FCSTD DOCUMENT  (FreeCAD 0.18R16110 (Git))
Label: minitomic_acrylic
License: All rights reserved
LicenseURL: http://en.wikipedia.org/wiki/All_rights_reserved
objects: Part::Part2DObjectPython×1454, App::DocumentObjectGroup×170, Part::Feature×140
note: 1594 computed .brp shape members not serialized (recipe doc carries the construction recipe); baked Part::Feature solids carry a one-line shape summary decoded from their .brp

FEATURE [Part::Feature] Path
  Placement = pos=(-11.0001,7.00006,0) rot=(0,0,1;0rad)
  shape: bbox 261 x 90 x 2e-07 mm, 0 faces, 0 solids (baked)
FEATURE [Part::Feature] Path001 .. Path007  x7 (patterned run collapsed; names and placements below)
  shape: bbox 3.572 x 3.572 x 2e-07 mm, 0 faces, 0 solids (baked)
  placements: all 7 at pos=(-11.0001,7.00006,0) rot=(0,0,1;0rad)
FEATURE [Part::Feature] Path008
  Placement = pos=(-11.0001,7.00006,0) rot=(0,0,1;0rad)
  shape: bbox 265 x 94 x 2e-07 mm, 0 faces, 0 solids (baked)
FEATURE [Part::Feature] Path009 .. Path015  x7 (patterned run collapsed; names and placements below)
  shape: bbox 4.106 x 4.106 x 2e-07 mm, 0 faces, 0 solids (baked)
  placements: all 7 at pos=(-11.0001,7.00006,0) rot=(0,0,1;0rad)
FEATURE [Part::Feature] Path016
  Placement = pos=(-11.0001,7.00006,0) rot=(0,0,1;0rad)
  shape: bbox 269 x 98 x 2e-07 mm, 0 faces, 0 solids (baked)
FEATURE [Part::Feature] Path017 .. Path028  x12 (patterned run collapsed; names and placements below)
  shape: bbox 14 x 14 x 2e-07 mm, 0 faces, 0 solids (baked)
  placements: all 12 at pos=(-11.0001,7.00006,0) rot=(0,0,1;0rad)
FEATURE [Part::Feature] Path029
  Placement = pos=(-11.0001,7.00006,0) rot=(0,0,1;0rad)
  shape: bbox 3.572 x 3.572 x 2e-07 mm, 0 faces, 0 solids (baked)
FEATURE [Part::Feature] Path030 .. Path041  x12 (patterned run collapsed; names and placements below)
  shape: bbox 14 x 14 x 2e-07 mm, 0 faces, 0 solids (baked)
  placements: all 12 at pos=(-11.0001,7.00006,0) rot=(0,0,1;0rad)
FEATURE [Part::Feature] Path042
  Placement = pos=(-11.0001,7.00006,0) rot=(0,0,1;0rad)
  shape: bbox 3.572 x 3.572 x 2e-07 mm, 0 faces, 0 solids (baked)
FEATURE [Part::Feature] Path043
  Placement = pos=(-11.0001,7.00006,0) rot=(0,0,1;0rad)
  shape: bbox 14 x 14 x 2e-07 mm, 0 faces, 0 solids (baked)
FEATURE [Part::Feature] Path044
  Placement = pos=(-11.0001,7.00006,0) rot=(0,0,1;0rad)
  shape: bbox 14 x 14 x 2e-07 mm, 0 faces, 0 solids (baked)
FEATURE [Part::Feature] Path045
  Placement = pos=(-11.0001,7.00006,0) rot=(0,0,1;0rad)
  shape: bbox 3.572 x 3.572 x 2e-07 mm, 0 faces, 0 solids (baked)
FEATURE [Part::Feature] Path046
  Placement = pos=(-11.0001,7.00006,0) rot=(0,0,1;0rad)
  shape: bbox 3.572 x 3.572 x 2e-07 mm, 0 faces, 0 solids (baked)
FEATURE [Part::Feature] Path047
  Placement = pos=(-11.0001,7.00006,0) rot=(0,0,1;0rad)
  shape: bbox 14 x 14 x 2e-07 mm, 0 faces, 0 solids (baked)
FEATURE [Part::Feature] Path048
  Placement = pos=(-11.0001,7.00006,0) rot=(0,0,1;0rad)
  shape: bbox 14 x 14 x 2e-07 mm, 0 faces, 0 solids (baked)
FEATURE [Part::Feature] Path049
  Placement = pos=(-11.0001,7.00006,0) rot=(0,0,1;0rad)
  shape: bbox 14 x 14 x 2e-07 mm, 0 faces, 0 solids (baked)
FEATURE [Part::Feature] Path050
  Placement = pos=(-11.0001,7.00006,0) rot=(0,0,1;0rad)
  shape: bbox 4 x 1.976 x 2e-07 mm, 0 faces, 0 solids (baked)
FEATURE [Part::Feature] Path051
  Placement = pos=(-11.0001,7.00006,0) rot=(0,0,1;0rad)
  shape: bbox 6 x 9 x 2e-07 mm, 0 faces, 0 solids (baked)
FEATURE [Part::Feature] Path052
  Placement = pos=(-11.0001,7.00006,0) rot=(0,0,1;0rad)
  shape: bbox 14 x 14 x 2e-07 mm, 0 faces, 0 solids (baked)
FEATURE [Part::Feature] Path053
  Placement = pos=(-11.0001,7.00006,0) rot=(0,0,1;0rad)
  shape: bbox 14 x 14 x 2e-07 mm, 0 faces, 0 solids (baked)
FEATURE [Part::Feature] Path054
  Placement = pos=(-11.0001,7.00006,0) rot=(0,0,1;0rad)
  shape: bbox 16.38 x 14 x 2e-07 mm, 0 faces, 0 solids (baked)
FEATURE [Part::Feature] Path055
  Placement = pos=(-11.0001,7.00006,0) rot=(0,0,1;0rad)
  shape: bbox 14 x 14 x 2e-07 mm, 0 faces, 0 solids (baked)
FEATURE [Part::Feature] Path056
  Placement = pos=(-11.0001,7.00006,0) rot=(0,0,1;0rad)
  shape: bbox 40.12 x 20.2 x 2e-07 mm, 0 faces, 0 solids (baked)
FEATURE [Part::Feature] Path057
  Placement = pos=(-11.0001,7.00006,0) rot=(0,0,1;0rad)
  shape: bbox 14 x 14 x 2e-07 mm, 0 faces, 0 solids (baked)
FEATURE [Part::Feature] Path058
  Placement = pos=(-11.0001,7.00006,0) rot=(0,0,1;0rad)
  shape: bbox 3.572 x 3.572 x 2e-07 mm, 0 faces, 0 solids (baked)
FEATURE [Part::Feature] Path059
  Placement = pos=(-11.0001,7.00006,0) rot=(0,0,1;0rad)
  shape: bbox 33.83 x 20.2 x 2e-07 mm, 0 faces, 0 solids (baked)
FEATURE [Part::Feature] Path060
  Placement = pos=(-11.0001,7.00006,0) rot=(0,0,1;0rad)
  shape: bbox 42.5 x 14 x 2e-07 mm, 0 faces, 0 solids (baked)
FEATURE [Part::Feature] Path061
  Placement = pos=(-11.0001,7.00006,0) rot=(0,0,1;0rad)
  shape: bbox 14 x 14 x 2e-07 mm, 0 faces, 0 solids (baked)
FEATURE [Part::Feature] Path062
  Placement = pos=(-11.0001,7.00006,0) rot=(0,0,1;0rad)
  shape: bbox 16.38 x 14 x 2e-07 mm, 0 faces, 0 solids (baked)
FEATURE [Part::Feature] Path063
  Placement = pos=(-11.0001,7.00006,0) rot=(0,0,1;0rad)
  shape: bbox 16.38 x 14 x 2e-07 mm, 0 faces, 0 solids (baked)
FEATURE [Part::Feature] Path064
  Placement = pos=(-11.0001,7.00006,0) rot=(0,0,1;0rad)
  shape: bbox 14 x 14 x 2e-07 mm, 0 faces, 0 solids (baked)
FEATURE [Part::Feature] Path065
  Placement = pos=(-11.0001,7.00006,0) rot=(0,0,1;0rad)
  shape: bbox 14 x 14 x 2e-07 mm, 0 faces, 0 solids (baked)
FEATURE [Part::Feature] Path066
  Placement = pos=(-11.0001,7.00006,0) rot=(0,0,1;0rad)
  shape: bbox 16.38 x 14 x 2e-07 mm, 0 faces, 0 solids (baked)
FEATURE [Part::Feature] Path067
  Placement = pos=(-11.0001,7.00006,0) rot=(0,0,1;0rad)
  shape: bbox 33.03 x 20.2 x 2e-07 mm, 0 faces, 0 solids (baked)
FEATURE [Part::Feature] Path068
  Placement = pos=(-11.0001,7.00006,0) rot=(0,0,1;0rad)
  shape: bbox 3.572 x 3.572 x 2e-07 mm, 0 faces, 0 solids (baked)
FEATURE [Part::Feature] Path069
  Placement = pos=(-11.0001,7.00006,0) rot=(0,0,1;0rad)
  shape: bbox 3.572 x 3.572 x 2e-07 mm, 0 faces, 0 solids (baked)
FEATURE [Part::Feature] Path070
  Placement = pos=(-11.0001,7.00006,0) rot=(0,0,1;0rad)
  shape: bbox 269 x 98 x 2e-07 mm, 0 faces, 0 solids (baked)
FEATURE [Part::Feature] Path071 .. Path083  x13 (patterned run collapsed; names and placements below)
  shape: bbox 14 x 14 x 2e-07 mm, 0 faces, 0 solids (baked)
  placements: all 13 at pos=(-11.0001,7.00006,0) rot=(0,0,1;0rad)
FEATURE [Part::Feature] Path084
  Placement = pos=(-11.0001,7.00006,0) rot=(0,0,1;0rad)
  shape: bbox 3.572 x 3.572 x 2e-07 mm, 0 faces, 0 solids (baked)
FEATURE [Part::Feature] Path085 .. Path098  x14 (patterned run collapsed; names and placements below)
  shape: bbox 14 x 14 x 2e-07 mm, 0 faces, 0 solids (baked)
  placements: all 14 at pos=(-11.0001,7.00006,0) rot=(0,0,1;0rad)
FEATURE [Part::Feature] Path099
  Placement = pos=(-11.0001,7.00006,0) rot=(0,0,1;0rad)
  shape: bbox 3.572 x 3.572 x 2e-07 mm, 0 faces, 0 solids (baked)
FEATURE [Part::Feature] Path100
  Placement = pos=(-11.0001,7.00006,0) rot=(0,0,1;0rad)
  shape: bbox 14 x 14 x 2e-07 mm, 0 faces, 0 solids (baked)
FEATURE [Part::Feature] Path101
  Placement = pos=(-11.0001,7.00006,0) rot=(0,0,1;0rad)
  shape: bbox 14 x 14 x 2e-07 mm, 0 faces, 0 solids (baked)
FEATURE [Part::Feature] Path102
  Placement = pos=(-11.0001,7.00006,0) rot=(0,0,1;0rad)
  shape: bbox 3.572 x 3.572 x 2e-07 mm, 0 faces, 0 solids (baked)
FEATURE [Part::Feature] Path103
  Placement = pos=(-11.0001,7.00006,0) rot=(0,0,1;0rad)
  shape: bbox 3.572 x 3.572 x 2e-07 mm, 0 faces, 0 solids (baked)
FEATURE [Part::Feature] Path104
  Placement = pos=(-11.0001,7.00006,0) rot=(0,0,1;0rad)
  shape: bbox 14 x 14 x 2e-07 mm, 0 faces, 0 solids (baked)
FEATURE [Part::Feature] Path105
  Placement = pos=(-11.0001,7.00006,0) rot=(0,0,1;0rad)
  shape: bbox 14 x 14 x 2e-07 mm, 0 faces, 0 solids (baked)
FEATURE [Part::Feature] Path106
  Placement = pos=(-11.0001,7.00006,0) rot=(0,0,1;0rad)
  shape: bbox 14 x 14 x 2e-07 mm, 0 faces, 0 solids (baked)
FEATURE [Part::Feature] Path107
  Placement = pos=(-11.0001,7.00006,0) rot=(0,0,1;0rad)
  shape: bbox 4 x 1.976 x 2e-07 mm, 0 faces, 0 solids (baked)
FEATURE [Part::Feature] Path108
  Placement = pos=(-11.0001,7.00006,0) rot=(0,0,1;0rad)
  shape: bbox 6 x 9 x 2e-07 mm, 0 faces, 0 solids (baked)
FEATURE [Part::Feature] Path109
  Placement = pos=(-11.0001,7.00006,0) rot=(0,0,1;0rad)
  shape: bbox 14 x 14 x 2e-07 mm, 0 faces, 0 solids (baked)
FEATURE [Part::Feature] Path110
  Placement = pos=(-11.0001,7.00006,0) rot=(0,0,1;0rad)
  shape: bbox 16.38 x 14 x 2e-07 mm, 0 faces, 0 solids (baked)
FEATURE [Part::Feature] Path111
  Placement = pos=(-11.0001,7.00006,0) rot=(0,0,1;0rad)
  shape: bbox 3.572 x 3.572 x 2e-07 mm, 0 faces, 0 solids (baked)
FEATURE [Part::Feature] Path112
  Placement = pos=(-11.0001,7.00006,0) rot=(0,0,1;0rad)
  shape: bbox 129.6 x 20.2 x 2e-07 mm, 0 faces, 0 solids (baked)
FEATURE [Part::Feature] Path113
  Placement = pos=(-11.0001,7.00006,0) rot=(0,0,1;0rad)
  shape: bbox 14 x 14 x 2e-07 mm, 0 faces, 0 solids (baked)
FEATURE [Part::Feature] Path114
  Placement = pos=(-11.0001,7.00006,0) rot=(0,0,1;0rad)
  shape: bbox 14 x 14 x 2e-07 mm, 0 faces, 0 solids (baked)
FEATURE [Part::Feature] Path115
  Placement = pos=(-11.0001,7.00006,0) rot=(0,0,1;0rad)
  shape: bbox 16.38 x 14 x 2e-07 mm, 0 faces, 0 solids (baked)
FEATURE [Part::Feature] Path116
  Placement = pos=(-11.0001,7.00006,0) rot=(0,0,1;0rad)
  shape: bbox 14 x 14 x 2e-07 mm, 0 faces, 0 solids (baked)
FEATURE [Part::Feature] Path117
  Placement = pos=(-11.0001,7.00006,0) rot=(0,0,1;0rad)
  shape: bbox 14 x 14 x 2e-07 mm, 0 faces, 0 solids (baked)
FEATURE [Part::Feature] Path118
  Placement = pos=(-11.0001,7.00006,0) rot=(0,0,1;0rad)
  shape: bbox 16.38 x 14 x 2e-07 mm, 0 faces, 0 solids (baked)
FEATURE [Part::Feature] Path119
  Placement = pos=(-11.0001,7.00006,0) rot=(0,0,1;0rad)
  shape: bbox 33.03 x 20.2 x 2e-07 mm, 0 faces, 0 solids (baked)
FEATURE [Part::Feature] Path120
  Placement = pos=(-11.0001,7.00006,0) rot=(0,0,1;0rad)
  shape: bbox 3.572 x 3.572 x 2e-07 mm, 0 faces, 0 solids (baked)
FEATURE [Part::Feature] Path121
  Placement = pos=(-11.0001,7.00006,0) rot=(0,0,1;0rad)
  shape: bbox 3.572 x 3.572 x 2e-07 mm, 0 faces, 0 solids (baked)
FEATURE [Part::Feature] Path122
  Placement = pos=(-11.0001,7.00006,0) rot=(0,0,1;0rad)
  shape: bbox 265 x 94 x 2e-07 mm, 0 faces, 0 solids (baked)
FEATURE [Part::Feature] Path123 .. Path127  x5 (patterned run collapsed; names and placements below)
  shape: bbox 3.572 x 3.572 x 2e-07 mm, 0 faces, 0 solids (baked)
  placements: all 5 at pos=(-11.0001,7.00006,0) rot=(0,0,1;0rad)
FEATURE [Part::Feature] Path128
  Placement = pos=(-11.0001,7.00006,0) rot=(0,0,1;0rad)
  shape: bbox 249 x 78 x 2e-07 mm, 0 faces, 0 solids (baked)
FEATURE [Part::Feature] Path129
  Placement = pos=(-11.0001,7.00006,0) rot=(0,0,1;0rad)
  shape: bbox 3.572 x 3.572 x 2e-07 mm, 0 faces, 0 solids (baked)
FEATURE [Part::Feature] Path130
  Placement = pos=(-11.0001,7.00006,0) rot=(0,0,1;0rad)
  shape: bbox 3.572 x 3.572 x 2e-07 mm, 0 faces, 0 solids (baked)
FEATURE [Part::Feature] Path132
  Placement = pos=(-11.0001,7.00006,0) rot=(0,0,1;0rad)
  shape: bbox 3.572 x 3.572 x 2e-07 mm, 0 faces, 0 solids (baked)
FEATURE [Part::Feature] Path133
  Placement = pos=(-11.0001,7.00006,0) rot=(0,0,1;0rad)
  shape: bbox 3.572 x 3.572 x 2e-07 mm, 0 faces, 0 solids (baked)
FEATURE [Part::Feature] Path134
  Placement = pos=(-11.0001,7.00006,0) rot=(0,0,1;0rad)
  shape: bbox 3.572 x 3.572 x 2e-07 mm, 0 faces, 0 solids (baked)
FEATURE [Part::Feature] Path136
  Placement = pos=(-11.0001,7.00006,0) rot=(0,0,1;0rad)
  shape: bbox 3.572 x 3.572 x 2e-07 mm, 0 faces, 0 solids (baked)
FEATURE [Part::Feature] Path137
  Placement = pos=(-11.0001,7.00006,0) rot=(0,0,1;0rad)
  shape: bbox 249 x 78 x 2e-07 mm, 0 faces, 0 solids (baked)
FEATURE [Part::Feature] Path138
  Placement = pos=(-11.0001,7.00006,0) rot=(0,0,1;0rad)
  shape: bbox 3.572 x 3.572 x 2e-07 mm, 0 faces, 0 solids (baked)
FEATURE [Part::Feature] Path139
  Placement = pos=(-11.0001,7.00006,0) rot=(0,0,1;0rad)
  shape: bbox 3.572 x 3.572 x 2e-07 mm, 0 faces, 0 solids (baked)
FEATURE [Part::Feature] Path131
  Placement = pos=(-11.0001,7.00006,0) rot=(0,0,1;0rad)
  shape: bbox 261 x 90 x 2e-07 mm, 0 faces, 0 solids (baked)
FEATURE [Part::Feature] Path135
  Placement = pos=(-11.0001,7.00006,0) rot=(0,0,1;0rad)
  shape: bbox 3.572 x 3.572 x 2e-07 mm, 0 faces, 0 solids (baked)
FEATURE [App::DocumentObjectGroup] Group
  Group = -> [Path,Path001,Path002,Path003,Path004,Path005,Path006,Path007,Path008,Path009,Path010,Path011,Path012,Path013,Path014,Path015,Path016,Path017,Path018,Path019,Path020,Path021,Path022,Path023,Path024,Path025,Path026,Path027,Path028,Path029,Path030,Path031,Path032,Path033,Path034,Path035,Path036,Path037,Path038,Path039,Path040,Path041,Path042,Path043,Path044,Path045,Path046,Path047,Path048,Path049,+90 more]
FEATURE [Part::Part2DObjectPython] Arc  # Draft 2D object (typed FeaturePython)
  FirstAngle = 90
  LastAngle = 180
  MakeFace = true
  Placement = pos=(-0.5,0.5,0) rot=(0,0,1;0rad)
  Radius = 0.5
FEATURE [Part::Part2DObjectPython] Arc001  # Draft 2D object (typed FeaturePython)
  FirstAngle = 0
  LastAngle = 90
  MakeFace = true
  Placement = pos=(247.5,0.5,0) rot=(0,0,1;0rad)
  Radius = 0.5
FEATURE [Part::Part2DObjectPython] Arc002  # Draft 2D object (typed FeaturePython)
  FirstAngle = 0
  LastAngle = 90
  MakeFace = true
  Placement = pos=(-0.5,-76.5,0) rot=(0,0,1;3.14159rad)
  Radius = 0.5
FEATURE [Part::Part2DObjectPython] Arc003  # Draft 2D object (typed FeaturePython)
  FirstAngle = 90
  LastAngle = 180
  MakeFace = true
  Placement = pos=(247.5,-76.5,0) rot=(0,0,1;3.14159rad)
  Radius = 0.5
FEATURE [Part::Part2DObjectPython] Line008  # Draft 2D object (typed FeaturePython)
  ChamferSize = 0
  Closed = false
  End = (248,0.5,0)
  FilletRadius = 0
  Length = 77
  MakeFace = true
  Placement = pos=(248,-76.5,0) rot=(0,0,1;0rad)
  Points = (2) [(0,0,0),(0,77,0)]
  Start = (248,-76.5,0)
  Subdivisions = 0
FEATURE [Part::Part2DObjectPython] Line009  # Draft 2D object (typed FeaturePython)
  ChamferSize = 0
  Closed = false
  End = (-0.5,1,0)
  FilletRadius = 0
  Length = 248
  MakeFace = true
  Placement = pos=(247.5,1,0) rot=(0,0,1;0rad)
  Points = (2) [(0,0,0),(-248,0,0)]
  Start = (247.5,1,0)
  Subdivisions = 0
FEATURE [Part::Part2DObjectPython] Line010  # Draft 2D object (typed FeaturePython)
  ChamferSize = 0
  Closed = false
  End = (-1,-76.5,0)
  FilletRadius = 0
  Length = 77
  MakeFace = true
  Placement = pos=(-1,0.5,0) rot=(0,0,1;0rad)
  Points = (2) [(0,0,0),(0,-77,0)]
  Start = (-1,0.5,0)
  Subdivisions = 0
FEATURE [Part::Part2DObjectPython] Line011  # Draft 2D object (typed FeaturePython)
  ChamferSize = 0
  Closed = false
  End = (247.5,-77,0)
  FilletRadius = 0
  Length = 248
  MakeFace = true
  Placement = pos=(-0.5,-77,0) rot=(0,0,1;0rad)
  Points = (2) [(0,0,0),(248,-2.84217e-14,0)]
  Start = (-0.5,-77,0)
  Subdivisions = 0
FEATURE [Part::Part2DObjectPython] Arc004  # Draft 2D object (typed FeaturePython)
  FirstAngle = 90
  LastAngle = 180
  MakeFace = true
  Placement = pos=(-4,4,0) rot=(0,0,1;0rad)
  Radius = 3
FEATURE [Part::Part2DObjectPython] Arc005  # Draft 2D object (typed FeaturePython)
  FirstAngle = 0
  LastAngle = 90
  MakeFace = true
  Placement = pos=(251,4,0) rot=(0,0,1;0rad)
  Radius = 3
FEATURE [Part::Part2DObjectPython] Arc006  # Draft 2D object (typed FeaturePython)
  FirstAngle = 0
  LastAngle = 90
  MakeFace = true
  Placement = pos=(-4,-80,0) rot=(0,0,1;3.14159rad)
  Radius = 3
FEATURE [Part::Part2DObjectPython] Arc007  # Draft 2D object (typed FeaturePython)
  FirstAngle = 90
  LastAngle = 180
  MakeFace = true
  Placement = pos=(251,-80,0) rot=(0,0,1;3.14159rad)
  Radius = 3
FEATURE [Part::Part2DObjectPython] Line020  # Draft 2D object (typed FeaturePython)
  ChamferSize = 0
  Closed = false
  End = (251,7,0)
  FilletRadius = 0
  Length = 255
  MakeFace = true
  Placement = pos=(-4,7,0) rot=(0,0,1;0rad)
  Points = (2) [(0,0,0),(255,0,0)]
  Start = (-4,7,0)
  Subdivisions = 0
FEATURE [Part::Part2DObjectPython] Line021  # Draft 2D object (typed FeaturePython)
  ChamferSize = 0
  Closed = false
  End = (254,-80,0)
  FilletRadius = 0
  Length = 84
  MakeFace = true
  Placement = pos=(254,4,0) rot=(0,0,1;0rad)
  Points = (2) [(0,0,0),(0,-84,0)]
  Start = (254,4,0)
  Subdivisions = 0
FEATURE [Part::Part2DObjectPython] Line022  # Draft 2D object (typed FeaturePython)
  ChamferSize = 0
  Closed = false
  End = (-4,-83,0)
  FilletRadius = 0
  Length = 255
  MakeFace = true
  Placement = pos=(251,-83,0) rot=(0,0,1;0rad)
  Points = (2) [(0,0,0),(-255,2.84217e-14,0)]
  Start = (251,-83,0)
  Subdivisions = 0
FEATURE [Part::Part2DObjectPython] Line023  # Draft 2D object (typed FeaturePython)
  ChamferSize = 0
  Closed = false
  End = (-7,4,0)
  FilletRadius = 0
  Length = 84
  MakeFace = true
  Placement = pos=(-7,-80,0) rot=(0,0,1;0rad)
  Points = (2) [(0,0,0),(0,84,0)]
  Start = (-7,-80,0)
  Subdivisions = 0
FEATURE [Part::Part2DObjectPython] Circle  # Draft 2D object (typed FeaturePython)
  FirstAngle = 0
  LastAngle = 0
  MakeFace = false
  Placement = pos=(-3.48744,3.48744,0) rot=(0,0,1;0rad)
  Radius = 1.6
FEATURE [Part::Part2DObjectPython] Circle001  # Draft 2D object (typed FeaturePython)
  FirstAngle = 0
  LastAngle = 0
  MakeFace = false
  Placement = pos=(-3.48744,-79.4874,0) rot=(0,0,1;0rad)
  Radius = 1.6
FEATURE [Part::Part2DObjectPython] Circle002  # Draft 2D object (typed FeaturePython)
  FirstAngle = 0
  LastAngle = 0
  MakeFace = false
  Placement = pos=(250.487,-79.4874,0) rot=(0,0,1;0rad)
  Radius = 1.6
FEATURE [Part::Part2DObjectPython] Circle003  # Draft 2D object (typed FeaturePython)
  FirstAngle = 0
  LastAngle = 0
  MakeFace = false
  Placement = pos=(250.487,3.48744,0) rot=(0,0,1;0rad)
  Radius = 1.6
FEATURE [Part::Part2DObjectPython] Circle004  # Draft 2D object (typed FeaturePython)
  FirstAngle = 0
  LastAngle = 0
  MakeFace = false
  Placement = pos=(123.5,4,0) rot=(0,0,1;0rad)
  Radius = 1.6
FEATURE [Part::Part2DObjectPython] Circle005  # Draft 2D object (typed FeaturePython)
  FirstAngle = 0
  LastAngle = 0
  MakeFace = false
  Placement = pos=(123.5,-80,0) rot=(0,0,1;0rad)
  Radius = 1.6
FEATURE [Part::Part2DObjectPython] Line025  # Draft 2D object (typed FeaturePython)
  ChamferSize = 0
  Closed = false
  End = (22.69,1.1875,0)
  FilletRadius = 0
  Length = 8.65
  MakeFace = false
  Placement = pos=(14.04,1.1875,0) rot=(0,0,1;0rad)
  Points = (2) [(0,0,0),(8.65,0,0)]
  Start = (14.04,1.1875,0)
  Subdivisions = 0
FEATURE [Part::Part2DObjectPython] Line026  # Draft 2D object (typed FeaturePython)
  ChamferSize = 0
  Closed = false
  End = (14.04,-6.1125,0)
  FilletRadius = 0
  Length = 7.3
  MakeFace = false
  Placement = pos=(14.04,1.1875,0) rot=(0,0,1;0rad)
  Points = (2) [(0,0,0),(0,-7.3,0)]
  Start = (14.04,1.1875,0)
  Subdivisions = 0
FEATURE [Part::Part2DObjectPython] Line027  # Draft 2D object (typed FeaturePython)
  ChamferSize = 0
  Closed = false
  End = (22.69,-6.1125,0)
  FilletRadius = 0
  Length = 7.3
  MakeFace = false
  Placement = pos=(22.69,1.1875,0) rot=(0,0,1;0rad)
  Points = (2) [(0,0,0),(0,-7.3,0)]
  Start = (22.69,1.1875,0)
  Subdivisions = 0
FEATURE [Part::Part2DObjectPython] Line028  # Draft 2D object (typed FeaturePython)
  ChamferSize = 0
  Closed = false
  End = (22.69,-6.1125,0)
  FilletRadius = 0
  Length = 8.65
  MakeFace = false
  Placement = pos=(14.04,-6.1125,0) rot=(0,0,1;0rad)
  Points = (2) [(0,0,0),(8.65,0,0)]
  Start = (14.04,-6.1125,0)
  Subdivisions = 0
FEATURE [Part::Part2DObjectPython] Circle006  # Draft 2D object (typed FeaturePython)
  FirstAngle = 0
  LastAngle = 0
  MakeFace = false
  Placement = pos=(31,4,0) rot=(0,0,1;0rad)
  Radius = 1.6
FEATURE [App::DocumentObjectGroup] Group001  label="Screws"
  Group = -> [Circle,Circle001,Circle002,Circle003,Circle004,Circle005,Circle006]
FEATURE [App::DocumentObjectGroup] Group002  label="Inside base"
  Group = -> [Arc,Arc001,Arc002,Arc003,Line008,Line009,Line010,Line011]
FEATURE [App::DocumentObjectGroup] Group003  label="USB"
  Group = -> [Line028,Line026,Line027,Line025]
FEATURE [Part::Part2DObjectPython] Arc008  # Draft 2D object (typed FeaturePython)
  FirstAngle = 90
  LastAngle = 180
  MakeFace = false
  Placement = pos=(-4,4,0) rot=(0,0,1;0rad)
  Radius = 5
FEATURE [Part::Part2DObjectPython] Arc009  # Draft 2D object (typed FeaturePython)
  FirstAngle = 0
  LastAngle = 90
  MakeFace = false
  Placement = pos=(251,4,0) rot=(0,0,1;0rad)
  Radius = 5
FEATURE [Part::Part2DObjectPython] Arc010  # Draft 2D object (typed FeaturePython)
  FirstAngle = -90
  LastAngle = 0
  MakeFace = false
  Placement = pos=(251,-80,0) rot=(0,0,1;0rad)
  Radius = 5
FEATURE [Part::Part2DObjectPython] Arc011  # Draft 2D object (typed FeaturePython)
  FirstAngle = -180
  LastAngle = -90
  MakeFace = false
  Placement = pos=(-4,-80,0) rot=(0,0,1;0rad)
  Radius = 5
FEATURE [Part::Part2DObjectPython] Line  # Draft 2D object (typed FeaturePython)
  ChamferSize = 0
  Closed = false
  End = (251,9,0)
  FilletRadius = 0
  Length = 255
  MakeFace = false
  Placement = pos=(-4,9,0) rot=(0,0,1;0rad)
  Points = (2) [(0,0,0),(255,0,0)]
  Start = (-4,9,0)
  Subdivisions = 0
FEATURE [Part::Part2DObjectPython] Line029  # Draft 2D object (typed FeaturePython)
  ChamferSize = 0
  Closed = false
  End = (256,-80,0)
  FilletRadius = 0
  Length = 84
  MakeFace = false
  Placement = pos=(256,4,0) rot=(0,0,1;0rad)
  Points = (2) [(0,0,0),(0,-84,0)]
  Start = (256,4,0)
  Subdivisions = 0
FEATURE [Part::Part2DObjectPython] Line030  # Draft 2D object (typed FeaturePython)
  ChamferSize = 0
  Closed = false
  End = (-4,-85,0)
  FilletRadius = 0
  Length = 255
  MakeFace = false
  Placement = pos=(251,-85,0) rot=(0,0,1;0rad)
  Points = (2) [(0,0,0),(-255,0,0)]
  Start = (251,-85,0)
  Subdivisions = 0
FEATURE [Part::Part2DObjectPython] Line031  # Draft 2D object (typed FeaturePython)
  ChamferSize = 0
  Closed = false
  End = (-9,4,0)
  FilletRadius = 0
  Length = 84
  MakeFace = false
  Placement = pos=(-9,-80,0) rot=(0,0,1;0rad)
  Points = (2) [(0,0,0),(0,84,0)]
  Start = (-9,-80,0)
  Subdivisions = 0
FEATURE [App::DocumentObjectGroup] Group004  label="Top layer 3mm"
  Group = -> [Arc004,Arc005,Arc006,Arc007,Line020,Line021,Line022,Line023]
FEATURE [App::DocumentObjectGroup] Group005  label="Top-switch layer 5mm"
  Group = -> [Arc008,Arc009,Arc010,Arc011,Line,Line029,Line030,Line031]
FEATURE [Part::Part2DObjectPython] Arc012  # Draft 2D object (typed FeaturePython)
  FirstAngle = 90
  LastAngle = 180
  MakeFace = false
  Placement = pos=(-4,4,0) rot=(0,0,1;0rad)
  Radius = 7.00001
FEATURE [Part::Part2DObjectPython] Arc013  # Draft 2D object (typed FeaturePython)
  FirstAngle = 0
  LastAngle = 90
  MakeFace = false
  Placement = pos=(251,4,0) rot=(0,0,1;0rad)
  Radius = 7.00001
FEATURE [Part::Part2DObjectPython] Arc014  # Draft 2D object (typed FeaturePython)
  FirstAngle = 0
  LastAngle = 90
  MakeFace = false
  Placement = pos=(-4,-80,0) rot=(0,0,1;3.14159rad)
  Radius = 7.00001
FEATURE [Part::Part2DObjectPython] Arc015  # Draft 2D object (typed FeaturePython)
  FirstAngle = 90
  LastAngle = 180
  MakeFace = false
  Placement = pos=(251,-80,0) rot=(0,0,1;3.14159rad)
  Radius = 7.00001
FEATURE [Part::Part2DObjectPython] Line032  # Draft 2D object (typed FeaturePython)
  ChamferSize = 0
  Closed = false
  End = (251,11,0)
  FilletRadius = 0
  Length = 255
  MakeFace = false
  Placement = pos=(-4,11,0) rot=(0,0,1;0rad)
  Points = (2) [(0,0,0),(255,0,0)]
  Start = (-4,11,0)
  Subdivisions = 0
FEATURE [Part::Part2DObjectPython] Line033  # Draft 2D object (typed FeaturePython)
  ChamferSize = 0
  Closed = false
  End = (258,-80,0)
  FilletRadius = 0
  Length = 84
  MakeFace = false
  Placement = pos=(258,4,0) rot=(0,0,1;0rad)
  Points = (2) [(0,0,0),(0,-84,0)]
  Start = (258,4,0)
  Subdivisions = 0
FEATURE [Part::Part2DObjectPython] Line034  # Draft 2D object (typed FeaturePython)
  ChamferSize = 0
  Closed = false
  End = (-4,-87,0)
  FilletRadius = 0
  Length = 255
  MakeFace = false
  Placement = pos=(251,-87,0) rot=(0,0,1;0rad)
  Points = (2) [(0,0,0),(-255,2.84217e-14,0)]
  Start = (251,-87,0)
  Subdivisions = 0
FEATURE [Part::Part2DObjectPython] Line035  # Draft 2D object (typed FeaturePython)
  ChamferSize = 0
  Closed = false
  End = (-11,4,0)
  FilletRadius = 0
  Length = 84
  MakeFace = false
  Placement = pos=(-11,-80,0) rot=(0,0,1;0rad)
  Points = (2) [(0,0,0),(0,84,0)]
  Start = (-11,-80,0)
  Subdivisions = 0
FEATURE [App::DocumentObjectGroup] Group007  label="Outside border"
  Group = -> [Arc012,Arc013,Arc014,Arc015,Line032,Line033,Line034,Line035]
FEATURE [Part::Part2DObjectPython] Line042  # Draft 2D object (typed FeaturePython)
  ChamferSize = 0
  Closed = false
  End = (16,-2.5,0)
  FilletRadius = 0
  Length = 13
  MakeFace = false
  Placement = pos=(3,-2.5,0) rot=(0,0,1;0rad)
  Points = (2) [(0,0,0),(13,0,0)]
  Start = (3,-2.5,0)
  Subdivisions = 0
FEATURE [Part::Part2DObjectPython] Arc016  # Draft 2D object (typed FeaturePython)
  FirstAngle = 0
  LastAngle = 90
  MakeFace = false
  Placement = pos=(16,-3,0) rot=(0,0,1;0rad)
  Radius = 0.5
FEATURE [Part::Part2DObjectPython] Arc017  # Draft 2D object (typed FeaturePython)
  FirstAngle = 90
  LastAngle = 180
  MakeFace = false
  Placement = pos=(3,-3,0) rot=(0,0,1;0rad)
  Radius = 0.5
FEATURE [Part::Part2DObjectPython] Line043  # Draft 2D object (typed FeaturePython)
  ChamferSize = 0
  Closed = false
  End = (2.5,-16,0)
  FilletRadius = 0
  Length = 13
  MakeFace = false
  Placement = pos=(2.5,-3,0) rot=(0,0,1;0rad)
  Points = (2) [(0,0,0),(0,-13,0)]
  Start = (2.5,-3,0)
  Subdivisions = 0
FEATURE [Part::Part2DObjectPython] Arc018  # Draft 2D object (typed FeaturePython)
  FirstAngle = 180
  LastAngle = 270
  MakeFace = false
  Placement = pos=(3,-16,0) rot=(0,0,1;0rad)
  Radius = 0.5
FEATURE [Part::Part2DObjectPython] Line044  # Draft 2D object (typed FeaturePython)
  ChamferSize = 0
  Closed = false
  End = (16,-16.5,0)
  FilletRadius = 0
  Length = 13
  MakeFace = false
  Placement = pos=(3,-16.5,0) rot=(0,0,1;0rad)
  Points = (2) [(0,0,0),(13,0,0)]
  Start = (3,-16.5,0)
  Subdivisions = 0
FEATURE [Part::Part2DObjectPython] Arc019  # Draft 2D object (typed FeaturePython)
  FirstAngle = -90
  LastAngle = 0
  MakeFace = false
  Placement = pos=(16,-16,0) rot=(0,0,1;0rad)
  Radius = 0.5
FEATURE [Part::Part2DObjectPython] Line045  # Draft 2D object (typed FeaturePython)
  ChamferSize = 0
  Closed = false
  End = (16.5,-3,0)
  FilletRadius = 0
  Length = 13
  MakeFace = false
  Placement = pos=(16.5,-16,0) rot=(0,0,1;0rad)
  Points = (2) [(0,0,0),(0,13,0)]
  Start = (16.5,-16,0)
  Subdivisions = 0
FEATURE [App::DocumentObjectGroup] Group010
  Group = -> [Line042,Arc016,Arc017,Line043,Arc018,Line044,Arc019,Line045]
FEATURE [Part::Part2DObjectPython] Line048  # Draft 2D object (typed FeaturePython)
  ChamferSize = 0
  Closed = false
  End = (35,-2.5,0)
  FilletRadius = 0
  Length = 13
  MakeFace = false
  Placement = pos=(22,-2.5,0) rot=(0,0,1;0rad)
  Points = (2) [(0,0,0),(13,0,0)]
  Start = (22,-2.5,0)
  Subdivisions = 0
FEATURE [Part::Part2DObjectPython] Arc020  # Draft 2D object (typed FeaturePython)
  FirstAngle = 0
  LastAngle = 90
  MakeFace = false
  Placement = pos=(35,-3,0) rot=(0,0,1;0rad)
  Radius = 0.5
FEATURE [Part::Part2DObjectPython] Arc021  # Draft 2D object (typed FeaturePython)
  FirstAngle = 90
  LastAngle = 180
  MakeFace = false
  Placement = pos=(22,-3,0) rot=(0,0,1;0rad)
  Radius = 0.5
FEATURE [Part::Part2DObjectPython] Line051  # Draft 2D object (typed FeaturePython)
  ChamferSize = 0
  Closed = false
  End = (21.5,-16,0)
  FilletRadius = 0
  Length = 13
  MakeFace = false
  Placement = pos=(21.5,-3,0) rot=(0,0,1;0rad)
  Points = (2) [(0,0,0),(0,-13,0)]
  Start = (21.5,-3,0)
  Subdivisions = 0
FEATURE [Part::Part2DObjectPython] Arc022  # Draft 2D object (typed FeaturePython)
  FirstAngle = 180
  LastAngle = 270
  MakeFace = false
  Placement = pos=(22,-16,0) rot=(0,0,1;0rad)
  Radius = 0.5
FEATURE [Part::Part2DObjectPython] Line052  # Draft 2D object (typed FeaturePython)
  ChamferSize = 0
  Closed = false
  End = (35,-16.5,0)
  FilletRadius = 0
  Length = 13
  MakeFace = false
  Placement = pos=(22,-16.5,0) rot=(0,0,1;0rad)
  Points = (2) [(0,0,0),(13,0,0)]
  Start = (22,-16.5,0)
  Subdivisions = 0
FEATURE [Part::Part2DObjectPython] Arc023  # Draft 2D object (typed FeaturePython)
  FirstAngle = -90
  LastAngle = 0
  MakeFace = false
  Placement = pos=(35,-16,0) rot=(0,0,1;0rad)
  Radius = 0.5
FEATURE [Part::Part2DObjectPython] Line053  # Draft 2D object (typed FeaturePython)
  ChamferSize = 0
  Closed = false
  End = (35.5,-3,0)
  FilletRadius = 0
  Length = 13
  MakeFace = false
  Placement = pos=(35.5,-16,0) rot=(0,0,1;0rad)
  Points = (2) [(0,0,0),(0,13,0)]
  Start = (35.5,-16,0)
  Subdivisions = 0
FEATURE [App::DocumentObjectGroup] Group011
  Group = -> [Line048,Arc020,Arc021,Line051,Arc022,Line052,Arc023,Line053]
FEATURE [Part::Part2DObjectPython] Arc024  # Draft 2D object (typed FeaturePython)
  FirstAngle = 90
  LastAngle = 180
  MakeFace = false
  Placement = pos=(41,-3,0) rot=(0,0,1;0rad)
  Radius = 0.5
FEATURE [Part::Part2DObjectPython] Line054  # Draft 2D object (typed FeaturePython)
  ChamferSize = 0
  Closed = false
  End = (40.5,-16,0)
  FilletRadius = 0
  Length = 13
  MakeFace = false
  Placement = pos=(40.5,-3,0) rot=(0,0,1;0rad)
  Points = (2) [(0,0,0),(0,-13,0)]
  Start = (40.5,-3,0)
  Subdivisions = 0
FEATURE [Part::Part2DObjectPython] Line055  # Draft 2D object (typed FeaturePython)
  ChamferSize = 0
  Closed = false
  End = (54,-2.5,0)
  FilletRadius = 0
  Length = 13
  MakeFace = false
  Placement = pos=(41,-2.5,0) rot=(0,0,1;0rad)
  Points = (2) [(0,0,0),(13,0,0)]
  Start = (41,-2.5,0)
  Subdivisions = 0
FEATURE [Part::Part2DObjectPython] Line057  # Draft 2D object (typed FeaturePython)
  ChamferSize = 0
  Closed = false
  End = (54,-16.5,0)
  FilletRadius = 0
  Length = 13
  MakeFace = false
  Placement = pos=(41,-16.5,0) rot=(0,0,1;0rad)
  Points = (2) [(0,0,0),(13,0,0)]
  Start = (41,-16.5,0)
  Subdivisions = 0
FEATURE [Part::Part2DObjectPython] Arc025  # Draft 2D object (typed FeaturePython)
  FirstAngle = 0
  LastAngle = 90
  MakeFace = false
  Placement = pos=(54,-3,0) rot=(0,0,1;0rad)
  Radius = 0.5
FEATURE [Part::Part2DObjectPython] Arc026  # Draft 2D object (typed FeaturePython)
  FirstAngle = -90
  LastAngle = 0
  MakeFace = false
  Placement = pos=(54,-16,0) rot=(0,0,1;0rad)
  Radius = 0.5
FEATURE [Part::Part2DObjectPython] Line059  # Draft 2D object (typed FeaturePython)
  ChamferSize = 0
  Closed = false
  End = (54.5,-3,0)
  FilletRadius = 0
  Length = 13
  MakeFace = false
  Placement = pos=(54.5,-16,0) rot=(0,0,1;0rad)
  Points = (2) [(0,0,0),(0,13,0)]
  Start = (54.5,-16,0)
  Subdivisions = 0
FEATURE [Part::Part2DObjectPython] Arc027  # Draft 2D object (typed FeaturePython)
  FirstAngle = 180
  LastAngle = 270
  MakeFace = false
  Placement = pos=(41,-16,0) rot=(0,0,1;0rad)
  Radius = 0.5
FEATURE [App::DocumentObjectGroup] Group012
  Group = -> [Line055,Arc025,Arc024,Line054,Arc027,Line057,Arc026,Line059]
FEATURE [Part::Part2DObjectPython] Arc028  # Draft 2D object (typed FeaturePython)
  FirstAngle = 180
  LastAngle = 270
  MakeFace = false
  Placement = pos=(60,-16,0) rot=(0,0,1;0rad)
  Radius = 0.5
FEATURE [Part::Part2DObjectPython] Arc029  # Draft 2D object (typed FeaturePython)
  FirstAngle = 0
  LastAngle = 90
  MakeFace = false
  Placement = pos=(73,-3,0) rot=(0,0,1;0rad)
  Radius = 0.5
FEATURE [Part::Part2DObjectPython] Arc030  # Draft 2D object (typed FeaturePython)
  FirstAngle = 90
  LastAngle = 180
  MakeFace = false
  Placement = pos=(60,-3,0) rot=(0,0,1;0rad)
  Radius = 0.5
FEATURE [Part::Part2DObjectPython] Line063  # Draft 2D object (typed FeaturePython)
  ChamferSize = 0
  Closed = false
  End = (73,-2.5,0)
  FilletRadius = 0
  Length = 13
  MakeFace = false
  Placement = pos=(60,-2.5,0) rot=(0,0,1;0rad)
  Points = (2) [(0,0,0),(13,0,0)]
  Start = (60,-2.5,0)
  Subdivisions = 0
FEATURE [Part::Part2DObjectPython] Arc031  # Draft 2D object (typed FeaturePython)
  FirstAngle = -90
  LastAngle = 0
  MakeFace = false
  Placement = pos=(73,-16,0) rot=(0,0,1;0rad)
  Radius = 0.5
FEATURE [Part::Part2DObjectPython] Line065  # Draft 2D object (typed FeaturePython)
  ChamferSize = 0
  Closed = false
  End = (59.5,-16,0)
  FilletRadius = 0
  Length = 13
  MakeFace = false
  Placement = pos=(59.5,-3,0) rot=(0,0,1;0rad)
  Points = (2) [(0,0,0),(0,-13,0)]
  Start = (59.5,-3,0)
  Subdivisions = 0
FEATURE [Part::Part2DObjectPython] Line066  # Draft 2D object (typed FeaturePython)
  ChamferSize = 0
  Closed = false
  End = (73,-16.5,0)
  FilletRadius = 0
  Length = 13
  MakeFace = false
  Placement = pos=(60,-16.5,0) rot=(0,0,1;0rad)
  Points = (2) [(0,0,0),(13,0,0)]
  Start = (60,-16.5,0)
  Subdivisions = 0
FEATURE [Part::Part2DObjectPython] Line067  # Draft 2D object (typed FeaturePython)
  ChamferSize = 0
  Closed = false
  End = (73.5,-3,0)
  FilletRadius = 0
  Length = 13
  MakeFace = false
  Placement = pos=(73.5,-16,0) rot=(0,0,1;0rad)
  Points = (2) [(0,0,0),(0,13,0)]
  Start = (73.5,-16,0)
  Subdivisions = 0
FEATURE [App::DocumentObjectGroup] Group013
  Group = -> [Line063,Arc029,Arc030,Line065,Arc028,Line066,Arc031,Line067]
FEATURE [Part::Part2DObjectPython] Arc032  # Draft 2D object (typed FeaturePython)
  FirstAngle = -90
  LastAngle = 0
  MakeFace = false
  Placement = pos=(92,-16,0) rot=(0,0,1;0rad)
  Radius = 0.5
FEATURE [Part::Part2DObjectPython] Arc033  # Draft 2D object (typed FeaturePython)
  FirstAngle = 180
  LastAngle = 270
  MakeFace = false
  Placement = pos=(79,-16,0) rot=(0,0,1;0rad)
  Radius = 0.5
FEATURE [Part::Part2DObjectPython] Arc034  # Draft 2D object (typed FeaturePython)
  FirstAngle = 0
  LastAngle = 90
  MakeFace = false
  Placement = pos=(92,-3,0) rot=(0,0,1;0rad)
  Radius = 0.5
FEATURE [Part::Part2DObjectPython] Arc035  # Draft 2D object (typed FeaturePython)
  FirstAngle = 90
  LastAngle = 180
  MakeFace = false
  Placement = pos=(79,-3,0) rot=(0,0,1;0rad)
  Radius = 0.5
FEATURE [Part::Part2DObjectPython] Line073  # Draft 2D object (typed FeaturePython)
  ChamferSize = 0
  Closed = false
  End = (92,-2.5,0)
  FilletRadius = 0
  Length = 13
  MakeFace = false
  Placement = pos=(79,-2.5,0) rot=(0,0,1;0rad)
  Points = (2) [(0,0,0),(13,0,0)]
  Start = (79,-2.5,0)
  Subdivisions = 0
FEATURE [Part::Part2DObjectPython] Line075  # Draft 2D object (typed FeaturePython)
  ChamferSize = 0
  Closed = false
  End = (78.5,-16,0)
  FilletRadius = 0
  Length = 13
  MakeFace = false
  Placement = pos=(78.5,-3,0) rot=(0,0,1;0rad)
  Points = (2) [(0,0,0),(0,-13,0)]
  Start = (78.5,-3,0)
  Subdivisions = 0
FEATURE [Part::Part2DObjectPython] Line076  # Draft 2D object (typed FeaturePython)
  ChamferSize = 0
  Closed = false
  End = (92,-16.5,0)
  FilletRadius = 0
  Length = 13
  MakeFace = false
  Placement = pos=(79,-16.5,0) rot=(0,0,1;0rad)
  Points = (2) [(0,0,0),(13,0,0)]
  Start = (79,-16.5,0)
  Subdivisions = 0
FEATURE [Part::Part2DObjectPython] Line077  # Draft 2D object (typed FeaturePython)
  ChamferSize = 0
  Closed = false
  End = (92.5,-3,0)
  FilletRadius = 0
  Length = 13
  MakeFace = false
  Placement = pos=(92.5,-16,0) rot=(0,0,1;0rad)
  Points = (2) [(0,0,0),(0,13,0)]
  Start = (92.5,-16,0)
  Subdivisions = 0
FEATURE [App::DocumentObjectGroup] Group014
  Group = -> [Line073,Arc034,Arc035,Line075,Arc033,Line076,Arc032,Line077]
FEATURE [Part::Part2DObjectPython] Line081  # Draft 2D object (typed FeaturePython)
  ChamferSize = 0
  Closed = false
  End = (97.5,-16,0)
  FilletRadius = 0
  Length = 13
  MakeFace = false
  Placement = pos=(97.5,-3,0) rot=(0,0,1;0rad)
  Points = (2) [(0,0,0),(0,-13,0)]
  Start = (97.5,-3,0)
  Subdivisions = 0
FEATURE [Part::Part2DObjectPython] Arc036  # Draft 2D object (typed FeaturePython)
  FirstAngle = 90
  LastAngle = 180
  MakeFace = false
  Placement = pos=(98,-3,0) rot=(0,0,1;0rad)
  Radius = 0.5
FEATURE [Part::Part2DObjectPython] Line082  # Draft 2D object (typed FeaturePython)
  ChamferSize = 0
  Closed = false
  End = (111.5,-3,0)
  FilletRadius = 0
  Length = 13
  MakeFace = false
  Placement = pos=(111.5,-16,0) rot=(0,0,1;0rad)
  Points = (2) [(0,0,0),(0,13,0)]
  Start = (111.5,-16,0)
  Subdivisions = 0
FEATURE [Part::Part2DObjectPython] Arc037  # Draft 2D object (typed FeaturePython)
  FirstAngle = -90
  LastAngle = 0
  MakeFace = false
  Placement = pos=(111,-16,0) rot=(0,0,1;0rad)
  Radius = 0.5
FEATURE [Part::Part2DObjectPython] Arc038  # Draft 2D object (typed FeaturePython)
  FirstAngle = 180
  LastAngle = 270
  MakeFace = false
  Placement = pos=(98,-16,0) rot=(0,0,1;0rad)
  Radius = 0.5
FEATURE [Part::Part2DObjectPython] Line084  # Draft 2D object (typed FeaturePython)
  ChamferSize = 0
  Closed = false
  End = (111,-2.5,0)
  FilletRadius = 0
  Length = 13
  MakeFace = false
  Placement = pos=(98,-2.5,0) rot=(0,0,1;0rad)
  Points = (2) [(0,0,0),(13,0,0)]
  Start = (98,-2.5,0)
  Subdivisions = 0
FEATURE [Part::Part2DObjectPython] Arc039  # Draft 2D object (typed FeaturePython)
  FirstAngle = 0
  LastAngle = 90
  MakeFace = false
  Placement = pos=(111,-3,0) rot=(0,0,1;0rad)
  Radius = 0.5
FEATURE [Part::Part2DObjectPython] Line085  # Draft 2D object (typed FeaturePython)
  ChamferSize = 0
  Closed = false
  End = (111,-16.5,0)
  FilletRadius = 0
  Length = 13
  MakeFace = false
  Placement = pos=(98,-16.5,0) rot=(0,0,1;0rad)
  Points = (2) [(0,0,0),(13,0,0)]
  Start = (98,-16.5,0)
  Subdivisions = 0
FEATURE [App::DocumentObjectGroup] Group015
  Group = -> [Line084,Arc039,Arc036,Line081,Arc038,Line085,Arc037,Line082]
FEATURE [Part::Part2DObjectPython] Arc040  # Draft 2D object (typed FeaturePython)
  FirstAngle = -90
  LastAngle = 0
  MakeFace = false
  Placement = pos=(130,-16,0) rot=(0,0,1;0rad)
  Radius = 0.5
FEATURE [Part::Part2DObjectPython] Arc041  # Draft 2D object (typed FeaturePython)
  FirstAngle = 180
  LastAngle = 270
  MakeFace = false
  Placement = pos=(117,-16,0) rot=(0,0,1;0rad)
  Radius = 0.5
FEATURE [Part::Part2DObjectPython] Line087  # Draft 2D object (typed FeaturePython)
  ChamferSize = 0
  Closed = false
  End = (116.5,-16,0)
  FilletRadius = 0
  Length = 13
  MakeFace = false
  Placement = pos=(116.5,-3,0) rot=(0,0,1;0rad)
  Points = (2) [(0,0,0),(0,-13,0)]
  Start = (116.5,-3,0)
  Subdivisions = 0
FEATURE [Part::Part2DObjectPython] Line088  # Draft 2D object (typed FeaturePython)
  ChamferSize = 0
  Closed = false
  End = (130,-16.5,0)
  FilletRadius = 0
  Length = 13
  MakeFace = false
  Placement = pos=(117,-16.5,0) rot=(0,0,1;0rad)
  Points = (2) [(0,0,0),(13,0,0)]
  Start = (117,-16.5,0)
  Subdivisions = 0
FEATURE [Part::Part2DObjectPython] Arc042  # Draft 2D object (typed FeaturePython)
  FirstAngle = 90
  LastAngle = 180
  MakeFace = false
  Placement = pos=(117,-3,0) rot=(0,0,1;0rad)
  Radius = 0.5
FEATURE [Part::Part2DObjectPython] Arc043  # Draft 2D object (typed FeaturePython)
  FirstAngle = 0
  LastAngle = 90
  MakeFace = false
  Placement = pos=(130,-3,0) rot=(0,0,1;0rad)
  Radius = 0.5
FEATURE [Part::Part2DObjectPython] Line092  # Draft 2D object (typed FeaturePython)
  ChamferSize = 0
  Closed = false
  End = (130.5,-3,0)
  FilletRadius = 0
  Length = 13
  MakeFace = false
  Placement = pos=(130.5,-16,0) rot=(0,0,1;0rad)
  Points = (2) [(0,0,0),(0,13,0)]
  Start = (130.5,-16,0)
  Subdivisions = 0
FEATURE [Part::Part2DObjectPython] Line093  # Draft 2D object (typed FeaturePython)
  ChamferSize = 0
  Closed = false
  End = (130,-2.5,0)
  FilletRadius = 0
  Length = 13
  MakeFace = false
  Placement = pos=(117,-2.5,0) rot=(0,0,1;0rad)
  Points = (2) [(0,0,0),(13,0,0)]
  Start = (117,-2.5,0)
  Subdivisions = 0
FEATURE [App::DocumentObjectGroup] Group016
  Group = -> [Line093,Arc043,Arc042,Line087,Arc041,Line088,Arc040,Line092]
FEATURE [Part::Part2DObjectPython] Arc044  # Draft 2D object (typed FeaturePython)
  FirstAngle = 180
  LastAngle = 270
  MakeFace = false
  Placement = pos=(136,-16,0) rot=(0,0,1;0rad)
  Radius = 0.5
FEATURE [Part::Part2DObjectPython] Line094  # Draft 2D object (typed FeaturePython)
  ChamferSize = 0
  Closed = false
  End = (149,-16.5,0)
  FilletRadius = 0
  Length = 13
  MakeFace = false
  Placement = pos=(136,-16.5,0) rot=(0,0,1;0rad)
  Points = (2) [(0,0,0),(13,0,0)]
  Start = (136,-16.5,0)
  Subdivisions = 0
FEATURE [Part::Part2DObjectPython] Arc045  # Draft 2D object (typed FeaturePython)
  FirstAngle = -90
  LastAngle = 0
  MakeFace = false
  Placement = pos=(149,-16,0) rot=(0,0,1;0rad)
  Radius = 0.5
FEATURE [Part::Part2DObjectPython] Line096  # Draft 2D object (typed FeaturePython)
  ChamferSize = 0
  Closed = false
  End = (135.5,-16,0)
  FilletRadius = 0
  Length = 13
  MakeFace = false
  Placement = pos=(135.5,-3,0) rot=(0,0,1;0rad)
  Points = (2) [(0,0,0),(0,-13,0)]
  Start = (135.5,-3,0)
  Subdivisions = 0
FEATURE [Part::Part2DObjectPython] Arc046  # Draft 2D object (typed FeaturePython)
  FirstAngle = 90
  LastAngle = 180
  MakeFace = false
  Placement = pos=(136,-3,0) rot=(0,0,1;0rad)
  Radius = 0.5
FEATURE [Part::Part2DObjectPython] Arc047  # Draft 2D object (typed FeaturePython)
  FirstAngle = 0
  LastAngle = 90
  MakeFace = false
  Placement = pos=(149,-3,0) rot=(0,0,1;0rad)
  Radius = 0.5
FEATURE [Part::Part2DObjectPython] Line099  # Draft 2D object (typed FeaturePython)
  ChamferSize = 0
  Closed = false
  End = (149.5,-3,0)
  FilletRadius = 0
  Length = 13
  MakeFace = false
  Placement = pos=(149.5,-16,0) rot=(0,0,1;0rad)
  Points = (2) [(0,0,0),(0,13,0)]
  Start = (149.5,-16,0)
  Subdivisions = 0
FEATURE [Part::Part2DObjectPython] Line101  # Draft 2D object (typed FeaturePython)
  ChamferSize = 0
  Closed = false
  End = (149,-2.5,0)
  FilletRadius = 0
  Length = 13
  MakeFace = false
  Placement = pos=(136,-2.5,0) rot=(0,0,1;0rad)
  Points = (2) [(0,0,0),(13,0,0)]
  Start = (136,-2.5,0)
  Subdivisions = 0
FEATURE [App::DocumentObjectGroup] Group017
  Group = -> [Line101,Arc047,Arc046,Line096,Arc044,Line094,Arc045,Line099]
FEATURE [Part::Part2DObjectPython] Line102  # Draft 2D object (typed FeaturePython)
  ChamferSize = 0
  Closed = false
  End = (168.5,-3,0)
  FilletRadius = 0
  Length = 13
  MakeFace = false
  Placement = pos=(168.5,-16,0) rot=(0,0,1;0rad)
  Points = (2) [(0,0,0),(0,13,0)]
  Start = (168.5,-16,0)
  Subdivisions = 0
FEATURE [Part::Part2DObjectPython] Arc048  # Draft 2D object (typed FeaturePython)
  FirstAngle = -90
  LastAngle = 0
  MakeFace = false
  Placement = pos=(168,-16,0) rot=(0,0,1;0rad)
  Radius = 0.5
FEATURE [Part::Part2DObjectPython] Line106  # Draft 2D object (typed FeaturePython)
  ChamferSize = 0
  Closed = false
  End = (154.5,-16,0)
  FilletRadius = 0
  Length = 13
  MakeFace = false
  Placement = pos=(154.5,-3,0) rot=(0,0,1;0rad)
  Points = (2) [(0,0,0),(0,-13,0)]
  Start = (154.5,-3,0)
  Subdivisions = 0
FEATURE [Part::Part2DObjectPython] Arc049  # Draft 2D object (typed FeaturePython)
  FirstAngle = 0
  LastAngle = 90
  MakeFace = false
  Placement = pos=(168,-3,0) rot=(0,0,1;0rad)
  Radius = 0.5
FEATURE [Part::Part2DObjectPython] Line107  # Draft 2D object (typed FeaturePython)
  ChamferSize = 0
  Closed = false
  End = (168,-2.5,0)
  FilletRadius = 0
  Length = 13
  MakeFace = false
  Placement = pos=(155,-2.5,0) rot=(0,0,1;0rad)
  Points = (2) [(0,0,0),(13,0,0)]
  Start = (155,-2.5,0)
  Subdivisions = 0
FEATURE [Part::Part2DObjectPython] Arc050  # Draft 2D object (typed FeaturePython)
  FirstAngle = 90
  LastAngle = 180
  MakeFace = false
  Placement = pos=(155,-3,0) rot=(0,0,1;0rad)
  Radius = 0.5
FEATURE [Part::Part2DObjectPython] Arc051  # Draft 2D object (typed FeaturePython)
  FirstAngle = 180
  LastAngle = 270
  MakeFace = false
  Placement = pos=(155,-16,0) rot=(0,0,1;0rad)
  Radius = 0.5
FEATURE [Part::Part2DObjectPython] Line108  # Draft 2D object (typed FeaturePython)
  ChamferSize = 0
  Closed = false
  End = (168,-16.5,0)
  FilletRadius = 0
  Length = 13
  MakeFace = false
  Placement = pos=(155,-16.5,0) rot=(0,0,1;0rad)
  Points = (2) [(0,0,0),(13,0,0)]
  Start = (155,-16.5,0)
  Subdivisions = 0
FEATURE [App::DocumentObjectGroup] Group018
  Group = -> [Line107,Arc049,Arc050,Line106,Arc051,Line108,Arc048,Line102]
FEATURE [Part::Part2DObjectPython] Arc052  # Draft 2D object (typed FeaturePython)
  FirstAngle = 90
  LastAngle = 180
  MakeFace = false
  Placement = pos=(174,-3,0) rot=(0,0,1;0rad)
  Radius = 0.5
FEATURE [Part::Part2DObjectPython] Arc053  # Draft 2D object (typed FeaturePython)
  FirstAngle = 0
  LastAngle = 90
  MakeFace = false
  Placement = pos=(187,-3,0) rot=(0,0,1;0rad)
  Radius = 0.5
FEATURE [Part::Part2DObjectPython] Line112  # Draft 2D object (typed FeaturePython)
  ChamferSize = 0
  Closed = false
  End = (173.5,-16,0)
  FilletRadius = 0
  Length = 13
  MakeFace = false
  Placement = pos=(173.5,-3,0) rot=(0,0,1;0rad)
  Points = (2) [(0,0,0),(0,-13,0)]
  Start = (173.5,-3,0)
  Subdivisions = 0
FEATURE [Part::Part2DObjectPython] Line113  # Draft 2D object (typed FeaturePython)
  ChamferSize = 0
  Closed = false
  End = (187,-2.5,0)
  FilletRadius = 0
  Length = 13
  MakeFace = false
  Placement = pos=(174,-2.5,0) rot=(0,0,1;0rad)
  Points = (2) [(0,0,0),(13,0,0)]
  Start = (174,-2.5,0)
  Subdivisions = 0
FEATURE [Part::Part2DObjectPython] Arc054  # Draft 2D object (typed FeaturePython)
  FirstAngle = 180
  LastAngle = 270
  MakeFace = false
  Placement = pos=(174,-16,0) rot=(0,0,1;0rad)
  Radius = 0.5
FEATURE [Part::Part2DObjectPython] Line116  # Draft 2D object (typed FeaturePython)
  ChamferSize = 0
  Closed = false
  End = (187,-16.5,0)
  FilletRadius = 0
  Length = 13
  MakeFace = false
  Placement = pos=(174,-16.5,0) rot=(0,0,1;0rad)
  Points = (2) [(0,0,0),(13,0,0)]
  Start = (174,-16.5,0)
  Subdivisions = 0
FEATURE [Part::Part2DObjectPython] Line117  # Draft 2D object (typed FeaturePython)
  ChamferSize = 0
  Closed = false
  End = (187.5,-3,0)
  FilletRadius = 0
  Length = 13
  MakeFace = false
  Placement = pos=(187.5,-16,0) rot=(0,0,1;0rad)
  Points = (2) [(0,0,0),(0,13,0)]
  Start = (187.5,-16,0)
  Subdivisions = 0
FEATURE [Part::Part2DObjectPython] Arc055  # Draft 2D object (typed FeaturePython)
  FirstAngle = -90
  LastAngle = 0
  MakeFace = false
  Placement = pos=(187,-16,0) rot=(0,0,1;0rad)
  Radius = 0.5
FEATURE [App::DocumentObjectGroup] Group019
  Group = -> [Line113,Arc053,Arc052,Line112,Arc054,Line116,Arc055,Line117]
FEATURE [Part::Part2DObjectPython] Arc056  # Draft 2D object (typed FeaturePython)
  FirstAngle = 0
  LastAngle = 90
  MakeFace = false
  Placement = pos=(206,-3,0) rot=(0,0,1;0rad)
  Radius = 0.5
FEATURE [Part::Part2DObjectPython] Arc057  # Draft 2D object (typed FeaturePython)
  FirstAngle = 90
  LastAngle = 180
  MakeFace = false
  Placement = pos=(193,-3,0) rot=(0,0,1;0rad)
  Radius = 0.5
FEATURE [Part::Part2DObjectPython] Line120  # Draft 2D object (typed FeaturePython)
  ChamferSize = 0
  Closed = false
  End = (192.5,-16,0)
  FilletRadius = 0
  Length = 13
  MakeFace = false
  Placement = pos=(192.5,-3,0) rot=(0,0,1;0rad)
  Points = (2) [(0,0,0),(0,-13,0)]
  Start = (192.5,-3,0)
  Subdivisions = 0
FEATURE [Part::Part2DObjectPython] Line122  # Draft 2D object (typed FeaturePython)
  ChamferSize = 0
  Closed = false
  End = (206,-16.5,0)
  FilletRadius = 0
  Length = 13
  MakeFace = false
  Placement = pos=(193,-16.5,0) rot=(0,0,1;0rad)
  Points = (2) [(0,0,0),(13,0,0)]
  Start = (193,-16.5,0)
  Subdivisions = 0
FEATURE [Part::Part2DObjectPython] Arc058  # Draft 2D object (typed FeaturePython)
  FirstAngle = -90
  LastAngle = 0
  MakeFace = false
  Placement = pos=(206,-16,0) rot=(0,0,1;0rad)
  Radius = 0.5
FEATURE [Part::Part2DObjectPython] Line123  # Draft 2D object (typed FeaturePython)
  ChamferSize = 0
  Closed = false
  End = (206.5,-3,0)
  FilletRadius = 0
  Length = 13
  MakeFace = false
  Placement = pos=(206.5,-16,0) rot=(0,0,1;0rad)
  Points = (2) [(0,0,0),(0,13,0)]
  Start = (206.5,-16,0)
  Subdivisions = 0
FEATURE [Part::Part2DObjectPython] Arc059  # Draft 2D object (typed FeaturePython)
  FirstAngle = 180
  LastAngle = 270
  MakeFace = false
  Placement = pos=(193,-16,0) rot=(0,0,1;0rad)
  Radius = 0.5
FEATURE [Part::Part2DObjectPython] Line125  # Draft 2D object (typed FeaturePython)
  ChamferSize = 0
  Closed = false
  End = (206,-2.5,0)
  FilletRadius = 0
  Length = 13
  MakeFace = false
  Placement = pos=(193,-2.5,0) rot=(0,0,1;0rad)
  Points = (2) [(0,0,0),(13,0,0)]
  Start = (193,-2.5,0)
  Subdivisions = 0
FEATURE [App::DocumentObjectGroup] Group020
  Group = -> [Line125,Arc056,Arc057,Line120,Arc059,Line122,Arc058,Line123]
FEATURE [Part::Part2DObjectPython] Line129  # Draft 2D object (typed FeaturePython)
  ChamferSize = 0
  Closed = false
  End = (211.5,-16,0)
  FilletRadius = 0
  Length = 13
  MakeFace = false
  Placement = pos=(211.5,-3,0) rot=(0,0,1;0rad)
  Points = (2) [(0,0,0),(0,-13,0)]
  Start = (211.5,-3,0)
  Subdivisions = 0
FEATURE [Part::Part2DObjectPython] Arc061  # Draft 2D object (typed FeaturePython)
  FirstAngle = 180
  LastAngle = 270
  MakeFace = false
  Placement = pos=(212,-16,0) rot=(0,0,1;0rad)
  Radius = 0.5
FEATURE [Part::Part2DObjectPython] Arc062  # Draft 2D object (typed FeaturePython)
  FirstAngle = 90
  LastAngle = 180
  MakeFace = false
  Placement = pos=(212,-3,0) rot=(0,0,1;0rad)
  Radius = 0.5
FEATURE [App::DocumentObjectGroup] Group021
  Group = -> [Arc062,Line129,Arc061]
FEATURE [Part::Part2DObjectPython] Line138  # Draft 2D object (typed FeaturePython)
  ChamferSize = 0
  Closed = false
  End = (244.5,-3,0)
  FilletRadius = 0
  Length = 13
  MakeFace = false
  Placement = pos=(244.5,-16,0) rot=(0,0,1;0rad)
  Points = (2) [(0,0,0),(0,13,0)]
  Start = (244.5,-16,0)
  Subdivisions = 0
FEATURE [Part::Part2DObjectPython] Arc065  # Draft 2D object (typed FeaturePython)
  FirstAngle = -90
  LastAngle = 0
  MakeFace = false
  Placement = pos=(244,-16,0) rot=(0,0,1;0rad)
  Radius = 0.5
FEATURE [Part::Part2DObjectPython] Arc067  # Draft 2D object (typed FeaturePython)
  FirstAngle = 0
  LastAngle = 90
  MakeFace = false
  Placement = pos=(244,-3,0) rot=(0,0,1;0rad)
  Radius = 0.5
FEATURE [App::DocumentObjectGroup] Group022
  Group = -> [Arc067,Arc065,Line138]
FEATURE [Part::Part2DObjectPython] Line146  # Draft 2D object (typed FeaturePython)
  ChamferSize = 0
  Closed = false
  End = (18.375,-21.5,0)
  FilletRadius = 0
  Length = 13
  MakeFace = false
  Placement = pos=(5.375,-21.5,0) rot=(0,0,1;0rad)
  Points = (2) [(0,0,0),(13,0,0)]
  Start = (5.375,-21.5,0)
  Subdivisions = 0
FEATURE [Part::Part2DObjectPython] Arc068  # Draft 2D object (typed FeaturePython)
  FirstAngle = 0
  LastAngle = 90
  MakeFace = false
  Placement = pos=(18.375,-22,0) rot=(0,0,1;0rad)
  Radius = 0.5
FEATURE [Part::Part2DObjectPython] Arc069  # Draft 2D object (typed FeaturePython)
  FirstAngle = 90
  LastAngle = 180
  MakeFace = false
  Placement = pos=(5.375,-22,0) rot=(0,0,1;0rad)
  Radius = 0.5
FEATURE [Part::Part2DObjectPython] Line147  # Draft 2D object (typed FeaturePython)
  ChamferSize = 0
  Closed = false
  End = (4.875,-35,0)
  FilletRadius = 0
  Length = 13
  MakeFace = false
  Placement = pos=(4.875,-22,0) rot=(0,0,1;0rad)
  Points = (2) [(0,0,0),(0,-13,0)]
  Start = (4.875,-22,0)
  Subdivisions = 0
FEATURE [Part::Part2DObjectPython] Arc070  # Draft 2D object (typed FeaturePython)
  FirstAngle = 180
  LastAngle = 270
  MakeFace = false
  Placement = pos=(5.375,-35,0) rot=(0,0,1;0rad)
  Radius = 0.5
FEATURE [Part::Part2DObjectPython] Line148  # Draft 2D object (typed FeaturePython)
  ChamferSize = 0
  Closed = false
  End = (18.375,-35.5,0)
  FilletRadius = 0
  Length = 13
  MakeFace = false
  Placement = pos=(5.375,-35.5,0) rot=(0,0,1;0rad)
  Points = (2) [(0,0,0),(13,0,0)]
  Start = (5.375,-35.5,0)
  Subdivisions = 0
FEATURE [Part::Part2DObjectPython] Arc071  # Draft 2D object (typed FeaturePython)
  FirstAngle = -90
  LastAngle = 0
  MakeFace = false
  Placement = pos=(18.375,-35,0) rot=(0,0,1;0rad)
  Radius = 0.5
FEATURE [Part::Part2DObjectPython] Line149  # Draft 2D object (typed FeaturePython)
  ChamferSize = 0
  Closed = false
  End = (18.875,-22,0)
  FilletRadius = 0
  Length = 13
  MakeFace = false
  Placement = pos=(18.875,-35,0) rot=(0,0,1;0rad)
  Points = (2) [(0,0,0),(0,13,0)]
  Start = (18.875,-35,0)
  Subdivisions = 0
FEATURE [App::DocumentObjectGroup] Group024
  Group = -> [Line149,Arc068,Arc069,Line147,Arc070,Line146,Line148,Arc071]
FEATURE [Part::Part2DObjectPython] Line152  # Draft 2D object (typed FeaturePython)
  ChamferSize = 0
  Closed = false
  End = (39.75,-21.5,0)
  FilletRadius = 0
  Length = 13
  MakeFace = false
  Placement = pos=(26.75,-21.5,0) rot=(0,0,1;0rad)
  Points = (2) [(0,0,0),(13,0,0)]
  Start = (26.75,-21.5,0)
  Subdivisions = 0
FEATURE [Part::Part2DObjectPython] Arc072  # Draft 2D object (typed FeaturePython)
  FirstAngle = 0
  LastAngle = 90
  MakeFace = false
  Placement = pos=(39.75,-22,0) rot=(0,0,1;0rad)
  Radius = 0.5
FEATURE [Part::Part2DObjectPython] Arc073  # Draft 2D object (typed FeaturePython)
  FirstAngle = 90
  LastAngle = 180
  MakeFace = false
  Placement = pos=(26.75,-22,0) rot=(0,0,1;0rad)
  Radius = 0.5
FEATURE [Part::Part2DObjectPython] Line155  # Draft 2D object (typed FeaturePython)
  ChamferSize = 0
  Closed = false
  End = (26.25,-35,0)
  FilletRadius = 0
  Length = 13
  MakeFace = false
  Placement = pos=(26.25,-22,0) rot=(0,0,1;0rad)
  Points = (2) [(0,0,0),(0,-13,0)]
  Start = (26.25,-22,0)
  Subdivisions = 0
FEATURE [Part::Part2DObjectPython] Arc074  # Draft 2D object (typed FeaturePython)
  FirstAngle = 180
  LastAngle = 270
  MakeFace = false
  Placement = pos=(26.75,-35,0) rot=(0,0,1;0rad)
  Radius = 0.5
FEATURE [Part::Part2DObjectPython] Line156  # Draft 2D object (typed FeaturePython)
  ChamferSize = 0
  Closed = false
  End = (39.75,-35.5,0)
  FilletRadius = 0
  Length = 13
  MakeFace = false
  Placement = pos=(26.75,-35.5,0) rot=(0,0,1;0rad)
  Points = (2) [(0,0,0),(13,0,0)]
  Start = (26.75,-35.5,0)
  Subdivisions = 0
FEATURE [Part::Part2DObjectPython] Arc075  # Draft 2D object (typed FeaturePython)
  FirstAngle = -90
  LastAngle = 0
  MakeFace = false
  Placement = pos=(39.75,-35,0) rot=(0,0,1;0rad)
  Radius = 0.5
FEATURE [Part::Part2DObjectPython] Line157  # Draft 2D object (typed FeaturePython)
  ChamferSize = 0
  Closed = false
  End = (40.25,-22,0)
  FilletRadius = 0
  Length = 13
  MakeFace = false
  Placement = pos=(40.25,-35,0) rot=(0,0,1;0rad)
  Points = (2) [(0,0,0),(0,13,0)]
  Start = (40.25,-35,0)
  Subdivisions = 0
FEATURE [App::DocumentObjectGroup] Group025
  Group = -> [Line152,Arc072,Arc073,Line155,Arc074,Line156,Arc075,Line157]
FEATURE [Part::Part2DObjectPython] Arc076  # Draft 2D object (typed FeaturePython)
  FirstAngle = 180
  LastAngle = 270
  MakeFace = false
  Placement = pos=(45.75,-35,0) rot=(0,0,1;0rad)
  Radius = 0.5
FEATURE [Part::Part2DObjectPython] Arc077  # Draft 2D object (typed FeaturePython)
  FirstAngle = -90
  LastAngle = 0
  MakeFace = false
  Placement = pos=(58.75,-35,0) rot=(0,0,1;0rad)
  Radius = 0.5
FEATURE [Part::Part2DObjectPython] Line159  # Draft 2D object (typed FeaturePython)
  ChamferSize = 0
  Closed = false
  End = (59.25,-22,0)
  FilletRadius = 0
  Length = 13
  MakeFace = false
  Placement = pos=(59.25,-35,0) rot=(0,0,1;0rad)
  Points = (2) [(0,0,0),(0,13,0)]
  Start = (59.25,-35,0)
  Subdivisions = 0
FEATURE [Part::Part2DObjectPython] Arc078  # Draft 2D object (typed FeaturePython)
  FirstAngle = 90
  LastAngle = 180
  MakeFace = false
  Placement = pos=(45.75,-22,0) rot=(0,0,1;0rad)
  Radius = 0.5
FEATURE [Part::Part2DObjectPython] Line161  # Draft 2D object (typed FeaturePython)
  ChamferSize = 0
  Closed = false
  End = (58.75,-35.5,0)
  FilletRadius = 0
  Length = 13
  MakeFace = false
  Placement = pos=(45.75,-35.5,0) rot=(0,0,1;0rad)
  Points = (2) [(0,0,0),(13,0,0)]
  Start = (45.75,-35.5,0)
  Subdivisions = 0
FEATURE [Part::Part2DObjectPython] Arc079  # Draft 2D object (typed FeaturePython)
  FirstAngle = 0
  LastAngle = 90
  MakeFace = false
  Placement = pos=(58.75,-22,0) rot=(0,0,1;0rad)
  Radius = 0.5
FEATURE [Part::Part2DObjectPython] Line163  # Draft 2D object (typed FeaturePython)
  ChamferSize = 0
  Closed = false
  End = (45.25,-35,0)
  FilletRadius = 0
  Length = 13
  MakeFace = false
  Placement = pos=(45.25,-22,0) rot=(0,0,1;0rad)
  Points = (2) [(0,0,0),(0,-13,0)]
  Start = (45.25,-22,0)
  Subdivisions = 0
FEATURE [Part::Part2DObjectPython] Line165  # Draft 2D object (typed FeaturePython)
  ChamferSize = 0
  Closed = false
  End = (58.75,-21.5,0)
  FilletRadius = 0
  Length = 13
  MakeFace = false
  Placement = pos=(45.75,-21.5,0) rot=(0,0,1;0rad)
  Points = (2) [(0,0,0),(13,0,0)]
  Start = (45.75,-21.5,0)
  Subdivisions = 0
FEATURE [App::DocumentObjectGroup] Group026
  Group = -> [Line165,Arc079,Arc078,Line163,Arc076,Line161,Arc077,Line159]
FEATURE [Part::Part2DObjectPython] Arc080  # Draft 2D object (typed FeaturePython)
  FirstAngle = 180
  LastAngle = 270
  MakeFace = false
  Placement = pos=(64.75,-35,0) rot=(0,0,1;0rad)
  Radius = 0.5
FEATURE [Part::Part2DObjectPython] Arc081  # Draft 2D object (typed FeaturePython)
  FirstAngle = -90
  LastAngle = 0
  MakeFace = false
  Placement = pos=(77.75,-35,0) rot=(0,0,1;0rad)
  Radius = 0.5
FEATURE [Part::Part2DObjectPython] Line167  # Draft 2D object (typed FeaturePython)
  ChamferSize = 0
  Closed = false
  End = (78.25,-22,0)
  FilletRadius = 0
  Length = 13
  MakeFace = false
  Placement = pos=(78.25,-35,0) rot=(0,0,1;0rad)
  Points = (2) [(0,0,0),(0,13,0)]
  Start = (78.25,-35,0)
  Subdivisions = 0
FEATURE [Part::Part2DObjectPython] Arc082  # Draft 2D object (typed FeaturePython)
  FirstAngle = 90
  LastAngle = 180
  MakeFace = false
  Placement = pos=(64.75,-22,0) rot=(0,0,1;0rad)
  Radius = 0.5
FEATURE [Part::Part2DObjectPython] Arc083  # Draft 2D object (typed FeaturePython)
  FirstAngle = 0
  LastAngle = 90
  MakeFace = false
  Placement = pos=(77.75,-22,0) rot=(0,0,1;0rad)
  Radius = 0.5
FEATURE [Part::Part2DObjectPython] Line171  # Draft 2D object (typed FeaturePython)
  ChamferSize = 0
  Closed = false
  End = (64.25,-35,0)
  FilletRadius = 0
  Length = 13
  MakeFace = false
  Placement = pos=(64.25,-22,0) rot=(0,0,1;0rad)
  Points = (2) [(0,0,0),(0,-13,0)]
  Start = (64.25,-22,0)
  Subdivisions = 0
FEATURE [Part::Part2DObjectPython] Line172  # Draft 2D object (typed FeaturePython)
  ChamferSize = 0
  Closed = false
  End = (77.75,-35.5,0)
  FilletRadius = 0
  Length = 13
  MakeFace = false
  Placement = pos=(64.75,-35.5,0) rot=(0,0,1;0rad)
  Points = (2) [(0,0,0),(13,0,0)]
  Start = (64.75,-35.5,0)
  Subdivisions = 0
FEATURE [Part::Part2DObjectPython] Line173  # Draft 2D object (typed FeaturePython)
  ChamferSize = 0
  Closed = false
  End = (77.75,-21.5,0)
  FilletRadius = 0
  Length = 13
  MakeFace = false
  Placement = pos=(64.75,-21.5,0) rot=(0,0,1;0rad)
  Points = (2) [(0,0,0),(13,0,0)]
  Start = (64.75,-21.5,0)
  Subdivisions = 0
FEATURE [App::DocumentObjectGroup] Group027
  Group = -> [Line173,Arc083,Arc082,Line171,Arc080,Line172,Arc081,Line167]
FEATURE [Part::Part2DObjectPython] Line174  # Draft 2D object (typed FeaturePython)
  ChamferSize = 0
  Closed = false
  End = (96.75,-21.5,0)
  FilletRadius = 0
  Length = 13
  MakeFace = false
  Placement = pos=(83.75,-21.5,0) rot=(0,0,1;0rad)
  Points = (2) [(0,0,0),(13,0,0)]
  Start = (83.75,-21.5,0)
  Subdivisions = 0
FEATURE [Part::Part2DObjectPython] Line177  # Draft 2D object (typed FeaturePython)
  ChamferSize = 0
  Closed = false
  End = (96.75,-35.5,0)
  FilletRadius = 0
  Length = 13
  MakeFace = false
  Placement = pos=(83.75,-35.5,0) rot=(0,0,1;0rad)
  Points = (2) [(0,0,0),(13,0,0)]
  Start = (83.75,-35.5,0)
  Subdivisions = 0
FEATURE [Part::Part2DObjectPython] Line178  # Draft 2D object (typed FeaturePython)
  ChamferSize = 0
  Closed = false
  End = (97.25,-22,0)
  FilletRadius = 0
  Length = 13
  MakeFace = false
  Placement = pos=(97.25,-35,0) rot=(0,0,1;0rad)
  Points = (2) [(0,0,0),(0,13,0)]
  Start = (97.25,-35,0)
  Subdivisions = 0
FEATURE [Part::Part2DObjectPython] Arc084  # Draft 2D object (typed FeaturePython)
  FirstAngle = 180
  LastAngle = 270
  MakeFace = false
  Placement = pos=(83.75,-35,0) rot=(0,0,1;0rad)
  Radius = 0.5
FEATURE [Part::Part2DObjectPython] Arc085  # Draft 2D object (typed FeaturePython)
  FirstAngle = -90
  LastAngle = 0
  MakeFace = false
  Placement = pos=(96.75,-35,0) rot=(0,0,1;0rad)
  Radius = 0.5
FEATURE [Part::Part2DObjectPython] Arc086  # Draft 2D object (typed FeaturePython)
  FirstAngle = 90
  LastAngle = 180
  MakeFace = false
  Placement = pos=(83.75,-22,0) rot=(0,0,1;0rad)
  Radius = 0.5
FEATURE [Part::Part2DObjectPython] Arc087  # Draft 2D object (typed FeaturePython)
  FirstAngle = 0
  LastAngle = 90
  MakeFace = false
  Placement = pos=(96.75,-22,0) rot=(0,0,1;0rad)
  Radius = 0.5
FEATURE [Part::Part2DObjectPython] Line181  # Draft 2D object (typed FeaturePython)
  ChamferSize = 0
  Closed = false
  End = (83.25,-35,0)
  FilletRadius = 0
  Length = 13
  MakeFace = false
  Placement = pos=(83.25,-22,0) rot=(0,0,1;0rad)
  Points = (2) [(0,0,0),(0,-13,0)]
  Start = (83.25,-22,0)
  Subdivisions = 0
FEATURE [App::DocumentObjectGroup] Group028
  Group = -> [Line174,Arc087,Arc086,Line181,Arc084,Line177,Arc085,Line178]
FEATURE [Part::Part2DObjectPython] Arc088  # Draft 2D object (typed FeaturePython)
  FirstAngle = 180
  LastAngle = 270
  MakeFace = false
  Placement = pos=(102.75,-35,0) rot=(0,0,1;0rad)
  Radius = 0.5
FEATURE [Part::Part2DObjectPython] Arc089  # Draft 2D object (typed FeaturePython)
  FirstAngle = -90
  LastAngle = 0
  MakeFace = false
  Placement = pos=(115.75,-35,0) rot=(0,0,1;0rad)
  Radius = 0.5
FEATURE [Part::Part2DObjectPython] Line184  # Draft 2D object (typed FeaturePython)
  ChamferSize = 0
  Closed = false
  End = (115.75,-35.5,0)
  FilletRadius = 0
  Length = 13
  MakeFace = false
  Placement = pos=(102.75,-35.5,0) rot=(0,0,1;0rad)
  Points = (2) [(0,0,0),(13,0,0)]
  Start = (102.75,-35.5,0)
  Subdivisions = 0
FEATURE [Part::Part2DObjectPython] Arc090  # Draft 2D object (typed FeaturePython)
  FirstAngle = 0
  LastAngle = 90
  MakeFace = false
  Placement = pos=(115.75,-22,0) rot=(0,0,1;0rad)
  Radius = 0.5
FEATURE [Part::Part2DObjectPython] Line185  # Draft 2D object (typed FeaturePython)
  ChamferSize = 0
  Closed = false
  End = (115.75,-21.5,0)
  FilletRadius = 0
  Length = 13
  MakeFace = false
  Placement = pos=(102.75,-21.5,0) rot=(0,0,1;0rad)
  Points = (2) [(0,0,0),(13,0,0)]
  Start = (102.75,-21.5,0)
  Subdivisions = 0
FEATURE [Part::Part2DObjectPython] Line187  # Draft 2D object (typed FeaturePython)
  ChamferSize = 0
  Closed = false
  End = (116.25,-22,0)
  FilletRadius = 0
  Length = 13
  MakeFace = false
  Placement = pos=(116.25,-35,0) rot=(0,0,1;0rad)
  Points = (2) [(0,0,0),(0,13,0)]
  Start = (116.25,-35,0)
  Subdivisions = 0
FEATURE [Part::Part2DObjectPython] Line189  # Draft 2D object (typed FeaturePython)
  ChamferSize = 0
  Closed = false
  End = (102.25,-35,0)
  FilletRadius = 0
  Length = 13
  MakeFace = false
  Placement = pos=(102.25,-22,0) rot=(0,0,1;0rad)
  Points = (2) [(0,0,0),(0,-13,0)]
  Start = (102.25,-22,0)
  Subdivisions = 0
FEATURE [Part::Part2DObjectPython] Arc091  # Draft 2D object (typed FeaturePython)
  FirstAngle = 90
  LastAngle = 180
  MakeFace = false
  Placement = pos=(102.75,-22,0) rot=(0,0,1;0rad)
  Radius = 0.5
FEATURE [App::DocumentObjectGroup] Group029
  Group = -> [Line185,Arc090,Arc091,Line189,Arc088,Line184,Arc089,Line187]
FEATURE [Part::Part2DObjectPython] Arc092  # Draft 2D object (typed FeaturePython)
  FirstAngle = 90
  LastAngle = 180
  MakeFace = false
  Placement = pos=(121.75,-22,0) rot=(0,0,1;0rad)
  Radius = 0.5
FEATURE [Part::Part2DObjectPython] Arc093  # Draft 2D object (typed FeaturePython)
  FirstAngle = 180
  LastAngle = 270
  MakeFace = false
  Placement = pos=(121.75,-35,0) rot=(0,0,1;0rad)
  Radius = 0.5
FEATURE [Part::Part2DObjectPython] Arc094  # Draft 2D object (typed FeaturePython)
  FirstAngle = -90
  LastAngle = 0
  MakeFace = false
  Placement = pos=(134.75,-35,0) rot=(0,0,1;0rad)
  Radius = 0.5
FEATURE [Part::Part2DObjectPython] Line190  # Draft 2D object (typed FeaturePython)
  ChamferSize = 0
  Closed = false
  End = (134.75,-35.5,0)
  FilletRadius = 0
  Length = 13
  MakeFace = false
  Placement = pos=(121.75,-35.5,0) rot=(0,0,1;0rad)
  Points = (2) [(0,0,0),(13,0,0)]
  Start = (121.75,-35.5,0)
  Subdivisions = 0
FEATURE [Part::Part2DObjectPython] Arc095  # Draft 2D object (typed FeaturePython)
  FirstAngle = 0
  LastAngle = 90
  MakeFace = false
  Placement = pos=(134.75,-22,0) rot=(0,0,1;0rad)
  Radius = 0.5
FEATURE [Part::Part2DObjectPython] Line191  # Draft 2D object (typed FeaturePython)
  ChamferSize = 0
  Closed = false
  End = (134.75,-21.5,0)
  FilletRadius = 0
  Length = 13
  MakeFace = false
  Placement = pos=(121.75,-21.5,0) rot=(0,0,1;0rad)
  Points = (2) [(0,0,0),(13,0,0)]
  Start = (121.75,-21.5,0)
  Subdivisions = 0
FEATURE [Part::Part2DObjectPython] Line194  # Draft 2D object (typed FeaturePython)
  ChamferSize = 0
  Closed = false
  End = (135.25,-22,0)
  FilletRadius = 0
  Length = 13
  MakeFace = false
  Placement = pos=(135.25,-35,0) rot=(0,0,1;0rad)
  Points = (2) [(0,0,0),(0,13,0)]
  Start = (135.25,-35,0)
  Subdivisions = 0
FEATURE [Part::Part2DObjectPython] Line197  # Draft 2D object (typed FeaturePython)
  ChamferSize = 0
  Closed = false
  End = (121.25,-35,0)
  FilletRadius = 0
  Length = 13
  MakeFace = false
  Placement = pos=(121.25,-22,0) rot=(0,0,1;0rad)
  Points = (2) [(0,0,0),(0,-13,0)]
  Start = (121.25,-22,0)
  Subdivisions = 0
FEATURE [App::DocumentObjectGroup] Group030
  Group = -> [Line191,Arc095,Arc092,Line197,Arc093,Line190,Arc094,Line194]
FEATURE [Part::Part2DObjectPython] Arc096  # Draft 2D object (typed FeaturePython)
  FirstAngle = 180
  LastAngle = 270
  MakeFace = false
  Placement = pos=(140.75,-35,0) rot=(0,0,1;0rad)
  Radius = 0.5
FEATURE [Part::Part2DObjectPython] Arc097  # Draft 2D object (typed FeaturePython)
  FirstAngle = 90
  LastAngle = 180
  MakeFace = false
  Placement = pos=(140.75,-22,0) rot=(0,0,1;0rad)
  Radius = 0.5
FEATURE [Part::Part2DObjectPython] Line199  # Draft 2D object (typed FeaturePython)
  ChamferSize = 0
  Closed = false
  End = (154.25,-22,0)
  FilletRadius = 0
  Length = 13
  MakeFace = false
  Placement = pos=(154.25,-35,0) rot=(0,0,1;0rad)
  Points = (2) [(0,0,0),(0,13,0)]
  Start = (154.25,-35,0)
  Subdivisions = 0
FEATURE [Part::Part2DObjectPython] Line201  # Draft 2D object (typed FeaturePython)
  ChamferSize = 0
  Closed = false
  End = (140.25,-35,0)
  FilletRadius = 0
  Length = 13
  MakeFace = false
  Placement = pos=(140.25,-22,0) rot=(0,0,1;0rad)
  Points = (2) [(0,0,0),(0,-13,0)]
  Start = (140.25,-22,0)
  Subdivisions = 0
FEATURE [Part::Part2DObjectPython] Arc098  # Draft 2D object (typed FeaturePython)
  FirstAngle = -90
  LastAngle = 0
  MakeFace = false
  Placement = pos=(153.75,-35,0) rot=(0,0,1;0rad)
  Radius = 0.5
FEATURE [Part::Part2DObjectPython] Arc099  # Draft 2D object (typed FeaturePython)
  FirstAngle = 0
  LastAngle = 90
  MakeFace = false
  Placement = pos=(153.75,-22,0) rot=(0,0,1;0rad)
  Radius = 0.5
FEATURE [Part::Part2DObjectPython] Line202  # Draft 2D object (typed FeaturePython)
  ChamferSize = 0
  Closed = false
  End = (153.75,-35.5,0)
  FilletRadius = 0
  Length = 13
  MakeFace = false
  Placement = pos=(140.75,-35.5,0) rot=(0,0,1;0rad)
  Points = (2) [(0,0,0),(13,0,0)]
  Start = (140.75,-35.5,0)
  Subdivisions = 0
FEATURE [Part::Part2DObjectPython] Line205  # Draft 2D object (typed FeaturePython)
  ChamferSize = 0
  Closed = false
  End = (153.75,-21.5,0)
  FilletRadius = 0
  Length = 13
  MakeFace = false
  Placement = pos=(140.75,-21.5,0) rot=(0,0,1;0rad)
  Points = (2) [(0,0,0),(13,0,0)]
  Start = (140.75,-21.5,0)
  Subdivisions = 0
FEATURE [App::DocumentObjectGroup] Group031
  Group = -> [Line205,Arc099,Arc097,Line201,Arc096,Line202,Arc098,Line199]
FEATURE [Part::Part2DObjectPython] Arc100  # Draft 2D object (typed FeaturePython)
  FirstAngle = 90
  LastAngle = 180
  MakeFace = false
  Placement = pos=(159.75,-22,0) rot=(0,0,1;0rad)
  Radius = 0.5
FEATURE [Part::Part2DObjectPython] Line206  # Draft 2D object (typed FeaturePython)
  ChamferSize = 0
  Closed = false
  End = (173.25,-22,0)
  FilletRadius = 0
  Length = 13
  MakeFace = false
  Placement = pos=(173.25,-35,0) rot=(0,0,1;0rad)
  Points = (2) [(0,0,0),(0,13,0)]
  Start = (173.25,-35,0)
  Subdivisions = 0
FEATURE [Part::Part2DObjectPython] Line207  # Draft 2D object (typed FeaturePython)
  ChamferSize = 0
  Closed = false
  End = (159.25,-35,0)
  FilletRadius = 0
  Length = 13
  MakeFace = false
  Placement = pos=(159.25,-22,0) rot=(0,0,1;0rad)
  Points = (2) [(0,0,0),(0,-13,0)]
  Start = (159.25,-22,0)
  Subdivisions = 0
FEATURE [Part::Part2DObjectPython] Arc101  # Draft 2D object (typed FeaturePython)
  FirstAngle = 180
  LastAngle = 270
  MakeFace = false
  Placement = pos=(159.75,-35,0) rot=(0,0,1;0rad)
  Radius = 0.5
FEATURE [Part::Part2DObjectPython] Arc102  # Draft 2D object (typed FeaturePython)
  FirstAngle = -90
  LastAngle = 0
  MakeFace = false
  Placement = pos=(172.75,-35,0) rot=(0,0,1;0rad)
  Radius = 0.5
FEATURE [Part::Part2DObjectPython] Line211  # Draft 2D object (typed FeaturePython)
  ChamferSize = 0
  Closed = false
  End = (172.75,-35.5,0)
  FilletRadius = 0
  Length = 13
  MakeFace = false
  Placement = pos=(159.75,-35.5,0) rot=(0,0,1;0rad)
  Points = (2) [(0,0,0),(13,0,0)]
  Start = (159.75,-35.5,0)
  Subdivisions = 0
FEATURE [Part::Part2DObjectPython] Arc103  # Draft 2D object (typed FeaturePython)
  FirstAngle = 0
  LastAngle = 90
  MakeFace = false
  Placement = pos=(172.75,-22,0) rot=(0,0,1;0rad)
  Radius = 0.5
FEATURE [Part::Part2DObjectPython] Line213  # Draft 2D object (typed FeaturePython)
  ChamferSize = 0
  Closed = false
  End = (172.75,-21.5,0)
  FilletRadius = 0
  Length = 13
  MakeFace = false
  Placement = pos=(159.75,-21.5,0) rot=(0,0,1;0rad)
  Points = (2) [(0,0,0),(13,0,0)]
  Start = (159.75,-21.5,0)
  Subdivisions = 0
FEATURE [App::DocumentObjectGroup] Group032
  Group = -> [Line213,Arc103,Arc100,Line207,Arc101,Line211,Arc102,Line206]
FEATURE [Part::Part2DObjectPython] Line216  # Draft 2D object (typed FeaturePython)
  ChamferSize = 0
  Closed = false
  End = (192.25,-22,0)
  FilletRadius = 0
  Length = 13
  MakeFace = false
  Placement = pos=(192.25,-35,0) rot=(0,0,1;0rad)
  Points = (2) [(0,0,0),(0,13,0)]
  Start = (192.25,-35,0)
  Subdivisions = 0
FEATURE [Part::Part2DObjectPython] Line217  # Draft 2D object (typed FeaturePython)
  ChamferSize = 0
  Closed = false
  End = (191.75,-21.5,0)
  FilletRadius = 0
  Length = 13
  MakeFace = false
  Placement = pos=(178.75,-21.5,0) rot=(0,0,1;0rad)
  Points = (2) [(0,0,0),(13,0,0)]
  Start = (178.75,-21.5,0)
  Subdivisions = 0
FEATURE [Part::Part2DObjectPython] Line218  # Draft 2D object (typed FeaturePython)
  ChamferSize = 0
  Closed = false
  End = (178.25,-35,0)
  FilletRadius = 0
  Length = 13
  MakeFace = false
  Placement = pos=(178.25,-22,0) rot=(0,0,1;0rad)
  Points = (2) [(0,0,0),(0,-13,0)]
  Start = (178.25,-22,0)
  Subdivisions = 0
FEATURE [Part::Part2DObjectPython] Arc104  # Draft 2D object (typed FeaturePython)
  FirstAngle = 90
  LastAngle = 180
  MakeFace = false
  Placement = pos=(178.75,-22,0) rot=(0,0,1;0rad)
  Radius = 0.5
FEATURE [Part::Part2DObjectPython] Arc105  # Draft 2D object (typed FeaturePython)
  FirstAngle = 180
  LastAngle = 270
  MakeFace = false
  Placement = pos=(178.75,-35,0) rot=(0,0,1;0rad)
  Radius = 0.5
FEATURE [Part::Part2DObjectPython] Arc106  # Draft 2D object (typed FeaturePython)
  FirstAngle = 0
  LastAngle = 90
  MakeFace = false
  Placement = pos=(191.75,-22,0) rot=(0,0,1;0rad)
  Radius = 0.5
FEATURE [Part::Part2DObjectPython] Arc107  # Draft 2D object (typed FeaturePython)
  FirstAngle = -90
  LastAngle = 0
  MakeFace = false
  Placement = pos=(191.75,-35,0) rot=(0,0,1;0rad)
  Radius = 0.5
FEATURE [Part::Part2DObjectPython] Line219  # Draft 2D object (typed FeaturePython)
  ChamferSize = 0
  Closed = false
  End = (191.75,-35.5,0)
  FilletRadius = 0
  Length = 13
  MakeFace = false
  Placement = pos=(178.75,-35.5,0) rot=(0,0,1;0rad)
  Points = (2) [(0,0,0),(13,0,0)]
  Start = (178.75,-35.5,0)
  Subdivisions = 0
FEATURE [App::DocumentObjectGroup] Group033
  Group = -> [Line217,Arc106,Arc104,Line218,Arc105,Line219,Arc107,Line216]
FEATURE [Part::Part2DObjectPython] Arc108  # Draft 2D object (typed FeaturePython)
  FirstAngle = 0
  LastAngle = 90
  MakeFace = false
  Placement = pos=(210.75,-22,0) rot=(0,0,1;0rad)
  Radius = 0.5
FEATURE [Part::Part2DObjectPython] Line222  # Draft 2D object (typed FeaturePython)
  ChamferSize = 0
  Closed = false
  End = (211.25,-22,0)
  FilletRadius = 0
  Length = 13
  MakeFace = false
  Placement = pos=(211.25,-35,0) rot=(0,0,1;0rad)
  Points = (2) [(0,0,0),(0,13,0)]
  Start = (211.25,-35,0)
  Subdivisions = 0
FEATURE [Part::Part2DObjectPython] Arc109  # Draft 2D object (typed FeaturePython)
  FirstAngle = -90
  LastAngle = 0
  MakeFace = false
  Placement = pos=(210.75,-35,0) rot=(0,0,1;0rad)
  Radius = 0.5
FEATURE [Part::Part2DObjectPython] Line224  # Draft 2D object (typed FeaturePython)
  ChamferSize = 0
  Closed = false
  End = (197.25,-35,0)
  FilletRadius = 0
  Length = 13
  MakeFace = false
  Placement = pos=(197.25,-22,0) rot=(0,0,1;0rad)
  Points = (2) [(0,0,0),(0,-13,0)]
  Start = (197.25,-22,0)
  Subdivisions = 0
FEATURE [Part::Part2DObjectPython] Line225  # Draft 2D object (typed FeaturePython)
  ChamferSize = 0
  Closed = false
  End = (210.75,-21.5,0)
  FilletRadius = 0
  Length = 13
  MakeFace = false
  Placement = pos=(197.75,-21.5,0) rot=(0,0,1;0rad)
  Points = (2) [(0,0,0),(13,0,0)]
  Start = (197.75,-21.5,0)
  Subdivisions = 0
FEATURE [Part::Part2DObjectPython] Arc110  # Draft 2D object (typed FeaturePython)
  FirstAngle = 90
  LastAngle = 180
  MakeFace = false
  Placement = pos=(197.75,-22,0) rot=(0,0,1;0rad)
  Radius = 0.5
FEATURE [Part::Part2DObjectPython] Arc111  # Draft 2D object (typed FeaturePython)
  FirstAngle = 180
  LastAngle = 270
  MakeFace = false
  Placement = pos=(197.75,-35,0) rot=(0,0,1;0rad)
  Radius = 0.5
FEATURE [Part::Part2DObjectPython] Line229  # Draft 2D object (typed FeaturePython)
  ChamferSize = 0
  Closed = false
  End = (210.75,-35.5,0)
  FilletRadius = 0
  Length = 13
  MakeFace = false
  Placement = pos=(197.75,-35.5,0) rot=(0,0,1;0rad)
  Points = (2) [(0,0,0),(13,0,0)]
  Start = (197.75,-35.5,0)
  Subdivisions = 0
FEATURE [App::DocumentObjectGroup] Group034
  Group = -> [Line225,Arc108,Arc110,Line224,Arc111,Line229,Arc109,Line222]
FEATURE [Part::Part2DObjectPython] Arc112  # Draft 2D object (typed FeaturePython)
  FirstAngle = 0
  LastAngle = 90
  MakeFace = false
  Placement = pos=(236.875,-22,0) rot=(0,0,1;0rad)
  Radius = 0.5
FEATURE [Part::Part2DObjectPython] Line234  # Draft 2D object (typed FeaturePython)
  ChamferSize = 0
  Closed = false
  End = (237.375,-22,0)
  FilletRadius = 0
  Length = 13
  MakeFace = false
  Placement = pos=(237.375,-35,0) rot=(0,0,1;0rad)
  Points = (2) [(0,0,0),(0,13,0)]
  Start = (237.375,-35,0)
  Subdivisions = 0
FEATURE [Part::Part2DObjectPython] Arc113  # Draft 2D object (typed FeaturePython)
  FirstAngle = -90
  LastAngle = 0
  MakeFace = false
  Placement = pos=(236.875,-35,0) rot=(0,0,1;0rad)
  Radius = 0.5
FEATURE [Part::Part2DObjectPython] Line235  # Draft 2D object (typed FeaturePython)
  ChamferSize = 0
  Closed = false
  End = (223.375,-35,0)
  FilletRadius = 0
  Length = 13
  MakeFace = false
  Placement = pos=(223.375,-22,0) rot=(0,0,1;0rad)
  Points = (2) [(0,0,0),(0,-13,0)]
  Start = (223.375,-22,0)
  Subdivisions = 0
FEATURE [Part::Part2DObjectPython] Line236  # Draft 2D object (typed FeaturePython)
  ChamferSize = 0
  Closed = false
  End = (236.875,-21.5,0)
  FilletRadius = 0
  Length = 13
  MakeFace = false
  Placement = pos=(223.875,-21.5,0) rot=(0,0,1;0rad)
  Points = (2) [(0,0,0),(13,0,0)]
  Start = (223.875,-21.5,0)
  Subdivisions = 0
FEATURE [Part::Part2DObjectPython] Arc114  # Draft 2D object (typed FeaturePython)
  FirstAngle = 90
  LastAngle = 180
  MakeFace = false
  Placement = pos=(223.875,-22,0) rot=(0,0,1;0rad)
  Radius = 0.5
FEATURE [Part::Part2DObjectPython] Arc115  # Draft 2D object (typed FeaturePython)
  FirstAngle = 180
  LastAngle = 270
  MakeFace = false
  Placement = pos=(223.875,-35,0) rot=(0,0,1;0rad)
  Radius = 0.5
FEATURE [Part::Part2DObjectPython] Line237  # Draft 2D object (typed FeaturePython)
  ChamferSize = 0
  Closed = false
  End = (236.875,-35.5,0)
  FilletRadius = 0
  Length = 13
  MakeFace = false
  Placement = pos=(223.875,-35.5,0) rot=(0,0,1;0rad)
  Points = (2) [(0,0,0),(13,0,0)]
  Start = (223.875,-35.5,0)
  Subdivisions = 0
FEATURE [App::DocumentObjectGroup] Group035
  Group = -> [Arc112,Line234,Arc113,Line235,Line236,Arc114,Arc115,Line237]
FEATURE [App::DocumentObjectGroup] Group023  label="Row 2"
  Group = -> [Group024,Group025,Group026,Group027,Group028,Group029,Group030,Group031,Group032,Group033,Group034,Group035]
FEATURE [Part::Part2DObjectPython] Line238  # Draft 2D object (typed FeaturePython)
  ChamferSize = 0
  Closed = false
  End = (23.625,-41,0)
  FilletRadius = 0
  Length = 13
  MakeFace = false
  Placement = pos=(23.625,-54,0) rot=(0,0,1;0rad)
  Points = (2) [(0,0,0),(0,13,0)]
  Start = (23.625,-54,0)
  Subdivisions = 0
FEATURE [Part::Part2DObjectPython] Line239  # Draft 2D object (typed FeaturePython)
  ChamferSize = 0
  Closed = false
  End = (23.125,-54.5,0)
  FilletRadius = 0
  Length = 13
  MakeFace = false
  Placement = pos=(10.125,-54.5,0) rot=(0,0,1;0rad)
  Points = (2) [(0,0,0),(13,0,0)]
  Start = (10.125,-54.5,0)
  Subdivisions = 0
FEATURE [Part::Part2DObjectPython] Arc116  # Draft 2D object (typed FeaturePython)
  FirstAngle = -90
  LastAngle = 0
  MakeFace = false
  Placement = pos=(23.125,-54,0) rot=(0,0,1;0rad)
  Radius = 0.5
FEATURE [Part::Part2DObjectPython] Line240  # Draft 2D object (typed FeaturePython)
  ChamferSize = 0
  Closed = false
  End = (9.625,-54,0)
  FilletRadius = 0
  Length = 13
  MakeFace = false
  Placement = pos=(9.625,-41,0) rot=(0,0,1;0rad)
  Points = (2) [(0,0,0),(0,-13,0)]
  Start = (9.625,-41,0)
  Subdivisions = 0
FEATURE [Part::Part2DObjectPython] Arc117  # Draft 2D object (typed FeaturePython)
  FirstAngle = 90
  LastAngle = 180
  MakeFace = false
  Placement = pos=(10.125,-41,0) rot=(0,0,1;0rad)
  Radius = 0.5
FEATURE [Part::Part2DObjectPython] Arc118  # Draft 2D object (typed FeaturePython)
  FirstAngle = 0
  LastAngle = 90
  MakeFace = false
  Placement = pos=(23.125,-41,0) rot=(0,0,1;0rad)
  Radius = 0.5
FEATURE [Part::Part2DObjectPython] Line244  # Draft 2D object (typed FeaturePython)
  ChamferSize = 0
  Closed = false
  End = (23.125,-40.5,0)
  FilletRadius = 0
  Length = 13
  MakeFace = false
  Placement = pos=(10.125,-40.5,0) rot=(0,0,1;0rad)
  Points = (2) [(0,0,0),(13,0,0)]
  Start = (10.125,-40.5,0)
  Subdivisions = 0
FEATURE [Part::Part2DObjectPython] Arc119  # Draft 2D object (typed FeaturePython)
  FirstAngle = 180
  LastAngle = 270
  MakeFace = false
  Placement = pos=(10.125,-54,0) rot=(0,0,1;0rad)
  Radius = 0.5
FEATURE [App::DocumentObjectGroup] Group037
  Group = -> [Arc118,Line238,Arc116,Line240,Line244,Arc117,Arc119,Line239]
FEATURE [Part::Part2DObjectPython] Line248  # Draft 2D object (typed FeaturePython)
  ChamferSize = 0
  Closed = false
  End = (49.25,-40.5,0)
  FilletRadius = 0
  Length = 13
  MakeFace = false
  Placement = pos=(36.25,-40.5,0) rot=(0,0,1;0rad)
  Points = (2) [(0,0,0),(13,0,0)]
  Start = (36.25,-40.5,0)
  Subdivisions = 0
FEATURE [Part::Part2DObjectPython] Arc120  # Draft 2D object (typed FeaturePython)
  FirstAngle = 0
  LastAngle = 90
  MakeFace = false
  Placement = pos=(49.25,-41,0) rot=(0,0,1;0rad)
  Radius = 0.5
FEATURE [Part::Part2DObjectPython] Arc121  # Draft 2D object (typed FeaturePython)
  FirstAngle = 90
  LastAngle = 180
  MakeFace = false
  Placement = pos=(36.25,-41,0) rot=(0,0,1;0rad)
  Radius = 0.5
FEATURE [Part::Part2DObjectPython] Line251  # Draft 2D object (typed FeaturePython)
  ChamferSize = 0
  Closed = false
  End = (35.75,-54,0)
  FilletRadius = 0
  Length = 13
  MakeFace = false
  Placement = pos=(35.75,-41,0) rot=(0,0,1;0rad)
  Points = (2) [(0,0,0),(0,-13,0)]
  Start = (35.75,-41,0)
  Subdivisions = 0
FEATURE [Part::Part2DObjectPython] Arc122  # Draft 2D object (typed FeaturePython)
  FirstAngle = 180
  LastAngle = 270
  MakeFace = false
  Placement = pos=(36.25,-54,0) rot=(0,0,1;0rad)
  Radius = 0.5
FEATURE [Part::Part2DObjectPython] Line252  # Draft 2D object (typed FeaturePython)
  ChamferSize = 0
  Closed = false
  End = (49.25,-54.5,0)
  FilletRadius = 0
  Length = 13
  MakeFace = false
  Placement = pos=(36.25,-54.5,0) rot=(0,0,1;0rad)
  Points = (2) [(0,0,0),(13,0,0)]
  Start = (36.25,-54.5,0)
  Subdivisions = 0
FEATURE [Part::Part2DObjectPython] Arc123  # Draft 2D object (typed FeaturePython)
  FirstAngle = -90
  LastAngle = 0
  MakeFace = false
  Placement = pos=(49.25,-54,0) rot=(0,0,1;0rad)
  Radius = 0.5
FEATURE [Part::Part2DObjectPython] Line253  # Draft 2D object (typed FeaturePython)
  ChamferSize = 0
  Closed = false
  End = (49.75,-41,0)
  FilletRadius = 0
  Length = 13
  MakeFace = false
  Placement = pos=(49.75,-54,0) rot=(0,0,1;0rad)
  Points = (2) [(0,0,0),(0,13,0)]
  Start = (49.75,-54,0)
  Subdivisions = 0
FEATURE [App::DocumentObjectGroup] Group038
  Group = -> [Line248,Arc120,Arc121,Line251,Arc122,Line252,Arc123,Line253]
FEATURE [Part::Part2DObjectPython] Line254  # Draft 2D object (typed FeaturePython)
  ChamferSize = 0
  Closed = false
  End = (68.25,-54.5,0)
  FilletRadius = 0
  Length = 13
  MakeFace = false
  Placement = pos=(55.25,-54.5,0) rot=(0,0,1;0rad)
  Points = (2) [(0,0,0),(13,0,0)]
  Start = (55.25,-54.5,0)
  Subdivisions = 0
FEATURE [Part::Part2DObjectPython] Arc124  # Draft 2D object (typed FeaturePython)
  FirstAngle = 0
  LastAngle = 90
  MakeFace = false
  Placement = pos=(68.25,-41,0) rot=(0,0,1;0rad)
  Radius = 0.5
FEATURE [Part::Part2DObjectPython] Line257  # Draft 2D object (typed FeaturePython)
  ChamferSize = 0
  Closed = false
  End = (68.75,-41,0)
  FilletRadius = 0
  Length = 13
  MakeFace = false
  Placement = pos=(68.75,-54,0) rot=(0,0,1;0rad)
  Points = (2) [(0,0,0),(0,13,0)]
  Start = (68.75,-54,0)
  Subdivisions = 0
FEATURE [Part::Part2DObjectPython] Line258  # Draft 2D object (typed FeaturePython)
  ChamferSize = 0
  Closed = false
  End = (68.25,-40.5,0)
  FilletRadius = 0
  Length = 13
  MakeFace = false
  Placement = pos=(55.25,-40.5,0) rot=(0,0,1;0rad)
  Points = (2) [(0,0,0),(13,0,0)]
  Start = (55.25,-40.5,0)
  Subdivisions = 0
FEATURE [Part::Part2DObjectPython] Arc125  # Draft 2D object (typed FeaturePython)
  FirstAngle = 90
  LastAngle = 180
  MakeFace = false
  Placement = pos=(55.25,-41,0) rot=(0,0,1;0rad)
  Radius = 0.5
FEATURE [Part::Part2DObjectPython] Line259  # Draft 2D object (typed FeaturePython)
  ChamferSize = 0
  Closed = false
  End = (54.75,-54,0)
  FilletRadius = 0
  Length = 13
  MakeFace = false
  Placement = pos=(54.75,-41,0) rot=(0,0,1;0rad)
  Points = (2) [(0,0,0),(0,-13,0)]
  Start = (54.75,-41,0)
  Subdivisions = 0
FEATURE [Part::Part2DObjectPython] Arc126  # Draft 2D object (typed FeaturePython)
  FirstAngle = 180
  LastAngle = 270
  MakeFace = false
  Placement = pos=(55.25,-54,0) rot=(0,0,1;0rad)
  Radius = 0.5
FEATURE [Part::Part2DObjectPython] Arc127  # Draft 2D object (typed FeaturePython)
  FirstAngle = -90
  LastAngle = 0
  MakeFace = false
  Placement = pos=(68.25,-54,0) rot=(0,0,1;0rad)
  Radius = 0.5
FEATURE [App::DocumentObjectGroup] Group039
  Group = -> [Line258,Arc124,Arc125,Line259,Arc126,Line254,Arc127,Line257]
FEATURE [Part::Part2DObjectPython] Arc128  # Draft 2D object (typed FeaturePython)
  FirstAngle = 0
  LastAngle = 90
  MakeFace = false
  Placement = pos=(87.25,-41,0) rot=(0,0,1;0rad)
  Radius = 0.5
FEATURE [Part::Part2DObjectPython] Arc129  # Draft 2D object (typed FeaturePython)
  FirstAngle = -90
  LastAngle = 0
  MakeFace = false
  Placement = pos=(87.25,-54,0) rot=(0,0,1;0rad)
  Radius = 0.5
FEATURE [Part::Part2DObjectPython] Line264  # Draft 2D object (typed FeaturePython)
  ChamferSize = 0
  Closed = false
  End = (87.25,-54.5,0)
  FilletRadius = 0
  Length = 13
  MakeFace = false
  Placement = pos=(74.25,-54.5,0) rot=(0,0,1;0rad)
  Points = (2) [(0,0,0),(13,0,0)]
  Start = (74.25,-54.5,0)
  Subdivisions = 0
FEATURE [Part::Part2DObjectPython] Line265  # Draft 2D object (typed FeaturePython)
  ChamferSize = 0
  Closed = false
  End = (87.75,-41,0)
  FilletRadius = 0
  Length = 13
  MakeFace = false
  Placement = pos=(87.75,-54,0) rot=(0,0,1;0rad)
  Points = (2) [(0,0,0),(0,13,0)]
  Start = (87.75,-54,0)
  Subdivisions = 0
FEATURE [Part::Part2DObjectPython] Arc130  # Draft 2D object (typed FeaturePython)
  FirstAngle = 180
  LastAngle = 270
  MakeFace = false
  Placement = pos=(74.25,-54,0) rot=(0,0,1;0rad)
  Radius = 0.5
FEATURE [Part::Part2DObjectPython] Line267  # Draft 2D object (typed FeaturePython)
  ChamferSize = 0
  Closed = false
  End = (87.25,-40.5,0)
  FilletRadius = 0
  Length = 13
  MakeFace = false
  Placement = pos=(74.25,-40.5,0) rot=(0,0,1;0rad)
  Points = (2) [(0,0,0),(13,0,0)]
  Start = (74.25,-40.5,0)
  Subdivisions = 0
FEATURE [Part::Part2DObjectPython] Arc131  # Draft 2D object (typed FeaturePython)
  FirstAngle = 90
  LastAngle = 180
  MakeFace = false
  Placement = pos=(74.25,-41,0) rot=(0,0,1;0rad)
  Radius = 0.5
FEATURE [Part::Part2DObjectPython] Line269  # Draft 2D object (typed FeaturePython)
  ChamferSize = 0
  Closed = false
  End = (73.75,-54,0)
  FilletRadius = 0
  Length = 13
  MakeFace = false
  Placement = pos=(73.75,-41,0) rot=(0,0,1;0rad)
  Points = (2) [(0,0,0),(0,-13,0)]
  Start = (73.75,-41,0)
  Subdivisions = 0
FEATURE [App::DocumentObjectGroup] Group040
  Group = -> [Line267,Arc128,Arc131,Line269,Arc130,Line264,Arc129,Line265]
FEATURE [Part::Part2DObjectPython] Arc132  # Draft 2D object (typed FeaturePython)
  FirstAngle = 0
  LastAngle = 90
  MakeFace = false
  Placement = pos=(106.25,-41,0) rot=(0,0,1;0rad)
  Radius = 0.5
FEATURE [Part::Part2DObjectPython] Arc133  # Draft 2D object (typed FeaturePython)
  FirstAngle = -90
  LastAngle = 0
  MakeFace = false
  Placement = pos=(106.25,-54,0) rot=(0,0,1;0rad)
  Radius = 0.5
FEATURE [Part::Part2DObjectPython] Line270  # Draft 2D object (typed FeaturePython)
  ChamferSize = 0
  Closed = false
  End = (106.25,-54.5,0)
  FilletRadius = 0
  Length = 13
  MakeFace = false
  Placement = pos=(93.25,-54.5,0) rot=(0,0,1;0rad)
  Points = (2) [(0,0,0),(13,0,0)]
  Start = (93.25,-54.5,0)
  Subdivisions = 0
FEATURE [Part::Part2DObjectPython] Line273  # Draft 2D object (typed FeaturePython)
  ChamferSize = 0
  Closed = false
  End = (106.75,-41,0)
  FilletRadius = 0
  Length = 13
  MakeFace = false
  Placement = pos=(106.75,-54,0) rot=(0,0,1;0rad)
  Points = (2) [(0,0,0),(0,13,0)]
  Start = (106.75,-54,0)
  Subdivisions = 0
FEATURE [Part::Part2DObjectPython] Arc134  # Draft 2D object (typed FeaturePython)
  FirstAngle = 180
  LastAngle = 270
  MakeFace = false
  Placement = pos=(93.25,-54,0) rot=(0,0,1;0rad)
  Radius = 0.5
FEATURE [Part::Part2DObjectPython] Line275  # Draft 2D object (typed FeaturePython)
  ChamferSize = 0
  Closed = false
  End = (106.25,-40.5,0)
  FilletRadius = 0
  Length = 13
  MakeFace = false
  Placement = pos=(93.25,-40.5,0) rot=(0,0,1;0rad)
  Points = (2) [(0,0,0),(13,0,0)]
  Start = (93.25,-40.5,0)
  Subdivisions = 0
FEATURE [Part::Part2DObjectPython] Arc135  # Draft 2D object (typed FeaturePython)
  FirstAngle = 90
  LastAngle = 180
  MakeFace = false
  Placement = pos=(93.25,-41,0) rot=(0,0,1;0rad)
  Radius = 0.5
FEATURE [Part::Part2DObjectPython] Line277  # Draft 2D object (typed FeaturePython)
  ChamferSize = 0
  Closed = false
  End = (92.75,-54,0)
  FilletRadius = 0
  Length = 13
  MakeFace = false
  Placement = pos=(92.75,-41,0) rot=(0,0,1;0rad)
  Points = (2) [(0,0,0),(0,-13,0)]
  Start = (92.75,-41,0)
  Subdivisions = 0
FEATURE [App::DocumentObjectGroup] Group041
  Group = -> [Line275,Arc132,Arc135,Line277,Arc134,Line270,Arc133,Line273]
FEATURE [Part::Part2DObjectPython] Arc136  # Draft 2D object (typed FeaturePython)
  FirstAngle = 90
  LastAngle = 180
  MakeFace = false
  Placement = pos=(112.25,-41,0) rot=(0,0,1;0rad)
  Radius = 0.5
FEATURE [Part::Part2DObjectPython] Arc137  # Draft 2D object (typed FeaturePython)
  FirstAngle = 180
  LastAngle = 270
  MakeFace = false
  Placement = pos=(112.25,-54,0) rot=(0,0,1;0rad)
  Radius = 0.5
FEATURE [Part::Part2DObjectPython] Line279  # Draft 2D object (typed FeaturePython)
  ChamferSize = 0
  Closed = false
  End = (111.75,-54,0)
  FilletRadius = 0
  Length = 13
  MakeFace = false
  Placement = pos=(111.75,-41,0) rot=(0,0,1;0rad)
  Points = (2) [(0,0,0),(0,-13,0)]
  Start = (111.75,-41,0)
  Subdivisions = 0
FEATURE [Part::Part2DObjectPython] Line280  # Draft 2D object (typed FeaturePython)
  ChamferSize = 0
  Closed = false
  End = (125.25,-40.5,0)
  FilletRadius = 0
  Length = 13
  MakeFace = false
  Placement = pos=(112.25,-40.5,0) rot=(0,0,1;0rad)
  Points = (2) [(0,0,0),(13,0,0)]
  Start = (112.25,-40.5,0)
  Subdivisions = 0
FEATURE [Part::Part2DObjectPython] Line281  # Draft 2D object (typed FeaturePython)
  ChamferSize = 0
  Closed = false
  End = (125.75,-41,0)
  FilletRadius = 0
  Length = 13
  MakeFace = false
  Placement = pos=(125.75,-54,0) rot=(0,0,1;0rad)
  Points = (2) [(0,0,0),(0,13,0)]
  Start = (125.75,-54,0)
  Subdivisions = 0
FEATURE [Part::Part2DObjectPython] Arc138  # Draft 2D object (typed FeaturePython)
  FirstAngle = 0
  LastAngle = 90
  MakeFace = false
  Placement = pos=(125.25,-41,0) rot=(0,0,1;0rad)
  Radius = 0.5
FEATURE [Part::Part2DObjectPython] Arc139  # Draft 2D object (typed FeaturePython)
  FirstAngle = -90
  LastAngle = 0
  MakeFace = false
  Placement = pos=(125.25,-54,0) rot=(0,0,1;0rad)
  Radius = 0.5
FEATURE [Part::Part2DObjectPython] Line285  # Draft 2D object (typed FeaturePython)
  ChamferSize = 0
  Closed = false
  End = (125.25,-54.5,0)
  FilletRadius = 0
  Length = 13
  MakeFace = false
  Placement = pos=(112.25,-54.5,0) rot=(0,0,1;0rad)
  Points = (2) [(0,0,0),(13,0,0)]
  Start = (112.25,-54.5,0)
  Subdivisions = 0
FEATURE [App::DocumentObjectGroup] Group042
  Group = -> [Line280,Arc138,Arc136,Line279,Arc137,Line285,Arc139,Line281]
FEATURE [Part::Part2DObjectPython] Line287  # Draft 2D object (typed FeaturePython)
  ChamferSize = 0
  Closed = false
  End = (130.75,-54,0)
  FilletRadius = 0
  Length = 13
  MakeFace = false
  Placement = pos=(130.75,-41,0) rot=(0,0,1;0rad)
  Points = (2) [(0,0,0),(0,-13,0)]
  Start = (130.75,-41,0)
  Subdivisions = 0
FEATURE [Part::Part2DObjectPython] Arc140  # Draft 2D object (typed FeaturePython)
  FirstAngle = 0
  LastAngle = 90
  MakeFace = false
  Placement = pos=(144.25,-41,0) rot=(0,0,1;0rad)
  Radius = 0.5
FEATURE [Part::Part2DObjectPython] Line289  # Draft 2D object (typed FeaturePython)
  ChamferSize = 0
  Closed = false
  End = (144.25,-40.5,0)
  FilletRadius = 0
  Length = 13
  MakeFace = false
  Placement = pos=(131.25,-40.5,0) rot=(0,0,1;0rad)
  Points = (2) [(0,0,0),(13,0,0)]
  Start = (131.25,-40.5,0)
  Subdivisions = 0
FEATURE [Part::Part2DObjectPython] Arc141  # Draft 2D object (typed FeaturePython)
  FirstAngle = 90
  LastAngle = 180
  MakeFace = false
  Placement = pos=(131.25,-41,0) rot=(0,0,1;0rad)
  Radius = 0.5
FEATURE [Part::Part2DObjectPython] Arc142  # Draft 2D object (typed FeaturePython)
  FirstAngle = 180
  LastAngle = 270
  MakeFace = false
  Placement = pos=(131.25,-54,0) rot=(0,0,1;0rad)
  Radius = 0.5
FEATURE [Part::Part2DObjectPython] Line290  # Draft 2D object (typed FeaturePython)
  ChamferSize = 0
  Closed = false
  End = (144.75,-41,0)
  FilletRadius = 0
  Length = 13
  MakeFace = false
  Placement = pos=(144.75,-54,0) rot=(0,0,1;0rad)
  Points = (2) [(0,0,0),(0,13,0)]
  Start = (144.75,-54,0)
  Subdivisions = 0
FEATURE [Part::Part2DObjectPython] Arc143  # Draft 2D object (typed FeaturePython)
  FirstAngle = -90
  LastAngle = 0
  MakeFace = false
  Placement = pos=(144.25,-54,0) rot=(0,0,1;0rad)
  Radius = 0.5
FEATURE [Part::Part2DObjectPython] Line293  # Draft 2D object (typed FeaturePython)
  ChamferSize = 0
  Closed = false
  End = (144.25,-54.5,0)
  FilletRadius = 0
  Length = 13
  MakeFace = false
  Placement = pos=(131.25,-54.5,0) rot=(0,0,1;0rad)
  Points = (2) [(0,0,0),(13,0,0)]
  Start = (131.25,-54.5,0)
  Subdivisions = 0
FEATURE [App::DocumentObjectGroup] Group043
  Group = -> [Line289,Arc140,Arc141,Line287,Arc142,Line293,Arc143,Line290]
FEATURE [Part::Part2DObjectPython] Line295  # Draft 2D object (typed FeaturePython)
  ChamferSize = 0
  Closed = false
  End = (163.75,-41,0)
  FilletRadius = 0
  Length = 13
  MakeFace = false
  Placement = pos=(163.75,-54,0) rot=(0,0,1;0rad)
  Points = (2) [(0,0,0),(0,13,0)]
  Start = (163.75,-54,0)
  Subdivisions = 0
FEATURE [Part::Part2DObjectPython] Arc144  # Draft 2D object (typed FeaturePython)
  FirstAngle = -90
  LastAngle = 0
  MakeFace = false
  Placement = pos=(163.25,-54,0) rot=(0,0,1;0rad)
  Radius = 0.5
FEATURE [Part::Part2DObjectPython] Arc145  # Draft 2D object (typed FeaturePython)
  FirstAngle = 0
  LastAngle = 90
  MakeFace = false
  Placement = pos=(163.25,-41,0) rot=(0,0,1;0rad)
  Radius = 0.5
FEATURE [Part::Part2DObjectPython] Line297  # Draft 2D object (typed FeaturePython)
  ChamferSize = 0
  Closed = false
  End = (163.25,-40.5,0)
  FilletRadius = 0
  Length = 13
  MakeFace = false
  Placement = pos=(150.25,-40.5,0) rot=(0,0,1;0rad)
  Points = (2) [(0,0,0),(13,0,0)]
  Start = (150.25,-40.5,0)
  Subdivisions = 0
FEATURE [Part::Part2DObjectPython] Line298  # Draft 2D object (typed FeaturePython)
  ChamferSize = 0
  Closed = false
  End = (149.75,-54,0)
  FilletRadius = 0
  Length = 13
  MakeFace = false
  Placement = pos=(149.75,-41,0) rot=(0,0,1;0rad)
  Points = (2) [(0,0,0),(0,-13,0)]
  Start = (149.75,-41,0)
  Subdivisions = 0
FEATURE [Part::Part2DObjectPython] Arc146  # Draft 2D object (typed FeaturePython)
  FirstAngle = 90
  LastAngle = 180
  MakeFace = false
  Placement = pos=(150.25,-41,0) rot=(0,0,1;0rad)
  Radius = 0.5
FEATURE [Part::Part2DObjectPython] Arc147  # Draft 2D object (typed FeaturePython)
  FirstAngle = 180
  LastAngle = 270
  MakeFace = false
  Placement = pos=(150.25,-54,0) rot=(0,0,1;0rad)
  Radius = 0.5
FEATURE [Part::Part2DObjectPython] Line301  # Draft 2D object (typed FeaturePython)
  ChamferSize = 0
  Closed = false
  End = (163.25,-54.5,0)
  FilletRadius = 0
  Length = 13
  MakeFace = false
  Placement = pos=(150.25,-54.5,0) rot=(0,0,1;0rad)
  Points = (2) [(0,0,0),(13,0,0)]
  Start = (150.25,-54.5,0)
  Subdivisions = 0
FEATURE [App::DocumentObjectGroup] Group044
  Group = -> [Line297,Arc145,Arc146,Line298,Arc147,Line301,Arc144,Line295]
FEATURE [Part::Part2DObjectPython] Line302  # Draft 2D object (typed FeaturePython)
  ChamferSize = 0
  Closed = false
  End = (168.75,-54,0)
  FilletRadius = 0
  Length = 13
  MakeFace = false
  Placement = pos=(168.75,-41,0) rot=(0,0,1;0rad)
  Points = (2) [(0,0,0),(0,-13,0)]
  Start = (168.75,-41,0)
  Subdivisions = 0
FEATURE [Part::Part2DObjectPython] Line304  # Draft 2D object (typed FeaturePython)
  ChamferSize = 0
  Closed = false
  End = (182.75,-41,0)
  FilletRadius = 0
  Length = 13
  MakeFace = false
  Placement = pos=(182.75,-54,0) rot=(0,0,1;0rad)
  Points = (2) [(0,0,0),(0,13,0)]
  Start = (182.75,-54,0)
  Subdivisions = 0
FEATURE [Part::Part2DObjectPython] Arc148  # Draft 2D object (typed FeaturePython)
  FirstAngle = -90
  LastAngle = 0
  MakeFace = false
  Placement = pos=(182.25,-54,0) rot=(0,0,1;0rad)
  Radius = 0.5
FEATURE [Part::Part2DObjectPython] Arc149  # Draft 2D object (typed FeaturePython)
  FirstAngle = 0
  LastAngle = 90
  MakeFace = false
  Placement = pos=(182.25,-41,0) rot=(0,0,1;0rad)
  Radius = 0.5
FEATURE [Part::Part2DObjectPython] Line306  # Draft 2D object (typed FeaturePython)
  ChamferSize = 0
  Closed = false
  End = (182.25,-40.5,0)
  FilletRadius = 0
  Length = 13
  MakeFace = false
  Placement = pos=(169.25,-40.5,0) rot=(0,0,1;0rad)
  Points = (2) [(0,0,0),(13,0,0)]
  Start = (169.25,-40.5,0)
  Subdivisions = 0
FEATURE [Part::Part2DObjectPython] Arc150  # Draft 2D object (typed FeaturePython)
  FirstAngle = 180
  LastAngle = 270
  MakeFace = false
  Placement = pos=(169.25,-54,0) rot=(0,0,1;0rad)
  Radius = 0.5
FEATURE [Part::Part2DObjectPython] Arc151  # Draft 2D object (typed FeaturePython)
  FirstAngle = 90
  LastAngle = 180
  MakeFace = false
  Placement = pos=(169.25,-41,0) rot=(0,0,1;0rad)
  Radius = 0.5
FEATURE [Part::Part2DObjectPython] Line308  # Draft 2D object (typed FeaturePython)
  ChamferSize = 0
  Closed = false
  End = (182.25,-54.5,0)
  FilletRadius = 0
  Length = 13
  MakeFace = false
  Placement = pos=(169.25,-54.5,0) rot=(0,0,1;0rad)
  Points = (2) [(0,0,0),(13,0,0)]
  Start = (169.25,-54.5,0)
  Subdivisions = 0
FEATURE [App::DocumentObjectGroup] Group045
  Group = -> [Line306,Arc149,Arc151,Line302,Arc150,Line308,Arc148,Line304]
FEATURE [Part::Part2DObjectPython] Line310  # Draft 2D object (typed FeaturePython)
  ChamferSize = 0
  Closed = false
  End = (201.75,-41,0)
  FilletRadius = 0
  Length = 13
  MakeFace = false
  Placement = pos=(201.75,-54,0) rot=(0,0,1;0rad)
  Points = (2) [(0,0,0),(0,13,0)]
  Start = (201.75,-54,0)
  Subdivisions = 0
FEATURE [Part::Part2DObjectPython] Arc152  # Draft 2D object (typed FeaturePython)
  FirstAngle = -90
  LastAngle = 0
  MakeFace = false
  Placement = pos=(201.25,-54,0) rot=(0,0,1;0rad)
  Radius = 0.5
FEATURE [Part::Part2DObjectPython] Line312  # Draft 2D object (typed FeaturePython)
  ChamferSize = 0
  Closed = false
  End = (187.75,-54,0)
  FilletRadius = 0
  Length = 13
  MakeFace = false
  Placement = pos=(187.75,-41,0) rot=(0,0,1;0rad)
  Points = (2) [(0,0,0),(0,-13,0)]
  Start = (187.75,-41,0)
  Subdivisions = 0
FEATURE [Part::Part2DObjectPython] Line313  # Draft 2D object (typed FeaturePython)
  ChamferSize = 0
  Closed = false
  End = (201.25,-40.5,0)
  FilletRadius = 0
  Length = 13
  MakeFace = false
  Placement = pos=(188.25,-40.5,0) rot=(0,0,1;0rad)
  Points = (2) [(0,0,0),(13,0,0)]
  Start = (188.25,-40.5,0)
  Subdivisions = 0
FEATURE [Part::Part2DObjectPython] Line314  # Draft 2D object (typed FeaturePython)
  ChamferSize = 0
  Closed = false
  End = (201.25,-54.5,0)
  FilletRadius = 0
  Length = 13
  MakeFace = false
  Placement = pos=(188.25,-54.5,0) rot=(0,0,1;0rad)
  Points = (2) [(0,0,0),(13,0,0)]
  Start = (188.25,-54.5,0)
  Subdivisions = 0
FEATURE [Part::Part2DObjectPython] Arc153  # Draft 2D object (typed FeaturePython)
  FirstAngle = 0
  LastAngle = 90
  MakeFace = false
  Placement = pos=(201.25,-41,0) rot=(0,0,1;0rad)
  Radius = 0.5
FEATURE [Part::Part2DObjectPython] Arc154  # Draft 2D object (typed FeaturePython)
  FirstAngle = 90
  LastAngle = 180
  MakeFace = false
  Placement = pos=(188.25,-41,0) rot=(0,0,1;0rad)
  Radius = 0.5
FEATURE [Part::Part2DObjectPython] Arc155  # Draft 2D object (typed FeaturePython)
  FirstAngle = 180
  LastAngle = 270
  MakeFace = false
  Placement = pos=(188.25,-54,0) rot=(0,0,1;0rad)
  Radius = 0.5
FEATURE [App::DocumentObjectGroup] Group046
  Group = -> [Line313,Arc153,Arc154,Line312,Arc155,Line314,Arc152,Line310]
FEATURE [Part::Part2DObjectPython] Line319  # Draft 2D object (typed FeaturePython)
  ChamferSize = 0
  Closed = false
  End = (206.75,-54,0)
  FilletRadius = 0
  Length = 13
  MakeFace = false
  Placement = pos=(206.75,-41,0) rot=(0,0,1;0rad)
  Points = (2) [(0,0,0),(0,-13,0)]
  Start = (206.75,-41,0)
  Subdivisions = 0
FEATURE [Part::Part2DObjectPython] Arc156  # Draft 2D object (typed FeaturePython)
  FirstAngle = 90
  LastAngle = 180
  MakeFace = false
  Placement = pos=(207.25,-41,0) rot=(0,0,1;0rad)
  Radius = 0.5
FEATURE [Part::Part2DObjectPython] Arc157  # Draft 2D object (typed FeaturePython)
  FirstAngle = 180
  LastAngle = 270
  MakeFace = false
  Placement = pos=(207.25,-54,0) rot=(0,0,1;0rad)
  Radius = 0.5
FEATURE [App::DocumentObjectGroup] Group047
  Group = -> [Arc156,Line319,Arc157]
FEATURE [Part::Part2DObjectPython] Arc161  # Draft 2D object (typed FeaturePython)
  FirstAngle = 90
  LastAngle = 180
  MakeFace = false
  Placement = pos=(228.625,-41,0) rot=(0,0,1;0rad)
  Radius = 0.5
FEATURE [Part::Part2DObjectPython] Line330  # Draft 2D object (typed FeaturePython)
  ChamferSize = 0
  Closed = false
  End = (228.125,-54,0)
  FilletRadius = 0
  Length = 13
  MakeFace = false
  Placement = pos=(228.125,-41,0) rot=(0,0,1;0rad)
  Points = (2) [(0,0,0),(0,-13,0)]
  Start = (228.125,-41,0)
  Subdivisions = 0
FEATURE [Part::Part2DObjectPython] Arc162  # Draft 2D object (typed FeaturePython)
  FirstAngle = 180
  LastAngle = 270
  MakeFace = false
  Placement = pos=(228.625,-54,0) rot=(0,0,1;0rad)
  Radius = 0.5
FEATURE [App::DocumentObjectGroup] Group048
  Group = -> [Arc161,Line330,Arc162]
FEATURE [Part::Part2DObjectPython] Arc164  # Draft 2D object (typed FeaturePython)
  FirstAngle = -90
  LastAngle = 0
  MakeFace = false
  Placement = pos=(222.625,-54,0) rot=(0,0,1;0rad)
  Radius = 0.5
FEATURE [Part::Part2DObjectPython] Arc165  # Draft 2D object (typed FeaturePython)
  FirstAngle = -90
  LastAngle = 0
  MakeFace = false
  Placement = pos=(244,-54,0) rot=(0,0,1;0rad)
  Radius = 0.5
FEATURE [Part::Part2DObjectPython] Line336  # Draft 2D object (typed FeaturePython)
  ChamferSize = 0
  Closed = false
  End = (244.5,-41,0)
  FilletRadius = 0
  Length = 13
  MakeFace = false
  Placement = pos=(244.5,-54,0) rot=(0,0,1;0rad)
  Points = (2) [(0,0,0),(0,13,0)]
  Start = (244.5,-54,0)
  Subdivisions = 0
FEATURE [Part::Part2DObjectPython] Arc168  # Draft 2D object (typed FeaturePython)
  FirstAngle = 0
  LastAngle = 90
  MakeFace = false
  Placement = pos=(222.625,-41,0) rot=(0,0,1;0rad)
  Radius = 0.5
FEATURE [Part::Part2DObjectPython] Line343  # Draft 2D object (typed FeaturePython)
  ChamferSize = 0
  Closed = false
  End = (223.125,-41,0)
  FilletRadius = 0
  Length = 13
  MakeFace = false
  Placement = pos=(223.125,-54,0) rot=(0,0,1;0rad)
  Points = (2) [(0,0,0),(0,13,0)]
  Start = (223.125,-54,0)
  Subdivisions = 0
FEATURE [Part::Part2DObjectPython] Arc169  # Draft 2D object (typed FeaturePython)
  FirstAngle = 0
  LastAngle = 90
  MakeFace = false
  Placement = pos=(244,-41,0) rot=(0,0,1;0rad)
  Radius = 0.5
FEATURE [App::DocumentObjectGroup] Group049
  Group = -> [Arc169,Arc165,Line336]
FEATURE [App::DocumentObjectGroup] Group050
  Group = -> [Line343,Arc168,Arc164]
FEATURE [Part::Part2DObjectPython] Arc176  # Draft 2D object (typed FeaturePython)
  FirstAngle = 90
  LastAngle = 180
  MakeFace = false
  Placement = pos=(243.188,-19.5,0) rot=(0,0,1;3.14159rad)
  Radius = 0.5
FEATURE [Part::Part2DObjectPython] Arc177  # Draft 2D object (typed FeaturePython)
  FirstAngle = 0
  LastAngle = 90
  MakeFace = false
  Placement = pos=(212.812,-19.5,0) rot=(0,0,1;3.14159rad)
  Radius = 0.5
FEATURE [Part::Part2DObjectPython] Line363  # Draft 2D object (typed FeaturePython)
  ChamferSize = 0
  Closed = false
  End = (243.188,-20,0)
  FilletRadius = 0
  Length = 30.376
  MakeFace = false
  Placement = pos=(212.812,-20,0) rot=(0,0,1;3.14159rad)
  Points = (2) [(0,0,0),(-30.376,0,0)]
  Start = (212.812,-20,0)
  Subdivisions = 0
FEATURE [Part::Part2DObjectPython] Arc178  # Draft 2D object (typed FeaturePython)
  FirstAngle = 180
  LastAngle = 270
  MakeFace = false
  Placement = pos=(243.188,-0.3,0) rot=(0,0,1;3.14159rad)
  Radius = 0.5
FEATURE [Part::Part2DObjectPython] Arc179  # Draft 2D object (typed FeaturePython)
  FirstAngle = -90
  LastAngle = 0
  MakeFace = false
  Placement = pos=(236.688,-0.3,0) rot=(0,0,1;3.14159rad)
  Radius = 0.5
FEATURE [Part::Part2DObjectPython] Line364  # Draft 2D object (typed FeaturePython)
  ChamferSize = 0
  Closed = false
  End = (236.688,0.2,0)
  FilletRadius = 0
  Length = 6.5
  MakeFace = false
  Placement = pos=(243.188,0.2,0) rot=(0,0,1;3.14159rad)
  Points = (2) [(0,0,0),(6.5,0,0)]
  Start = (243.188,0.2,0)
  Subdivisions = 0
FEATURE [Part::Part2DObjectPython] Arc180  # Draft 2D object (typed FeaturePython)
  FirstAngle = 90
  LastAngle = 180
  MakeFace = false
  Placement = pos=(235.688,-2,0) rot=(0,0,1;3.14159rad)
  Radius = 0.5
FEATURE [Part::Part2DObjectPython] Arc181  # Draft 2D object (typed FeaturePython)
  FirstAngle = -90
  LastAngle = 0
  MakeFace = false
  Placement = pos=(212.812,-0.3,0) rot=(0,0,1;3.14159rad)
  Radius = 0.5
FEATURE [Part::Part2DObjectPython] Line367  # Draft 2D object (typed FeaturePython)
  ChamferSize = 0
  Closed = false
  End = (212.812,0.2,0)
  FilletRadius = 0
  Length = 6.5
  MakeFace = false
  Placement = pos=(219.312,0.2,0) rot=(0,0,1;3.14159rad)
  Points = (2) [(0,0,0),(6.5,0,0)]
  Start = (219.312,0.2,0)
  Subdivisions = 0
FEATURE [Part::Part2DObjectPython] Arc182  # Draft 2D object (typed FeaturePython)
  FirstAngle = 180
  LastAngle = 270
  MakeFace = false
  Placement = pos=(219.312,-0.3,0) rot=(0,0,1;3.14159rad)
  Radius = 0.5
FEATURE [Part::Part2DObjectPython] Arc183  # Draft 2D object (typed FeaturePython)
  FirstAngle = 0
  LastAngle = 90
  MakeFace = false
  Placement = pos=(220.312,-2,0) rot=(0,0,1;3.14159rad)
  Radius = 0.5
FEATURE [Part::Part2DObjectPython] Line368  # Draft 2D object (typed FeaturePython)
  ChamferSize = 0
  Closed = false
  End = (236.188,-2,0)
  FilletRadius = 0
  Length = 1.7
  MakeFace = false
  Placement = pos=(236.188,-0.3,0) rot=(0,0,1;3.14159rad)
  Points = (2) [(0,0,0),(0,1.7,0)]
  Start = (236.188,-0.3,0)
  Subdivisions = 0
FEATURE [Part::Part2DObjectPython] Line369  # Draft 2D object (typed FeaturePython)
  ChamferSize = 0
  Closed = false
  End = (220.312,-2.5,0)
  FilletRadius = 0
  Length = 15.376
  MakeFace = false
  Placement = pos=(235.688,-2.5,0) rot=(0,0,1;3.14159rad)
  Points = (2) [(0,0,0),(15.376,0,0)]
  Start = (235.688,-2.5,0)
  Subdivisions = 0
FEATURE [Part::Part2DObjectPython] Line370  # Draft 2D object (typed FeaturePython)
  ChamferSize = 0
  Closed = false
  End = (219.812,-0.3,0)
  FilletRadius = 0
  Length = 1.7
  MakeFace = false
  Placement = pos=(219.812,-2,0) rot=(0,0,1;3.14159rad)
  Points = (2) [(0,0,0),(0,-1.7,0)]
  Start = (219.812,-2,0)
  Subdivisions = 0
FEATURE [Part::Part2DObjectPython] Line372  # Draft 2D object (typed FeaturePython)
  ChamferSize = 0
  Closed = false
  End = (18.875,-60,0)
  FilletRadius = 0
  Length = 13
  MakeFace = false
  Placement = pos=(18.875,-73,0) rot=(0,0,1;0rad)
  Points = (2) [(0,0,0),(0,13,0)]
  Start = (18.875,-73,0)
  Subdivisions = 0
FEATURE [Part::Part2DObjectPython] Arc184  # Draft 2D object (typed FeaturePython)
  FirstAngle = 0
  LastAngle = 90
  MakeFace = false
  Placement = pos=(18.375,-60,0) rot=(0,0,1;0rad)
  Radius = 0.5
FEATURE [Part::Part2DObjectPython] Arc185  # Draft 2D object (typed FeaturePython)
  FirstAngle = 90
  LastAngle = 180
  MakeFace = false
  Placement = pos=(5.375,-60,0) rot=(0,0,1;0rad)
  Radius = 0.5
FEATURE [Part::Part2DObjectPython] Line376  # Draft 2D object (typed FeaturePython)
  ChamferSize = 0
  Closed = false
  End = (4.875,-73,0)
  FilletRadius = 0
  Length = 13
  MakeFace = false
  Placement = pos=(4.875,-60,0) rot=(0,0,1;0rad)
  Points = (2) [(0,0,0),(0,-13,0)]
  Start = (4.875,-60,0)
  Subdivisions = 0
FEATURE [Part::Part2DObjectPython] Arc186  # Draft 2D object (typed FeaturePython)
  FirstAngle = 180
  LastAngle = 270
  MakeFace = false
  Placement = pos=(5.375,-73,0) rot=(0,0,1;0rad)
  Radius = 0.5
FEATURE [Part::Part2DObjectPython] Line377  # Draft 2D object (typed FeaturePython)
  ChamferSize = 0
  Closed = false
  End = (18.375,-59.5,0)
  FilletRadius = 0
  Length = 13
  MakeFace = false
  Placement = pos=(5.375,-59.5,0) rot=(0,0,1;0rad)
  Points = (2) [(0,0,0),(13,0,0)]
  Start = (5.375,-59.5,0)
  Subdivisions = 0
FEATURE [Part::Part2DObjectPython] Line378  # Draft 2D object (typed FeaturePython)
  ChamferSize = 0
  Closed = false
  End = (18.375,-73.5,0)
  FilletRadius = 0
  Length = 13
  MakeFace = false
  Placement = pos=(5.375,-73.5,0) rot=(0,0,1;0rad)
  Points = (2) [(0,0,0),(13,0,0)]
  Start = (5.375,-73.5,0)
  Subdivisions = 0
FEATURE [Part::Part2DObjectPython] Arc187  # Draft 2D object (typed FeaturePython)
  FirstAngle = -90
  LastAngle = 0
  MakeFace = false
  Placement = pos=(18.375,-73,0) rot=(0,0,1;0rad)
  Radius = 0.5
FEATURE [App::DocumentObjectGroup] Group053
  Group = -> [Line372,Arc184,Arc185,Line376,Arc186,Line377,Line378,Arc187]
FEATURE [Part::Part2DObjectPython] Arc188  # Draft 2D object (typed FeaturePython)
  FirstAngle = 90
  LastAngle = 180
  MakeFace = false
  Placement = pos=(29.125,-60,0) rot=(0,0,1;0rad)
  Radius = 0.5
FEATURE [Part::Part2DObjectPython] Arc189  # Draft 2D object (typed FeaturePython)
  FirstAngle = 0
  LastAngle = 90
  MakeFace = false
  Placement = pos=(42.125,-60,0) rot=(0,0,1;0rad)
  Radius = 0.5
FEATURE [Part::Part2DObjectPython] Line381  # Draft 2D object (typed FeaturePython)
  ChamferSize = 0
  Closed = false
  End = (42.625,-60,0)
  FilletRadius = 0
  Length = 13
  MakeFace = false
  Placement = pos=(42.625,-73,0) rot=(0,0,1;0rad)
  Points = (2) [(0,0,0),(0,13,0)]
  Start = (42.625,-73,0)
  Subdivisions = 0
FEATURE [Part::Part2DObjectPython] Line384  # Draft 2D object (typed FeaturePython)
  ChamferSize = 0
  Closed = false
  End = (28.625,-73,0)
  FilletRadius = 0
  Length = 13
  MakeFace = false
  Placement = pos=(28.625,-60,0) rot=(0,0,1;0rad)
  Points = (2) [(0,0,0),(0,-13,0)]
  Start = (28.625,-60,0)
  Subdivisions = 0
FEATURE [Part::Part2DObjectPython] Arc190  # Draft 2D object (typed FeaturePython)
  FirstAngle = 180
  LastAngle = 270
  MakeFace = false
  Placement = pos=(29.125,-73,0) rot=(0,0,1;0rad)
  Radius = 0.5
FEATURE [Part::Part2DObjectPython] Line385  # Draft 2D object (typed FeaturePython)
  ChamferSize = 0
  Closed = false
  End = (42.125,-59.5,0)
  FilletRadius = 0
  Length = 13
  MakeFace = false
  Placement = pos=(29.125,-59.5,0) rot=(0,0,1;0rad)
  Points = (2) [(0,0,0),(13,0,0)]
  Start = (29.125,-59.5,0)
  Subdivisions = 0
FEATURE [Part::Part2DObjectPython] Line386  # Draft 2D object (typed FeaturePython)
  ChamferSize = 0
  Closed = false
  End = (42.125,-73.5,0)
  FilletRadius = 0
  Length = 13
  MakeFace = false
  Placement = pos=(29.125,-73.5,0) rot=(0,0,1;0rad)
  Points = (2) [(0,0,0),(13,0,0)]
  Start = (29.125,-73.5,0)
  Subdivisions = 0
FEATURE [Part::Part2DObjectPython] Arc191  # Draft 2D object (typed FeaturePython)
  FirstAngle = -90
  LastAngle = 0
  MakeFace = false
  Placement = pos=(42.125,-73,0) rot=(0,0,1;0rad)
  Radius = 0.5
FEATURE [App::DocumentObjectGroup] Group054
  Group = -> [Line381,Arc189,Arc188,Line384,Arc190,Line385,Line386,Arc191]
FEATURE [Part::Part2DObjectPython] Arc193  # Draft 2D object (typed FeaturePython)
  FirstAngle = 90
  LastAngle = 180
  MakeFace = false
  Placement = pos=(50.5,-60,0) rot=(0,0,1;0rad)
  Radius = 0.5
FEATURE [Part::Part2DObjectPython] Line393  # Draft 2D object (typed FeaturePython)
  ChamferSize = 0
  Closed = false
  End = (50,-73,0)
  FilletRadius = 0
  Length = 13
  MakeFace = false
  Placement = pos=(50,-60,0) rot=(0,0,1;0rad)
  Points = (2) [(0,0,0),(0,-13,0)]
  Start = (50,-60,0)
  Subdivisions = 0
FEATURE [Part::Part2DObjectPython] Arc194  # Draft 2D object (typed FeaturePython)
  FirstAngle = 180
  LastAngle = 270
  MakeFace = false
  Placement = pos=(50.5,-73,0) rot=(0,0,1;0rad)
  Radius = 0.5
FEATURE [App::DocumentObjectGroup] Group055
  Group = -> [Arc193,Line393,Arc194]
FEATURE [Part::Part2DObjectPython] Arc196  # Draft 2D object (typed FeaturePython)
  FirstAngle = 180
  LastAngle = 270
  MakeFace = false
  Placement = pos=(69.5,-73,0) rot=(0,0,1;0rad)
  Radius = 0.5
FEATURE [Part::Part2DObjectPython] Arc199  # Draft 2D object (typed FeaturePython)
  FirstAngle = 90
  LastAngle = 180
  MakeFace = false
  Placement = pos=(69.5,-60,0) rot=(0,0,1;0rad)
  Radius = 0.5
FEATURE [Part::Part2DObjectPython] Line403  # Draft 2D object (typed FeaturePython)
  ChamferSize = 0
  Closed = false
  End = (69,-73,0)
  FilletRadius = 0
  Length = 13
  MakeFace = false
  Placement = pos=(69,-60,0) rot=(0,0,1;0rad)
  Points = (2) [(0,0,0),(0,-13,0)]
  Start = (69,-60,0)
  Subdivisions = 0
FEATURE [App::DocumentObjectGroup] Group056
  Group = -> [Arc199,Line403,Arc196]
FEATURE [Part::Part2DObjectPython] Line404  # Draft 2D object (typed FeaturePython)
  ChamferSize = 0
  Closed = false
  End = (109.125,-60,0)
  FilletRadius = 0
  Length = 13
  MakeFace = false
  Placement = pos=(109.125,-73,0) rot=(0,0,1;0rad)
  Points = (2) [(0,0,0),(0,13,0)]
  Start = (109.125,-73,0)
  Subdivisions = 0
FEATURE [Part::Part2DObjectPython] Arc200  # Draft 2D object (typed FeaturePython)
  FirstAngle = -90
  LastAngle = 0
  MakeFace = false
  Placement = pos=(108.625,-73,0) rot=(0,0,1;0rad)
  Radius = 0.5
FEATURE [Part::Part2DObjectPython] Arc202  # Draft 2D object (typed FeaturePython)
  FirstAngle = 0
  LastAngle = 90
  MakeFace = false
  Placement = pos=(108.625,-60,0) rot=(0,0,1;0rad)
  Radius = 0.5
FEATURE [App::DocumentObjectGroup] Group057  label="1.75u space"
  Group = -> [Arc202,Line404,Arc200]
FEATURE [Part::Part2DObjectPython] Line420  # Draft 2D object (typed FeaturePython)
  ChamferSize = 0
  Closed = false
  End = (122.062,-75.7,0)
  FilletRadius = 0
  Length = 19.2
  MakeFace = false
  Placement = pos=(122.062,-56.5,0) rot=(0,0,1;0rad)
  Points = (2) [(0,0,0),(4.26326e-14,-19.2,0)]
  Start = (122.062,-56.5,0)
  Subdivisions = 0
FEATURE [Part::Part2DObjectPython] Arc206  # Draft 2D object (typed FeaturePython)
  FirstAngle = 180
  LastAngle = 270
  MakeFace = false
  Placement = pos=(122.562,-75.7,0) rot=(0,0,1;0rad)
  Radius = 0.5
FEATURE [Part::Part2DObjectPython] Arc208  # Draft 2D object (typed FeaturePython)
  FirstAngle = 180
  LastAngle = 270
  MakeFace = false
  Placement = pos=(146.438,-75.7,0) rot=(0,0,1;0rad)
  Radius = 0.5
FEATURE [Part::Part2DObjectPython] Arc210  # Draft 2D object (typed FeaturePython)
  FirstAngle = 90
  LastAngle = 180
  MakeFace = false
  Placement = pos=(122.562,-56.5,0) rot=(0,0,1;0rad)
  Radius = 0.5
FEATURE [Part::Part2DObjectPython] Arc211  # Draft 2D object (typed FeaturePython)
  FirstAngle = 0
  LastAngle = 90
  MakeFace = false
  Placement = pos=(145.438,-74,0) rot=(0,0,1;0rad)
  Radius = 0.5
FEATURE [Part::Part2DObjectPython] Line422  # Draft 2D object (typed FeaturePython)
  ChamferSize = 0
  Closed = false
  End = (145.938,-75.7,0)
  FilletRadius = 0
  Length = 1.7
  MakeFace = false
  Placement = pos=(145.938,-74,0) rot=(0,0,1;0rad)
  Points = (2) [(0,0,0),(0,-1.7,0)]
  Start = (145.938,-74,0)
  Subdivisions = 0
FEATURE [App::DocumentObjectGroup] Group058  label="2u space"
  Group = -> [Arc210,Arc206,Line420,Arc208,Arc211,Line422]
FEATURE [Part::Part2DObjectPython] Arc212  # Draft 2D object (typed FeaturePython)
  FirstAngle = 180
  LastAngle = 270
  MakeFace = false
  Placement = pos=(159.75,-73,0) rot=(0,0,1;0rad)
  Radius = 0.5
FEATURE [Part::Part2DObjectPython] Arc215  # Draft 2D object (typed FeaturePython)
  FirstAngle = 90
  LastAngle = 180
  MakeFace = false
  Placement = pos=(159.75,-60,0) rot=(0,0,1;0rad)
  Radius = 0.5
FEATURE [Part::Part2DObjectPython] Line431  # Draft 2D object (typed FeaturePython)
  ChamferSize = 0
  Closed = false
  End = (159.25,-73,0)
  FilletRadius = 0
  Length = 13
  MakeFace = false
  Placement = pos=(159.25,-60,0) rot=(0,0,1;0rad)
  Points = (2) [(0,0,0),(0,-13,0)]
  Start = (159.25,-60,0)
  Subdivisions = 0
FEATURE [App::DocumentObjectGroup] Group059
  Group = -> [Arc215,Line431,Arc212]
FEATURE [App::DocumentObjectGroup] Group060
FEATURE [Part::Part2DObjectPython] Arc221  # Draft 2D object (typed FeaturePython)
  FirstAngle = 90
  LastAngle = 180
  MakeFace = false
  Placement = pos=(204.875,-60,0) rot=(0,0,1;0rad)
  Radius = 0.5
FEATURE [Part::Part2DObjectPython] Arc223  # Draft 2D object (typed FeaturePython)
  FirstAngle = 180
  LastAngle = 270
  MakeFace = false
  Placement = pos=(204.875,-73,0) rot=(0,0,1;0rad)
  Radius = 0.5
FEATURE [Part::Part2DObjectPython] Line446  # Draft 2D object (typed FeaturePython)
  ChamferSize = 0
  Closed = false
  End = (204.375,-73,0)
  FilletRadius = 0
  Length = 13
  MakeFace = false
  Placement = pos=(204.375,-60,0) rot=(0,0,1;0rad)
  Points = (2) [(0,0,0),(0,-13,0)]
  Start = (204.375,-60,0)
  Subdivisions = 0
FEATURE [App::DocumentObjectGroup] Group061
  Group = -> [Arc221,Line446,Arc223]
FEATURE [Part::Part2DObjectPython] Arc224  # Draft 2D object (typed FeaturePython)
  FirstAngle = -90
  LastAngle = 0
  MakeFace = false
  Placement = pos=(241.625,-73,0) rot=(0,0,1;0rad)
  Radius = 0.5
FEATURE [Part::Part2DObjectPython] Line451  # Draft 2D object (typed FeaturePython)
  ChamferSize = 0
  Closed = false
  End = (228.125,-73,0)
  FilletRadius = 0
  Length = 13
  MakeFace = false
  Placement = pos=(228.125,-60,0) rot=(0,0,1;0rad)
  Points = (2) [(0,0,0),(0,-13,0)]
  Start = (228.125,-60,0)
  Subdivisions = 0
FEATURE [Part::Part2DObjectPython] Line452  # Draft 2D object (typed FeaturePython)
  ChamferSize = 0
  Closed = false
  End = (241.625,-59.5,0)
  FilletRadius = 0
  Length = 13
  MakeFace = false
  Placement = pos=(228.625,-59.5,0) rot=(0,0,1;0rad)
  Points = (2) [(0,0,0),(13,0,0)]
  Start = (228.625,-59.5,0)
  Subdivisions = 0
FEATURE [Part::Part2DObjectPython] Line453  # Draft 2D object (typed FeaturePython)
  ChamferSize = 0
  Closed = false
  End = (242.125,-60,0)
  FilletRadius = 0
  Length = 13
  MakeFace = false
  Placement = pos=(242.125,-73,0) rot=(0,0,1;0rad)
  Points = (2) [(0,0,0),(0,13,0)]
  Start = (242.125,-73,0)
  Subdivisions = 0
FEATURE [Part::Part2DObjectPython] Arc225  # Draft 2D object (typed FeaturePython)
  FirstAngle = 90
  LastAngle = 180
  MakeFace = false
  Placement = pos=(228.625,-60,0) rot=(0,0,1;0rad)
  Radius = 0.5
FEATURE [Part::Part2DObjectPython] Arc226  # Draft 2D object (typed FeaturePython)
  FirstAngle = 0
  LastAngle = 90
  MakeFace = false
  Placement = pos=(241.625,-60,0) rot=(0,0,1;0rad)
  Radius = 0.5
FEATURE [Part::Part2DObjectPython] Arc227  # Draft 2D object (typed FeaturePython)
  FirstAngle = 180
  LastAngle = 270
  MakeFace = false
  Placement = pos=(228.625,-73,0) rot=(0,0,1;0rad)
  Radius = 0.5
FEATURE [Part::Part2DObjectPython] Line455  # Draft 2D object (typed FeaturePython)
  ChamferSize = 0
  Closed = false
  End = (241.625,-73.5,0)
  FilletRadius = 0
  Length = 13
  MakeFace = false
  Placement = pos=(228.625,-73.5,0) rot=(0,0,1;0rad)
  Points = (2) [(0,0,0),(13,0,0)]
  Start = (228.625,-73.5,0)
  Subdivisions = 0
FEATURE [App::DocumentObjectGroup] Group062
  Group = -> [Line453,Arc226,Arc225,Line451,Arc227,Line452,Line455,Arc224]
FEATURE [App::DocumentObjectGroup] Group063  label="split 1"
  Group = -> [Group053,Group054,Group055,Group056,Group057,Group058,Group059,Group060,Group061,Group062]
FEATURE [Part::Part2DObjectPython] Arc229  # Draft 2D object (typed FeaturePython)
  FirstAngle = 0
  LastAngle = 90
  MakeFace = false
  Placement = pos=(65.875,-60,0) rot=(0,0,1;0rad)
  Radius = 0.5
FEATURE [Part::Part2DObjectPython] Line457  # Draft 2D object (typed FeaturePython)
  ChamferSize = 0
  Closed = false
  End = (66.375,-60,0)
  FilletRadius = 0
  Length = 13
  MakeFace = false
  Placement = pos=(66.375,-73,0) rot=(0,0,1;0rad)
  Points = (2) [(0,0,0),(0,13,0)]
  Start = (66.375,-73,0)
  Subdivisions = 0
FEATURE [Part::Part2DObjectPython] Arc231  # Draft 2D object (typed FeaturePython)
  FirstAngle = -90
  LastAngle = 0
  MakeFace = false
  Placement = pos=(65.875,-73,0) rot=(0,0,1;0rad)
  Radius = 0.5
FEATURE [App::DocumentObjectGroup] Group065
  Group = -> [Line457,Arc229,Arc231]
FEATURE [Part::Part2DObjectPython] Arc232  # Draft 2D object (typed FeaturePython)
  FirstAngle = 0
  LastAngle = 90
  MakeFace = false
  Placement = pos=(100.313,-74,0) rot=(0,0,1;0rad)
  Radius = 0.5
FEATURE [Part::Part2DObjectPython] Line469  # Draft 2D object (typed FeaturePython)
  ChamferSize = 0
  Closed = false
  End = (100.813,-75.7,0)
  FilletRadius = 0
  Length = 1.7
  MakeFace = false
  Placement = pos=(100.813,-74,0) rot=(0,0,1;0rad)
  Points = (2) [(0,0,0),(0,-1.7,0)]
  Start = (100.813,-74,0)
  Subdivisions = 0
FEATURE [Part::Part2DObjectPython] Line470  # Draft 2D object (typed FeaturePython)
  ChamferSize = 0
  Closed = false
  End = (84.437,-74,0)
  FilletRadius = 0
  Length = 1.7
  MakeFace = false
  Placement = pos=(84.437,-75.7,0) rot=(0,0,1;0rad)
  Points = (2) [(0,0,0),(0,1.7,0)]
  Start = (84.437,-75.7,0)
  Subdivisions = 0
FEATURE [Part::Part2DObjectPython] Arc233  # Draft 2D object (typed FeaturePython)
  FirstAngle = 180
  LastAngle = 270
  MakeFace = false
  Placement = pos=(77.437,-75.7,0) rot=(0,0,1;0rad)
  Radius = 0.5
FEATURE [Part::Part2DObjectPython] Arc234  # Draft 2D object (typed FeaturePython)
  FirstAngle = -90
  LastAngle = 0
  MakeFace = false
  Placement = pos=(107.813,-75.7,0) rot=(0,0,1;0rad)
  Radius = 0.5
FEATURE [Part::Part2DObjectPython] Line471  # Draft 2D object (typed FeaturePython)
  ChamferSize = 0
  Closed = false
  End = (77.437,-56,0)
  FilletRadius = 0
  Length = 30.376
  MakeFace = false
  Placement = pos=(107.813,-56,0) rot=(0,0,1;0rad)
  Points = (2) [(0,0,0),(-30.376,0,0)]
  Start = (107.813,-56,0)
  Subdivisions = 0
FEATURE [Part::Part2DObjectPython] Line472  # Draft 2D object (typed FeaturePython)
  ChamferSize = 0
  Closed = false
  End = (83.937,-76.2,0)
  FilletRadius = 0
  Length = 6.5
  MakeFace = false
  Placement = pos=(77.437,-76.2,0) rot=(0,0,1;0rad)
  Points = (2) [(0,0,0),(6.5,0,0)]
  Start = (77.437,-76.2,0)
  Subdivisions = 0
FEATURE [Part::Part2DObjectPython] Arc235  # Draft 2D object (typed FeaturePython)
  FirstAngle = 0
  LastAngle = 90
  MakeFace = false
  Placement = pos=(107.813,-56.5,0) rot=(0,0,1;0rad)
  Radius = 0.5
FEATURE [Part::Part2DObjectPython] Line474  # Draft 2D object (typed FeaturePython)
  ChamferSize = 0
  Closed = false
  End = (100.313,-73.5,0)
  FilletRadius = 0
  Length = 15.376
  MakeFace = false
  Placement = pos=(84.937,-73.5,0) rot=(0,0,1;0rad)
  Points = (2) [(0,0,0),(15.376,0,0)]
  Start = (84.937,-73.5,0)
  Subdivisions = 0
FEATURE [Part::Part2DObjectPython] Line475  # Draft 2D object (typed FeaturePython)
  ChamferSize = 0
  Closed = false
  End = (107.813,-76.2,0)
  FilletRadius = 0
  Length = 6.5
  MakeFace = false
  Placement = pos=(101.313,-76.2,0) rot=(0,0,1;0rad)
  Points = (2) [(0,0,0),(6.5,0,0)]
  Start = (101.313,-76.2,0)
  Subdivisions = 0
FEATURE [Part::Part2DObjectPython] Arc236  # Draft 2D object (typed FeaturePython)
  FirstAngle = 180
  LastAngle = 270
  MakeFace = false
  Placement = pos=(101.313,-75.7,0) rot=(0,0,1;0rad)
  Radius = 0.5
FEATURE [Part::Part2DObjectPython] Arc237  # Draft 2D object (typed FeaturePython)
  FirstAngle = -90
  LastAngle = 0
  MakeFace = false
  Placement = pos=(83.937,-75.7,0) rot=(0,0,1;0rad)
  Radius = 0.5
FEATURE [Part::Part2DObjectPython] Arc238  # Draft 2D object (typed FeaturePython)
  FirstAngle = 90
  LastAngle = 180
  MakeFace = false
  Placement = pos=(77.437,-56.5,0) rot=(0,0,1;0rad)
  Radius = 0.5
FEATURE [Part::Part2DObjectPython] Arc239  # Draft 2D object (typed FeaturePython)
  FirstAngle = 90
  LastAngle = 180
  MakeFace = false
  Placement = pos=(84.937,-74,0) rot=(0,0,1;0rad)
  Radius = 0.5
FEATURE [App::DocumentObjectGroup] Group066  label="2.25u space"
  Group = -> [Arc232,Line469,Line470,Arc233,Arc234,Line471,Line472,Arc235,Line474,Line475,Arc236,Arc237,Arc238,Arc239]
FEATURE [Part::Part2DObjectPython] Arc240  # Draft 2D object (typed FeaturePython)
  FirstAngle = 90
  LastAngle = 180
  MakeFace = false
  Placement = pos=(132.437,-74,0) rot=(0,0,1;0rad)
  Radius = 0.5
FEATURE [Part::Part2DObjectPython] Line480  # Draft 2D object (typed FeaturePython)
  ChamferSize = 0
  Closed = false
  End = (155.813,-56.5,0)
  FilletRadius = 0
  Length = 19.2
  MakeFace = false
  Placement = pos=(155.813,-75.7,0) rot=(0,0,1;3.14159rad)
  Points = (2) [(0,0,0),(0,-19.2,0)]
  Start = (155.813,-75.7,0)
  Subdivisions = 0
FEATURE [Part::Part2DObjectPython] Line482  # Draft 2D object (typed FeaturePython)
  ChamferSize = 0
  Closed = false
  End = (131.937,-74,0)
  FilletRadius = 0
  Length = 1.7
  MakeFace = false
  Placement = pos=(131.937,-75.7,0) rot=(0,0,1;0rad)
  Points = (2) [(0,0,0),(0,1.7,0)]
  Start = (131.937,-75.7,0)
  Subdivisions = 0
FEATURE [Part::Part2DObjectPython] Arc243  # Draft 2D object (typed FeaturePython)
  FirstAngle = -90
  LastAngle = 0
  MakeFace = false
  Placement = pos=(131.437,-75.7,0) rot=(0,0,1;0rad)
  Radius = 0.5
FEATURE [Part::Part2DObjectPython] Arc245  # Draft 2D object (typed FeaturePython)
  FirstAngle = 0
  LastAngle = 90
  MakeFace = false
  Placement = pos=(155.313,-56.5,0) rot=(0,0,1;0rad)
  Radius = 0.5
FEATURE [Part::Part2DObjectPython] Arc246  # Draft 2D object (typed FeaturePython)
  FirstAngle = -90
  LastAngle = 0
  MakeFace = false
  Placement = pos=(155.313,-75.7,0) rot=(0,0,1;0rad)
  Radius = 0.5
FEATURE [App::DocumentObjectGroup] Group067  label="2.75u space"
  Group = -> [Arc240,Line480,Line482,Arc243,Arc245,Arc246]
FEATURE [App::DocumentObjectGroup] Group068
FEATURE [Part::Part2DObjectPython] Arc252  # Draft 2D object (typed FeaturePython)
  FirstAngle = 0
  LastAngle = 90
  MakeFace = false
  Placement = pos=(201.25,-60,0) rot=(0,0,1;0rad)
  Radius = 0.5
FEATURE [Part::Part2DObjectPython] Line500  # Draft 2D object (typed FeaturePython)
  ChamferSize = 0
  Closed = false
  End = (201.75,-60,0)
  FilletRadius = 0
  Length = 13
  MakeFace = false
  Placement = pos=(201.75,-73,0) rot=(0,0,1;0rad)
  Points = (2) [(0,0,0),(0,13,0)]
  Start = (201.75,-73,0)
  Subdivisions = 0
FEATURE [Part::Part2DObjectPython] Arc253  # Draft 2D object (typed FeaturePython)
  FirstAngle = -90
  LastAngle = 0
  MakeFace = false
  Placement = pos=(201.25,-73,0) rot=(0,0,1;0rad)
  Radius = 0.5
FEATURE [App::DocumentObjectGroup] Group069
  Group = -> [Arc252,Arc253,Line500]
FEATURE [Part::Part2DObjectPython] Arc256  # Draft 2D object (typed FeaturePython)
  FirstAngle = 0
  LastAngle = 90
  MakeFace = false
  Placement = pos=(220.25,-60,0) rot=(0,0,1;0rad)
  Radius = 0.5
FEATURE [Part::Part2DObjectPython] Arc257  # Draft 2D object (typed FeaturePython)
  FirstAngle = -90
  LastAngle = 0
  MakeFace = false
  Placement = pos=(220.25,-73,0) rot=(0,0,1;0rad)
  Radius = 0.5
FEATURE [Part::Part2DObjectPython] Line508  # Draft 2D object (typed FeaturePython)
  ChamferSize = 0
  Closed = false
  End = (220.75,-60,0)
  FilletRadius = 0
  Length = 13
  MakeFace = false
  Placement = pos=(220.75,-73,0) rot=(0,0,1;0rad)
  Points = (2) [(0,0,0),(0,13,0)]
  Start = (220.75,-73,0)
  Subdivisions = 0
FEATURE [App::DocumentObjectGroup] Group070
  Group = -> [Arc256,Arc257,Line508]
FEATURE [App::DocumentObjectGroup] Group064  label="split 2"
  Group = -> [Group065,Group066,Group067,Group068,Group069,Group070]
FEATURE [Part::Part2DObjectPython] Line512  # Draft 2D object (typed FeaturePython)
  ChamferSize = 0
  Closed = false
  End = (18.875,-60,0)
  FilletRadius = 0
  Length = 13
  MakeFace = false
  Placement = pos=(18.875,-73,0) rot=(0,0,1;0rad)
  Points = (2) [(0,0,0),(0,13,0)]
  Start = (18.875,-73,0)
  Subdivisions = 0
FEATURE [Part::Part2DObjectPython] Arc260  # Draft 2D object (typed FeaturePython)
  FirstAngle = 0
  LastAngle = 90
  MakeFace = false
  Placement = pos=(18.375,-60,0) rot=(0,0,1;0rad)
  Radius = 0.5
FEATURE [Part::Part2DObjectPython] Arc261  # Draft 2D object (typed FeaturePython)
  FirstAngle = 90
  LastAngle = 180
  MakeFace = false
  Placement = pos=(5.375,-60,0) rot=(0,0,1;0rad)
  Radius = 0.5
FEATURE [Part::Part2DObjectPython] Line516  # Draft 2D object (typed FeaturePython)
  ChamferSize = 0
  Closed = false
  End = (4.875,-73,0)
  FilletRadius = 0
  Length = 13
  MakeFace = false
  Placement = pos=(4.875,-60,0) rot=(0,0,1;0rad)
  Points = (2) [(0,0,0),(0,-13,0)]
  Start = (4.875,-60,0)
  Subdivisions = 0
FEATURE [Part::Part2DObjectPython] Arc262  # Draft 2D object (typed FeaturePython)
  FirstAngle = 180
  LastAngle = 270
  MakeFace = false
  Placement = pos=(5.375,-73,0) rot=(0,0,1;0rad)
  Radius = 0.5
FEATURE [Part::Part2DObjectPython] Line517  # Draft 2D object (typed FeaturePython)
  ChamferSize = 0
  Closed = false
  End = (18.375,-59.5,0)
  FilletRadius = 0
  Length = 13
  MakeFace = false
  Placement = pos=(5.375,-59.5,0) rot=(0,0,1;0rad)
  Points = (2) [(0,0,0),(13,0,0)]
  Start = (5.375,-59.5,0)
  Subdivisions = 0
FEATURE [Part::Part2DObjectPython] Line518  # Draft 2D object (typed FeaturePython)
  ChamferSize = 0
  Closed = false
  End = (18.375,-73.5,0)
  FilletRadius = 0
  Length = 13
  MakeFace = false
  Placement = pos=(5.375,-73.5,0) rot=(0,0,1;0rad)
  Points = (2) [(0,0,0),(13,0,0)]
  Start = (5.375,-73.5,0)
  Subdivisions = 0
FEATURE [Part::Part2DObjectPython] Arc263  # Draft 2D object (typed FeaturePython)
  FirstAngle = -90
  LastAngle = 0
  MakeFace = false
  Placement = pos=(18.375,-73,0) rot=(0,0,1;0rad)
  Radius = 0.5
FEATURE [App::DocumentObjectGroup] Group072
  Group = -> [Line512,Arc260,Arc261,Line516,Arc262,Line517,Line518,Arc263]
FEATURE [Part::Part2DObjectPython] Line522  # Draft 2D object (typed FeaturePython)
  ChamferSize = 0
  Closed = false
  End = (39.75,-59.5,0)
  FilletRadius = 0
  Length = 13
  MakeFace = false
  Placement = pos=(26.75,-59.5,0) rot=(0,0,1;0rad)
  Points = (2) [(0,0,0),(13,0,0)]
  Start = (26.75,-59.5,0)
  Subdivisions = 0
FEATURE [Part::Part2DObjectPython] Arc264  # Draft 2D object (typed FeaturePython)
  FirstAngle = 0
  LastAngle = 90
  MakeFace = false
  Placement = pos=(39.75,-60,0) rot=(0,0,1;0rad)
  Radius = 0.5
FEATURE [Part::Part2DObjectPython] Arc265  # Draft 2D object (typed FeaturePython)
  FirstAngle = 90
  LastAngle = 180
  MakeFace = false
  Placement = pos=(26.75,-60,0) rot=(0,0,1;0rad)
  Radius = 0.5
FEATURE [Part::Part2DObjectPython] Line525  # Draft 2D object (typed FeaturePython)
  ChamferSize = 0
  Closed = false
  End = (26.25,-73,0)
  FilletRadius = 0
  Length = 13
  MakeFace = false
  Placement = pos=(26.25,-60,0) rot=(0,0,1;0rad)
  Points = (2) [(0,0,0),(0,-13,0)]
  Start = (26.25,-60,0)
  Subdivisions = 0
FEATURE [Part::Part2DObjectPython] Arc266  # Draft 2D object (typed FeaturePython)
  FirstAngle = 180
  LastAngle = 270
  MakeFace = false
  Placement = pos=(26.75,-73,0) rot=(0,0,1;0rad)
  Radius = 0.5
FEATURE [Part::Part2DObjectPython] Line526  # Draft 2D object (typed FeaturePython)
  ChamferSize = 0
  Closed = false
  End = (39.75,-73.5,0)
  FilletRadius = 0
  Length = 13
  MakeFace = false
  Placement = pos=(26.75,-73.5,0) rot=(0,0,1;0rad)
  Points = (2) [(0,0,0),(13,0,0)]
  Start = (26.75,-73.5,0)
  Subdivisions = 0
FEATURE [Part::Part2DObjectPython] Arc267  # Draft 2D object (typed FeaturePython)
  FirstAngle = -90
  LastAngle = 0
  MakeFace = false
  Placement = pos=(39.75,-73,0) rot=(0,0,1;0rad)
  Radius = 0.5
FEATURE [Part::Part2DObjectPython] Line527  # Draft 2D object (typed FeaturePython)
  ChamferSize = 0
  Closed = false
  End = (40.25,-60,0)
  FilletRadius = 0
  Length = 13
  MakeFace = false
  Placement = pos=(40.25,-73,0) rot=(0,0,1;0rad)
  Points = (2) [(0,0,0),(0,13,0)]
  Start = (40.25,-73,0)
  Subdivisions = 0
FEATURE [App::DocumentObjectGroup] Group073
  Group = -> [Line522,Arc264,Arc265,Line525,Arc266,Line526,Arc267,Line527]
FEATURE [Part::Part2DObjectPython] Line529  # Draft 2D object (typed FeaturePython)
  ChamferSize = 0
  Closed = false
  End = (61.625,-60,0)
  FilletRadius = 0
  Length = 13
  MakeFace = false
  Placement = pos=(61.625,-73,0) rot=(0,0,1;0rad)
  Points = (2) [(0,0,0),(0,13,0)]
  Start = (61.625,-73,0)
  Subdivisions = 0
FEATURE [Part::Part2DObjectPython] Arc268  # Draft 2D object (typed FeaturePython)
  FirstAngle = 0
  LastAngle = 90
  MakeFace = false
  Placement = pos=(61.125,-60,0) rot=(0,0,1;0rad)
  Radius = 0.5
FEATURE [Part::Part2DObjectPython] Arc271  # Draft 2D object (typed FeaturePython)
  FirstAngle = -90
  LastAngle = 0
  MakeFace = false
  Placement = pos=(61.125,-73,0) rot=(0,0,1;0rad)
  Radius = 0.5
FEATURE [App::DocumentObjectGroup] Group074
  Group = -> [Line529,Arc268,Arc271]
FEATURE [Part::Part2DObjectPython] Line540  # Draft 2D object (typed FeaturePython)
  ChamferSize = 0
  Closed = false
  End = (140,-60,0)
  FilletRadius = 0
  Length = 13
  MakeFace = false
  Placement = pos=(140,-73,0) rot=(0,0,1;0rad)
  Points = (2) [(0,0,0),(0,13,0)]
  Start = (140,-73,0)
  Subdivisions = 0
FEATURE [Part::Part2DObjectPython] Arc274  # Draft 2D object (typed FeaturePython)
  FirstAngle = 90
  LastAngle = 180
  MakeFace = false
  Placement = pos=(140.5,-60,0) rot=(0,0,1;0rad)
  Radius = 0.5
FEATURE [Part::Part2DObjectPython] Arc275  # Draft 2D object (typed FeaturePython)
  FirstAngle = -90
  LastAngle = 0
  MakeFace = false
  Placement = pos=(139.5,-73,0) rot=(0,0,1;0rad)
  Radius = 0.5
FEATURE [Part::Part2DObjectPython] Line543  # Draft 2D object (typed FeaturePython)
  ChamferSize = 0
  Closed = false
  End = (139.5,-73.5,0)
  FilletRadius = 0
  Length = 13
  MakeFace = false
  Placement = pos=(126.5,-73.5,0) rot=(0,0,1;0rad)
  Points = (2) [(0,0,0),(13,0,0)]
  Start = (126.5,-73.5,0)
  Subdivisions = 0
FEATURE [Part::Part2DObjectPython] Arc277  # Draft 2D object (typed FeaturePython)
  FirstAngle = 0
  LastAngle = 90
  MakeFace = false
  Placement = pos=(193.4,-56.5,0) rot=(0,0,1;0rad)
  Radius = 0.5
FEATURE [Part::Part2DObjectPython] Arc279  # Draft 2D object (typed FeaturePython)
  FirstAngle = -90
  LastAngle = 0
  MakeFace = false
  Placement = pos=(79.1,-75.7,0) rot=(0,0,1;0rad)
  Radius = 0.5
FEATURE [Part::Part2DObjectPython] Arc280  # Draft 2D object (typed FeaturePython)
  FirstAngle = 90
  LastAngle = 180
  MakeFace = false
  Placement = pos=(80.1,-60,0) rot=(0,0,1;0rad)
  Radius = 0.5
FEATURE [Part::Part2DObjectPython] Line554  # Draft 2D object (typed FeaturePython)
  ChamferSize = 0
  Closed = false
  End = (79.6,-75.7,0)
  FilletRadius = 0
  Length = 15.7
  MakeFace = false
  Placement = pos=(79.6,-60,0) rot=(0,0,1;0rad)
  Points = (2) [(0,0,0),(0,-15.7,0)]
  Start = (79.6,-60,0)
  Subdivisions = 0
FEATURE [Part::Part2DObjectPython] Arc281  # Draft 2D object (typed FeaturePython)
  FirstAngle = 180
  LastAngle = 270
  MakeFace = false
  Placement = pos=(186.9,-75.7,0) rot=(0,0,1;0rad)
  Radius = 0.5
FEATURE [Part::Part2DObjectPython] Line558  # Draft 2D object (typed FeaturePython)
  ChamferSize = 0
  Closed = false
  End = (193.4,-76.2,0)
  FilletRadius = 0
  Length = 6.5
  MakeFace = false
  Placement = pos=(186.9,-76.2,0) rot=(0,0,1;0rad)
  Points = (2) [(0,0,0),(6.5,0,0)]
  Start = (186.9,-76.2,0)
  Subdivisions = 0
FEATURE [Part::Part2DObjectPython] Arc282  # Draft 2D object (typed FeaturePython)
  FirstAngle = -90
  LastAngle = 0
  MakeFace = false
  Placement = pos=(193.4,-75.7,0) rot=(0,0,1;0rad)
  Radius = 0.5
FEATURE [Part::Part2DObjectPython] Arc283  # Draft 2D object (typed FeaturePython)
  FirstAngle = 0
  LastAngle = 90
  MakeFace = false
  Placement = pos=(182.5,-60,0) rot=(0,0,1;0rad)
  Radius = 0.5
FEATURE [App::DocumentObjectGroup] Group075  label="7u space"
  Group = -> [Line540,Arc274,Arc275,Line543,Arc277,Arc279,Arc280,Line554,Arc281,Line558,Arc282,Arc283]
FEATURE [Part::Part2DObjectPython] Line563  # Draft 2D object (typed FeaturePython)
  ChamferSize = 0
  Closed = false
  End = (218.375,-60,0)
  FilletRadius = 0
  Length = 13
  MakeFace = false
  Placement = pos=(218.375,-73,0) rot=(0,0,1;0rad)
  Points = (2) [(0,0,0),(0,13,0)]
  Start = (218.375,-73,0)
  Subdivisions = 0
FEATURE [Part::Part2DObjectPython] Arc284  # Draft 2D object (typed FeaturePython)
  FirstAngle = 0
  LastAngle = 90
  MakeFace = false
  Placement = pos=(217.875,-60,0) rot=(0,0,1;0rad)
  Radius = 0.5
FEATURE [Part::Part2DObjectPython] Line566  # Draft 2D object (typed FeaturePython)
  ChamferSize = 0
  Closed = false
  End = (204.375,-73,0)
  FilletRadius = 0
  Length = 13
  MakeFace = false
  Placement = pos=(204.375,-60,0) rot=(0,0,1;0rad)
  Points = (2) [(0,0,0),(0,-13,0)]
  Start = (204.375,-60,0)
  Subdivisions = 0
FEATURE [Part::Part2DObjectPython] Arc285  # Draft 2D object (typed FeaturePython)
  FirstAngle = 180
  LastAngle = 270
  MakeFace = false
  Placement = pos=(204.875,-73,0) rot=(0,0,1;0rad)
  Radius = 0.5
FEATURE [Part::Part2DObjectPython] Line567  # Draft 2D object (typed FeaturePython)
  ChamferSize = 0
  Closed = false
  End = (217.875,-59.5,0)
  FilletRadius = 0
  Length = 13
  MakeFace = false
  Placement = pos=(204.875,-59.5,0) rot=(0,0,1;0rad)
  Points = (2) [(0,0,0),(13,0,0)]
  Start = (204.875,-59.5,0)
  Subdivisions = 0
FEATURE [Part::Part2DObjectPython] Arc286  # Draft 2D object (typed FeaturePython)
  FirstAngle = 90
  LastAngle = 180
  MakeFace = false
  Placement = pos=(204.875,-60,0) rot=(0,0,1;0rad)
  Radius = 0.5
FEATURE [Part::Part2DObjectPython] Arc287  # Draft 2D object (typed FeaturePython)
  FirstAngle = -90
  LastAngle = 0
  MakeFace = false
  Placement = pos=(217.875,-73,0) rot=(0,0,1;0rad)
  Radius = 0.5
FEATURE [Part::Part2DObjectPython] Line569  # Draft 2D object (typed FeaturePython)
  ChamferSize = 0
  Closed = false
  End = (217.875,-73.5,0)
  FilletRadius = 0
  Length = 13
  MakeFace = false
  Placement = pos=(204.875,-73.5,0) rot=(0,0,1;0rad)
  Points = (2) [(0,0,0),(13,0,0)]
  Start = (204.875,-73.5,0)
  Subdivisions = 0
FEATURE [App::DocumentObjectGroup] Group076
  Group = -> [Line563,Arc284,Arc286,Line566,Arc285,Line567,Line569,Arc287]
FEATURE [Part::Part2DObjectPython] Line571  # Draft 2D object (typed FeaturePython)
  ChamferSize = 0
  Closed = false
  End = (241.625,-73.5,0)
  FilletRadius = 0
  Length = 13
  MakeFace = false
  Placement = pos=(228.625,-73.5,0) rot=(0,0,1;0rad)
  Points = (2) [(0,0,0),(13,0,0)]
  Start = (228.625,-73.5,0)
  Subdivisions = 0
FEATURE [Part::Part2DObjectPython] Line573  # Draft 2D object (typed FeaturePython)
  ChamferSize = 0
  Closed = false
  End = (242.125,-60,0)
  FilletRadius = 0
  Length = 13
  MakeFace = false
  Placement = pos=(242.125,-73,0) rot=(0,0,1;0rad)
  Points = (2) [(0,0,0),(0,13,0)]
  Start = (242.125,-73,0)
  Subdivisions = 0
FEATURE [Part::Part2DObjectPython] Arc288  # Draft 2D object (typed FeaturePython)
  FirstAngle = 0
  LastAngle = 90
  MakeFace = false
  Placement = pos=(241.625,-60,0) rot=(0,0,1;0rad)
  Radius = 0.5
FEATURE [Part::Part2DObjectPython] Arc289  # Draft 2D object (typed FeaturePython)
  FirstAngle = 180
  LastAngle = 270
  MakeFace = false
  Placement = pos=(228.625,-73,0) rot=(0,0,1;0rad)
  Radius = 0.5
FEATURE [Part::Part2DObjectPython] Line576  # Draft 2D object (typed FeaturePython)
  ChamferSize = 0
  Closed = false
  End = (241.625,-59.5,0)
  FilletRadius = 0
  Length = 13
  MakeFace = false
  Placement = pos=(228.625,-59.5,0) rot=(0,0,1;0rad)
  Points = (2) [(0,0,0),(13,0,0)]
  Start = (228.625,-59.5,0)
  Subdivisions = 0
FEATURE [Part::Part2DObjectPython] Line577  # Draft 2D object (typed FeaturePython)
  ChamferSize = 0
  Closed = false
  End = (228.125,-73,0)
  FilletRadius = 0
  Length = 13
  MakeFace = false
  Placement = pos=(228.125,-60,0) rot=(0,0,1;0rad)
  Points = (2) [(0,0,0),(0,-13,0)]
  Start = (228.125,-60,0)
  Subdivisions = 0
FEATURE [Part::Part2DObjectPython] Arc290  # Draft 2D object (typed FeaturePython)
  FirstAngle = -90
  LastAngle = 0
  MakeFace = false
  Placement = pos=(241.625,-73,0) rot=(0,0,1;0rad)
  Radius = 0.5
FEATURE [Part::Part2DObjectPython] Arc291  # Draft 2D object (typed FeaturePython)
  FirstAngle = 90
  LastAngle = 180
  MakeFace = false
  Placement = pos=(228.625,-60,0) rot=(0,0,1;0rad)
  Radius = 0.5
FEATURE [App::DocumentObjectGroup] Group077
  Group = -> [Line573,Arc288,Arc291,Line577,Arc289,Line576,Line571,Arc290]
FEATURE [App::DocumentObjectGroup] Group078  label="full 1"
  Group = -> [Group072,Group073,Group074,Group075,Group076,Group077]
FEATURE [Part::Part2DObjectPython] Arc293  # Draft 2D object (typed FeaturePython)
  FirstAngle = 90
  LastAngle = 180
  MakeFace = false
  Placement = pos=(45.75,-60,0) rot=(0,0,1;0rad)
  Radius = 0.5
FEATURE [Part::Part2DObjectPython] Line584  # Draft 2D object (typed FeaturePython)
  ChamferSize = 0
  Closed = false
  End = (45.25,-73,0)
  FilletRadius = 0
  Length = 13
  MakeFace = false
  Placement = pos=(45.25,-60,0) rot=(0,0,1;0rad)
  Points = (2) [(0,0,0),(0,-13,0)]
  Start = (45.25,-60,0)
  Subdivisions = 0
FEATURE [Part::Part2DObjectPython] Arc294  # Draft 2D object (typed FeaturePython)
  FirstAngle = 180
  LastAngle = 270
  MakeFace = false
  Placement = pos=(45.75,-73,0) rot=(0,0,1;0rad)
  Radius = 0.5
FEATURE [App::DocumentObjectGroup] Group080
  Group = -> [Arc293,Line584,Arc294]
FEATURE [Part::Part2DObjectPython] Arc296  # Draft 2D object (typed FeaturePython)
  FirstAngle = 90
  LastAngle = 180
  MakeFace = false
  Placement = pos=(67.837,-56.5,0) rot=(0,0,1;0rad)
  Radius = 0.5
FEATURE [Part::Part2DObjectPython] Arc297  # Draft 2D object (typed FeaturePython)
  FirstAngle = 180
  LastAngle = 270
  MakeFace = false
  Placement = pos=(114.625,-73,0) rot=(0,0,1;0rad)
  Radius = 0.5
FEATURE [Part::Part2DObjectPython] Line587  # Draft 2D object (typed FeaturePython)
  ChamferSize = 0
  Closed = false
  End = (127.625,-73.5,0)
  FilletRadius = 0
  Length = 13
  MakeFace = false
  Placement = pos=(114.625,-73.5,0) rot=(0,0,1;0rad)
  Points = (2) [(0,0,0),(13,0,0)]
  Start = (114.625,-73.5,0)
  Subdivisions = 0
FEATURE [Part::Part2DObjectPython] Line589  # Draft 2D object (typed FeaturePython)
  ChamferSize = 0
  Closed = false
  End = (114.125,-73,0)
  FilletRadius = 0
  Length = 13
  MakeFace = false
  Placement = pos=(114.125,-60,0) rot=(0,0,1;0rad)
  Points = (2) [(0,0,0),(0,-13,0)]
  Start = (114.125,-60,0)
  Subdivisions = 0
FEATURE [Part::Part2DObjectPython] Arc300  # Draft 2D object (typed FeaturePython)
  FirstAngle = 0
  LastAngle = 90
  MakeFace = false
  Placement = pos=(113.625,-60,0) rot=(0,0,1;0rad)
  Radius = 0.5
FEATURE [Part::Part2DObjectPython] Line596  # Draft 2D object (typed FeaturePython)
  ChamferSize = 0
  Closed = false
  End = (67.337,-75.7,0)
  FilletRadius = 0
  Length = 19.2
  MakeFace = false
  Placement = pos=(67.337,-56.5,0) rot=(0,0,1;0rad)
  Points = (2) [(0,0,0),(0,-19.2,0)]
  Start = (67.337,-56.5,0)
  Subdivisions = 0
FEATURE [Part::Part2DObjectPython] Arc302  # Draft 2D object (typed FeaturePython)
  FirstAngle = -90
  LastAngle = 0
  MakeFace = false
  Placement = pos=(174.413,-75.7,0) rot=(0,0,1;0rad)
  Radius = 0.5
FEATURE [Part::Part2DObjectPython] Arc304  # Draft 2D object (typed FeaturePython)
  FirstAngle = 180
  LastAngle = 270
  MakeFace = false
  Placement = pos=(67.837,-75.7,0) rot=(0,0,1;0rad)
  Radius = 0.5
FEATURE [Part::Part2DObjectPython] Line599  # Draft 2D object (typed FeaturePython)
  ChamferSize = 0
  Closed = false
  End = (174.413,-76.2,0)
  FilletRadius = 0
  Length = 6.5
  MakeFace = false
  Placement = pos=(167.913,-76.2,0) rot=(0,0,1;0rad)
  Points = (2) [(0,0,0),(6.5,0,0)]
  Start = (167.913,-76.2,0)
  Subdivisions = 0
FEATURE [Part::Part2DObjectPython] Arc306  # Draft 2D object (typed FeaturePython)
  FirstAngle = 0
  LastAngle = 90
  MakeFace = false
  Placement = pos=(166.913,-60,0) rot=(0,0,1;0rad)
  Radius = 0.5
FEATURE [Part::Part2DObjectPython] Line601  # Draft 2D object (typed FeaturePython)
  ChamferSize = 0
  Closed = false
  End = (167.413,-75.7,0)
  FilletRadius = 0
  Length = 15.7
  MakeFace = false
  Placement = pos=(167.413,-60,0) rot=(0,0,1;0rad)
  Points = (2) [(0,0,0),(0,-15.7,0)]
  Start = (167.413,-60,0)
  Subdivisions = 0
FEATURE [Part::Part2DObjectPython] Arc307  # Draft 2D object (typed FeaturePython)
  FirstAngle = 180
  LastAngle = 270
  MakeFace = false
  Placement = pos=(167.913,-75.7,0) rot=(0,0,1;0rad)
  Radius = 0.5
FEATURE [App::DocumentObjectGroup] Group082  label="6.25u space"
  Group = -> [Arc300,Line589,Arc297,Line587,Arc296,Arc304,Line596,Arc307,Line599,Arc302,Arc306,Line601]
FEATURE [Part::Part2DObjectPython] Arc308  # Draft 2D object (typed FeaturePython)
  FirstAngle = 0
  LastAngle = 90
  MakeFace = false
  Placement = pos=(196.5,-60,0) rot=(0,0,1;0rad)
  Radius = 0.5
FEATURE [Part::Part2DObjectPython] Line610  # Draft 2D object (typed FeaturePython)
  ChamferSize = 0
  Closed = false
  End = (197,-60,0)
  FilletRadius = 0
  Length = 13
  MakeFace = false
  Placement = pos=(197,-73,0) rot=(0,0,1;0rad)
  Points = (2) [(0,0,0),(0,13,0)]
  Start = (197,-73,0)
  Subdivisions = 0
FEATURE [Part::Part2DObjectPython] Arc310  # Draft 2D object (typed FeaturePython)
  FirstAngle = 180
  LastAngle = 270
  MakeFace = false
  Placement = pos=(183.5,-73,0) rot=(0,0,1;0rad)
  Radius = 0.5
FEATURE [Part::Part2DObjectPython] Arc311  # Draft 2D object (typed FeaturePython)
  FirstAngle = -90
  LastAngle = 0
  MakeFace = false
  Placement = pos=(196.5,-73,0) rot=(0,0,1;0rad)
  Radius = 0.5
FEATURE [Part::Part2DObjectPython] Line616  # Draft 2D object (typed FeaturePython)
  ChamferSize = 0
  Closed = false
  End = (183,-73,0)
  FilletRadius = 0
  Length = 13
  MakeFace = false
  Placement = pos=(183,-60,0) rot=(0,0,1;0rad)
  Points = (2) [(0,0,0),(0,-13,0)]
  Start = (183,-60,0)
  Subdivisions = 0
FEATURE [App::DocumentObjectGroup] Group083
  Group = -> [Arc308,Line616,Arc310,Arc311,Line610]
FEATURE [App::DocumentObjectGroup] Group079  label="full 2"
  Group = -> [Group080,Group082,Group083]
FEATURE [Part::Part2DObjectPython] Line617  # Draft 2D object (typed FeaturePython)
  ChamferSize = 0
  Closed = false
  End = (23.5,-27.5,0)
  FilletRadius = 0
  Length = 3
  MakeFace = false
  Placement = pos=(20.5,-27.5,0) rot=(0,0,1;0rad)
  Points = (2) [(0,0,0),(3,0,0)]
  Start = (20.5,-27.5,0)
  Subdivisions = 0
FEATURE [Part::Part2DObjectPython] Line618  # Draft 2D object (typed FeaturePython)
  ChamferSize = 0
  Closed = false
  End = (24,-28,0)
  FilletRadius = 0
  Length = 1
  MakeFace = false
  Placement = pos=(24,-29,0) rot=(0,0,1;0rad)
  Points = (2) [(0,0,0),(0,1,0)]
  Start = (24,-29,0)
  Subdivisions = 0
FEATURE [Part::Part2DObjectPython] Arc312  # Draft 2D object (typed FeaturePython)
  FirstAngle = 0
  LastAngle = 90
  MakeFace = false
  Placement = pos=(23.5,-28,0) rot=(0,0,1;0rad)
  Radius = 0.5
FEATURE [Part::Part2DObjectPython] Arc313  # Draft 2D object (typed FeaturePython)
  FirstAngle = 90
  LastAngle = 180
  MakeFace = false
  Placement = pos=(20.5,-28,0) rot=(0,0,1;0rad)
  Radius = 0.5
FEATURE [Part::Part2DObjectPython] Line619  # Draft 2D object (typed FeaturePython)
  ChamferSize = 0
  Closed = false
  End = (20,-29,0)
  FilletRadius = 0
  Length = 1
  MakeFace = false
  Placement = pos=(20,-28,0) rot=(0,0,1;0rad)
  Points = (2) [(0,0,0),(0,-1,0)]
  Start = (20,-28,0)
  Subdivisions = 0
FEATURE [Part::Part2DObjectPython] Arc314  # Draft 2D object (typed FeaturePython)
  FirstAngle = 0
  LastAngle = 90
  MakeFace = false
  Placement = pos=(20.5,-29,0) rot=(0,0,1;3.14159rad)
  Radius = 0.5
FEATURE [Part::Part2DObjectPython] Line621  # Draft 2D object (typed FeaturePython)
  ChamferSize = 0
  Closed = false
  End = (20.5,-29.5,0)
  FilletRadius = 0
  Length = 3
  MakeFace = false
  Placement = pos=(23.5,-29.5,0) rot=(0,0,1;3.14159rad)
  Points = (2) [(0,0,0),(3,0,0)]
  Start = (23.5,-29.5,0)
  Subdivisions = 0
FEATURE [Part::Part2DObjectPython] Arc315  # Draft 2D object (typed FeaturePython)
  FirstAngle = 90
  LastAngle = 180
  MakeFace = false
  Placement = pos=(23.5,-29,0) rot=(0,0,1;3.14159rad)
  Radius = 0.5
FEATURE [Part::Part2DObjectPython] Line623  # Draft 2D object (typed FeaturePython)
  ChamferSize = 0
  Closed = false
  End = (30.5,-43,0)
  FilletRadius = 0
  Length = 5
  MakeFace = false
  Placement = pos=(25.5,-43,0) rot=(0,0,1;0rad)
  Points = (2) [(0,0,0),(5,0,0)]
  Start = (25.5,-43,0)
  Subdivisions = 0
FEATURE [Part::Part2DObjectPython] Line624  # Draft 2D object (typed FeaturePython)
  ChamferSize = 0
  Closed = false
  End = (31,-43.5,0)
  FilletRadius = 0
  Length = 8
  MakeFace = false
  Placement = pos=(31,-51.5,0) rot=(0,0,1;0rad)
  Points = (2) [(0,0,0),(0,8,0)]
  Start = (31,-51.5,0)
  Subdivisions = 0
FEATURE [Part::Part2DObjectPython] Arc316  # Draft 2D object (typed FeaturePython)
  FirstAngle = 90
  LastAngle = 180
  MakeFace = false
  Placement = pos=(25.5,-43.5,0) rot=(0,0,1;0rad)
  Radius = 0.5
FEATURE [Part::Part2DObjectPython] Arc317  # Draft 2D object (typed FeaturePython)
  FirstAngle = 0
  LastAngle = 90
  MakeFace = false
  Placement = pos=(30.5,-43.5,0) rot=(0,0,1;0rad)
  Radius = 0.5
FEATURE [Part::Part2DObjectPython] Arc318  # Draft 2D object (typed FeaturePython)
  FirstAngle = 90
  LastAngle = 180
  MakeFace = false
  Placement = pos=(30.5,-51.5,0) rot=(0,0,1;3.14159rad)
  Radius = 0.5
FEATURE [Part::Part2DObjectPython] Line626  # Draft 2D object (typed FeaturePython)
  ChamferSize = 0
  Closed = false
  End = (25.5,-52,0)
  FilletRadius = 0
  Length = 5
  MakeFace = false
  Placement = pos=(30.5,-52,0) rot=(0,0,1;3.14159rad)
  Points = (2) [(0,0,0),(5,2.13163e-14,0)]
  Start = (30.5,-52,0)
  Subdivisions = 0
FEATURE [Part::Part2DObjectPython] Arc319  # Draft 2D object (typed FeaturePython)
  FirstAngle = 0
  LastAngle = 90
  MakeFace = false
  Placement = pos=(25.5,-51.5,0) rot=(0,0,1;3.14159rad)
  Radius = 0.5
FEATURE [Part::Part2DObjectPython] Line627  # Draft 2D object (typed FeaturePython)
  ChamferSize = 0
  Closed = false
  End = (25,-43.5,0)
  FilletRadius = 0
  Length = 8
  MakeFace = false
  Placement = pos=(25,-51.5,0) rot=(0,0,1;0rad)
  Points = (2) [(0,0,0),(0,8,0)]
  Start = (25,-51.5,0)
  Subdivisions = 0
FEATURE [App::DocumentObjectGroup] Group084  label="Reset"
  Group = -> [Line623,Line624,Arc316,Arc317,Arc318,Line626,Arc319,Line627]
FEATURE [App::DocumentObjectGroup] Group085  label="LED"
  Group = -> [Line617,Line618,Arc312,Arc313,Line619,Arc314,Line621,Arc315]
FEATURE [Part::Part2DObjectPython] Arc320  # Draft 2D object (typed FeaturePython)
  FirstAngle = 0
  LastAngle = 90
  MakeFace = false
  Placement = pos=(251,4,0) rot=(0,0,1;0rad)
  Radius = 5
FEATURE [Part::Part2DObjectPython] Arc321  # Draft 2D object (typed FeaturePython)
  FirstAngle = -90
  LastAngle = 0
  MakeFace = false
  Placement = pos=(251,-80,0) rot=(0,0,1;0rad)
  Radius = 5
FEATURE [Part::Part2DObjectPython] Line628  # Draft 2D object (typed FeaturePython)
  ChamferSize = 0
  Closed = false
  End = (256,-80,0)
  FilletRadius = 0
  Length = 84
  MakeFace = false
  Placement = pos=(256,4,0) rot=(0,0,1;0rad)
  Points = (2) [(0,0,0),(0,-84,0)]
  Start = (256,4,0)
  Subdivisions = 0
FEATURE [Part::Part2DObjectPython] Arc322  # Draft 2D object (typed FeaturePython)
  FirstAngle = 90
  LastAngle = 180
  MakeFace = false
  Placement = pos=(-4,4,0) rot=(0,0,1;0rad)
  Radius = 5
FEATURE [Part::Part2DObjectPython] Arc323  # Draft 2D object (typed FeaturePython)
  FirstAngle = -180
  LastAngle = -90
  MakeFace = false
  Placement = pos=(-4,-80,0) rot=(0,0,1;0rad)
  Radius = 5
FEATURE [Part::Part2DObjectPython] Line629  # Draft 2D object (typed FeaturePython)
  ChamferSize = 0
  Closed = false
  End = (-4,-85,0)
  FilletRadius = 0
  Length = 255
  MakeFace = false
  Placement = pos=(251,-85,0) rot=(0,0,1;0rad)
  Points = (2) [(0,0,0),(-255,0,0)]
  Start = (251,-85,0)
  Subdivisions = 0
FEATURE [Part::Part2DObjectPython] Line631  # Draft 2D object (typed FeaturePython)
  ChamferSize = 0
  Closed = false
  End = (-9,4,0)
  FilletRadius = 0
  Length = 84
  MakeFace = false
  Placement = pos=(-9,-80,0) rot=(0,0,1;0rad)
  Points = (2) [(0,0,0),(0,84,0)]
  Start = (-9,-80,0)
  Subdivisions = 0
FEATURE [Part::Part2DObjectPython] Arc324  # Draft 2D object (typed FeaturePython)
  FirstAngle = 90
  LastAngle = 180
  MakeFace = true
  Placement = pos=(-0.5,0.5,0) rot=(0,0,1;0rad)
  Radius = 0.5
FEATURE [Part::Part2DObjectPython] Arc325  # Draft 2D object (typed FeaturePython)
  FirstAngle = 0
  LastAngle = 90
  MakeFace = true
  Placement = pos=(-0.5,-76.5,0) rot=(0,0,1;3.14159rad)
  Radius = 0.5
FEATURE [Part::Part2DObjectPython] Arc326  # Draft 2D object (typed FeaturePython)
  FirstAngle = 90
  LastAngle = 180
  MakeFace = true
  Placement = pos=(247.5,-76.5,0) rot=(0,0,1;3.14159rad)
  Radius = 0.5
FEATURE [Part::Part2DObjectPython] Line632  # Draft 2D object (typed FeaturePython)
  ChamferSize = 0
  Closed = false
  End = (248,0.5,0)
  FilletRadius = 0
  Length = 77
  MakeFace = true
  Placement = pos=(248,-76.5,0) rot=(0,0,1;0rad)
  Points = (2) [(0,0,0),(0,77,0)]
  Start = (248,-76.5,0)
  Subdivisions = 0
FEATURE [Part::Part2DObjectPython] Arc327  # Draft 2D object (typed FeaturePython)
  FirstAngle = 0
  LastAngle = 90
  MakeFace = true
  Placement = pos=(247.5,0.5,0) rot=(0,0,1;0rad)
  Radius = 0.5
FEATURE [Part::Part2DObjectPython] Line634  # Draft 2D object (typed FeaturePython)
  ChamferSize = 0
  Closed = false
  End = (-1,-76.5,0)
  FilletRadius = 0
  Length = 77
  MakeFace = true
  Placement = pos=(-1,0.5,0) rot=(0,0,1;0rad)
  Points = (2) [(0,0,0),(0,-77,0)]
  Start = (-1,0.5,0)
  Subdivisions = 0
FEATURE [Part::Part2DObjectPython] Line635  # Draft 2D object (typed FeaturePython)
  ChamferSize = 0
  Closed = false
  End = (247.5,-77,0)
  FilletRadius = 0
  Length = 248
  MakeFace = true
  Placement = pos=(-0.5,-77,0) rot=(0,0,1;0rad)
  Points = (2) [(0,0,0),(248,-2.84217e-14,0)]
  Start = (-0.5,-77,0)
  Subdivisions = 0
FEATURE [App::DocumentObjectGroup] Group087  label="Bottom inside base"
  Group = -> [Arc324,Arc327,Arc325,Arc326,Line632,Line634,Line635]
FEATURE [Part::Part2DObjectPython] Line636  # Draft 2D object (typed FeaturePython)
  ChamferSize = 0
  Closed = false
  End = (-7,4,0)
  FilletRadius = 0
  Length = 84
  MakeFace = true
  Placement = pos=(-7,-80,0) rot=(0,0,1;0rad)
  Points = (2) [(0,0,0),(0,84,0)]
  Start = (-7,-80,0)
  Subdivisions = 0
FEATURE [Part::Part2DObjectPython] Arc328  # Draft 2D object (typed FeaturePython)
  FirstAngle = 90
  LastAngle = 180
  MakeFace = true
  Placement = pos=(-4,4,0) rot=(0,0,1;0rad)
  Radius = 3
FEATURE [Part::Part2DObjectPython] Arc329  # Draft 2D object (typed FeaturePython)
  FirstAngle = 0
  LastAngle = 90
  MakeFace = true
  Placement = pos=(-4,-80,0) rot=(0,0,1;3.14159rad)
  Radius = 3
FEATURE [Part::Part2DObjectPython] Line638  # Draft 2D object (typed FeaturePython)
  ChamferSize = 0
  Closed = false
  End = (254,-80,0)
  FilletRadius = 0
  Length = 84
  MakeFace = true
  Placement = pos=(254,4,0) rot=(0,0,1;0rad)
  Points = (2) [(0,0,0),(0,-84,0)]
  Start = (254,4,0)
  Subdivisions = 0
FEATURE [Part::Part2DObjectPython] Line639  # Draft 2D object (typed FeaturePython)
  ChamferSize = 0
  Closed = false
  End = (-4,-83,0)
  FilletRadius = 0
  Length = 255
  MakeFace = true
  Placement = pos=(251,-83,0) rot=(0,0,1;0rad)
  Points = (2) [(0,0,0),(-255,2.84217e-14,0)]
  Start = (251,-83,0)
  Subdivisions = 0
FEATURE [Part::Part2DObjectPython] Arc330  # Draft 2D object (typed FeaturePython)
  FirstAngle = 0
  LastAngle = 90
  MakeFace = true
  Placement = pos=(251,4,0) rot=(0,0,1;0rad)
  Radius = 3
FEATURE [Part::Part2DObjectPython] Arc331  # Draft 2D object (typed FeaturePython)
  FirstAngle = 90
  LastAngle = 180
  MakeFace = true
  Placement = pos=(251,-80,0) rot=(0,0,1;3.14159rad)
  Radius = 3
FEATURE [App::DocumentObjectGroup] Group089  label="Top"
  Group = -> [Group002,Group004,Group005]
FEATURE [Part::Part2DObjectPython] Arc332  # Draft 2D object (typed FeaturePython)
  FirstAngle = 180
  LastAngle = 270
  MakeFace = false
  Placement = pos=(12.365,-6,0) rot=(0,0,1;0rad)
  Radius = 1
FEATURE [Part::Part2DObjectPython] Line641  # Draft 2D object (typed FeaturePython)
  ChamferSize = 0
  Closed = false
  End = (24.365,-7,0)
  FilletRadius = 0
  Length = 12
  MakeFace = false
  Placement = pos=(12.365,-7,0) rot=(0,0,1;0rad)
  Points = (2) [(0,0,0),(12,0,0)]
  Start = (12.365,-7,0)
  Subdivisions = 0
FEATURE [Part::Part2DObjectPython] Arc333  # Draft 2D object (typed FeaturePython)
  FirstAngle = -90
  LastAngle = 0
  MakeFace = false
  Placement = pos=(24.365,-6,0) rot=(0,0,1;0rad)
  Radius = 1
FEATURE [Part::Part2DObjectPython] Arc334  # Draft 2D object (typed FeaturePython)
  FirstAngle = 0
  LastAngle = 90
  MakeFace = false
  Placement = pos=(10.365,6,0) rot=(0,0,1;0rad)
  Radius = 1
FEATURE [Part::Part2DObjectPython] Line645  # Draft 2D object (typed FeaturePython)
  ChamferSize = 0
  Closed = false
  End = (11.365,-6,0)
  FilletRadius = 0
  Length = 12
  MakeFace = false
  Placement = pos=(11.365,6,0) rot=(0,0,1;0rad)
  Points = (2) [(0,0,0),(0,-12,0)]
  Start = (11.365,6,0)
  Subdivisions = 0
FEATURE [Part::Part2DObjectPython] Line646  # Draft 2D object (typed FeaturePython)
  ChamferSize = 0
  Closed = false
  End = (-4,7,0)
  FilletRadius = 0
  Length = 14.365
  MakeFace = false
  Placement = pos=(10.365,7,0) rot=(0,0,1;0rad)
  Points = (2) [(0,0,0),(-14.365,0,0)]
  Start = (10.365,7,0)
  Subdivisions = 0
FEATURE [Part::Part2DObjectPython] Arc335  # Draft 2D object (typed FeaturePython)
  FirstAngle = 90
  LastAngle = 180
  MakeFace = false
  Placement = pos=(26.365,6,0) rot=(0,0,1;0rad)
  Radius = 1
FEATURE [Part::Part2DObjectPython] Line647  # Draft 2D object (typed FeaturePython)
  ChamferSize = 0
  Closed = false
  End = (25.365,-6,0)
  FilletRadius = 0
  Length = 12
  MakeFace = false
  Placement = pos=(25.365,6,0) rot=(0,0,1;0rad)
  Points = (2) [(0,0,0),(0,-12,0)]
  Start = (25.365,6,0)
  Subdivisions = 0
FEATURE [Part::Part2DObjectPython] Line648  # Draft 2D object (typed FeaturePython)
  ChamferSize = 0
  Closed = false
  End = (251,7,0)
  FilletRadius = 0
  Length = 224.635
  MakeFace = false
  Placement = pos=(26.365,7,0) rot=(0,0,1;0rad)
  Points = (2) [(0,0,0),(224.635,0,0)]
  Start = (26.365,7,0)
  Subdivisions = 0
FEATURE [App::DocumentObjectGroup] Group088  label="Bottom layer 3mm"
  Group = -> [Arc328,Arc330,Arc329,Arc331,Line638,Line639,Line636,Arc332,Line641,Arc333,Arc334,Line645,Line646,Arc335,Line647,Line648]
FEATURE [Part::Part2DObjectPython] Arc336  # Draft 2D object (typed FeaturePython)
  FirstAngle = 90
  LastAngle = 180
  MakeFace = false
  Placement = pos=(26.365,8,0) rot=(0,0,1;0rad)
  Radius = 1
FEATURE [Part::Part2DObjectPython] Arc337  # Draft 2D object (typed FeaturePython)
  FirstAngle = 180
  LastAngle = 270
  MakeFace = false
  Placement = pos=(26.365,2,0) rot=(0,0,1;0rad)
  Radius = 1
FEATURE [Part::Part2DObjectPython] Arc339  # Draft 2D object (typed FeaturePython)
  FirstAngle = 90
  LastAngle = 180
  MakeFace = false
  Placement = pos=(10.365,2,0) rot=(0,0,1;3.14159rad)
  Radius = 1
FEATURE [Part::Part2DObjectPython] Line650  # Draft 2D object (typed FeaturePython)
  ChamferSize = 0
  Closed = false
  End = (10.365,1,0)
  FilletRadius = 0
  Length = 10.865
  MakeFace = false
  Placement = pos=(-0.5,1,0) rot=(0,0,1;0rad)
  Points = (2) [(0,0,0),(10.865,0,0)]
  Start = (-0.5,1,0)
  Subdivisions = 0
FEATURE [Part::Part2DObjectPython] Line652  # Draft 2D object (typed FeaturePython)
  ChamferSize = 0
  Closed = false
  End = (25.365,8,0)
  FilletRadius = 0
  Length = 6
  MakeFace = false
  Placement = pos=(25.365,2,0) rot=(0,0,1;0rad)
  Points = (2) [(0,0,0),(0,6,0)]
  Start = (25.365,2,0)
  Subdivisions = 0
FEATURE [Part::Part2DObjectPython] Line653  # Draft 2D object (typed FeaturePython)
  ChamferSize = 0
  Closed = false
  End = (251,9,0)
  FilletRadius = 0
  Length = 224.635
  MakeFace = false
  Placement = pos=(26.365,9,0) rot=(0,0,1;0rad)
  Points = (2) [(0,0,0),(224.635,0,0)]
  Start = (26.365,9,0)
  Subdivisions = 0
FEATURE [Part::Part2DObjectPython] Line654  # Draft 2D object (typed FeaturePython)
  ChamferSize = 0
  Closed = false
  End = (26.365,1,0)
  FilletRadius = 0
  Length = 221.135
  MakeFace = false
  Placement = pos=(247.5,1,0) rot=(0,0,1;0rad)
  Points = (2) [(0,0,0),(-221.135,0,0)]
  Start = (247.5,1,0)
  Subdivisions = 0
FEATURE [Part::Part2DObjectPython] Arc340  # Draft 2D object (typed FeaturePython)
  FirstAngle = 0
  LastAngle = 90
  MakeFace = false
  Placement = pos=(10.365,8,0) rot=(0,0,1;0rad)
  Radius = 1
FEATURE [Part::Part2DObjectPython] Line655  # Draft 2D object (typed FeaturePython)
  ChamferSize = 0
  Closed = false
  End = (-4,9,0)
  FilletRadius = 0
  Length = 14.365
  MakeFace = false
  Placement = pos=(10.365,9,0) rot=(0,0,1;0rad)
  Points = (2) [(0,0,0),(-14.365,0,0)]
  Start = (10.365,9,0)
  Subdivisions = 0
FEATURE [Part::Part2DObjectPython] Line656  # Draft 2D object (typed FeaturePython)
  ChamferSize = 0
  Closed = false
  End = (11.365,2,0)
  FilletRadius = 0
  Length = 6
  MakeFace = false
  Placement = pos=(11.365,8,0) rot=(0,0,1;0rad)
  Points = (2) [(0,0,0),(7.10543e-15,-6,0)]
  Start = (11.365,8,0)
  Subdivisions = 0
FEATURE [App::DocumentObjectGroup] Group086  label="Switch-bottom layer 5mm"
  Group = -> [Arc322,Arc320,Arc321,Arc323,Line628,Line629,Line631,Group087,Arc336,Arc337,Arc339,Line650,Line652,Line653,Line654,Arc340,Line655,Line656]
FEATURE [App::DocumentObjectGroup] Group091  label="Bottom"
  Group = -> [Group086,Group088]
FEATURE [Part::Part2DObjectPython] Line657  # Draft 2D object (typed FeaturePython)
  ChamferSize = 0
  Closed = false
  End = (206,-16.5,0)
  FilletRadius = 0
  Length = 13
  MakeFace = false
  Placement = pos=(193,-16.5,0) rot=(0,0,1;0rad)
  Points = (2) [(0,0,0),(13,0,0)]
  Start = (193,-16.5,0)
  Subdivisions = 0
FEATURE [Part::Part2DObjectPython] Arc341  # Draft 2D object (typed FeaturePython)
  FirstAngle = -90
  LastAngle = 0
  MakeFace = false
  Placement = pos=(206,-16,0) rot=(0,0,1;0rad)
  Radius = 0.5
FEATURE [Part::Part2DObjectPython] Line658  # Draft 2D object (typed FeaturePython)
  ChamferSize = 0
  Closed = false
  End = (206.5,-3,0)
  FilletRadius = 0
  Length = 13
  MakeFace = false
  Placement = pos=(206.5,-16,0) rot=(0,0,1;0rad)
  Points = (2) [(0,0,0),(0,13,0)]
  Start = (206.5,-16,0)
  Subdivisions = 0
FEATURE [Part::Part2DObjectPython] Line659  # Draft 2D object (typed FeaturePython)
  ChamferSize = 0
  Closed = false
  End = (211.5,-16,0)
  FilletRadius = 0
  Length = 13
  MakeFace = false
  Placement = pos=(211.5,-3,0) rot=(0,0,1;0rad)
  Points = (2) [(0,0,0),(0,-13,0)]
  Start = (211.5,-3,0)
  Subdivisions = 0
FEATURE [Part::Part2DObjectPython] Line660  # Draft 2D object (typed FeaturePython)
  ChamferSize = 0
  Closed = false
  End = (209,0,0)
  FilletRadius = 0
  Length = 19
  MakeFace = false
  Placement = pos=(190,0,0) rot=(0,0,1;0rad)
  Points = (2) [(0,0,0),(19,0,0)]
  Start = (190,0,0)
  Subdivisions = 0
FEATURE [Part::Part2DObjectPython] Line661  # Draft 2D object (typed FeaturePython)
  ChamferSize = 0
  Closed = false
  End = (192.5,-16,0)
  FilletRadius = 0
  Length = 13
  MakeFace = false
  Placement = pos=(192.5,-3,0) rot=(0,0,1;0rad)
  Points = (2) [(0,0,0),(0,-13,0)]
  Start = (192.5,-3,0)
  Subdivisions = 0
FEATURE [Part::Part2DObjectPython] Line662  # Draft 2D object (typed FeaturePython)
  ChamferSize = 0
  Closed = false
  End = (190,-19,0)
  FilletRadius = 0
  Length = 19
  MakeFace = false
  Placement = pos=(209,-19,0) rot=(0,0,1;0rad)
  Points = (2) [(0,0,0),(-19,0,0)]
  Start = (209,-19,0)
  Subdivisions = 0
FEATURE [Part::Part2DObjectPython] Arc342  # Draft 2D object (typed FeaturePython)
  FirstAngle = 180
  LastAngle = 270
  MakeFace = false
  Placement = pos=(193,-16,0) rot=(0,0,1;0rad)
  Radius = 0.5
FEATURE [Part::Part2DObjectPython] Line663  # Draft 2D object (typed FeaturePython)
  ChamferSize = 0
  Closed = false
  End = (228,0,0)
  FilletRadius = 0
  Length = 19
  MakeFace = false
  Placement = pos=(209,0,0) rot=(0,0,1;0rad)
  Points = (2) [(0,0,0),(19,0,0)]
  Start = (209,0,0)
  Subdivisions = 0
FEATURE [Part::Part2DObjectPython] Arc343  # Draft 2D object (typed FeaturePython)
  FirstAngle = 0
  LastAngle = 90
  MakeFace = false
  Placement = pos=(244,-3,0) rot=(0,0,1;0rad)
  Radius = 0.5
FEATURE [Part::Part2DObjectPython] Line664  # Draft 2D object (typed FeaturePython)
  ChamferSize = 0
  Closed = false
  End = (228,-19,0)
  FilletRadius = 0
  Length = 19
  MakeFace = false
  Placement = pos=(228,0,0) rot=(0,0,1;0rad)
  Points = (2) [(0,0,0),(0,-19,0)]
  Start = (228,0,0)
  Subdivisions = 0
FEATURE [Part::Part2DObjectPython] Line665  # Draft 2D object (typed FeaturePython)
  ChamferSize = 0
  Closed = false
  End = (209,-19,0)
  FilletRadius = 0
  Length = 19
  MakeFace = false
  Placement = pos=(228,-19,0) rot=(0,0,1;0rad)
  Points = (2) [(0,0,0),(-19,0,0)]
  Start = (228,-19,0)
  Subdivisions = 0
FEATURE [Part::Part2DObjectPython] Arc344  # Draft 2D object (typed FeaturePython)
  FirstAngle = 90
  LastAngle = 180
  MakeFace = false
  Placement = pos=(193,-3,0) rot=(0,0,1;0rad)
  Radius = 0.5
FEATURE [Part::Part2DObjectPython] Line666  # Draft 2D object (typed FeaturePython)
  ChamferSize = 0
  Closed = false
  End = (225,-2.5,0)
  FilletRadius = 0
  Length = 13
  MakeFace = false
  Placement = pos=(212,-2.5,0) rot=(0,0,1;0rad)
  Points = (2) [(0,0,0),(13,0,0)]
  Start = (212,-2.5,0)
  Subdivisions = 0
FEATURE [Part::Part2DObjectPython] Arc345  # Draft 2D object (typed FeaturePython)
  FirstAngle = -90
  LastAngle = 0
  MakeFace = false
  Placement = pos=(244,-16,0) rot=(0,0,1;0rad)
  Radius = 0.5
FEATURE [Part::Part2DObjectPython] Line667  # Draft 2D object (typed FeaturePython)
  ChamferSize = 0
  Closed = false
  End = (206,-2.5,0)
  FilletRadius = 0
  Length = 13
  MakeFace = false
  Placement = pos=(193,-2.5,0) rot=(0,0,1;0rad)
  Points = (2) [(0,0,0),(13,0,0)]
  Start = (193,-2.5,0)
  Subdivisions = 0
FEATURE [Part::Part2DObjectPython] Line668  # Draft 2D object (typed FeaturePython)
  ChamferSize = 0
  Closed = false
  End = (190,-19,0)
  FilletRadius = 0
  Length = 19
  MakeFace = false
  Placement = pos=(190,0,0) rot=(0,0,1;0rad)
  Points = (2) [(0,0,0),(0,-19,0)]
  Start = (190,0,0)
  Subdivisions = 0
FEATURE [Part::Part2DObjectPython] Line669  # Draft 2D object (typed FeaturePython)
  ChamferSize = 0
  Closed = false
  End = (244,-16.5,0)
  FilletRadius = 0
  Length = 13
  MakeFace = false
  Placement = pos=(231,-16.5,0) rot=(0,0,1;0rad)
  Points = (2) [(0,0,0),(13,0,0)]
  Start = (231,-16.5,0)
  Subdivisions = 0
FEATURE [Part::Part2DObjectPython] Line670  # Draft 2D object (typed FeaturePython)
  ChamferSize = 0
  Closed = false
  End = (18.875,-22,0)
  FilletRadius = 0
  Length = 13
  MakeFace = false
  Placement = pos=(18.875,-35,0) rot=(0,0,1;0rad)
  Points = (2) [(0,0,0),(0,13,0)]
  Start = (18.875,-35,0)
  Subdivisions = 0
FEATURE [Part::Part2DObjectPython] Line671  # Draft 2D object (typed FeaturePython)
  ChamferSize = 0
  Closed = false
  End = (244,-2.5,0)
  FilletRadius = 0
  Length = 13
  MakeFace = false
  Placement = pos=(231,-2.5,0) rot=(0,0,1;0rad)
  Points = (2) [(0,0,0),(13,0,0)]
  Start = (231,-2.5,0)
  Subdivisions = 0
FEATURE [Part::Part2DObjectPython] Line672  # Draft 2D object (typed FeaturePython)
  ChamferSize = 0
  Closed = false
  End = (228,-19,0)
  FilletRadius = 0
  Length = 19
  MakeFace = false
  Placement = pos=(247,-19,0) rot=(0,0,1;0rad)
  Points = (2) [(0,0,0),(-19,0,0)]
  Start = (247,-19,0)
  Subdivisions = 0
FEATURE [Part::Part2DObjectPython] Line673  # Draft 2D object (typed FeaturePython)
  ChamferSize = 0
  Closed = false
  End = (244.5,-3,0)
  FilletRadius = 0
  Length = 13
  MakeFace = false
  Placement = pos=(244.5,-16,0) rot=(0,0,1;0rad)
  Points = (2) [(0,0,0),(0,13,0)]
  Start = (244.5,-16,0)
  Subdivisions = 0
FEATURE [Part::Part2DObjectPython] Arc346  # Draft 2D object (typed FeaturePython)
  FirstAngle = 90
  LastAngle = 180
  MakeFace = false
  Placement = pos=(231,-3,0) rot=(0,0,1;0rad)
  Radius = 0.5
FEATURE [Part::Part2DObjectPython] Arc347  # Draft 2D object (typed FeaturePython)
  FirstAngle = 0
  LastAngle = 90
  MakeFace = false
  Placement = pos=(18.375,-22,0) rot=(0,0,1;0rad)
  Radius = 0.5
FEATURE [Part::Part2DObjectPython] Line674  # Draft 2D object (typed FeaturePython)
  ChamferSize = 0
  Closed = false
  End = (225.5,-3,0)
  FilletRadius = 0
  Length = 13
  MakeFace = false
  Placement = pos=(225.5,-16,0) rot=(0,0,1;0rad)
  Points = (2) [(0,0,0),(0,13,0)]
  Start = (225.5,-16,0)
  Subdivisions = 0
FEATURE [Part::Part2DObjectPython] Arc348  # Draft 2D object (typed FeaturePython)
  FirstAngle = 180
  LastAngle = 270
  MakeFace = false
  Placement = pos=(212,-16,0) rot=(0,0,1;0rad)
  Radius = 0.5
FEATURE [Part::Part2DObjectPython] Arc349  # Draft 2D object (typed FeaturePython)
  FirstAngle = -90
  LastAngle = 0
  MakeFace = false
  Placement = pos=(225,-16,0) rot=(0,0,1;0rad)
  Radius = 0.5
FEATURE [Part::Part2DObjectPython] Line675  # Draft 2D object (typed FeaturePython)
  ChamferSize = 0
  Closed = false
  End = (225,-16.5,0)
  FilletRadius = 0
  Length = 13
  MakeFace = false
  Placement = pos=(212,-16.5,0) rot=(0,0,1;0rad)
  Points = (2) [(0,0,0),(13,0,0)]
  Start = (212,-16.5,0)
  Subdivisions = 0
FEATURE [Part::Part2DObjectPython] Arc350  # Draft 2D object (typed FeaturePython)
  FirstAngle = 90
  LastAngle = 180
  MakeFace = false
  Placement = pos=(212,-3,0) rot=(0,0,1;0rad)
  Radius = 0.5
FEATURE [Part::Part2DObjectPython] Arc351  # Draft 2D object (typed FeaturePython)
  FirstAngle = 0
  LastAngle = 90
  MakeFace = false
  Placement = pos=(225,-3,0) rot=(0,0,1;0rad)
  Radius = 0.5
FEATURE [Part::Part2DObjectPython] Line676  # Draft 2D object (typed FeaturePython)
  ChamferSize = 0
  Closed = false
  End = (230.5,-16,0)
  FilletRadius = 0
  Length = 13
  MakeFace = false
  Placement = pos=(230.5,-3,0) rot=(0,0,1;0rad)
  Points = (2) [(0,0,0),(0,-13,0)]
  Start = (230.5,-3,0)
  Subdivisions = 0
FEATURE [Part::Part2DObjectPython] Line677  # Draft 2D object (typed FeaturePython)
  ChamferSize = 0
  Closed = false
  End = (228,-19,0)
  FilletRadius = 0
  Length = 19
  MakeFace = false
  Placement = pos=(228,0,0) rot=(0,0,1;0rad)
  Points = (2) [(0,0,0),(0,-19,0)]
  Start = (228,0,0)
  Subdivisions = 0
FEATURE [Part::Part2DObjectPython] Line678  # Draft 2D object (typed FeaturePython)
  ChamferSize = 0
  Closed = false
  End = (247,0,0)
  FilletRadius = 0
  Length = 19
  MakeFace = false
  Placement = pos=(228,0,0) rot=(0,0,1;0rad)
  Points = (2) [(0,0,0),(19,0,0)]
  Start = (228,0,0)
  Subdivisions = 0
FEATURE [Part::Part2DObjectPython] Arc352  # Draft 2D object (typed FeaturePython)
  FirstAngle = 180
  LastAngle = 270
  MakeFace = false
  Placement = pos=(231,-16,0) rot=(0,0,1;0rad)
  Radius = 0.5
FEATURE [Part::Part2DObjectPython] Line679  # Draft 2D object (typed FeaturePython)
  ChamferSize = 0
  Closed = false
  End = (247,-19,0)
  FilletRadius = 0
  Length = 19
  MakeFace = false
  Placement = pos=(247,0,0) rot=(0,0,1;0rad)
  Points = (2) [(0,0,0),(0,-19,0)]
  Start = (247,0,0)
  Subdivisions = 0
FEATURE [Part::Part2DObjectPython] Line680  # Draft 2D object (typed FeaturePython)
  ChamferSize = 0
  Closed = false
  End = (23.75,-19,0)
  FilletRadius = 0
  Length = 23.75
  MakeFace = false
  Placement = pos=(0,-19,0) rot=(0,0,1;0rad)
  Points = (2) [(0,0,0),(23.75,0,0)]
  Start = (0,-19,0)
  Subdivisions = 0
FEATURE [Part::Part2DObjectPython] Line681  # Draft 2D object (typed FeaturePython)
  ChamferSize = 0
  Closed = false
  End = (209,-19,0)
  FilletRadius = 0
  Length = 19
  MakeFace = false
  Placement = pos=(209,0,0) rot=(0,0,1;0rad)
  Points = (2) [(0,0,0),(0,-19,0)]
  Start = (209,0,0)
  Subdivisions = 0
FEATURE [Part::Part2DObjectPython] Line682  # Draft 2D object (typed FeaturePython)
  ChamferSize = 0
  Closed = false
  End = (0,-38,0)
  FilletRadius = 0
  Length = 19
  MakeFace = false
  Placement = pos=(0,-19,0) rot=(0,0,1;0rad)
  Points = (2) [(0,0,0),(0,-19,0)]
  Start = (0,-19,0)
  Subdivisions = 0
FEATURE [Part::Part2DObjectPython] Line683  # Draft 2D object (typed FeaturePython)
  ChamferSize = 0
  Closed = false
  End = (23.75,-19,0)
  FilletRadius = 0
  Length = 19
  MakeFace = false
  Placement = pos=(23.75,-38,0) rot=(0,0,1;0rad)
  Points = (2) [(0,0,0),(0,19,0)]
  Start = (23.75,-38,0)
  Subdivisions = 0
FEATURE [Part::Part2DObjectPython] Arc353  # Draft 2D object (typed FeaturePython)
  FirstAngle = 90
  LastAngle = 180
  MakeFace = false
  Placement = pos=(5.375,-22,0) rot=(0,0,1;0rad)
  Radius = 0.5
FEATURE [Part::Part2DObjectPython] Line684  # Draft 2D object (typed FeaturePython)
  ChamferSize = 0
  Closed = false
  End = (4.875,-35,0)
  FilletRadius = 0
  Length = 13
  MakeFace = false
  Placement = pos=(4.875,-22,0) rot=(0,0,1;0rad)
  Points = (2) [(0,0,0),(0,-13,0)]
  Start = (4.875,-22,0)
  Subdivisions = 0
FEATURE [Part::Part2DObjectPython] Arc354  # Draft 2D object (typed FeaturePython)
  FirstAngle = 180
  LastAngle = 270
  MakeFace = false
  Placement = pos=(5.375,-35,0) rot=(0,0,1;0rad)
  Radius = 0.5
FEATURE [Part::Part2DObjectPython] Line685  # Draft 2D object (typed FeaturePython)
  ChamferSize = 0
  Closed = false
  End = (18.375,-21.5,0)
  FilletRadius = 0
  Length = 13
  MakeFace = false
  Placement = pos=(5.375,-21.5,0) rot=(0,0,1;0rad)
  Points = (2) [(0,0,0),(13,0,0)]
  Start = (5.375,-21.5,0)
  Subdivisions = 0
FEATURE [Part::Part2DObjectPython] Line686  # Draft 2D object (typed FeaturePython)
  ChamferSize = 0
  Closed = false
  End = (18.375,-35.5,0)
  FilletRadius = 0
  Length = 13
  MakeFace = false
  Placement = pos=(5.375,-35.5,0) rot=(0,0,1;0rad)
  Points = (2) [(0,0,0),(13,0,0)]
  Start = (5.375,-35.5,0)
  Subdivisions = 0
FEATURE [Part::Part2DObjectPython] Line687  # Draft 2D object (typed FeaturePython)
  ChamferSize = 0
  Closed = false
  End = (23.75,-38,0)
  FilletRadius = 0
  Length = 23.75
  MakeFace = false
  Placement = pos=(0,-38,0) rot=(0,0,1;0rad)
  Points = (2) [(0,0,0),(23.75,0,0)]
  Start = (0,-38,0)
  Subdivisions = 0
FEATURE [Part::Part2DObjectPython] Arc355  # Draft 2D object (typed FeaturePython)
  FirstAngle = -90
  LastAngle = 0
  MakeFace = false
  Placement = pos=(18.375,-35,0) rot=(0,0,1;0rad)
  Radius = 0.5
FEATURE [Part::Part2DObjectPython] Line688  # Draft 2D object (typed FeaturePython)
  ChamferSize = 0
  Closed = false
  End = (23.75,-38,0)
  FilletRadius = 0
  Length = 19
  MakeFace = false
  Placement = pos=(23.75,-19,0) rot=(0,0,1;0rad)
  Points = (2) [(0,0,0),(0,-19,0)]
  Start = (23.75,-19,0)
  Subdivisions = 0
FEATURE [Part::Part2DObjectPython] Arc356  # Draft 2D object (typed FeaturePython)
  FirstAngle = 180
  LastAngle = 270
  MakeFace = false
  Placement = pos=(26.75,-35,0) rot=(0,0,1;0rad)
  Radius = 0.5
FEATURE [Part::Part2DObjectPython] Arc357  # Draft 2D object (typed FeaturePython)
  FirstAngle = -90
  LastAngle = 0
  MakeFace = false
  Placement = pos=(39.75,-35,0) rot=(0,0,1;0rad)
  Radius = 0.5
FEATURE [Part::Part2DObjectPython] Line689  # Draft 2D object (typed FeaturePython)
  ChamferSize = 0
  Closed = false
  End = (40.25,-22,0)
  FilletRadius = 0
  Length = 13
  MakeFace = false
  Placement = pos=(40.25,-35,0) rot=(0,0,1;0rad)
  Points = (2) [(0,0,0),(0,13,0)]
  Start = (40.25,-35,0)
  Subdivisions = 0
FEATURE [Part::Part2DObjectPython] Arc358  # Draft 2D object (typed FeaturePython)
  FirstAngle = 180
  LastAngle = 270
  MakeFace = false
  Placement = pos=(45.75,-35,0) rot=(0,0,1;0rad)
  Radius = 0.5
FEATURE [Part::Part2DObjectPython] Arc359  # Draft 2D object (typed FeaturePython)
  FirstAngle = -90
  LastAngle = 0
  MakeFace = false
  Placement = pos=(58.75,-35,0) rot=(0,0,1;0rad)
  Radius = 0.5
FEATURE [Part::Part2DObjectPython] Arc360  # Draft 2D object (typed FeaturePython)
  FirstAngle = 90
  LastAngle = 180
  MakeFace = false
  Placement = pos=(26.75,-22,0) rot=(0,0,1;0rad)
  Radius = 0.5
FEATURE [Part::Part2DObjectPython] Line690  # Draft 2D object (typed FeaturePython)
  ChamferSize = 0
  Closed = false
  End = (23.75,-38,0)
  FilletRadius = 0
  Length = 19
  MakeFace = false
  Placement = pos=(42.75,-38,0) rot=(0,0,1;0rad)
  Points = (2) [(0,0,0),(-19,0,0)]
  Start = (42.75,-38,0)
  Subdivisions = 0
FEATURE [Part::Part2DObjectPython] Line691  # Draft 2D object (typed FeaturePython)
  ChamferSize = 0
  Closed = false
  End = (39.75,-35.5,0)
  FilletRadius = 0
  Length = 13
  MakeFace = false
  Placement = pos=(26.75,-35.5,0) rot=(0,0,1;0rad)
  Points = (2) [(0,0,0),(13,0,0)]
  Start = (26.75,-35.5,0)
  Subdivisions = 0
FEATURE [Part::Part2DObjectPython] Line692  # Draft 2D object (typed FeaturePython)
  ChamferSize = 0
  Closed = false
  End = (42.75,-38,0)
  FilletRadius = 0
  Length = 19
  MakeFace = false
  Placement = pos=(42.75,-19,0) rot=(0,0,1;0rad)
  Points = (2) [(0,0,0),(0,-19,0)]
  Start = (42.75,-19,0)
  Subdivisions = 0
FEATURE [Part::Part2DObjectPython] Arc361  # Draft 2D object (typed FeaturePython)
  FirstAngle = 0
  LastAngle = 90
  MakeFace = false
  Placement = pos=(39.75,-22,0) rot=(0,0,1;0rad)
  Radius = 0.5
FEATURE [Part::Part2DObjectPython] Line693  # Draft 2D object (typed FeaturePython)
  ChamferSize = 0
  Closed = false
  End = (26.25,-35,0)
  FilletRadius = 0
  Length = 13
  MakeFace = false
  Placement = pos=(26.25,-22,0) rot=(0,0,1;0rad)
  Points = (2) [(0,0,0),(0,-13,0)]
  Start = (26.25,-22,0)
  Subdivisions = 0
FEATURE [Part::Part2DObjectPython] Line694  # Draft 2D object (typed FeaturePython)
  ChamferSize = 0
  Closed = false
  End = (42.75,-19,0)
  FilletRadius = 0
  Length = 19
  MakeFace = false
  Placement = pos=(23.75,-19,0) rot=(0,0,1;0rad)
  Points = (2) [(0,0,0),(19,0,0)]
  Start = (23.75,-19,0)
  Subdivisions = 0
FEATURE [Part::Part2DObjectPython] Line695  # Draft 2D object (typed FeaturePython)
  ChamferSize = 0
  Closed = false
  End = (39.75,-21.5,0)
  FilletRadius = 0
  Length = 13
  MakeFace = false
  Placement = pos=(26.75,-21.5,0) rot=(0,0,1;0rad)
  Points = (2) [(0,0,0),(13,0,0)]
  Start = (26.75,-21.5,0)
  Subdivisions = 0
FEATURE [Part::Part2DObjectPython] Line696  # Draft 2D object (typed FeaturePython)
  ChamferSize = 0
  Closed = false
  End = (42.75,-38,0)
  FilletRadius = 0
  Length = 19
  MakeFace = false
  Placement = pos=(42.75,-19,0) rot=(0,0,1;0rad)
  Points = (2) [(0,0,0),(0,-19,0)]
  Start = (42.75,-19,0)
  Subdivisions = 0
FEATURE [Part::Part2DObjectPython] Line697  # Draft 2D object (typed FeaturePython)
  ChamferSize = 0
  Closed = false
  End = (59.25,-22,0)
  FilletRadius = 0
  Length = 13
  MakeFace = false
  Placement = pos=(59.25,-35,0) rot=(0,0,1;0rad)
  Points = (2) [(0,0,0),(0,13,0)]
  Start = (59.25,-35,0)
  Subdivisions = 0
FEATURE [Part::Part2DObjectPython] Arc362  # Draft 2D object (typed FeaturePython)
  FirstAngle = 90
  LastAngle = 180
  MakeFace = false
  Placement = pos=(45.75,-22,0) rot=(0,0,1;0rad)
  Radius = 0.5
FEATURE [Part::Part2DObjectPython] Line698  # Draft 2D object (typed FeaturePython)
  ChamferSize = 0
  Closed = false
  End = (42.75,-38,0)
  FilletRadius = 0
  Length = 19
  MakeFace = false
  Placement = pos=(61.75,-38,0) rot=(0,0,1;0rad)
  Points = (2) [(0,0,0),(-19,0,0)]
  Start = (61.75,-38,0)
  Subdivisions = 0
FEATURE [Part::Part2DObjectPython] Line699  # Draft 2D object (typed FeaturePython)
  ChamferSize = 0
  Closed = false
  End = (77.75,-21.5,0)
  FilletRadius = 0
  Length = 13
  MakeFace = false
  Placement = pos=(64.75,-21.5,0) rot=(0,0,1;0rad)
  Points = (2) [(0,0,0),(13,0,0)]
  Start = (64.75,-21.5,0)
  Subdivisions = 0
FEATURE [Part::Part2DObjectPython] Arc363  # Draft 2D object (typed FeaturePython)
  FirstAngle = 180
  LastAngle = 270
  MakeFace = false
  Placement = pos=(83.75,-35,0) rot=(0,0,1;0rad)
  Radius = 0.5
FEATURE [Part::Part2DObjectPython] Line700  # Draft 2D object (typed FeaturePython)
  ChamferSize = 0
  Closed = false
  End = (61.75,-38,0)
  FilletRadius = 0
  Length = 19
  MakeFace = false
  Placement = pos=(80.75,-38,0) rot=(0,0,1;0rad)
  Points = (2) [(0,0,0),(-19,0,0)]
  Start = (80.75,-38,0)
  Subdivisions = 0
FEATURE [Part::Part2DObjectPython] Line701  # Draft 2D object (typed FeaturePython)
  ChamferSize = 0
  Closed = false
  End = (80.75,-38,0)
  FilletRadius = 0
  Length = 19
  MakeFace = false
  Placement = pos=(99.75,-38,0) rot=(0,0,1;0rad)
  Points = (2) [(0,0,0),(-19,0,0)]
  Start = (99.75,-38,0)
  Subdivisions = 0
FEATURE [Part::Part2DObjectPython] Line702  # Draft 2D object (typed FeaturePython)
  ChamferSize = 0
  Closed = false
  End = (61.75,-19,0)
  FilletRadius = 0
  Length = 19
  MakeFace = false
  Placement = pos=(42.75,-19,0) rot=(0,0,1;0rad)
  Points = (2) [(0,0,0),(19,0,0)]
  Start = (42.75,-19,0)
  Subdivisions = 0
FEATURE [Part::Part2DObjectPython] Arc364  # Draft 2D object (typed FeaturePython)
  FirstAngle = -90
  LastAngle = 0
  MakeFace = false
  Placement = pos=(96.75,-35,0) rot=(0,0,1;0rad)
  Radius = 0.5
FEATURE [Part::Part2DObjectPython] Line703  # Draft 2D object (typed FeaturePython)
  ChamferSize = 0
  Closed = false
  End = (80.75,-38,0)
  FilletRadius = 0
  Length = 19
  MakeFace = false
  Placement = pos=(80.75,-19,0) rot=(0,0,1;0rad)
  Points = (2) [(0,0,0),(0,-19,0)]
  Start = (80.75,-19,0)
  Subdivisions = 0
FEATURE [Part::Part2DObjectPython] Line704  # Draft 2D object (typed FeaturePython)
  ChamferSize = 0
  Closed = false
  End = (77.75,-35.5,0)
  FilletRadius = 0
  Length = 13
  MakeFace = false
  Placement = pos=(64.75,-35.5,0) rot=(0,0,1;0rad)
  Points = (2) [(0,0,0),(13,0,0)]
  Start = (64.75,-35.5,0)
  Subdivisions = 0
FEATURE [Part::Part2DObjectPython] Line705  # Draft 2D object (typed FeaturePython)
  ChamferSize = 0
  Closed = false
  End = (99.75,-19,0)
  FilletRadius = 0
  Length = 19
  MakeFace = false
  Placement = pos=(80.75,-19,0) rot=(0,0,1;0rad)
  Points = (2) [(0,0,0),(19,0,0)]
  Start = (80.75,-19,0)
  Subdivisions = 0
FEATURE [Part::Part2DObjectPython] Line706  # Draft 2D object (typed FeaturePython)
  ChamferSize = 0
  Closed = false
  End = (78.25,-22,0)
  FilletRadius = 0
  Length = 13
  MakeFace = false
  Placement = pos=(78.25,-35,0) rot=(0,0,1;0rad)
  Points = (2) [(0,0,0),(0,13,0)]
  Start = (78.25,-35,0)
  Subdivisions = 0
FEATURE [Part::Part2DObjectPython] Arc365  # Draft 2D object (typed FeaturePython)
  FirstAngle = 0
  LastAngle = 90
  MakeFace = false
  Placement = pos=(58.75,-22,0) rot=(0,0,1;0rad)
  Radius = 0.5
FEATURE [Part::Part2DObjectPython] Line707  # Draft 2D object (typed FeaturePython)
  ChamferSize = 0
  Closed = false
  End = (96.75,-35.5,0)
  FilletRadius = 0
  Length = 13
  MakeFace = false
  Placement = pos=(83.75,-35.5,0) rot=(0,0,1;0rad)
  Points = (2) [(0,0,0),(13,0,0)]
  Start = (83.75,-35.5,0)
  Subdivisions = 0
FEATURE [Part::Part2DObjectPython] Line708  # Draft 2D object (typed FeaturePython)
  ChamferSize = 0
  Closed = false
  End = (61.75,-38,0)
  FilletRadius = 0
  Length = 19
  MakeFace = false
  Placement = pos=(61.75,-19,0) rot=(0,0,1;0rad)
  Points = (2) [(0,0,0),(0,-19,0)]
  Start = (61.75,-19,0)
  Subdivisions = 0
FEATURE [Part::Part2DObjectPython] Line709  # Draft 2D object (typed FeaturePython)
  ChamferSize = 0
  Closed = false
  End = (45.25,-35,0)
  FilletRadius = 0
  Length = 13
  MakeFace = false
  Placement = pos=(45.25,-22,0) rot=(0,0,1;0rad)
  Points = (2) [(0,0,0),(0,-13,0)]
  Start = (45.25,-22,0)
  Subdivisions = 0
FEATURE [Part::Part2DObjectPython] Arc366  # Draft 2D object (typed FeaturePython)
  FirstAngle = 0
  LastAngle = 90
  MakeFace = false
  Placement = pos=(96.75,-22,0) rot=(0,0,1;0rad)
  Radius = 0.5
FEATURE [Part::Part2DObjectPython] Arc367  # Draft 2D object (typed FeaturePython)
  FirstAngle = 90
  LastAngle = 180
  MakeFace = false
  Placement = pos=(102.75,-22,0) rot=(0,0,1;0rad)
  Radius = 0.5
FEATURE [Part::Part2DObjectPython] Arc368  # Draft 2D object (typed FeaturePython)
  FirstAngle = 180
  LastAngle = 270
  MakeFace = false
  Placement = pos=(121.75,-35,0) rot=(0,0,1;0rad)
  Radius = 0.5
FEATURE [Part::Part2DObjectPython] Arc369  # Draft 2D object (typed FeaturePython)
  FirstAngle = 180
  LastAngle = 270
  MakeFace = false
  Placement = pos=(64.75,-35,0) rot=(0,0,1;0rad)
  Radius = 0.5
FEATURE [Part::Part2DObjectPython] Arc370  # Draft 2D object (typed FeaturePython)
  FirstAngle = -90
  LastAngle = 0
  MakeFace = false
  Placement = pos=(77.75,-35,0) rot=(0,0,1;0rad)
  Radius = 0.5
FEATURE [Part::Part2DObjectPython] Line710  # Draft 2D object (typed FeaturePython)
  ChamferSize = 0
  Closed = false
  End = (96.75,-21.5,0)
  FilletRadius = 0
  Length = 13
  MakeFace = false
  Placement = pos=(83.75,-21.5,0) rot=(0,0,1;0rad)
  Points = (2) [(0,0,0),(13,0,0)]
  Start = (83.75,-21.5,0)
  Subdivisions = 0
FEATURE [Part::Part2DObjectPython] Line711  # Draft 2D object (typed FeaturePython)
  ChamferSize = 0
  Closed = false
  End = (99.75,-38,0)
  FilletRadius = 0
  Length = 19
  MakeFace = false
  Placement = pos=(99.75,-19,0) rot=(0,0,1;0rad)
  Points = (2) [(0,0,0),(0,-19,0)]
  Start = (99.75,-19,0)
  Subdivisions = 0
FEATURE [Part::Part2DObjectPython] Line712  # Draft 2D object (typed FeaturePython)
  ChamferSize = 0
  Closed = false
  End = (61.75,-38,0)
  FilletRadius = 0
  Length = 19
  MakeFace = false
  Placement = pos=(61.75,-19,0) rot=(0,0,1;0rad)
  Points = (2) [(0,0,0),(0,-19,0)]
  Start = (61.75,-19,0)
  Subdivisions = 0
FEATURE [Part::Part2DObjectPython] Line713  # Draft 2D object (typed FeaturePython)
  ChamferSize = 0
  Closed = false
  End = (58.75,-35.5,0)
  FilletRadius = 0
  Length = 13
  MakeFace = false
  Placement = pos=(45.75,-35.5,0) rot=(0,0,1;0rad)
  Points = (2) [(0,0,0),(13,0,0)]
  Start = (45.75,-35.5,0)
  Subdivisions = 0
FEATURE [Part::Part2DObjectPython] Arc371  # Draft 2D object (typed FeaturePython)
  FirstAngle = 90
  LastAngle = 180
  MakeFace = false
  Placement = pos=(64.75,-22,0) rot=(0,0,1;0rad)
  Radius = 0.5
FEATURE [Part::Part2DObjectPython] Line714  # Draft 2D object (typed FeaturePython)
  ChamferSize = 0
  Closed = false
  End = (80.75,-19,0)
  FilletRadius = 0
  Length = 19
  MakeFace = false
  Placement = pos=(61.75,-19,0) rot=(0,0,1;0rad)
  Points = (2) [(0,0,0),(19,0,0)]
  Start = (61.75,-19,0)
  Subdivisions = 0
FEATURE [Part::Part2DObjectPython] Arc372  # Draft 2D object (typed FeaturePython)
  FirstAngle = 0
  LastAngle = 90
  MakeFace = false
  Placement = pos=(77.75,-22,0) rot=(0,0,1;0rad)
  Radius = 0.5
FEATURE [Part::Part2DObjectPython] Line715  # Draft 2D object (typed FeaturePython)
  ChamferSize = 0
  Closed = false
  End = (58.75,-21.5,0)
  FilletRadius = 0
  Length = 13
  MakeFace = false
  Placement = pos=(45.75,-21.5,0) rot=(0,0,1;0rad)
  Points = (2) [(0,0,0),(13,0,0)]
  Start = (45.75,-21.5,0)
  Subdivisions = 0
FEATURE [Part::Part2DObjectPython] Line716  # Draft 2D object (typed FeaturePython)
  ChamferSize = 0
  Closed = false
  End = (64.25,-35,0)
  FilletRadius = 0
  Length = 13
  MakeFace = false
  Placement = pos=(64.25,-22,0) rot=(0,0,1;0rad)
  Points = (2) [(0,0,0),(0,-13,0)]
  Start = (64.25,-22,0)
  Subdivisions = 0
FEATURE [Part::Part2DObjectPython] Line717  # Draft 2D object (typed FeaturePython)
  ChamferSize = 0
  Closed = false
  End = (97.25,-22,0)
  FilletRadius = 0
  Length = 13
  MakeFace = false
  Placement = pos=(97.25,-35,0) rot=(0,0,1;0rad)
  Points = (2) [(0,0,0),(0,13,0)]
  Start = (97.25,-35,0)
  Subdivisions = 0
FEATURE [Part::Part2DObjectPython] Line718  # Draft 2D object (typed FeaturePython)
  ChamferSize = 0
  Closed = false
  End = (80.75,-38,0)
  FilletRadius = 0
  Length = 19
  MakeFace = false
  Placement = pos=(80.75,-19,0) rot=(0,0,1;0rad)
  Points = (2) [(0,0,0),(0,-19,0)]
  Start = (80.75,-19,0)
  Subdivisions = 0
FEATURE [Part::Part2DObjectPython] Line719  # Draft 2D object (typed FeaturePython)
  ChamferSize = 0
  Closed = false
  End = (83.25,-35,0)
  FilletRadius = 0
  Length = 13
  MakeFace = false
  Placement = pos=(83.25,-22,0) rot=(0,0,1;0rad)
  Points = (2) [(0,0,0),(0,-13,0)]
  Start = (83.25,-22,0)
  Subdivisions = 0
FEATURE [Part::Part2DObjectPython] Arc373  # Draft 2D object (typed FeaturePython)
  FirstAngle = 180
  LastAngle = 270
  MakeFace = false
  Placement = pos=(102.75,-35,0) rot=(0,0,1;0rad)
  Radius = 0.5
FEATURE [Part::Part2DObjectPython] Arc374  # Draft 2D object (typed FeaturePython)
  FirstAngle = -90
  LastAngle = 0
  MakeFace = false
  Placement = pos=(115.75,-35,0) rot=(0,0,1;0rad)
  Radius = 0.5
FEATURE [Part::Part2DObjectPython] Line720  # Draft 2D object (typed FeaturePython)
  ChamferSize = 0
  Closed = false
  End = (115.75,-35.5,0)
  FilletRadius = 0
  Length = 13
  MakeFace = false
  Placement = pos=(102.75,-35.5,0) rot=(0,0,1;0rad)
  Points = (2) [(0,0,0),(13,0,0)]
  Start = (102.75,-35.5,0)
  Subdivisions = 0
FEATURE [Part::Part2DObjectPython] Arc375  # Draft 2D object (typed FeaturePython)
  FirstAngle = 0
  LastAngle = 90
  MakeFace = false
  Placement = pos=(115.75,-22,0) rot=(0,0,1;0rad)
  Radius = 0.5
FEATURE [Part::Part2DObjectPython] Arc376  # Draft 2D object (typed FeaturePython)
  FirstAngle = 90
  LastAngle = 180
  MakeFace = false
  Placement = pos=(83.75,-22,0) rot=(0,0,1;0rad)
  Radius = 0.5
FEATURE [Part::Part2DObjectPython] Line721  # Draft 2D object (typed FeaturePython)
  ChamferSize = 0
  Closed = false
  End = (115.75,-21.5,0)
  FilletRadius = 0
  Length = 13
  MakeFace = false
  Placement = pos=(102.75,-21.5,0) rot=(0,0,1;0rad)
  Points = (2) [(0,0,0),(13,0,0)]
  Start = (102.75,-21.5,0)
  Subdivisions = 0
FEATURE [Part::Part2DObjectPython] Line722  # Draft 2D object (typed FeaturePython)
  ChamferSize = 0
  Closed = false
  End = (99.75,-38,0)
  FilletRadius = 0
  Length = 19
  MakeFace = false
  Placement = pos=(118.75,-38,0) rot=(0,0,1;0rad)
  Points = (2) [(0,0,0),(-19,0,0)]
  Start = (118.75,-38,0)
  Subdivisions = 0
FEATURE [Part::Part2DObjectPython] Line723  # Draft 2D object (typed FeaturePython)
  ChamferSize = 0
  Closed = false
  End = (118.75,-38,0)
  FilletRadius = 0
  Length = 19
  MakeFace = false
  Placement = pos=(118.75,-19,0) rot=(0,0,1;0rad)
  Points = (2) [(0,0,0),(0,-19,0)]
  Start = (118.75,-19,0)
  Subdivisions = 0
FEATURE [Part::Part2DObjectPython] Line724  # Draft 2D object (typed FeaturePython)
  ChamferSize = 0
  Closed = false
  End = (116.25,-22,0)
  FilletRadius = 0
  Length = 13
  MakeFace = false
  Placement = pos=(116.25,-35,0) rot=(0,0,1;0rad)
  Points = (2) [(0,0,0),(0,13,0)]
  Start = (116.25,-35,0)
  Subdivisions = 0
FEATURE [Part::Part2DObjectPython] Line725  # Draft 2D object (typed FeaturePython)
  ChamferSize = 0
  Closed = false
  End = (99.75,-38,0)
  FilletRadius = 0
  Length = 19
  MakeFace = false
  Placement = pos=(99.75,-19,0) rot=(0,0,1;0rad)
  Points = (2) [(0,0,0),(0,-19,0)]
  Start = (99.75,-19,0)
  Subdivisions = 0
FEATURE [Part::Part2DObjectPython] Line726  # Draft 2D object (typed FeaturePython)
  ChamferSize = 0
  Closed = false
  End = (118.75,-19,0)
  FilletRadius = 0
  Length = 19
  MakeFace = false
  Placement = pos=(99.75,-19,0) rot=(0,0,1;0rad)
  Points = (2) [(0,0,0),(19,0,0)]
  Start = (99.75,-19,0)
  Subdivisions = 0
FEATURE [Part::Part2DObjectPython] Line727  # Draft 2D object (typed FeaturePython)
  ChamferSize = 0
  Closed = false
  End = (102.25,-35,0)
  FilletRadius = 0
  Length = 13
  MakeFace = false
  Placement = pos=(102.25,-22,0) rot=(0,0,1;0rad)
  Points = (2) [(0,0,0),(0,-13,0)]
  Start = (102.25,-22,0)
  Subdivisions = 0
FEATURE [Part::Part2DObjectPython] Arc377  # Draft 2D object (typed FeaturePython)
  FirstAngle = 90
  LastAngle = 180
  MakeFace = false
  Placement = pos=(121.75,-22,0) rot=(0,0,1;0rad)
  Radius = 0.5
FEATURE [Part::Part2DObjectPython] Line728  # Draft 2D object (typed FeaturePython)
  ChamferSize = 0
  Closed = false
  End = (137.75,-38,0)
  FilletRadius = 0
  Length = 19
  MakeFace = false
  Placement = pos=(137.75,-19,0) rot=(0,0,1;0rad)
  Points = (2) [(0,0,0),(0,-19,0)]
  Start = (137.75,-19,0)
  Subdivisions = 0
FEATURE [Part::Part2DObjectPython] Line729  # Draft 2D object (typed FeaturePython)
  ChamferSize = 0
  Closed = false
  End = (135.25,-22,0)
  FilletRadius = 0
  Length = 13
  MakeFace = false
  Placement = pos=(135.25,-35,0) rot=(0,0,1;0rad)
  Points = (2) [(0,0,0),(0,13,0)]
  Start = (135.25,-35,0)
  Subdivisions = 0
FEATURE [Part::Part2DObjectPython] Line730  # Draft 2D object (typed FeaturePython)
  ChamferSize = 0
  Closed = false
  End = (137.75,-19,0)
  FilletRadius = 0
  Length = 19
  MakeFace = false
  Placement = pos=(118.75,-19,0) rot=(0,0,1;0rad)
  Points = (2) [(0,0,0),(19,0,0)]
  Start = (118.75,-19,0)
  Subdivisions = 0
FEATURE [Part::Part2DObjectPython] Line731  # Draft 2D object (typed FeaturePython)
  ChamferSize = 0
  Closed = false
  End = (121.25,-35,0)
  FilletRadius = 0
  Length = 13
  MakeFace = false
  Placement = pos=(121.25,-22,0) rot=(0,0,1;0rad)
  Points = (2) [(0,0,0),(0,-13,0)]
  Start = (121.25,-22,0)
  Subdivisions = 0
FEATURE [Part::Part2DObjectPython] Arc378  # Draft 2D object (typed FeaturePython)
  FirstAngle = 90
  LastAngle = 180
  MakeFace = false
  Placement = pos=(140.75,-22,0) rot=(0,0,1;0rad)
  Radius = 0.5
FEATURE [Part::Part2DObjectPython] Arc379  # Draft 2D object (typed FeaturePython)
  FirstAngle = -90
  LastAngle = 0
  MakeFace = false
  Placement = pos=(134.75,-35,0) rot=(0,0,1;0rad)
  Radius = 0.5
FEATURE [Part::Part2DObjectPython] Line732  # Draft 2D object (typed FeaturePython)
  ChamferSize = 0
  Closed = false
  End = (154.25,-22,0)
  FilletRadius = 0
  Length = 13
  MakeFace = false
  Placement = pos=(154.25,-35,0) rot=(0,0,1;0rad)
  Points = (2) [(0,0,0),(0,13,0)]
  Start = (154.25,-35,0)
  Subdivisions = 0
FEATURE [Part::Part2DObjectPython] Arc380  # Draft 2D object (typed FeaturePython)
  FirstAngle = 0
  LastAngle = 90
  MakeFace = false
  Placement = pos=(134.75,-22,0) rot=(0,0,1;0rad)
  Radius = 0.5
FEATURE [Part::Part2DObjectPython] Line733  # Draft 2D object (typed FeaturePython)
  ChamferSize = 0
  Closed = false
  End = (134.75,-35.5,0)
  FilletRadius = 0
  Length = 13
  MakeFace = false
  Placement = pos=(121.75,-35.5,0) rot=(0,0,1;0rad)
  Points = (2) [(0,0,0),(13,0,0)]
  Start = (121.75,-35.5,0)
  Subdivisions = 0
FEATURE [Part::Part2DObjectPython] Line734  # Draft 2D object (typed FeaturePython)
  ChamferSize = 0
  Closed = false
  End = (118.75,-38,0)
  FilletRadius = 0
  Length = 19
  MakeFace = false
  Placement = pos=(118.75,-19,0) rot=(0,0,1;0rad)
  Points = (2) [(0,0,0),(0,-19,0)]
  Start = (118.75,-19,0)
  Subdivisions = 0
FEATURE [Part::Part2DObjectPython] Line735  # Draft 2D object (typed FeaturePython)
  ChamferSize = 0
  Closed = false
  End = (140.25,-35,0)
  FilletRadius = 0
  Length = 13
  MakeFace = false
  Placement = pos=(140.25,-22,0) rot=(0,0,1;0rad)
  Points = (2) [(0,0,0),(0,-13,0)]
  Start = (140.25,-22,0)
  Subdivisions = 0
FEATURE [Part::Part2DObjectPython] Line736  # Draft 2D object (typed FeaturePython)
  ChamferSize = 0
  Closed = false
  End = (118.75,-38,0)
  FilletRadius = 0
  Length = 19
  MakeFace = false
  Placement = pos=(137.75,-38,0) rot=(0,0,1;0rad)
  Points = (2) [(0,0,0),(-19,0,0)]
  Start = (137.75,-38,0)
  Subdivisions = 0
FEATURE [Part::Part2DObjectPython] Arc381  # Draft 2D object (typed FeaturePython)
  FirstAngle = 180
  LastAngle = 270
  MakeFace = false
  Placement = pos=(140.75,-35,0) rot=(0,0,1;0rad)
  Radius = 0.5
FEATURE [Part::Part2DObjectPython] Line737  # Draft 2D object (typed FeaturePython)
  ChamferSize = 0
  Closed = false
  End = (134.75,-21.5,0)
  FilletRadius = 0
  Length = 13
  MakeFace = false
  Placement = pos=(121.75,-21.5,0) rot=(0,0,1;0rad)
  Points = (2) [(0,0,0),(13,0,0)]
  Start = (121.75,-21.5,0)
  Subdivisions = 0
FEATURE [Part::Part2DObjectPython] Line738  # Draft 2D object (typed FeaturePython)
  ChamferSize = 0
  Closed = false
  End = (156.75,-38,0)
  FilletRadius = 0
  Length = 19
  MakeFace = false
  Placement = pos=(156.75,-19,0) rot=(0,0,1;0rad)
  Points = (2) [(0,0,0),(0,-19,0)]
  Start = (156.75,-19,0)
  Subdivisions = 0
FEATURE [Part::Part2DObjectPython] Arc382  # Draft 2D object (typed FeaturePython)
  FirstAngle = -90
  LastAngle = 0
  MakeFace = false
  Placement = pos=(153.75,-35,0) rot=(0,0,1;0rad)
  Radius = 0.5
FEATURE [Part::Part2DObjectPython] Line739  # Draft 2D object (typed FeaturePython)
  ChamferSize = 0
  Closed = false
  End = (137.75,-38,0)
  FilletRadius = 0
  Length = 19
  MakeFace = false
  Placement = pos=(137.75,-19,0) rot=(0,0,1;0rad)
  Points = (2) [(0,0,0),(0,-19,0)]
  Start = (137.75,-19,0)
  Subdivisions = 0
FEATURE [Part::Part2DObjectPython] Line740  # Draft 2D object (typed FeaturePython)
  ChamferSize = 0
  Closed = false
  End = (156.75,-19,0)
  FilletRadius = 0
  Length = 19
  MakeFace = false
  Placement = pos=(137.75,-19,0) rot=(0,0,1;0rad)
  Points = (2) [(0,0,0),(19,0,0)]
  Start = (137.75,-19,0)
  Subdivisions = 0
FEATURE [Part::Part2DObjectPython] Line741  # Draft 2D object (typed FeaturePython)
  ChamferSize = 0
  Closed = false
  End = (153.75,-35.5,0)
  FilletRadius = 0
  Length = 13
  MakeFace = false
  Placement = pos=(140.75,-35.5,0) rot=(0,0,1;0rad)
  Points = (2) [(0,0,0),(13,0,0)]
  Start = (140.75,-35.5,0)
  Subdivisions = 0
FEATURE [Part::Part2DObjectPython] Arc383  # Draft 2D object (typed FeaturePython)
  FirstAngle = 0
  LastAngle = 90
  MakeFace = false
  Placement = pos=(153.75,-22,0) rot=(0,0,1;0rad)
  Radius = 0.5
FEATURE [Part::Part2DObjectPython] Arc384  # Draft 2D object (typed FeaturePython)
  FirstAngle = 0
  LastAngle = 90
  MakeFace = false
  Placement = pos=(191.75,-22,0) rot=(0,0,1;0rad)
  Radius = 0.5
FEATURE [Part::Part2DObjectPython] Line742  # Draft 2D object (typed FeaturePython)
  ChamferSize = 0
  Closed = false
  End = (175.75,-38,0)
  FilletRadius = 0
  Length = 19
  MakeFace = false
  Placement = pos=(175.75,-19,0) rot=(0,0,1;0rad)
  Points = (2) [(0,0,0),(0,-19,0)]
  Start = (175.75,-19,0)
  Subdivisions = 0
FEATURE [Part::Part2DObjectPython] Line743  # Draft 2D object (typed FeaturePython)
  ChamferSize = 0
  Closed = false
  End = (23.625,-41,0)
  FilletRadius = 0
  Length = 13
  MakeFace = false
  Placement = pos=(23.625,-54,0) rot=(0,0,1;0rad)
  Points = (2) [(0,0,0),(0,13,0)]
  Start = (23.625,-54,0)
  Subdivisions = 0
FEATURE [Part::Part2DObjectPython] Arc385  # Draft 2D object (typed FeaturePython)
  FirstAngle = -90
  LastAngle = 0
  MakeFace = false
  Placement = pos=(210.75,-35,0) rot=(0,0,1;0rad)
  Radius = 0.5
FEATURE [Part::Part2DObjectPython] Line744  # Draft 2D object (typed FeaturePython)
  ChamferSize = 0
  Closed = false
  End = (192.25,-22,0)
  FilletRadius = 0
  Length = 13
  MakeFace = false
  Placement = pos=(192.25,-35,0) rot=(0,0,1;0rad)
  Points = (2) [(0,0,0),(0,13,0)]
  Start = (192.25,-35,0)
  Subdivisions = 0
FEATURE [Part::Part2DObjectPython] Line745  # Draft 2D object (typed FeaturePython)
  ChamferSize = 0
  Closed = false
  End = (156.75,-38,0)
  FilletRadius = 0
  Length = 19
  MakeFace = false
  Placement = pos=(156.75,-19,0) rot=(0,0,1;0rad)
  Points = (2) [(0,0,0),(0,-19,0)]
  Start = (156.75,-19,0)
  Subdivisions = 0
FEATURE [Part::Part2DObjectPython] Arc386  # Draft 2D object (typed FeaturePython)
  FirstAngle = -90
  LastAngle = 0
  MakeFace = false
  Placement = pos=(191.75,-35,0) rot=(0,0,1;0rad)
  Radius = 0.5
FEATURE [Part::Part2DObjectPython] Line746  # Draft 2D object (typed FeaturePython)
  ChamferSize = 0
  Closed = false
  End = (137.75,-38,0)
  FilletRadius = 0
  Length = 19
  MakeFace = false
  Placement = pos=(156.75,-38,0) rot=(0,0,1;0rad)
  Points = (2) [(0,0,0),(-19,0,0)]
  Start = (156.75,-38,0)
  Subdivisions = 0
FEATURE [Part::Part2DObjectPython] Line747  # Draft 2D object (typed FeaturePython)
  ChamferSize = 0
  Closed = false
  End = (173.25,-22,0)
  FilletRadius = 0
  Length = 13
  MakeFace = false
  Placement = pos=(173.25,-35,0) rot=(0,0,1;0rad)
  Points = (2) [(0,0,0),(0,13,0)]
  Start = (173.25,-35,0)
  Subdivisions = 0
FEATURE [Part::Part2DObjectPython] Line748  # Draft 2D object (typed FeaturePython)
  ChamferSize = 0
  Closed = false
  End = (172.75,-21.5,0)
  FilletRadius = 0
  Length = 13
  MakeFace = false
  Placement = pos=(159.75,-21.5,0) rot=(0,0,1;0rad)
  Points = (2) [(0,0,0),(13,0,0)]
  Start = (159.75,-21.5,0)
  Subdivisions = 0
FEATURE [Part::Part2DObjectPython] Line749  # Draft 2D object (typed FeaturePython)
  ChamferSize = 0
  Closed = false
  End = (159.25,-35,0)
  FilletRadius = 0
  Length = 13
  MakeFace = false
  Placement = pos=(159.25,-22,0) rot=(0,0,1;0rad)
  Points = (2) [(0,0,0),(0,-13,0)]
  Start = (159.25,-22,0)
  Subdivisions = 0
FEATURE [Part::Part2DObjectPython] Arc387  # Draft 2D object (typed FeaturePython)
  FirstAngle = 90
  LastAngle = 180
  MakeFace = false
  Placement = pos=(159.75,-22,0) rot=(0,0,1;0rad)
  Radius = 0.5
FEATURE [Part::Part2DObjectPython] Line750  # Draft 2D object (typed FeaturePython)
  ChamferSize = 0
  Closed = false
  End = (194.75,-38,0)
  FilletRadius = 0
  Length = 19
  MakeFace = false
  Placement = pos=(194.75,-19,0) rot=(0,0,1;0rad)
  Points = (2) [(0,0,0),(0,-19,0)]
  Start = (194.75,-19,0)
  Subdivisions = 0
FEATURE [Part::Part2DObjectPython] Line751  # Draft 2D object (typed FeaturePython)
  ChamferSize = 0
  Closed = false
  End = (33.25,-57,0)
  FilletRadius = 0
  Length = 19
  MakeFace = false
  Placement = pos=(33.25,-38,0) rot=(0,0,1;0rad)
  Points = (2) [(0,0,0),(0,-19,0)]
  Start = (33.25,-38,0)
  Subdivisions = 0
FEATURE [Part::Part2DObjectPython] Line752  # Draft 2D object (typed FeaturePython)
  ChamferSize = 0
  Closed = false
  End = (178.25,-35,0)
  FilletRadius = 0
  Length = 13
  MakeFace = false
  Placement = pos=(178.25,-22,0) rot=(0,0,1;0rad)
  Points = (2) [(0,0,0),(0,-13,0)]
  Start = (178.25,-22,0)
  Subdivisions = 0
FEATURE [Part::Part2DObjectPython] Line753  # Draft 2D object (typed FeaturePython)
  ChamferSize = 0
  Closed = false
  End = (191.75,-21.5,0)
  FilletRadius = 0
  Length = 13
  MakeFace = false
  Placement = pos=(178.75,-21.5,0) rot=(0,0,1;0rad)
  Points = (2) [(0,0,0),(13,0,0)]
  Start = (178.75,-21.5,0)
  Subdivisions = 0
FEATURE [Part::Part2DObjectPython] Arc388  # Draft 2D object (typed FeaturePython)
  FirstAngle = 180
  LastAngle = 270
  MakeFace = false
  Placement = pos=(159.75,-35,0) rot=(0,0,1;0rad)
  Radius = 0.5
FEATURE [Part::Part2DObjectPython] Arc389  # Draft 2D object (typed FeaturePython)
  FirstAngle = 0
  LastAngle = 90
  MakeFace = false
  Placement = pos=(172.75,-22,0) rot=(0,0,1;0rad)
  Radius = 0.5
FEATURE [Part::Part2DObjectPython] Arc390  # Draft 2D object (typed FeaturePython)
  FirstAngle = 90
  LastAngle = 180
  MakeFace = false
  Placement = pos=(178.75,-22,0) rot=(0,0,1;0rad)
  Radius = 0.5
FEATURE [Part::Part2DObjectPython] Arc391  # Draft 2D object (typed FeaturePython)
  FirstAngle = 180
  LastAngle = 270
  MakeFace = false
  Placement = pos=(178.75,-35,0) rot=(0,0,1;0rad)
  Radius = 0.5
FEATURE [Part::Part2DObjectPython] Line754  # Draft 2D object (typed FeaturePython)
  ChamferSize = 0
  Closed = false
  End = (175.75,-38,0)
  FilletRadius = 0
  Length = 19
  MakeFace = false
  Placement = pos=(194.75,-38,0) rot=(0,0,1;0rad)
  Points = (2) [(0,0,0),(-19,0,0)]
  Start = (194.75,-38,0)
  Subdivisions = 0
FEATURE [Part::Part2DObjectPython] Arc392  # Draft 2D object (typed FeaturePython)
  FirstAngle = -90
  LastAngle = 0
  MakeFace = false
  Placement = pos=(172.75,-35,0) rot=(0,0,1;0rad)
  Radius = 0.5
FEATURE [Part::Part2DObjectPython] Line755  # Draft 2D object (typed FeaturePython)
  ChamferSize = 0
  Closed = false
  End = (172.75,-35.5,0)
  FilletRadius = 0
  Length = 13
  MakeFace = false
  Placement = pos=(159.75,-35.5,0) rot=(0,0,1;0rad)
  Points = (2) [(0,0,0),(13,0,0)]
  Start = (159.75,-35.5,0)
  Subdivisions = 0
FEATURE [Part::Part2DObjectPython] Line756  # Draft 2D object (typed FeaturePython)
  ChamferSize = 0
  Closed = false
  End = (153.75,-21.5,0)
  FilletRadius = 0
  Length = 13
  MakeFace = false
  Placement = pos=(140.75,-21.5,0) rot=(0,0,1;0rad)
  Points = (2) [(0,0,0),(13,0,0)]
  Start = (140.75,-21.5,0)
  Subdivisions = 0
FEATURE [Part::Part2DObjectPython] Line757  # Draft 2D object (typed FeaturePython)
  ChamferSize = 0
  Closed = false
  End = (156.75,-38,0)
  FilletRadius = 0
  Length = 19
  MakeFace = false
  Placement = pos=(175.75,-38,0) rot=(0,0,1;0rad)
  Points = (2) [(0,0,0),(-19,0,0)]
  Start = (175.75,-38,0)
  Subdivisions = 0
FEATURE [Part::Part2DObjectPython] Line758  # Draft 2D object (typed FeaturePython)
  ChamferSize = 0
  Closed = false
  End = (194.75,-19,0)
  FilletRadius = 0
  Length = 19
  MakeFace = false
  Placement = pos=(175.75,-19,0) rot=(0,0,1;0rad)
  Points = (2) [(0,0,0),(19,0,0)]
  Start = (175.75,-19,0)
  Subdivisions = 0
FEATURE [Part::Part2DObjectPython] Line759  # Draft 2D object (typed FeaturePython)
  ChamferSize = 0
  Closed = false
  End = (175.75,-19,0)
  FilletRadius = 0
  Length = 19
  MakeFace = false
  Placement = pos=(156.75,-19,0) rot=(0,0,1;0rad)
  Points = (2) [(0,0,0),(19,0,0)]
  Start = (156.75,-19,0)
  Subdivisions = 0
FEATURE [Part::Part2DObjectPython] Line760  # Draft 2D object (typed FeaturePython)
  ChamferSize = 0
  Closed = false
  End = (175.75,-38,0)
  FilletRadius = 0
  Length = 19
  MakeFace = false
  Placement = pos=(175.75,-19,0) rot=(0,0,1;0rad)
  Points = (2) [(0,0,0),(0,-19,0)]
  Start = (175.75,-19,0)
  Subdivisions = 0
FEATURE [Part::Part2DObjectPython] Line761  # Draft 2D object (typed FeaturePython)
  ChamferSize = 0
  Closed = false
  End = (191.75,-35.5,0)
  FilletRadius = 0
  Length = 13
  MakeFace = false
  Placement = pos=(178.75,-35.5,0) rot=(0,0,1;0rad)
  Points = (2) [(0,0,0),(13,0,0)]
  Start = (178.75,-35.5,0)
  Subdivisions = 0
FEATURE [Part::Part2DObjectPython] Arc393  # Draft 2D object (typed FeaturePython)
  FirstAngle = 0
  LastAngle = 90
  MakeFace = false
  Placement = pos=(210.75,-22,0) rot=(0,0,1;0rad)
  Radius = 0.5
FEATURE [Part::Part2DObjectPython] Line762  # Draft 2D object (typed FeaturePython)
  ChamferSize = 0
  Closed = false
  End = (211.25,-22,0)
  FilletRadius = 0
  Length = 13
  MakeFace = false
  Placement = pos=(211.25,-35,0) rot=(0,0,1;0rad)
  Points = (2) [(0,0,0),(0,13,0)]
  Start = (211.25,-35,0)
  Subdivisions = 0
FEATURE [Part::Part2DObjectPython] Line763  # Draft 2D object (typed FeaturePython)
  ChamferSize = 0
  Closed = false
  End = (23.125,-54.5,0)
  FilletRadius = 0
  Length = 13
  MakeFace = false
  Placement = pos=(10.125,-54.5,0) rot=(0,0,1;0rad)
  Points = (2) [(0,0,0),(13,0,0)]
  Start = (10.125,-54.5,0)
  Subdivisions = 0
FEATURE [Part::Part2DObjectPython] Line764  # Draft 2D object (typed FeaturePython)
  ChamferSize = 0
  Closed = false
  End = (9.625,-54,0)
  FilletRadius = 0
  Length = 13
  MakeFace = false
  Placement = pos=(9.625,-41,0) rot=(0,0,1;0rad)
  Points = (2) [(0,0,0),(0,-13,0)]
  Start = (9.625,-41,0)
  Subdivisions = 0
FEATURE [Part::Part2DObjectPython] Arc394  # Draft 2D object (typed FeaturePython)
  FirstAngle = 90
  LastAngle = 180
  MakeFace = false
  Placement = pos=(10.125,-41,0) rot=(0,0,1;0rad)
  Radius = 0.5
FEATURE [Part::Part2DObjectPython] Line765  # Draft 2D object (typed FeaturePython)
  ChamferSize = 0
  Closed = false
  End = (237.375,-22,0)
  FilletRadius = 0
  Length = 13
  MakeFace = false
  Placement = pos=(237.375,-35,0) rot=(0,0,1;0rad)
  Points = (2) [(0,0,0),(0,13,0)]
  Start = (237.375,-35,0)
  Subdivisions = 0
FEATURE [Part::Part2DObjectPython] Line766  # Draft 2D object (typed FeaturePython)
  ChamferSize = 0
  Closed = false
  End = (0,-57,0)
  FilletRadius = 0
  Length = 19
  MakeFace = false
  Placement = pos=(0,-38,0) rot=(0,0,1;0rad)
  Points = (2) [(0,0,0),(0,-19,0)]
  Start = (0,-38,0)
  Subdivisions = 0
FEATURE [Part::Part2DObjectPython] Line767  # Draft 2D object (typed FeaturePython)
  ChamferSize = 0
  Closed = false
  End = (210.75,-21.5,0)
  FilletRadius = 0
  Length = 13
  MakeFace = false
  Placement = pos=(197.75,-21.5,0) rot=(0,0,1;0rad)
  Points = (2) [(0,0,0),(13,0,0)]
  Start = (197.75,-21.5,0)
  Subdivisions = 0
FEATURE [Part::Part2DObjectPython] Line768  # Draft 2D object (typed FeaturePython)
  ChamferSize = 0
  Closed = false
  End = (236.875,-35.5,0)
  FilletRadius = 0
  Length = 13
  MakeFace = false
  Placement = pos=(223.875,-35.5,0) rot=(0,0,1;0rad)
  Points = (2) [(0,0,0),(13,0,0)]
  Start = (223.875,-35.5,0)
  Subdivisions = 0
FEATURE [Part::Part2DObjectPython] Arc395  # Draft 2D object (typed FeaturePython)
  FirstAngle = -90
  LastAngle = 0
  MakeFace = false
  Placement = pos=(236.875,-35,0) rot=(0,0,1;0rad)
  Radius = 0.5
FEATURE [Part::Part2DObjectPython] Arc396  # Draft 2D object (typed FeaturePython)
  FirstAngle = -90
  LastAngle = 0
  MakeFace = false
  Placement = pos=(23.125,-54,0) rot=(0,0,1;0rad)
  Radius = 0.5
FEATURE [Part::Part2DObjectPython] Line769  # Draft 2D object (typed FeaturePython)
  ChamferSize = 0
  Closed = false
  End = (33.25,-57,0)
  FilletRadius = 0
  Length = 33.25
  MakeFace = false
  Placement = pos=(0,-57,0) rot=(0,0,1;0rad)
  Points = (2) [(0,0,0),(33.25,0,0)]
  Start = (0,-57,0)
  Subdivisions = 0
FEATURE [Part::Part2DObjectPython] Line770  # Draft 2D object (typed FeaturePython)
  ChamferSize = 0
  Closed = false
  End = (223.375,-35,0)
  FilletRadius = 0
  Length = 13
  MakeFace = false
  Placement = pos=(223.375,-22,0) rot=(0,0,1;0rad)
  Points = (2) [(0,0,0),(0,-13,0)]
  Start = (223.375,-22,0)
  Subdivisions = 0
FEATURE [Part::Part2DObjectPython] Arc397  # Draft 2D object (typed FeaturePython)
  FirstAngle = 90
  LastAngle = 180
  MakeFace = false
  Placement = pos=(223.875,-22,0) rot=(0,0,1;0rad)
  Radius = 0.5
FEATURE [Part::Part2DObjectPython] Line771  # Draft 2D object (typed FeaturePython)
  ChamferSize = 0
  Closed = false
  End = (197.25,-35,0)
  FilletRadius = 0
  Length = 13
  MakeFace = false
  Placement = pos=(197.25,-22,0) rot=(0,0,1;0rad)
  Points = (2) [(0,0,0),(0,-13,0)]
  Start = (197.25,-22,0)
  Subdivisions = 0
FEATURE [Part::Part2DObjectPython] Line772  # Draft 2D object (typed FeaturePython)
  ChamferSize = 0
  Closed = false
  End = (213.75,-19,0)
  FilletRadius = 0
  Length = 19
  MakeFace = false
  Placement = pos=(194.75,-19,0) rot=(0,0,1;0rad)
  Points = (2) [(0,0,0),(19,0,0)]
  Start = (194.75,-19,0)
  Subdivisions = 0
FEATURE [Part::Part2DObjectPython] Line773  # Draft 2D object (typed FeaturePython)
  ChamferSize = 0
  Closed = false
  End = (194.75,-38,0)
  FilletRadius = 0
  Length = 19
  MakeFace = false
  Placement = pos=(194.75,-19,0) rot=(0,0,1;0rad)
  Points = (2) [(0,0,0),(0,-19,0)]
  Start = (194.75,-19,0)
  Subdivisions = 0
FEATURE [Part::Part2DObjectPython] Arc398  # Draft 2D object (typed FeaturePython)
  FirstAngle = 180
  LastAngle = 270
  MakeFace = false
  Placement = pos=(197.75,-35,0) rot=(0,0,1;0rad)
  Radius = 0.5
FEATURE [Part::Part2DObjectPython] Line774  # Draft 2D object (typed FeaturePython)
  ChamferSize = 0
  Closed = false
  End = (213.75,-38,0)
  FilletRadius = 0
  Length = 19
  MakeFace = false
  Placement = pos=(213.75,-19,0) rot=(0,0,1;0rad)
  Points = (2) [(0,0,0),(0,-19,0)]
  Start = (213.75,-19,0)
  Subdivisions = 0
FEATURE [Part::Part2DObjectPython] Line775  # Draft 2D object (typed FeaturePython)
  ChamferSize = 0
  Closed = false
  End = (194.75,-38,0)
  FilletRadius = 0
  Length = 19
  MakeFace = false
  Placement = pos=(213.75,-38,0) rot=(0,0,1;0rad)
  Points = (2) [(0,0,0),(-19,0,0)]
  Start = (213.75,-38,0)
  Subdivisions = 0
FEATURE [Part::Part2DObjectPython] Line776  # Draft 2D object (typed FeaturePython)
  ChamferSize = 0
  Closed = false
  End = (213.75,-38,0)
  FilletRadius = 0
  Length = 19
  MakeFace = false
  Placement = pos=(213.75,-19,0) rot=(0,0,1;0rad)
  Points = (2) [(0,0,0),(0,-19,0)]
  Start = (213.75,-19,0)
  Subdivisions = 0
FEATURE [Part::Part2DObjectPython] Line777  # Draft 2D object (typed FeaturePython)
  ChamferSize = 0
  Closed = false
  End = (247,-38,0)
  FilletRadius = 0
  Length = 33.25
  MakeFace = false
  Placement = pos=(213.75,-38,0) rot=(0,0,1;0rad)
  Points = (2) [(0,0,0),(33.25,0,0)]
  Start = (213.75,-38,0)
  Subdivisions = 0
FEATURE [Part::Part2DObjectPython] Line778  # Draft 2D object (typed FeaturePython)
  ChamferSize = 0
  Closed = false
  End = (247,-38,0)
  FilletRadius = 0
  Length = 19
  MakeFace = false
  Placement = pos=(247,-19,0) rot=(0,0,1;0rad)
  Points = (2) [(0,0,0),(0,-19,0)]
  Start = (247,-19,0)
  Subdivisions = 0
FEATURE [Part::Part2DObjectPython] Arc399  # Draft 2D object (typed FeaturePython)
  FirstAngle = 0
  LastAngle = 90
  MakeFace = false
  Placement = pos=(236.875,-22,0) rot=(0,0,1;0rad)
  Radius = 0.5
FEATURE [Part::Part2DObjectPython] Line779  # Draft 2D object (typed FeaturePython)
  ChamferSize = 0
  Closed = false
  End = (236.875,-21.5,0)
  FilletRadius = 0
  Length = 13
  MakeFace = false
  Placement = pos=(223.875,-21.5,0) rot=(0,0,1;0rad)
  Points = (2) [(0,0,0),(13,0,0)]
  Start = (223.875,-21.5,0)
  Subdivisions = 0
FEATURE [Part::Part2DObjectPython] Line780  # Draft 2D object (typed FeaturePython)
  ChamferSize = 0
  Closed = false
  End = (210.75,-35.5,0)
  FilletRadius = 0
  Length = 13
  MakeFace = false
  Placement = pos=(197.75,-35.5,0) rot=(0,0,1;0rad)
  Points = (2) [(0,0,0),(13,0,0)]
  Start = (197.75,-35.5,0)
  Subdivisions = 0
FEATURE [Part::Part2DObjectPython] Line781  # Draft 2D object (typed FeaturePython)
  ChamferSize = 0
  Closed = false
  End = (247,-19,0)
  FilletRadius = 0
  Length = 33.25
  MakeFace = false
  Placement = pos=(213.75,-19,0) rot=(0,0,1;0rad)
  Points = (2) [(0,0,0),(33.25,0,0)]
  Start = (213.75,-19,0)
  Subdivisions = 0
FEATURE [Part::Part2DObjectPython] Arc400  # Draft 2D object (typed FeaturePython)
  FirstAngle = 180
  LastAngle = 270
  MakeFace = false
  Placement = pos=(223.875,-35,0) rot=(0,0,1;0rad)
  Radius = 0.5
FEATURE [Part::Part2DObjectPython] Arc401  # Draft 2D object (typed FeaturePython)
  FirstAngle = 90
  LastAngle = 180
  MakeFace = false
  Placement = pos=(197.75,-22,0) rot=(0,0,1;0rad)
  Radius = 0.5
FEATURE [Part::Part2DObjectPython] Arc402  # Draft 2D object (typed FeaturePython)
  FirstAngle = 0
  LastAngle = 90
  MakeFace = false
  Placement = pos=(23.125,-41,0) rot=(0,0,1;0rad)
  Radius = 0.5
FEATURE [Part::Part2DObjectPython] Line782  # Draft 2D object (typed FeaturePython)
  ChamferSize = 0
  Closed = false
  End = (23.125,-40.5,0)
  FilletRadius = 0
  Length = 13
  MakeFace = false
  Placement = pos=(10.125,-40.5,0) rot=(0,0,1;0rad)
  Points = (2) [(0,0,0),(13,0,0)]
  Start = (10.125,-40.5,0)
  Subdivisions = 0
FEATURE [Part::Part2DObjectPython] Line783  # Draft 2D object (typed FeaturePython)
  ChamferSize = 0
  Closed = false
  End = (33.25,-38,0)
  FilletRadius = 0
  Length = 33.25
  MakeFace = false
  Placement = pos=(0,-38,0) rot=(0,0,1;0rad)
  Points = (2) [(0,0,0),(33.25,0,0)]
  Start = (0,-38,0)
  Subdivisions = 0
FEATURE [Part::Part2DObjectPython] Arc403  # Draft 2D object (typed FeaturePython)
  FirstAngle = 180
  LastAngle = 270
  MakeFace = false
  Placement = pos=(10.125,-54,0) rot=(0,0,1;0rad)
  Radius = 0.5
FEATURE [Part::Part2DObjectPython] Arc404  # Draft 2D object (typed FeaturePython)
  FirstAngle = 0
  LastAngle = 90
  MakeFace = false
  Placement = pos=(145.438,-74,0) rot=(0,0,1;0rad)
  Radius = 0.5
FEATURE [Part::Part2DObjectPython] Line784  # Draft 2D object (typed FeaturePython)
  ChamferSize = 0
  Closed = false
  End = (145.938,-75.7,0)
  FilletRadius = 0
  Length = 1.7
  MakeFace = false
  Placement = pos=(145.938,-74,0) rot=(0,0,1;0rad)
  Points = (2) [(0,0,0),(0,-1.7,0)]
  Start = (145.938,-74,0)
  Subdivisions = 0
FEATURE [Part::Part2DObjectPython] Line785  # Draft 2D object (typed FeaturePython)
  ChamferSize = 0
  Closed = false
  End = (49.25,-54.5,0)
  FilletRadius = 0
  Length = 13
  MakeFace = false
  Placement = pos=(36.25,-54.5,0) rot=(0,0,1;0rad)
  Points = (2) [(0,0,0),(13,0,0)]
  Start = (36.25,-54.5,0)
  Subdivisions = 0
FEATURE [Part::Part2DObjectPython] Line786  # Draft 2D object (typed FeaturePython)
  ChamferSize = 0
  Closed = false
  End = (52.25,-57,0)
  FilletRadius = 0
  Length = 19
  MakeFace = false
  Placement = pos=(52.25,-38,0) rot=(0,0,1;0rad)
  Points = (2) [(0,0,0),(0,-19,0)]
  Start = (52.25,-38,0)
  Subdivisions = 0
FEATURE [Part::Part2DObjectPython] Arc405  # Draft 2D object (typed FeaturePython)
  FirstAngle = 0
  LastAngle = 90
  MakeFace = false
  Placement = pos=(87.25,-41,0) rot=(0,0,1;0rad)
  Radius = 0.5
FEATURE [Part::Part2DObjectPython] Line787  # Draft 2D object (typed FeaturePython)
  ChamferSize = 0
  Closed = false
  End = (153.438,-56.5,0)
  FilletRadius = 0
  Length = 19.2
  MakeFace = false
  Placement = pos=(153.438,-75.7,0) rot=(0,0,1;3.14159rad)
  Points = (2) [(0,0,0),(0,-19.2,0)]
  Start = (153.438,-75.7,0)
  Subdivisions = 0
FEATURE [Part::Part2DObjectPython] Line788  # Draft 2D object (typed FeaturePython)
  ChamferSize = 0
  Closed = false
  End = (52.25,-57,0)
  FilletRadius = 0
  Length = 19
  MakeFace = false
  Placement = pos=(52.25,-38,0) rot=(0,0,1;0rad)
  Points = (2) [(0,0,0),(0,-19,0)]
  Start = (52.25,-38,0)
  Subdivisions = 0
FEATURE [Part::Part2DObjectPython] Line789  # Draft 2D object (typed FeaturePython)
  ChamferSize = 0
  Closed = false
  End = (33.25,-57,0)
  FilletRadius = 0
  Length = 19
  MakeFace = false
  Placement = pos=(33.25,-38,0) rot=(0,0,1;0rad)
  Points = (2) [(0,0,0),(0,-19,0)]
  Start = (33.25,-38,0)
  Subdivisions = 0
FEATURE [Part::Part2DObjectPython] Arc406  # Draft 2D object (typed FeaturePython)
  FirstAngle = 0
  LastAngle = 90
  MakeFace = false
  Placement = pos=(49.25,-41,0) rot=(0,0,1;0rad)
  Radius = 0.5
FEATURE [Part::Part2DObjectPython] Line790  # Draft 2D object (typed FeaturePython)
  ChamferSize = 0
  Closed = false
  End = (49.75,-41,0)
  FilletRadius = 0
  Length = 13
  MakeFace = false
  Placement = pos=(49.75,-54,0) rot=(0,0,1;0rad)
  Points = (2) [(0,0,0),(0,13,0)]
  Start = (49.75,-54,0)
  Subdivisions = 0
FEATURE [Part::Part2DObjectPython] Arc407  # Draft 2D object (typed FeaturePython)
  FirstAngle = 0
  LastAngle = 90
  MakeFace = false
  Placement = pos=(68.25,-41,0) rot=(0,0,1;0rad)
  Radius = 0.5
FEATURE [Part::Part2DObjectPython] Arc408  # Draft 2D object (typed FeaturePython)
  FirstAngle = -90
  LastAngle = 0
  MakeFace = false
  Placement = pos=(68.25,-54,0) rot=(0,0,1;0rad)
  Radius = 0.5
FEATURE [Part::Part2DObjectPython] Line791  # Draft 2D object (typed FeaturePython)
  ChamferSize = 0
  Closed = false
  End = (71.25,-38,0)
  FilletRadius = 0
  Length = 19
  MakeFace = false
  Placement = pos=(52.25,-38,0) rot=(0,0,1;0rad)
  Points = (2) [(0,0,0),(19,0,0)]
  Start = (52.25,-38,0)
  Subdivisions = 0
FEATURE [Part::Part2DObjectPython] Line792  # Draft 2D object (typed FeaturePython)
  ChamferSize = 0
  Closed = false
  End = (68.25,-54.5,0)
  FilletRadius = 0
  Length = 13
  MakeFace = false
  Placement = pos=(55.25,-54.5,0) rot=(0,0,1;0rad)
  Points = (2) [(0,0,0),(13,0,0)]
  Start = (55.25,-54.5,0)
  Subdivisions = 0
FEATURE [Part::Part2DObjectPython] Line793  # Draft 2D object (typed FeaturePython)
  ChamferSize = 0
  Closed = false
  End = (172.75,-73.5,0)
  FilletRadius = 0
  Length = 13
  MakeFace = false
  Placement = pos=(159.75,-73.5,0) rot=(0,0,1;0rad)
  Points = (2) [(0,0,0),(13,0,0)]
  Start = (159.75,-73.5,0)
  Subdivisions = 0
FEATURE [Part::Part2DObjectPython] Line794  # Draft 2D object (typed FeaturePython)
  ChamferSize = 0
  Closed = false
  End = (68.75,-41,0)
  FilletRadius = 0
  Length = 13
  MakeFace = false
  Placement = pos=(68.75,-54,0) rot=(0,0,1;0rad)
  Points = (2) [(0,0,0),(0,13,0)]
  Start = (68.75,-54,0)
  Subdivisions = 0
FEATURE [Part::Part2DObjectPython] Arc409  # Draft 2D object (typed FeaturePython)
  FirstAngle = 180
  LastAngle = 270
  MakeFace = false
  Placement = pos=(55.25,-54,0) rot=(0,0,1;0rad)
  Radius = 0.5
FEATURE [Part::Part2DObjectPython] Line795  # Draft 2D object (typed FeaturePython)
  ChamferSize = 0
  Closed = false
  End = (52.25,-57,0)
  FilletRadius = 0
  Length = 19
  MakeFace = false
  Placement = pos=(71.25,-57,0) rot=(0,0,1;0rad)
  Points = (2) [(0,0,0),(-19,0,0)]
  Start = (71.25,-57,0)
  Subdivisions = 0
FEATURE [Part::Part2DObjectPython] Line796  # Draft 2D object (typed FeaturePython)
  ChamferSize = 0
  Closed = false
  End = (49.25,-40.5,0)
  FilletRadius = 0
  Length = 13
  MakeFace = false
  Placement = pos=(36.25,-40.5,0) rot=(0,0,1;0rad)
  Points = (2) [(0,0,0),(13,0,0)]
  Start = (36.25,-40.5,0)
  Subdivisions = 0
FEATURE [Part::Part2DObjectPython] Arc410  # Draft 2D object (typed FeaturePython)
  FirstAngle = -90
  LastAngle = 0
  MakeFace = false
  Placement = pos=(87.25,-54,0) rot=(0,0,1;0rad)
  Radius = 0.5
FEATURE [Part::Part2DObjectPython] Line797  # Draft 2D object (typed FeaturePython)
  ChamferSize = 0
  Closed = false
  End = (87.25,-54.5,0)
  FilletRadius = 0
  Length = 13
  MakeFace = false
  Placement = pos=(74.25,-54.5,0) rot=(0,0,1;0rad)
  Points = (2) [(0,0,0),(13,0,0)]
  Start = (74.25,-54.5,0)
  Subdivisions = 0
FEATURE [Part::Part2DObjectPython] Arc411  # Draft 2D object (typed FeaturePython)
  FirstAngle = 90
  LastAngle = 180
  MakeFace = false
  Placement = pos=(36.25,-41,0) rot=(0,0,1;0rad)
  Radius = 0.5
FEATURE [Part::Part2DObjectPython] Line798  # Draft 2D object (typed FeaturePython)
  ChamferSize = 0
  Closed = false
  End = (35.75,-54,0)
  FilletRadius = 0
  Length = 13
  MakeFace = false
  Placement = pos=(35.75,-41,0) rot=(0,0,1;0rad)
  Points = (2) [(0,0,0),(0,-13,0)]
  Start = (35.75,-41,0)
  Subdivisions = 0
FEATURE [Part::Part2DObjectPython] Arc412  # Draft 2D object (typed FeaturePython)
  FirstAngle = 180
  LastAngle = 270
  MakeFace = false
  Placement = pos=(36.25,-54,0) rot=(0,0,1;0rad)
  Radius = 0.5
FEATURE [Part::Part2DObjectPython] Line799  # Draft 2D object (typed FeaturePython)
  ChamferSize = 0
  Closed = false
  End = (33.25,-57,0)
  FilletRadius = 0
  Length = 19
  MakeFace = false
  Placement = pos=(52.25,-57,0) rot=(0,0,1;0rad)
  Points = (2) [(0,0,0),(-19,0,0)]
  Start = (52.25,-57,0)
  Subdivisions = 0
FEATURE [Part::Part2DObjectPython] Arc413  # Draft 2D object (typed FeaturePython)
  FirstAngle = -90
  LastAngle = 0
  MakeFace = false
  Placement = pos=(49.25,-54,0) rot=(0,0,1;0rad)
  Radius = 0.5
FEATURE [Part::Part2DObjectPython] Line800  # Draft 2D object (typed FeaturePython)
  ChamferSize = 0
  Closed = false
  End = (68.25,-40.5,0)
  FilletRadius = 0
  Length = 13
  MakeFace = false
  Placement = pos=(55.25,-40.5,0) rot=(0,0,1;0rad)
  Points = (2) [(0,0,0),(13,0,0)]
  Start = (55.25,-40.5,0)
  Subdivisions = 0
FEATURE [Part::Part2DObjectPython] Arc414  # Draft 2D object (typed FeaturePython)
  FirstAngle = 90
  LastAngle = 180
  MakeFace = false
  Placement = pos=(55.25,-41,0) rot=(0,0,1;0rad)
  Radius = 0.5
FEATURE [Part::Part2DObjectPython] Line801  # Draft 2D object (typed FeaturePython)
  ChamferSize = 0
  Closed = false
  End = (52.25,-38,0)
  FilletRadius = 0
  Length = 19
  MakeFace = false
  Placement = pos=(33.25,-38,0) rot=(0,0,1;0rad)
  Points = (2) [(0,0,0),(19,0,0)]
  Start = (33.25,-38,0)
  Subdivisions = 0
FEATURE [Part::Part2DObjectPython] Line802  # Draft 2D object (typed FeaturePython)
  ChamferSize = 0
  Closed = false
  End = (71.25,-57,0)
  FilletRadius = 0
  Length = 19
  MakeFace = false
  Placement = pos=(71.25,-38,0) rot=(0,0,1;0rad)
  Points = (2) [(0,0,0),(0,-19,0)]
  Start = (71.25,-38,0)
  Subdivisions = 0
FEATURE [Part::Part2DObjectPython] Line803  # Draft 2D object (typed FeaturePython)
  ChamferSize = 0
  Closed = false
  End = (71.25,-57,0)
  FilletRadius = 0
  Length = 19
  MakeFace = false
  Placement = pos=(71.25,-38,0) rot=(0,0,1;0rad)
  Points = (2) [(0,0,0),(0,-19,0)]
  Start = (71.25,-38,0)
  Subdivisions = 0
FEATURE [Part::Part2DObjectPython] Line804  # Draft 2D object (typed FeaturePython)
  ChamferSize = 0
  Closed = false
  End = (54.75,-54,0)
  FilletRadius = 0
  Length = 13
  MakeFace = false
  Placement = pos=(54.75,-41,0) rot=(0,0,1;0rad)
  Points = (2) [(0,0,0),(0,-13,0)]
  Start = (54.75,-41,0)
  Subdivisions = 0
FEATURE [Part::Part2DObjectPython] Line805  # Draft 2D object (typed FeaturePython)
  ChamferSize = 0
  Closed = false
  End = (90.25,-38,0)
  FilletRadius = 0
  Length = 19
  MakeFace = false
  Placement = pos=(71.25,-38,0) rot=(0,0,1;0rad)
  Points = (2) [(0,0,0),(19,0,0)]
  Start = (71.25,-38,0)
  Subdivisions = 0
FEATURE [Part::Part2DObjectPython] Line806  # Draft 2D object (typed FeaturePython)
  ChamferSize = 0
  Closed = false
  End = (87.75,-41,0)
  FilletRadius = 0
  Length = 13
  MakeFace = false
  Placement = pos=(87.75,-54,0) rot=(0,0,1;0rad)
  Points = (2) [(0,0,0),(0,13,0)]
  Start = (87.75,-54,0)
  Subdivisions = 0
FEATURE [Part::Part2DObjectPython] Arc415  # Draft 2D object (typed FeaturePython)
  FirstAngle = 180
  LastAngle = 270
  MakeFace = false
  Placement = pos=(74.25,-54,0) rot=(0,0,1;0rad)
  Radius = 0.5
FEATURE [Part::Part2DObjectPython] Line807  # Draft 2D object (typed FeaturePython)
  ChamferSize = 0
  Closed = false
  End = (71.25,-57,0)
  FilletRadius = 0
  Length = 19
  MakeFace = false
  Placement = pos=(90.25,-57,0) rot=(0,0,1;0rad)
  Points = (2) [(0,0,0),(-19,0,0)]
  Start = (90.25,-57,0)
  Subdivisions = 0
FEATURE [Part::Part2DObjectPython] Line808  # Draft 2D object (typed FeaturePython)
  ChamferSize = 0
  Closed = false
  End = (87.25,-40.5,0)
  FilletRadius = 0
  Length = 13
  MakeFace = false
  Placement = pos=(74.25,-40.5,0) rot=(0,0,1;0rad)
  Points = (2) [(0,0,0),(13,0,0)]
  Start = (74.25,-40.5,0)
  Subdivisions = 0
FEATURE [Part::Part2DObjectPython] Line809  # Draft 2D object (typed FeaturePython)
  ChamferSize = 0
  Closed = false
  End = (147.25,-57,0)
  FilletRadius = 0
  Length = 19
  MakeFace = false
  Placement = pos=(147.25,-38,0) rot=(0,0,1;0rad)
  Points = (2) [(0,0,0),(0,-19,0)]
  Start = (147.25,-38,0)
  Subdivisions = 0
FEATURE [Part::Part2DObjectPython] Line810  # Draft 2D object (typed FeaturePython)
  ChamferSize = 0
  Closed = false
  End = (144.75,-41,0)
  FilletRadius = 0
  Length = 13
  MakeFace = false
  Placement = pos=(144.75,-54,0) rot=(0,0,1;0rad)
  Points = (2) [(0,0,0),(0,13,0)]
  Start = (144.75,-54,0)
  Subdivisions = 0
FEATURE [Part::Part2DObjectPython] Arc416  # Draft 2D object (typed FeaturePython)
  FirstAngle = -90
  LastAngle = 0
  MakeFace = false
  Placement = pos=(144.25,-54,0) rot=(0,0,1;0rad)
  Radius = 0.5
FEATURE [Part::Part2DObjectPython] Line811  # Draft 2D object (typed FeaturePython)
  ChamferSize = 0
  Closed = false
  End = (128.25,-38,0)
  FilletRadius = 0
  Length = 19
  MakeFace = false
  Placement = pos=(109.25,-38,0) rot=(0,0,1;0rad)
  Points = (2) [(0,0,0),(19,0,0)]
  Start = (109.25,-38,0)
  Subdivisions = 0
FEATURE [Part::Part2DObjectPython] Line812  # Draft 2D object (typed FeaturePython)
  ChamferSize = 0
  Closed = false
  End = (111.75,-54,0)
  FilletRadius = 0
  Length = 13
  MakeFace = false
  Placement = pos=(111.75,-41,0) rot=(0,0,1;0rad)
  Points = (2) [(0,0,0),(0,-13,0)]
  Start = (111.75,-41,0)
  Subdivisions = 0
FEATURE [Part::Part2DObjectPython] Line813  # Draft 2D object (typed FeaturePython)
  ChamferSize = 0
  Closed = false
  End = (128.25,-57,0)
  FilletRadius = 0
  Length = 19
  MakeFace = false
  Placement = pos=(128.25,-38,0) rot=(0,0,1;0rad)
  Points = (2) [(0,0,0),(0,-19,0)]
  Start = (128.25,-38,0)
  Subdivisions = 0
FEATURE [Part::Part2DObjectPython] Arc417  # Draft 2D object (typed FeaturePython)
  FirstAngle = 0
  LastAngle = 90
  MakeFace = false
  Placement = pos=(144.25,-41,0) rot=(0,0,1;0rad)
  Radius = 0.5
FEATURE [Part::Part2DObjectPython] Arc418  # Draft 2D object (typed FeaturePython)
  FirstAngle = 0
  LastAngle = 90
  MakeFace = false
  Placement = pos=(125.25,-41,0) rot=(0,0,1;0rad)
  Radius = 0.5
FEATURE [Part::Part2DObjectPython] Line814  # Draft 2D object (typed FeaturePython)
  ChamferSize = 0
  Closed = false
  End = (125.25,-40.5,0)
  FilletRadius = 0
  Length = 13
  MakeFace = false
  Placement = pos=(112.25,-40.5,0) rot=(0,0,1;0rad)
  Points = (2) [(0,0,0),(13,0,0)]
  Start = (112.25,-40.5,0)
  Subdivisions = 0
FEATURE [Part::Part2DObjectPython] Arc419  # Draft 2D object (typed FeaturePython)
  FirstAngle = 90
  LastAngle = 180
  MakeFace = false
  Placement = pos=(93.25,-41,0) rot=(0,0,1;0rad)
  Radius = 0.5
FEATURE [Part::Part2DObjectPython] Line815  # Draft 2D object (typed FeaturePython)
  ChamferSize = 0
  Closed = false
  End = (149.75,-54,0)
  FilletRadius = 0
  Length = 13
  MakeFace = false
  Placement = pos=(149.75,-41,0) rot=(0,0,1;0rad)
  Points = (2) [(0,0,0),(0,-13,0)]
  Start = (149.75,-41,0)
  Subdivisions = 0
FEATURE [Part::Part2DObjectPython] Arc420  # Draft 2D object (typed FeaturePython)
  FirstAngle = 90
  LastAngle = 180
  MakeFace = false
  Placement = pos=(112.25,-41,0) rot=(0,0,1;0rad)
  Radius = 0.5
FEATURE [Part::Part2DObjectPython] Arc421  # Draft 2D object (typed FeaturePython)
  FirstAngle = 180
  LastAngle = 270
  MakeFace = false
  Placement = pos=(112.25,-54,0) rot=(0,0,1;0rad)
  Radius = 0.5
FEATURE [Part::Part2DObjectPython] Line816  # Draft 2D object (typed FeaturePython)
  ChamferSize = 0
  Closed = false
  End = (125.75,-41,0)
  FilletRadius = 0
  Length = 13
  MakeFace = false
  Placement = pos=(125.75,-54,0) rot=(0,0,1;0rad)
  Points = (2) [(0,0,0),(0,13,0)]
  Start = (125.75,-54,0)
  Subdivisions = 0
FEATURE [Part::Part2DObjectPython] Line817  # Draft 2D object (typed FeaturePython)
  ChamferSize = 0
  Closed = false
  End = (109.25,-57,0)
  FilletRadius = 0
  Length = 19
  MakeFace = false
  Placement = pos=(109.25,-38,0) rot=(0,0,1;0rad)
  Points = (2) [(0,0,0),(0,-19,0)]
  Start = (109.25,-38,0)
  Subdivisions = 0
FEATURE [Part::Part2DObjectPython] Line818  # Draft 2D object (typed FeaturePython)
  ChamferSize = 0
  Closed = false
  End = (109.25,-57,0)
  FilletRadius = 0
  Length = 19
  MakeFace = false
  Placement = pos=(109.25,-38,0) rot=(0,0,1;0rad)
  Points = (2) [(0,0,0),(0,-19,0)]
  Start = (109.25,-38,0)
  Subdivisions = 0
FEATURE [Part::Part2DObjectPython] Line819  # Draft 2D object (typed FeaturePython)
  ChamferSize = 0
  Closed = false
  End = (147.25,-38,0)
  FilletRadius = 0
  Length = 19
  MakeFace = false
  Placement = pos=(128.25,-38,0) rot=(0,0,1;0rad)
  Points = (2) [(0,0,0),(19,0,0)]
  Start = (128.25,-38,0)
  Subdivisions = 0
FEATURE [Part::Part2DObjectPython] Arc422  # Draft 2D object (typed FeaturePython)
  FirstAngle = 180
  LastAngle = 270
  MakeFace = false
  Placement = pos=(93.25,-54,0) rot=(0,0,1;0rad)
  Radius = 0.5
FEATURE [Part::Part2DObjectPython] Line820  # Draft 2D object (typed FeaturePython)
  ChamferSize = 0
  Closed = false
  End = (92.75,-54,0)
  FilletRadius = 0
  Length = 13
  MakeFace = false
  Placement = pos=(92.75,-41,0) rot=(0,0,1;0rad)
  Points = (2) [(0,0,0),(0,-13,0)]
  Start = (92.75,-41,0)
  Subdivisions = 0
FEATURE [Part::Part2DObjectPython] Line821  # Draft 2D object (typed FeaturePython)
  ChamferSize = 0
  Closed = false
  End = (106.25,-40.5,0)
  FilletRadius = 0
  Length = 13
  MakeFace = false
  Placement = pos=(93.25,-40.5,0) rot=(0,0,1;0rad)
  Points = (2) [(0,0,0),(13,0,0)]
  Start = (93.25,-40.5,0)
  Subdivisions = 0
FEATURE [Part::Part2DObjectPython] Line822  # Draft 2D object (typed FeaturePython)
  ChamferSize = 0
  Closed = false
  End = (144.25,-40.5,0)
  FilletRadius = 0
  Length = 13
  MakeFace = false
  Placement = pos=(131.25,-40.5,0) rot=(0,0,1;0rad)
  Points = (2) [(0,0,0),(13,0,0)]
  Start = (131.25,-40.5,0)
  Subdivisions = 0
FEATURE [Part::Part2DObjectPython] Arc423  # Draft 2D object (typed FeaturePython)
  FirstAngle = -90
  LastAngle = 0
  MakeFace = false
  Placement = pos=(125.25,-54,0) rot=(0,0,1;0rad)
  Radius = 0.5
FEATURE [Part::Part2DObjectPython] Line823  # Draft 2D object (typed FeaturePython)
  ChamferSize = 0
  Closed = false
  End = (106.75,-41,0)
  FilletRadius = 0
  Length = 13
  MakeFace = false
  Placement = pos=(106.75,-54,0) rot=(0,0,1;0rad)
  Points = (2) [(0,0,0),(0,13,0)]
  Start = (106.75,-54,0)
  Subdivisions = 0
FEATURE [Part::Part2DObjectPython] Line824  # Draft 2D object (typed FeaturePython)
  ChamferSize = 0
  Closed = false
  End = (109.25,-57,0)
  FilletRadius = 0
  Length = 19
  MakeFace = false
  Placement = pos=(128.25,-57,0) rot=(0,0,1;0rad)
  Points = (2) [(0,0,0),(-19,0,0)]
  Start = (128.25,-57,0)
  Subdivisions = 0
FEATURE [Part::Part2DObjectPython] Line825  # Draft 2D object (typed FeaturePython)
  ChamferSize = 0
  Closed = false
  End = (125.25,-54.5,0)
  FilletRadius = 0
  Length = 13
  MakeFace = false
  Placement = pos=(112.25,-54.5,0) rot=(0,0,1;0rad)
  Points = (2) [(0,0,0),(13,0,0)]
  Start = (112.25,-54.5,0)
  Subdivisions = 0
FEATURE [Part::Part2DObjectPython] Line826  # Draft 2D object (typed FeaturePython)
  ChamferSize = 0
  Closed = false
  End = (130.75,-54,0)
  FilletRadius = 0
  Length = 13
  MakeFace = false
  Placement = pos=(130.75,-41,0) rot=(0,0,1;0rad)
  Points = (2) [(0,0,0),(0,-13,0)]
  Start = (130.75,-41,0)
  Subdivisions = 0
FEATURE [Part::Part2DObjectPython] Arc424  # Draft 2D object (typed FeaturePython)
  FirstAngle = 90
  LastAngle = 180
  MakeFace = false
  Placement = pos=(131.25,-41,0) rot=(0,0,1;0rad)
  Radius = 0.5
FEATURE [Part::Part2DObjectPython] Line827  # Draft 2D object (typed FeaturePython)
  ChamferSize = 0
  Closed = false
  End = (90.25,-57,0)
  FilletRadius = 0
  Length = 19
  MakeFace = false
  Placement = pos=(109.25,-57,0) rot=(0,0,1;0rad)
  Points = (2) [(0,0,0),(-19,0,0)]
  Start = (109.25,-57,0)
  Subdivisions = 0
FEATURE [Part::Part2DObjectPython] Arc425  # Draft 2D object (typed FeaturePython)
  FirstAngle = 180
  LastAngle = 270
  MakeFace = false
  Placement = pos=(131.25,-54,0) rot=(0,0,1;0rad)
  Radius = 0.5
FEATURE [Part::Part2DObjectPython] Line828  # Draft 2D object (typed FeaturePython)
  ChamferSize = 0
  Closed = false
  End = (128.25,-57,0)
  FilletRadius = 0
  Length = 19
  MakeFace = false
  Placement = pos=(128.25,-38,0) rot=(0,0,1;0rad)
  Points = (2) [(0,0,0),(0,-19,0)]
  Start = (128.25,-38,0)
  Subdivisions = 0
FEATURE [Part::Part2DObjectPython] Line829  # Draft 2D object (typed FeaturePython)
  ChamferSize = 0
  Closed = false
  End = (128.25,-57,0)
  FilletRadius = 0
  Length = 19
  MakeFace = false
  Placement = pos=(147.25,-57,0) rot=(0,0,1;0rad)
  Points = (2) [(0,0,0),(-19,0,0)]
  Start = (147.25,-57,0)
  Subdivisions = 0
FEATURE [Part::Part2DObjectPython] Line830  # Draft 2D object (typed FeaturePython)
  ChamferSize = 0
  Closed = false
  End = (144.25,-54.5,0)
  FilletRadius = 0
  Length = 13
  MakeFace = false
  Placement = pos=(131.25,-54.5,0) rot=(0,0,1;0rad)
  Points = (2) [(0,0,0),(13,0,0)]
  Start = (131.25,-54.5,0)
  Subdivisions = 0
FEATURE [Part::Part2DObjectPython] Line831  # Draft 2D object (typed FeaturePython)
  ChamferSize = 0
  Closed = false
  End = (166.25,-57,0)
  FilletRadius = 0
  Length = 19
  MakeFace = false
  Placement = pos=(166.25,-38,0) rot=(0,0,1;0rad)
  Points = (2) [(0,0,0),(0,-19,0)]
  Start = (166.25,-38,0)
  Subdivisions = 0
FEATURE [Part::Part2DObjectPython] Line832  # Draft 2D object (typed FeaturePython)
  ChamferSize = 0
  Closed = false
  End = (163.75,-41,0)
  FilletRadius = 0
  Length = 13
  MakeFace = false
  Placement = pos=(163.75,-54,0) rot=(0,0,1;0rad)
  Points = (2) [(0,0,0),(0,13,0)]
  Start = (163.75,-54,0)
  Subdivisions = 0
FEATURE [Part::Part2DObjectPython] Arc426  # Draft 2D object (typed FeaturePython)
  FirstAngle = -90
  LastAngle = 0
  MakeFace = false
  Placement = pos=(163.25,-54,0) rot=(0,0,1;0rad)
  Radius = 0.5
FEATURE [Part::Part2DObjectPython] Arc427  # Draft 2D object (typed FeaturePython)
  FirstAngle = 0
  LastAngle = 90
  MakeFace = false
  Placement = pos=(163.25,-41,0) rot=(0,0,1;0rad)
  Radius = 0.5
FEATURE [Part::Part2DObjectPython] Line833  # Draft 2D object (typed FeaturePython)
  ChamferSize = 0
  Closed = false
  End = (166.25,-38,0)
  FilletRadius = 0
  Length = 19
  MakeFace = false
  Placement = pos=(147.25,-38,0) rot=(0,0,1;0rad)
  Points = (2) [(0,0,0),(19,0,0)]
  Start = (147.25,-38,0)
  Subdivisions = 0
FEATURE [Part::Part2DObjectPython] Line834  # Draft 2D object (typed FeaturePython)
  ChamferSize = 0
  Closed = false
  End = (163.25,-40.5,0)
  FilletRadius = 0
  Length = 13
  MakeFace = false
  Placement = pos=(150.25,-40.5,0) rot=(0,0,1;0rad)
  Points = (2) [(0,0,0),(13,0,0)]
  Start = (150.25,-40.5,0)
  Subdivisions = 0
FEATURE [Part::Part2DObjectPython] Arc428  # Draft 2D object (typed FeaturePython)
  FirstAngle = 180
  LastAngle = 270
  MakeFace = false
  Placement = pos=(150.25,-54,0) rot=(0,0,1;0rad)
  Radius = 0.5
FEATURE [Part::Part2DObjectPython] Line835  # Draft 2D object (typed FeaturePython)
  ChamferSize = 0
  Closed = false
  End = (201.75,-41,0)
  FilletRadius = 0
  Length = 13
  MakeFace = false
  Placement = pos=(201.75,-54,0) rot=(0,0,1;0rad)
  Points = (2) [(0,0,0),(0,13,0)]
  Start = (201.75,-54,0)
  Subdivisions = 0
FEATURE [Part::Part2DObjectPython] Line836  # Draft 2D object (typed FeaturePython)
  ChamferSize = 0
  Closed = false
  End = (187.75,-54,0)
  FilletRadius = 0
  Length = 13
  MakeFace = false
  Placement = pos=(187.75,-41,0) rot=(0,0,1;0rad)
  Points = (2) [(0,0,0),(0,-13,0)]
  Start = (187.75,-41,0)
  Subdivisions = 0
FEATURE [Part::Part2DObjectPython] Line837  # Draft 2D object (typed FeaturePython)
  ChamferSize = 0
  Closed = false
  End = (204.25,-57,0)
  FilletRadius = 0
  Length = 19
  MakeFace = false
  Placement = pos=(204.25,-38,0) rot=(0,0,1;0rad)
  Points = (2) [(0,0,0),(0,-19,0)]
  Start = (204.25,-38,0)
  Subdivisions = 0
FEATURE [Part::Part2DObjectPython] Line838  # Draft 2D object (typed FeaturePython)
  ChamferSize = 0
  Closed = false
  End = (147.25,-57,0)
  FilletRadius = 0
  Length = 19
  MakeFace = false
  Placement = pos=(166.25,-57,0) rot=(0,0,1;0rad)
  Points = (2) [(0,0,0),(-19,0,0)]
  Start = (166.25,-57,0)
  Subdivisions = 0
FEATURE [Part::Part2DObjectPython] Line839  # Draft 2D object (typed FeaturePython)
  ChamferSize = 0
  Closed = false
  End = (182.75,-41,0)
  FilletRadius = 0
  Length = 13
  MakeFace = false
  Placement = pos=(182.75,-54,0) rot=(0,0,1;0rad)
  Points = (2) [(0,0,0),(0,13,0)]
  Start = (182.75,-54,0)
  Subdivisions = 0
FEATURE [Part::Part2DObjectPython] Arc429  # Draft 2D object (typed FeaturePython)
  FirstAngle = -90
  LastAngle = 0
  MakeFace = false
  Placement = pos=(182.25,-54,0) rot=(0,0,1;0rad)
  Radius = 0.5
FEATURE [Part::Part2DObjectPython] Line840  # Draft 2D object (typed FeaturePython)
  ChamferSize = 0
  Closed = false
  End = (185.25,-57,0)
  FilletRadius = 0
  Length = 19
  MakeFace = false
  Placement = pos=(185.25,-38,0) rot=(0,0,1;0rad)
  Points = (2) [(0,0,0),(0,-19,0)]
  Start = (185.25,-38,0)
  Subdivisions = 0
FEATURE [Part::Part2DObjectPython] Arc430  # Draft 2D object (typed FeaturePython)
  FirstAngle = 90
  LastAngle = 180
  MakeFace = false
  Placement = pos=(150.25,-41,0) rot=(0,0,1;0rad)
  Radius = 0.5
FEATURE [Part::Part2DObjectPython] Line841  # Draft 2D object (typed FeaturePython)
  ChamferSize = 0
  Closed = false
  End = (168.75,-54,0)
  FilletRadius = 0
  Length = 13
  MakeFace = false
  Placement = pos=(168.75,-41,0) rot=(0,0,1;0rad)
  Points = (2) [(0,0,0),(0,-13,0)]
  Start = (168.75,-41,0)
  Subdivisions = 0
FEATURE [Part::Part2DObjectPython] Line842  # Draft 2D object (typed FeaturePython)
  ChamferSize = 0
  Closed = false
  End = (182.25,-40.5,0)
  FilletRadius = 0
  Length = 13
  MakeFace = false
  Placement = pos=(169.25,-40.5,0) rot=(0,0,1;0rad)
  Points = (2) [(0,0,0),(13,0,0)]
  Start = (169.25,-40.5,0)
  Subdivisions = 0
FEATURE [Part::Part2DObjectPython] Line843  # Draft 2D object (typed FeaturePython)
  ChamferSize = 0
  Closed = false
  End = (182.25,-54.5,0)
  FilletRadius = 0
  Length = 13
  MakeFace = false
  Placement = pos=(169.25,-54.5,0) rot=(0,0,1;0rad)
  Points = (2) [(0,0,0),(13,0,0)]
  Start = (169.25,-54.5,0)
  Subdivisions = 0
FEATURE [Part::Part2DObjectPython] Line844  # Draft 2D object (typed FeaturePython)
  ChamferSize = 0
  Closed = false
  End = (201.25,-40.5,0)
  FilletRadius = 0
  Length = 13
  MakeFace = false
  Placement = pos=(188.25,-40.5,0) rot=(0,0,1;0rad)
  Points = (2) [(0,0,0),(13,0,0)]
  Start = (188.25,-40.5,0)
  Subdivisions = 0
FEATURE [Part::Part2DObjectPython] Line845  # Draft 2D object (typed FeaturePython)
  ChamferSize = 0
  Closed = false
  End = (163.25,-54.5,0)
  FilletRadius = 0
  Length = 13
  MakeFace = false
  Placement = pos=(150.25,-54.5,0) rot=(0,0,1;0rad)
  Points = (2) [(0,0,0),(13,0,0)]
  Start = (150.25,-54.5,0)
  Subdivisions = 0
FEATURE [Part::Part2DObjectPython] Arc431  # Draft 2D object (typed FeaturePython)
  FirstAngle = 0
  LastAngle = 90
  MakeFace = false
  Placement = pos=(182.25,-41,0) rot=(0,0,1;0rad)
  Radius = 0.5
FEATURE [Part::Part2DObjectPython] Arc432  # Draft 2D object (typed FeaturePython)
  FirstAngle = 90
  LastAngle = 180
  MakeFace = false
  Placement = pos=(169.25,-41,0) rot=(0,0,1;0rad)
  Radius = 0.5
FEATURE [Part::Part2DObjectPython] Line846  # Draft 2D object (typed FeaturePython)
  ChamferSize = 0
  Closed = false
  End = (201.25,-54.5,0)
  FilletRadius = 0
  Length = 13
  MakeFace = false
  Placement = pos=(188.25,-54.5,0) rot=(0,0,1;0rad)
  Points = (2) [(0,0,0),(13,0,0)]
  Start = (188.25,-54.5,0)
  Subdivisions = 0
FEATURE [Part::Part2DObjectPython] Arc433  # Draft 2D object (typed FeaturePython)
  FirstAngle = 90
  LastAngle = 180
  MakeFace = false
  Placement = pos=(188.25,-41,0) rot=(0,0,1;0rad)
  Radius = 0.5
FEATURE [Part::Part2DObjectPython] Arc434  # Draft 2D object (typed FeaturePython)
  FirstAngle = 180
  LastAngle = 270
  MakeFace = false
  Placement = pos=(188.25,-54,0) rot=(0,0,1;0rad)
  Radius = 0.5
FEATURE [Part::Part2DObjectPython] Arc435  # Draft 2D object (typed FeaturePython)
  FirstAngle = -90
  LastAngle = 0
  MakeFace = false
  Placement = pos=(201.25,-54,0) rot=(0,0,1;0rad)
  Radius = 0.5
FEATURE [Part::Part2DObjectPython] Line847  # Draft 2D object (typed FeaturePython)
  ChamferSize = 0
  Closed = false
  End = (147.25,-57,0)
  FilletRadius = 0
  Length = 19
  MakeFace = false
  Placement = pos=(147.25,-38,0) rot=(0,0,1;0rad)
  Points = (2) [(0,0,0),(0,-19,0)]
  Start = (147.25,-38,0)
  Subdivisions = 0
FEATURE [Part::Part2DObjectPython] Arc436  # Draft 2D object (typed FeaturePython)
  FirstAngle = 0
  LastAngle = 90
  MakeFace = false
  Placement = pos=(201.25,-41,0) rot=(0,0,1;0rad)
  Radius = 0.5
FEATURE [Part::Part2DObjectPython] Arc437  # Draft 2D object (typed FeaturePython)
  FirstAngle = 180
  LastAngle = 270
  MakeFace = false
  Placement = pos=(169.25,-54,0) rot=(0,0,1;0rad)
  Radius = 0.5
FEATURE [Part::Part2DObjectPython] Line848  # Draft 2D object (typed FeaturePython)
  ChamferSize = 0
  Closed = false
  End = (166.25,-57,0)
  FilletRadius = 0
  Length = 19
  MakeFace = false
  Placement = pos=(185.25,-57,0) rot=(0,0,1;0rad)
  Points = (2) [(0,0,0),(-19,0,0)]
  Start = (185.25,-57,0)
  Subdivisions = 0
FEATURE [Part::Part2DObjectPython] Line849  # Draft 2D object (typed FeaturePython)
  ChamferSize = 0
  Closed = false
  End = (166.25,-57,0)
  FilletRadius = 0
  Length = 19
  MakeFace = false
  Placement = pos=(166.25,-38,0) rot=(0,0,1;0rad)
  Points = (2) [(0,0,0),(0,-19,0)]
  Start = (166.25,-38,0)
  Subdivisions = 0
FEATURE [Part::Part2DObjectPython] Line850  # Draft 2D object (typed FeaturePython)
  ChamferSize = 0
  Closed = false
  End = (185.25,-38,0)
  FilletRadius = 0
  Length = 19
  MakeFace = false
  Placement = pos=(166.25,-38,0) rot=(0,0,1;0rad)
  Points = (2) [(0,0,0),(19,0,0)]
  Start = (166.25,-38,0)
  Subdivisions = 0
FEATURE [Part::Part2DObjectPython] Line851  # Draft 2D object (typed FeaturePython)
  ChamferSize = 0
  Closed = false
  End = (223.25,-57,0)
  FilletRadius = 0
  Length = 19
  MakeFace = false
  Placement = pos=(223.25,-38,0) rot=(0,0,1;0rad)
  Points = (2) [(0,0,0),(0,-19,0)]
  Start = (223.25,-38,0)
  Subdivisions = 0
FEATURE [Part::Part2DObjectPython] Arc438  # Draft 2D object (typed FeaturePython)
  FirstAngle = -90
  LastAngle = 0
  MakeFace = false
  Placement = pos=(241.625,-54,0) rot=(0,0,1;0rad)
  Radius = 0.5
FEATURE [Part::Part2DObjectPython] Arc439  # Draft 2D object (typed FeaturePython)
  FirstAngle = -90
  LastAngle = 0
  MakeFace = false
  Placement = pos=(220.25,-54,0) rot=(0,0,1;0rad)
  Radius = 0.5
FEATURE [Part::Part2DObjectPython] Line852  # Draft 2D object (typed FeaturePython)
  ChamferSize = 0
  Closed = false
  End = (247,-38,0)
  FilletRadius = 0
  Length = 19
  MakeFace = false
  Placement = pos=(247,-57,0) rot=(0,0,1;0rad)
  Points = (2) [(0,0,0),(0,19,0)]
  Start = (247,-57,0)
  Subdivisions = 0
FEATURE [Part::Part2DObjectPython] Arc440  # Draft 2D object (typed FeaturePython)
  FirstAngle = 180
  LastAngle = 270
  MakeFace = false
  Placement = pos=(231,-54,0) rot=(0,0,1;0rad)
  Radius = 0.5
FEATURE [Part::Part2DObjectPython] Arc441  # Draft 2D object (typed FeaturePython)
  FirstAngle = -90
  LastAngle = 0
  MakeFace = false
  Placement = pos=(222.625,-54,0) rot=(0,0,1;0rad)
  Radius = 0.5
FEATURE [Part::Part2DObjectPython] Arc442  # Draft 2D object (typed FeaturePython)
  FirstAngle = 180
  LastAngle = 270
  MakeFace = false
  Placement = pos=(207.25,-54,0) rot=(0,0,1;0rad)
  Radius = 0.5
FEATURE [Part::Part2DObjectPython] Line853  # Draft 2D object (typed FeaturePython)
  ChamferSize = 0
  Closed = false
  End = (220.75,-41,0)
  FilletRadius = 0
  Length = 13
  MakeFace = false
  Placement = pos=(220.75,-54,0) rot=(0,0,1;0rad)
  Points = (2) [(0,0,0),(0,13,0)]
  Start = (220.75,-54,0)
  Subdivisions = 0
FEATURE [Part::Part2DObjectPython] Arc443  # Draft 2D object (typed FeaturePython)
  FirstAngle = 180
  LastAngle = 270
  MakeFace = false
  Placement = pos=(228.625,-54,0) rot=(0,0,1;0rad)
  Radius = 0.5
FEATURE [Part::Part2DObjectPython] Line854  # Draft 2D object (typed FeaturePython)
  ChamferSize = 0
  Closed = false
  End = (220.25,-54.5,0)
  FilletRadius = 0
  Length = 13
  MakeFace = false
  Placement = pos=(207.25,-54.5,0) rot=(0,0,1;0rad)
  Points = (2) [(0,0,0),(13,0,0)]
  Start = (207.25,-54.5,0)
  Subdivisions = 0
FEATURE [Part::Part2DObjectPython] Line855  # Draft 2D object (typed FeaturePython)
  ChamferSize = 0
  Closed = false
  End = (206.75,-54,0)
  FilletRadius = 0
  Length = 13
  MakeFace = false
  Placement = pos=(206.75,-41,0) rot=(0,0,1;0rad)
  Points = (2) [(0,0,0),(0,-13,0)]
  Start = (206.75,-41,0)
  Subdivisions = 0
FEATURE [Part::Part2DObjectPython] Line856  # Draft 2D object (typed FeaturePython)
  ChamferSize = 0
  Closed = false
  End = (204.25,-57,0)
  FilletRadius = 0
  Length = 19
  MakeFace = false
  Placement = pos=(204.25,-38,0) rot=(0,0,1;0rad)
  Points = (2) [(0,0,0),(0,-19,0)]
  Start = (204.25,-38,0)
  Subdivisions = 0
FEATURE [Part::Part2DObjectPython] Arc444  # Draft 2D object (typed FeaturePython)
  FirstAngle = 0
  LastAngle = 90
  MakeFace = false
  Placement = pos=(241.625,-41,0) rot=(0,0,1;0rad)
  Radius = 0.5
FEATURE [Part::Part2DObjectPython] Line857  # Draft 2D object (typed FeaturePython)
  ChamferSize = 0
  Closed = false
  End = (228.125,-54,0)
  FilletRadius = 0
  Length = 13
  MakeFace = false
  Placement = pos=(228.125,-41,0) rot=(0,0,1;0rad)
  Points = (2) [(0,0,0),(0,-13,0)]
  Start = (228.125,-41,0)
  Subdivisions = 0
FEATURE [Part::Part2DObjectPython] Line858  # Draft 2D object (typed FeaturePython)
  ChamferSize = 0
  Closed = false
  End = (241.625,-40.5,0)
  FilletRadius = 0
  Length = 13
  MakeFace = false
  Placement = pos=(228.625,-40.5,0) rot=(0,0,1;0rad)
  Points = (2) [(0,0,0),(13,0,0)]
  Start = (228.625,-40.5,0)
  Subdivisions = 0
FEATURE [Part::Part2DObjectPython] Line859  # Draft 2D object (typed FeaturePython)
  ChamferSize = 0
  Closed = false
  End = (241.625,-54.5,0)
  FilletRadius = 0
  Length = 13
  MakeFace = false
  Placement = pos=(228.625,-54.5,0) rot=(0,0,1;0rad)
  Points = (2) [(0,0,0),(13,0,0)]
  Start = (228.625,-54.5,0)
  Subdivisions = 0
FEATURE [Part::Part2DObjectPython] Line860  # Draft 2D object (typed FeaturePython)
  ChamferSize = 0
  Closed = false
  End = (242.125,-41,0)
  FilletRadius = 0
  Length = 13
  MakeFace = false
  Placement = pos=(242.125,-54,0) rot=(0,0,1;0rad)
  Points = (2) [(0,0,0),(0,13,0)]
  Start = (242.125,-54,0)
  Subdivisions = 0
FEATURE [Part::Part2DObjectPython] Line861  # Draft 2D object (typed FeaturePython)
  ChamferSize = 0
  Closed = false
  End = (204.25,-57,0)
  FilletRadius = 0
  Length = 19
  MakeFace = false
  Placement = pos=(223.25,-57,0) rot=(0,0,1;0rad)
  Points = (2) [(0,0,0),(-19,0,0)]
  Start = (223.25,-57,0)
  Subdivisions = 0
FEATURE [Part::Part2DObjectPython] Arc445  # Draft 2D object (typed FeaturePython)
  FirstAngle = 0
  LastAngle = 90
  MakeFace = false
  Placement = pos=(220.25,-41,0) rot=(0,0,1;0rad)
  Radius = 0.5
FEATURE [Part::Part2DObjectPython] Line862  # Draft 2D object (typed FeaturePython)
  ChamferSize = 0
  Closed = false
  End = (185.25,-57,0)
  FilletRadius = 0
  Length = 19
  MakeFace = false
  Placement = pos=(204.25,-57,0) rot=(0,0,1;0rad)
  Points = (2) [(0,0,0),(-19,0,0)]
  Start = (204.25,-57,0)
  Subdivisions = 0
FEATURE [Part::Part2DObjectPython] Line863  # Draft 2D object (typed FeaturePython)
  ChamferSize = 0
  Closed = false
  End = (204.25,-38,0)
  FilletRadius = 0
  Length = 19
  MakeFace = false
  Placement = pos=(185.25,-38,0) rot=(0,0,1;0rad)
  Points = (2) [(0,0,0),(19,0,0)]
  Start = (185.25,-38,0)
  Subdivisions = 0
FEATURE [Part::Part2DObjectPython] Line864  # Draft 2D object (typed FeaturePython)
  ChamferSize = 0
  Closed = false
  End = (223.25,-38,0)
  FilletRadius = 0
  Length = 19
  MakeFace = false
  Placement = pos=(204.25,-38,0) rot=(0,0,1;0rad)
  Points = (2) [(0,0,0),(19,0,0)]
  Start = (204.25,-38,0)
  Subdivisions = 0
FEATURE [Part::Part2DObjectPython] Line865  # Draft 2D object (typed FeaturePython)
  ChamferSize = 0
  Closed = false
  End = (247,-38,0)
  FilletRadius = 0
  Length = 23.75
  MakeFace = false
  Placement = pos=(223.25,-38,0) rot=(0,0,1;0rad)
  Points = (2) [(0,0,0),(23.75,0,0)]
  Start = (223.25,-38,0)
  Subdivisions = 0
FEATURE [Part::Part2DObjectPython] Line866  # Draft 2D object (typed FeaturePython)
  ChamferSize = 0
  Closed = false
  End = (247,-57,0)
  FilletRadius = 0
  Length = 23.75
  MakeFace = false
  Placement = pos=(223.25,-57,0) rot=(0,0,1;0rad)
  Points = (2) [(0,0,0),(23.75,0,0)]
  Start = (223.25,-57,0)
  Subdivisions = 0
FEATURE [Part::Part2DObjectPython] Arc446  # Draft 2D object (typed FeaturePython)
  FirstAngle = 90
  LastAngle = 180
  MakeFace = false
  Placement = pos=(207.25,-41,0) rot=(0,0,1;0rad)
  Radius = 0.5
FEATURE [Part::Part2DObjectPython] Line867  # Draft 2D object (typed FeaturePython)
  ChamferSize = 0
  Closed = false
  End = (185.25,-57,0)
  FilletRadius = 0
  Length = 19
  MakeFace = false
  Placement = pos=(185.25,-38,0) rot=(0,0,1;0rad)
  Points = (2) [(0,0,0),(0,-19,0)]
  Start = (185.25,-38,0)
  Subdivisions = 0
FEATURE [Part::Part2DObjectPython] Line868  # Draft 2D object (typed FeaturePython)
  ChamferSize = 0
  Closed = false
  End = (223.25,-57,0)
  FilletRadius = 0
  Length = 19
  MakeFace = false
  Placement = pos=(223.25,-38,0) rot=(0,0,1;0rad)
  Points = (2) [(0,0,0),(0,-19,0)]
  Start = (223.25,-38,0)
  Subdivisions = 0
FEATURE [Part::Part2DObjectPython] Line869  # Draft 2D object (typed FeaturePython)
  ChamferSize = 0
  Closed = false
  End = (220.25,-40.5,0)
  FilletRadius = 0
  Length = 13
  MakeFace = false
  Placement = pos=(207.25,-40.5,0) rot=(0,0,1;0rad)
  Points = (2) [(0,0,0),(13,0,0)]
  Start = (207.25,-40.5,0)
  Subdivisions = 0
FEATURE [Part::Part2DObjectPython] Arc447  # Draft 2D object (typed FeaturePython)
  FirstAngle = 90
  LastAngle = 180
  MakeFace = false
  Placement = pos=(228.625,-41,0) rot=(0,0,1;0rad)
  Radius = 0.5
FEATURE [Part::Part2DObjectPython] Line870  # Draft 2D object (typed FeaturePython)
  ChamferSize = 0
  Closed = false
  End = (204.25,-57,0)
  FilletRadius = 0
  Length = 19
  MakeFace = false
  Placement = pos=(204.25,-38,0) rot=(0,0,1;0rad)
  Points = (2) [(0,0,0),(0,-19,0)]
  Start = (204.25,-38,0)
  Subdivisions = 0
FEATURE [Part::Part2DObjectPython] Arc448  # Draft 2D object (typed FeaturePython)
  FirstAngle = -90
  LastAngle = 0
  MakeFace = false
  Placement = pos=(244,-54,0) rot=(0,0,1;0rad)
  Radius = 0.5
FEATURE [Part::Part2DObjectPython] Line871  # Draft 2D object (typed FeaturePython)
  ChamferSize = 0
  Closed = false
  End = (228,-38,0)
  FilletRadius = 0
  Length = 19
  MakeFace = false
  Placement = pos=(228,-57,0) rot=(0,0,1;0rad)
  Points = (2) [(0,0,0),(0,19,0)]
  Start = (228,-57,0)
  Subdivisions = 0
FEATURE [Part::Part2DObjectPython] Line872  # Draft 2D object (typed FeaturePython)
  ChamferSize = 0
  Closed = false
  End = (209,3.6e-15,0)
  FilletRadius = 0
  Length = 19
  MakeFace = false
  Placement = pos=(209,-19,0) rot=(0,0,1;3.14159rad)
  Points = (2) [(0,0,0),(0,-19,0)]
  Start = (209,-19,0)
  Subdivisions = 0
FEATURE [Part::Part2DObjectPython] Line873  # Draft 2D object (typed FeaturePython)
  ChamferSize = 0
  Closed = false
  End = (247,-38,0)
  FilletRadius = 0
  Length = 19
  MakeFace = false
  Placement = pos=(228,-38,0) rot=(0,0,1;0rad)
  Points = (2) [(0,0,0),(19,0,0)]
  Start = (228,-38,0)
  Subdivisions = 0
FEATURE [Part::Part2DObjectPython] Arc449  # Draft 2D object (typed FeaturePython)
  FirstAngle = 180
  LastAngle = 270
  MakeFace = false
  Placement = pos=(209.625,-54,0) rot=(0,0,1;0rad)
  Radius = 0.5
FEATURE [Part::Part2DObjectPython] Line874  # Draft 2D object (typed FeaturePython)
  ChamferSize = 0
  Closed = false
  End = (172.75,-59.5,0)
  FilletRadius = 0
  Length = 13
  MakeFace = false
  Placement = pos=(159.75,-59.5,0) rot=(0,0,1;0rad)
  Points = (2) [(0,0,0),(13,0,0)]
  Start = (159.75,-59.5,0)
  Subdivisions = 0
FEATURE [Part::Part2DObjectPython] Line875  # Draft 2D object (typed FeaturePython)
  ChamferSize = 0
  Closed = false
  End = (230.5,-54,0)
  FilletRadius = 0
  Length = 13
  MakeFace = false
  Placement = pos=(230.5,-41,0) rot=(0,0,1;0rad)
  Points = (2) [(0,0,0),(0,-13,0)]
  Start = (230.5,-41,0)
  Subdivisions = 0
FEATURE [Part::Part2DObjectPython] Line876  # Draft 2D object (typed FeaturePython)
  ChamferSize = 0
  Closed = false
  End = (228,-38,0)
  FilletRadius = 0
  Length = 23.75
  MakeFace = false
  Placement = pos=(204.25,-38,0) rot=(0,0,1;0rad)
  Points = (2) [(0,0,0),(23.75,0,0)]
  Start = (204.25,-38,0)
  Subdivisions = 0
FEATURE [Part::Part2DObjectPython] Arc450  # Draft 2D object (typed FeaturePython)
  FirstAngle = 90
  LastAngle = 180
  MakeFace = false
  Placement = pos=(209.625,-41,0) rot=(0,0,1;0rad)
  Radius = 0.5
FEATURE [Part::Part2DObjectPython] Line877  # Draft 2D object (typed FeaturePython)
  ChamferSize = 0
  Closed = false
  End = (209,-19,0)
  FilletRadius = 0
  Length = 38
  MakeFace = false
  Placement = pos=(247,-19,0) rot=(0,0,1;3.14159rad)
  Points = (2) [(0,0,0),(38,1.06581e-14,0)]
  Start = (247,-19,0)
  Subdivisions = 0
FEATURE [Part::Part2DObjectPython] Line878  # Draft 2D object (typed FeaturePython)
  ChamferSize = 0
  Closed = false
  End = (209,-4e-15,0)
  FilletRadius = 0
  Length = 38
  MakeFace = false
  Placement = pos=(247,-4e-15,0) rot=(0,0,1;3.14159rad)
  Points = (2) [(0,0,0),(38,0,0)]
  Start = (247,-4e-15,0)
  Subdivisions = 0
FEATURE [Part::Part2DObjectPython] Line879  # Draft 2D object (typed FeaturePython)
  ChamferSize = 0
  Closed = false
  End = (244.5,-41,0)
  FilletRadius = 0
  Length = 13
  MakeFace = false
  Placement = pos=(244.5,-54,0) rot=(0,0,1;0rad)
  Points = (2) [(0,0,0),(0,13,0)]
  Start = (244.5,-54,0)
  Subdivisions = 0
FEATURE [Part::Part2DObjectPython] Line880  # Draft 2D object (typed FeaturePython)
  ChamferSize = 0
  Closed = false
  End = (244,-54.5,0)
  FilletRadius = 0
  Length = 13
  MakeFace = false
  Placement = pos=(231,-54.5,0) rot=(0,0,1;0rad)
  Points = (2) [(0,0,0),(13,0,0)]
  Start = (231,-54.5,0)
  Subdivisions = 0
FEATURE [Part::Part2DObjectPython] Line881  # Draft 2D object (typed FeaturePython)
  ChamferSize = 0
  Closed = false
  End = (247,-3.6e-15,0)
  FilletRadius = 0
  Length = 19
  MakeFace = false
  Placement = pos=(247,-19,0) rot=(0,0,1;3.14159rad)
  Points = (2) [(0,0,0),(0,-19,0)]
  Start = (247,-19,0)
  Subdivisions = 0
FEATURE [Part::Part2DObjectPython] Line882  # Draft 2D object (typed FeaturePython)
  ChamferSize = 0
  Closed = false
  End = (175.75,-76,0)
  FilletRadius = 0
  Length = 19
  MakeFace = false
  Placement = pos=(175.75,-57,0) rot=(0,0,1;0rad)
  Points = (2) [(0,0,0),(0,-19,0)]
  Start = (175.75,-57,0)
  Subdivisions = 0
FEATURE [Part::Part2DObjectPython] Arc451  # Draft 2D object (typed FeaturePython)
  FirstAngle = 0
  LastAngle = 90
  MakeFace = false
  Placement = pos=(222.625,-41,0) rot=(0,0,1;0rad)
  Radius = 0.5
FEATURE [Part::Part2DObjectPython] Line883  # Draft 2D object (typed FeaturePython)
  ChamferSize = 0
  Closed = false
  End = (209.125,-54,0)
  FilletRadius = 0
  Length = 13
  MakeFace = false
  Placement = pos=(209.125,-41,0) rot=(0,0,1;0rad)
  Points = (2) [(0,0,0),(0,-13,0)]
  Start = (209.125,-41,0)
  Subdivisions = 0
FEATURE [Part::Part2DObjectPython] Line884  # Draft 2D object (typed FeaturePython)
  ChamferSize = 0
  Closed = false
  End = (228,-57,0)
  FilletRadius = 0
  Length = 19
  MakeFace = false
  Placement = pos=(247,-57,0) rot=(0,0,1;0rad)
  Points = (2) [(0,0,0),(-19,0,0)]
  Start = (247,-57,0)
  Subdivisions = 0
FEATURE [Part::Part2DObjectPython] Line885  # Draft 2D object (typed FeaturePython)
  ChamferSize = 0
  Closed = false
  End = (228,-57,0)
  FilletRadius = 0
  Length = 19
  MakeFace = false
  Placement = pos=(228,-38,0) rot=(0,0,1;0rad)
  Points = (2) [(0,0,0),(0,-19,0)]
  Start = (228,-38,0)
  Subdivisions = 0
FEATURE [Part::Part2DObjectPython] Line886  # Draft 2D object (typed FeaturePython)
  ChamferSize = 0
  Closed = false
  End = (222.625,-54.5,0)
  FilletRadius = 0
  Length = 13
  MakeFace = false
  Placement = pos=(209.625,-54.5,0) rot=(0,0,1;0rad)
  Points = (2) [(0,0,0),(13,0,0)]
  Start = (209.625,-54.5,0)
  Subdivisions = 0
FEATURE [Part::Part2DObjectPython] Line887  # Draft 2D object (typed FeaturePython)
  ChamferSize = 0
  Closed = false
  End = (247,-57,0)
  FilletRadius = 0
  Length = 19
  MakeFace = false
  Placement = pos=(247,-38,0) rot=(0,0,1;0rad)
  Points = (2) [(0,0,0),(0,-19,0)]
  Start = (247,-38,0)
  Subdivisions = 0
FEATURE [Part::Part2DObjectPython] Line888  # Draft 2D object (typed FeaturePython)
  ChamferSize = 0
  Closed = false
  End = (222.625,-40.5,0)
  FilletRadius = 0
  Length = 13
  MakeFace = false
  Placement = pos=(209.625,-40.5,0) rot=(0,0,1;0rad)
  Points = (2) [(0,0,0),(13,0,0)]
  Start = (209.625,-40.5,0)
  Subdivisions = 0
FEATURE [Part::Part2DObjectPython] Line889  # Draft 2D object (typed FeaturePython)
  ChamferSize = 0
  Closed = false
  End = (223.125,-41,0)
  FilletRadius = 0
  Length = 13
  MakeFace = false
  Placement = pos=(223.125,-54,0) rot=(0,0,1;0rad)
  Points = (2) [(0,0,0),(0,13,0)]
  Start = (223.125,-54,0)
  Subdivisions = 0
FEATURE [Part::Part2DObjectPython] Line890  # Draft 2D object (typed FeaturePython)
  ChamferSize = 0
  Closed = false
  End = (244,-40.5,0)
  FilletRadius = 0
  Length = 13
  MakeFace = false
  Placement = pos=(231,-40.5,0) rot=(0,0,1;0rad)
  Points = (2) [(0,0,0),(13,0,0)]
  Start = (231,-40.5,0)
  Subdivisions = 0
FEATURE [Part::Part2DObjectPython] Line891  # Draft 2D object (typed FeaturePython)
  ChamferSize = 0
  Closed = false
  End = (228,-57,0)
  FilletRadius = 0
  Length = 23.75
  MakeFace = false
  Placement = pos=(204.25,-57,0) rot=(0,0,1;0rad)
  Points = (2) [(0,0,0),(23.75,0,0)]
  Start = (204.25,-57,0)
  Subdivisions = 0
FEATURE [Part::Part2DObjectPython] Arc452  # Draft 2D object (typed FeaturePython)
  FirstAngle = 0
  LastAngle = 90
  MakeFace = false
  Placement = pos=(244,-41,0) rot=(0,0,1;0rad)
  Radius = 0.5
FEATURE [Part::Part2DObjectPython] Arc453  # Draft 2D object (typed FeaturePython)
  FirstAngle = 90
  LastAngle = 180
  MakeFace = false
  Placement = pos=(231,-41,0) rot=(0,0,1;0rad)
  Radius = 0.5
FEATURE [Part::Part2DObjectPython] Line892  # Draft 2D object (typed FeaturePython)
  ChamferSize = 0
  Closed = false
  End = (243.188,-20,0)
  FilletRadius = 0
  Length = 30.376
  MakeFace = false
  Placement = pos=(212.812,-20,0) rot=(0,0,1;3.14159rad)
  Points = (2) [(0,0,0),(-30.376,0,0)]
  Start = (212.812,-20,0)
  Subdivisions = 0
FEATURE [Part::Part2DObjectPython] Line893  # Draft 2D object (typed FeaturePython)
  ChamferSize = 0
  Closed = false
  End = (175.75,-57,0)
  FilletRadius = 0
  Length = 19
  MakeFace = false
  Placement = pos=(156.75,-57,0) rot=(0,0,1;0rad)
  Points = (2) [(0,0,0),(19,0,0)]
  Start = (156.75,-57,0)
  Subdivisions = 0
FEATURE [Part::Part2DObjectPython] Line894  # Draft 2D object (typed FeaturePython)
  ChamferSize = 0
  Closed = false
  End = (156.75,-76,0)
  FilletRadius = 0
  Length = 19
  MakeFace = false
  Placement = pos=(175.75,-76,0) rot=(0,0,1;0rad)
  Points = (2) [(0,0,0),(-19,0,0)]
  Start = (175.75,-76,0)
  Subdivisions = 0
FEATURE [Part::Part2DObjectPython] Line895  # Draft 2D object (typed FeaturePython)
  ChamferSize = 0
  Closed = false
  End = (236.188,-2,0)
  FilletRadius = 0
  Length = 1.7
  MakeFace = false
  Placement = pos=(236.188,-0.3,0) rot=(0,0,1;3.14159rad)
  Points = (2) [(0,0,0),(0,1.7,0)]
  Start = (236.188,-0.3,0)
  Subdivisions = 0
FEATURE [Part::Part2DObjectPython] Line896  # Draft 2D object (typed FeaturePython)
  ChamferSize = 0
  Closed = false
  End = (220.312,-2.5,0)
  FilletRadius = 0
  Length = 15.376
  MakeFace = false
  Placement = pos=(235.688,-2.5,0) rot=(0,0,1;3.14159rad)
  Points = (2) [(0,0,0),(15.376,0,0)]
  Start = (235.688,-2.5,0)
  Subdivisions = 0
FEATURE [Part::Part2DObjectPython] Line897  # Draft 2D object (typed FeaturePython)
  ChamferSize = 0
  Closed = false
  End = (0,-76,0)
  FilletRadius = 0
  Length = 19
  MakeFace = false
  Placement = pos=(0,-57,0) rot=(0,0,1;0rad)
  Points = (2) [(0,0,0),(0,-19,0)]
  Start = (0,-57,0)
  Subdivisions = 0
FEATURE [Part::Part2DObjectPython] Line898  # Draft 2D object (typed FeaturePython)
  ChamferSize = 0
  Closed = false
  End = (236.688,0.2,0)
  FilletRadius = 0
  Length = 6.5
  MakeFace = false
  Placement = pos=(243.188,0.2,0) rot=(0,0,1;3.14159rad)
  Points = (2) [(0,0,0),(6.5,0,0)]
  Start = (243.188,0.2,0)
  Subdivisions = 0
FEATURE [Part::Part2DObjectPython] Arc454  # Draft 2D object (typed FeaturePython)
  FirstAngle = 0
  LastAngle = 90
  MakeFace = false
  Placement = pos=(212.812,-19.5,0) rot=(0,0,1;3.14159rad)
  Radius = 0.5
FEATURE [Part::Part2DObjectPython] Line899  # Draft 2D object (typed FeaturePython)
  ChamferSize = 0
  Closed = false
  End = (66.5,-57,0)
  FilletRadius = 0
  Length = 19
  MakeFace = false
  Placement = pos=(47.5,-57,0) rot=(0,0,1;0rad)
  Points = (2) [(0,0,0),(19,0,0)]
  Start = (47.5,-57,0)
  Subdivisions = 0
FEATURE [Part::Part2DObjectPython] Arc455  # Draft 2D object (typed FeaturePython)
  FirstAngle = 90
  LastAngle = 180
  MakeFace = false
  Placement = pos=(5.375,-60,0) rot=(0,0,1;0rad)
  Radius = 0.5
FEATURE [Part::Part2DObjectPython] Line900  # Draft 2D object (typed FeaturePython)
  ChamferSize = 0
  Closed = false
  End = (109.125,-60,0)
  FilletRadius = 0
  Length = 13
  MakeFace = false
  Placement = pos=(109.125,-73,0) rot=(0,0,1;0rad)
  Points = (2) [(0,0,0),(0,13,0)]
  Start = (109.125,-73,0)
  Subdivisions = 0
FEATURE [Part::Part2DObjectPython] Line901  # Draft 2D object (typed FeaturePython)
  ChamferSize = 0
  Closed = false
  End = (108.625,-73.5,0)
  FilletRadius = 0
  Length = 13
  MakeFace = false
  Placement = pos=(95.625,-73.5,0) rot=(0,0,1;0rad)
  Points = (2) [(0,0,0),(13,0,0)]
  Start = (95.625,-73.5,0)
  Subdivisions = 0
FEATURE [Part::Part2DObjectPython] Arc456  # Draft 2D object (typed FeaturePython)
  FirstAngle = 0
  LastAngle = 90
  MakeFace = false
  Placement = pos=(18.375,-60,0) rot=(0,0,1;0rad)
  Radius = 0.5
FEATURE [Part::Part2DObjectPython] Arc457  # Draft 2D object (typed FeaturePython)
  FirstAngle = 90
  LastAngle = 180
  MakeFace = false
  Placement = pos=(29.125,-60,0) rot=(0,0,1;0rad)
  Radius = 0.5
FEATURE [Part::Part2DObjectPython] Line902  # Draft 2D object (typed FeaturePython)
  ChamferSize = 0
  Closed = false
  End = (243.688,-0.3,0)
  FilletRadius = 0
  Length = 19.2
  MakeFace = false
  Placement = pos=(243.688,-19.5,0) rot=(0,0,1;3.14159rad)
  Points = (2) [(0,0,0),(0,-19.2,0)]
  Start = (243.688,-19.5,0)
  Subdivisions = 0
FEATURE [Part::Part2DObjectPython] Line903  # Draft 2D object (typed FeaturePython)
  ChamferSize = 0
  Closed = false
  End = (47.5,-57,0)
  FilletRadius = 0
  Length = 23.75
  MakeFace = false
  Placement = pos=(23.75,-57,0) rot=(0,0,1;0rad)
  Points = (2) [(0,0,0),(23.75,0,0)]
  Start = (23.75,-57,0)
  Subdivisions = 0
FEATURE [Part::Part2DObjectPython] Line904  # Draft 2D object (typed FeaturePython)
  ChamferSize = 0
  Closed = false
  End = (66.5,-76,0)
  FilletRadius = 0
  Length = 19
  MakeFace = false
  Placement = pos=(66.5,-57,0) rot=(0,0,1;0rad)
  Points = (2) [(0,0,0),(0,-19,0)]
  Start = (66.5,-57,0)
  Subdivisions = 0
FEATURE [Part::Part2DObjectPython] Line905  # Draft 2D object (typed FeaturePython)
  ChamferSize = 0
  Closed = false
  End = (223.25,-76,0)
  FilletRadius = 0
  Length = 23.75
  MakeFace = false
  Placement = pos=(199.5,-76,0) rot=(0,0,1;0rad)
  Points = (2) [(0,0,0),(23.75,0,0)]
  Start = (199.5,-76,0)
  Subdivisions = 0
FEATURE [Part::Part2DObjectPython] Arc458  # Draft 2D object (typed FeaturePython)
  FirstAngle = -90
  LastAngle = 0
  MakeFace = false
  Placement = pos=(212.812,-0.3,0) rot=(0,0,1;3.14159rad)
  Radius = 0.5
FEATURE [Part::Part2DObjectPython] Arc459  # Draft 2D object (typed FeaturePython)
  FirstAngle = 180
  LastAngle = 270
  MakeFace = false
  Placement = pos=(243.188,-0.3,0) rot=(0,0,1;3.14159rad)
  Radius = 0.5
FEATURE [Part::Part2DObjectPython] Line906  # Draft 2D object (typed FeaturePython)
  ChamferSize = 0
  Closed = false
  End = (212.812,0.2,0)
  FilletRadius = 0
  Length = 6.5
  MakeFace = false
  Placement = pos=(219.312,0.2,0) rot=(0,0,1;3.14159rad)
  Points = (2) [(0,0,0),(6.5,0,0)]
  Start = (219.312,0.2,0)
  Subdivisions = 0
FEATURE [Part::Part2DObjectPython] Line907  # Draft 2D object (typed FeaturePython)
  ChamferSize = 0
  Closed = false
  End = (18.875,-60,0)
  FilletRadius = 0
  Length = 13
  MakeFace = false
  Placement = pos=(18.875,-73,0) rot=(0,0,1;0rad)
  Points = (2) [(0,0,0),(0,13,0)]
  Start = (18.875,-73,0)
  Subdivisions = 0
FEATURE [Part::Part2DObjectPython] Line908  # Draft 2D object (typed FeaturePython)
  ChamferSize = 0
  Closed = false
  End = (23.75,-57,0)
  FilletRadius = 0
  Length = 23.75
  MakeFace = false
  Placement = pos=(0,-57,0) rot=(0,0,1;0rad)
  Points = (2) [(0,0,0),(23.75,0,0)]
  Start = (0,-57,0)
  Subdivisions = 0
FEATURE [Part::Part2DObjectPython] Arc460  # Draft 2D object (typed FeaturePython)
  FirstAngle = 90
  LastAngle = 180
  MakeFace = false
  Placement = pos=(235.688,-2,0) rot=(0,0,1;3.14159rad)
  Radius = 0.5
FEATURE [Part::Part2DObjectPython] Arc461  # Draft 2D object (typed FeaturePython)
  FirstAngle = 180
  LastAngle = 270
  MakeFace = false
  Placement = pos=(219.312,-0.3,0) rot=(0,0,1;3.14159rad)
  Radius = 0.5
FEATURE [Part::Part2DObjectPython] Arc462  # Draft 2D object (typed FeaturePython)
  FirstAngle = -90
  LastAngle = 0
  MakeFace = false
  Placement = pos=(236.688,-0.3,0) rot=(0,0,1;3.14159rad)
  Radius = 0.5
FEATURE [Part::Part2DObjectPython] Line909  # Draft 2D object (typed FeaturePython)
  ChamferSize = 0
  Closed = false
  End = (63.5,-59.5,0)
  FilletRadius = 0
  Length = 13
  MakeFace = false
  Placement = pos=(50.5,-59.5,0) rot=(0,0,1;0rad)
  Points = (2) [(0,0,0),(13,0,0)]
  Start = (50.5,-59.5,0)
  Subdivisions = 0
FEATURE [Part::Part2DObjectPython] Line910  # Draft 2D object (typed FeaturePython)
  ChamferSize = 0
  Closed = false
  End = (247,-76,0)
  FilletRadius = 0
  Length = 23.75
  MakeFace = false
  Placement = pos=(223.25,-76,0) rot=(0,0,1;0rad)
  Points = (2) [(0,0,0),(23.75,0,0)]
  Start = (223.25,-76,0)
  Subdivisions = 0
FEATURE [Part::Part2DObjectPython] Arc463  # Draft 2D object (typed FeaturePython)
  FirstAngle = 90
  LastAngle = 180
  MakeFace = false
  Placement = pos=(243.188,-19.5,0) rot=(0,0,1;3.14159rad)
  Radius = 0.5
FEATURE [Part::Part2DObjectPython] Arc464  # Draft 2D object (typed FeaturePython)
  FirstAngle = 0
  LastAngle = 90
  MakeFace = false
  Placement = pos=(220.312,-2,0) rot=(0,0,1;3.14159rad)
  Radius = 0.5
FEATURE [Part::Part2DObjectPython] Line911  # Draft 2D object (typed FeaturePython)
  ChamferSize = 0
  Closed = false
  End = (219.812,-0.3,0)
  FilletRadius = 0
  Length = 1.7
  MakeFace = false
  Placement = pos=(219.812,-2,0) rot=(0,0,1;3.14159rad)
  Points = (2) [(0,0,0),(0,-1.7,0)]
  Start = (219.812,-2,0)
  Subdivisions = 0
FEATURE [Part::Part2DObjectPython] Line912  # Draft 2D object (typed FeaturePython)
  ChamferSize = 0
  Closed = false
  End = (212.312,-19.5,0)
  FilletRadius = 0
  Length = 19.2
  MakeFace = false
  Placement = pos=(212.312,-0.3,0) rot=(0,0,1;0rad)
  Points = (2) [(0,0,0),(0,-19.2,0)]
  Start = (212.312,-0.3,0)
  Subdivisions = 0
FEATURE [Part::Part2DObjectPython] Line913  # Draft 2D object (typed FeaturePython)
  ChamferSize = 0
  Closed = false
  End = (47.5,-76,0)
  FilletRadius = 0
  Length = 19
  MakeFace = false
  Placement = pos=(66.5,-76,0) rot=(0,0,1;0rad)
  Points = (2) [(0,0,0),(-19,0,0)]
  Start = (66.5,-76,0)
  Subdivisions = 0
FEATURE [Part::Part2DObjectPython] Line914  # Draft 2D object (typed FeaturePython)
  ChamferSize = 0
  Closed = false
  End = (23.75,-57,0)
  FilletRadius = 0
  Length = 19
  MakeFace = false
  Placement = pos=(23.75,-76,0) rot=(0,0,1;0rad)
  Points = (2) [(0,0,0),(0,19,0)]
  Start = (23.75,-76,0)
  Subdivisions = 0
FEATURE [Part::Part2DObjectPython] Line915  # Draft 2D object (typed FeaturePython)
  ChamferSize = 0
  Closed = false
  End = (4.875,-73,0)
  FilletRadius = 0
  Length = 13
  MakeFace = false
  Placement = pos=(4.875,-60,0) rot=(0,0,1;0rad)
  Points = (2) [(0,0,0),(0,-13,0)]
  Start = (4.875,-60,0)
  Subdivisions = 0
FEATURE [Part::Part2DObjectPython] Arc465  # Draft 2D object (typed FeaturePython)
  FirstAngle = 180
  LastAngle = 270
  MakeFace = false
  Placement = pos=(5.375,-73,0) rot=(0,0,1;0rad)
  Radius = 0.5
FEATURE [Part::Part2DObjectPython] Line916  # Draft 2D object (typed FeaturePython)
  ChamferSize = 0
  Closed = false
  End = (18.375,-59.5,0)
  FilletRadius = 0
  Length = 13
  MakeFace = false
  Placement = pos=(5.375,-59.5,0) rot=(0,0,1;0rad)
  Points = (2) [(0,0,0),(13,0,0)]
  Start = (5.375,-59.5,0)
  Subdivisions = 0
FEATURE [Part::Part2DObjectPython] Line917  # Draft 2D object (typed FeaturePython)
  ChamferSize = 0
  Closed = false
  End = (18.375,-73.5,0)
  FilletRadius = 0
  Length = 13
  MakeFace = false
  Placement = pos=(5.375,-73.5,0) rot=(0,0,1;0rad)
  Points = (2) [(0,0,0),(13,0,0)]
  Start = (5.375,-73.5,0)
  Subdivisions = 0
FEATURE [Part::Part2DObjectPython] Line918  # Draft 2D object (typed FeaturePython)
  ChamferSize = 0
  Closed = false
  End = (23.75,-76,0)
  FilletRadius = 0
  Length = 23.75
  MakeFace = false
  Placement = pos=(0,-76,0) rot=(0,0,1;0rad)
  Points = (2) [(0,0,0),(23.75,0,0)]
  Start = (0,-76,0)
  Subdivisions = 0
FEATURE [Part::Part2DObjectPython] Arc466  # Draft 2D object (typed FeaturePython)
  FirstAngle = -90
  LastAngle = 0
  MakeFace = false
  Placement = pos=(18.375,-73,0) rot=(0,0,1;0rad)
  Radius = 0.5
FEATURE [Part::Part2DObjectPython] Line919  # Draft 2D object (typed FeaturePython)
  ChamferSize = 0
  Closed = false
  End = (23.75,-76,0)
  FilletRadius = 0
  Length = 19
  MakeFace = false
  Placement = pos=(23.75,-57,0) rot=(0,0,1;0rad)
  Points = (2) [(0,0,0),(0,-19,0)]
  Start = (23.75,-57,0)
  Subdivisions = 0
FEATURE [Part::Part2DObjectPython] Arc467  # Draft 2D object (typed FeaturePython)
  FirstAngle = 0
  LastAngle = 90
  MakeFace = false
  Placement = pos=(42.125,-60,0) rot=(0,0,1;0rad)
  Radius = 0.5
FEATURE [Part::Part2DObjectPython] Line920  # Draft 2D object (typed FeaturePython)
  ChamferSize = 0
  Closed = false
  End = (42.625,-60,0)
  FilletRadius = 0
  Length = 13
  MakeFace = false
  Placement = pos=(42.625,-73,0) rot=(0,0,1;0rad)
  Points = (2) [(0,0,0),(0,13,0)]
  Start = (42.625,-73,0)
  Subdivisions = 0
FEATURE [Part::Part2DObjectPython] Arc468  # Draft 2D object (typed FeaturePython)
  FirstAngle = 180
  LastAngle = 270
  MakeFace = false
  Placement = pos=(50.5,-73,0) rot=(0,0,1;0rad)
  Radius = 0.5
FEATURE [Part::Part2DObjectPython] Line921  # Draft 2D object (typed FeaturePython)
  ChamferSize = 0
  Closed = false
  End = (42.125,-73.5,0)
  FilletRadius = 0
  Length = 13
  MakeFace = false
  Placement = pos=(29.125,-73.5,0) rot=(0,0,1;0rad)
  Points = (2) [(0,0,0),(13,0,0)]
  Start = (29.125,-73.5,0)
  Subdivisions = 0
FEATURE [Part::Part2DObjectPython] Line922  # Draft 2D object (typed FeaturePython)
  ChamferSize = 0
  Closed = false
  End = (63.5,-73.5,0)
  FilletRadius = 0
  Length = 13
  MakeFace = false
  Placement = pos=(50.5,-73.5,0) rot=(0,0,1;0rad)
  Points = (2) [(0,0,0),(13,0,0)]
  Start = (50.5,-73.5,0)
  Subdivisions = 0
FEATURE [Part::Part2DObjectPython] Arc469  # Draft 2D object (typed FeaturePython)
  FirstAngle = 180
  LastAngle = 270
  MakeFace = false
  Placement = pos=(29.125,-73,0) rot=(0,0,1;0rad)
  Radius = 0.5
FEATURE [Part::Part2DObjectPython] Line923  # Draft 2D object (typed FeaturePython)
  ChamferSize = 0
  Closed = false
  End = (64,-60,0)
  FilletRadius = 0
  Length = 13
  MakeFace = false
  Placement = pos=(64,-73,0) rot=(0,0,1;0rad)
  Points = (2) [(0,0,0),(0,13,0)]
  Start = (64,-73,0)
  Subdivisions = 0
FEATURE [Part::Part2DObjectPython] Line924  # Draft 2D object (typed FeaturePython)
  ChamferSize = 0
  Closed = false
  End = (47.5,-76,0)
  FilletRadius = 0
  Length = 19
  MakeFace = false
  Placement = pos=(47.5,-57,0) rot=(0,0,1;0rad)
  Points = (2) [(0,0,0),(0,-19,0)]
  Start = (47.5,-57,0)
  Subdivisions = 0
FEATURE [Part::Part2DObjectPython] Arc470  # Draft 2D object (typed FeaturePython)
  FirstAngle = -90
  LastAngle = 0
  MakeFace = false
  Placement = pos=(63.5,-73,0) rot=(0,0,1;0rad)
  Radius = 0.5
FEATURE [Part::Part2DObjectPython] Line925  # Draft 2D object (typed FeaturePython)
  ChamferSize = 0
  Closed = false
  End = (28.625,-73,0)
  FilletRadius = 0
  Length = 13
  MakeFace = false
  Placement = pos=(28.625,-60,0) rot=(0,0,1;0rad)
  Points = (2) [(0,0,0),(0,-13,0)]
  Start = (28.625,-60,0)
  Subdivisions = 0
FEATURE [Part::Part2DObjectPython] Line926  # Draft 2D object (typed FeaturePython)
  ChamferSize = 0
  Closed = false
  End = (217.875,-73.5,0)
  FilletRadius = 0
  Length = 13
  MakeFace = false
  Placement = pos=(204.875,-73.5,0) rot=(0,0,1;0rad)
  Points = (2) [(0,0,0),(13,0,0)]
  Start = (204.875,-73.5,0)
  Subdivisions = 0
FEATURE [Part::Part2DObjectPython] Arc471  # Draft 2D object (typed FeaturePython)
  FirstAngle = 0
  LastAngle = 90
  MakeFace = false
  Placement = pos=(63.5,-60,0) rot=(0,0,1;0rad)
  Radius = 0.5
FEATURE [Part::Part2DObjectPython] Line927  # Draft 2D object (typed FeaturePython)
  ChamferSize = 0
  Closed = false
  End = (85.5,-57,0)
  FilletRadius = 0
  Length = 19
  MakeFace = false
  Placement = pos=(66.5,-57,0) rot=(0,0,1;0rad)
  Points = (2) [(0,0,0),(19,0,0)]
  Start = (66.5,-57,0)
  Subdivisions = 0
FEATURE [Part::Part2DObjectPython] Arc472  # Draft 2D object (typed FeaturePython)
  FirstAngle = 90
  LastAngle = 180
  MakeFace = false
  Placement = pos=(50.5,-60,0) rot=(0,0,1;0rad)
  Radius = 0.5
FEATURE [Part::Part2DObjectPython] Line928  # Draft 2D object (typed FeaturePython)
  ChamferSize = 0
  Closed = false
  End = (50,-73,0)
  FilletRadius = 0
  Length = 13
  MakeFace = false
  Placement = pos=(50,-60,0) rot=(0,0,1;0rad)
  Points = (2) [(0,0,0),(0,-13,0)]
  Start = (50,-60,0)
  Subdivisions = 0
FEATURE [Part::Part2DObjectPython] Line929  # Draft 2D object (typed FeaturePython)
  ChamferSize = 0
  Closed = false
  End = (42.125,-59.5,0)
  FilletRadius = 0
  Length = 13
  MakeFace = false
  Placement = pos=(29.125,-59.5,0) rot=(0,0,1;0rad)
  Points = (2) [(0,0,0),(13,0,0)]
  Start = (29.125,-59.5,0)
  Subdivisions = 0
FEATURE [Part::Part2DObjectPython] Line930  # Draft 2D object (typed FeaturePython)
  ChamferSize = 0
  Closed = false
  End = (223.25,-76,0)
  FilletRadius = 0
  Length = 19
  MakeFace = false
  Placement = pos=(223.25,-57,0) rot=(0,0,1;0rad)
  Points = (2) [(0,0,0),(0,-19,0)]
  Start = (223.25,-57,0)
  Subdivisions = 0
FEATURE [Part::Part2DObjectPython] Line931  # Draft 2D object (typed FeaturePython)
  ChamferSize = 0
  Closed = false
  End = (82.5,-59.5,0)
  FilletRadius = 0
  Length = 13
  MakeFace = false
  Placement = pos=(69.5,-59.5,0) rot=(0,0,1;0rad)
  Points = (2) [(0,0,0),(13,0,0)]
  Start = (69.5,-59.5,0)
  Subdivisions = 0
FEATURE [Part::Part2DObjectPython] Line932  # Draft 2D object (typed FeaturePython)
  ChamferSize = 0
  Closed = false
  End = (47.5,-76,0)
  FilletRadius = 0
  Length = 23.75
  MakeFace = false
  Placement = pos=(23.75,-76,0) rot=(0,0,1;0rad)
  Points = (2) [(0,0,0),(23.75,0,0)]
  Start = (23.75,-76,0)
  Subdivisions = 0
FEATURE [Part::Part2DObjectPython] Line933  # Draft 2D object (typed FeaturePython)
  ChamferSize = 0
  Closed = false
  End = (66.5,-76,0)
  FilletRadius = 0
  Length = 19
  MakeFace = false
  Placement = pos=(85.5,-76,0) rot=(0,0,1;0rad)
  Points = (2) [(0,0,0),(-19,0,0)]
  Start = (85.5,-76,0)
  Subdivisions = 0
FEATURE [Part::Part2DObjectPython] Line934  # Draft 2D object (typed FeaturePython)
  ChamferSize = 0
  Closed = false
  End = (241.625,-73.5,0)
  FilletRadius = 0
  Length = 13
  MakeFace = false
  Placement = pos=(228.625,-73.5,0) rot=(0,0,1;0rad)
  Points = (2) [(0,0,0),(13,0,0)]
  Start = (228.625,-73.5,0)
  Subdivisions = 0
FEATURE [Part::Part2DObjectPython] Line935  # Draft 2D object (typed FeaturePython)
  ChamferSize = 0
  Closed = false
  End = (47.5,-57,0)
  FilletRadius = 0
  Length = 19
  MakeFace = false
  Placement = pos=(47.5,-76,0) rot=(0,0,1;0rad)
  Points = (2) [(0,0,0),(0,19,0)]
  Start = (47.5,-76,0)
  Subdivisions = 0
FEATURE [Part::Part2DObjectPython] Line936  # Draft 2D object (typed FeaturePython)
  ChamferSize = 0
  Closed = false
  End = (242.125,-60,0)
  FilletRadius = 0
  Length = 13
  MakeFace = false
  Placement = pos=(242.125,-73,0) rot=(0,0,1;0rad)
  Points = (2) [(0,0,0),(0,13,0)]
  Start = (242.125,-73,0)
  Subdivisions = 0
FEATURE [Part::Part2DObjectPython] Line937  # Draft 2D object (typed FeaturePython)
  ChamferSize = 0
  Closed = false
  End = (85.5,-76,0)
  FilletRadius = 0
  Length = 19
  MakeFace = false
  Placement = pos=(85.5,-57,0) rot=(0,0,1;0rad)
  Points = (2) [(0,0,0),(0,-19,0)]
  Start = (85.5,-57,0)
  Subdivisions = 0
FEATURE [Part::Part2DObjectPython] Arc473  # Draft 2D object (typed FeaturePython)
  FirstAngle = -90
  LastAngle = 0
  MakeFace = false
  Placement = pos=(42.125,-73,0) rot=(0,0,1;0rad)
  Radius = 0.5
FEATURE [Part::Part2DObjectPython] Line938  # Draft 2D object (typed FeaturePython)
  ChamferSize = 0
  Closed = false
  End = (82.5,-73.5,0)
  FilletRadius = 0
  Length = 13
  MakeFace = false
  Placement = pos=(69.5,-73.5,0) rot=(0,0,1;0rad)
  Points = (2) [(0,0,0),(13,0,0)]
  Start = (69.5,-73.5,0)
  Subdivisions = 0
FEATURE [Part::Part2DObjectPython] Line939  # Draft 2D object (typed FeaturePython)
  ChamferSize = 0
  Closed = false
  End = (129.562,-74,0)
  FilletRadius = 0
  Length = 1.7
  MakeFace = false
  Placement = pos=(129.562,-75.7,0) rot=(0,0,1;0rad)
  Points = (2) [(0,0,0),(0,1.7,0)]
  Start = (129.562,-75.7,0)
  Subdivisions = 0
FEATURE [Part::Part2DObjectPython] Arc474  # Draft 2D object (typed FeaturePython)
  FirstAngle = 180
  LastAngle = 270
  MakeFace = false
  Placement = pos=(122.562,-75.7,0) rot=(0,0,1;0rad)
  Radius = 0.5
FEATURE [Part::Part2DObjectPython] Arc475  # Draft 2D object (typed FeaturePython)
  FirstAngle = -90
  LastAngle = 0
  MakeFace = false
  Placement = pos=(152.938,-75.7,0) rot=(0,0,1;0rad)
  Radius = 0.5
FEATURE [Part::Part2DObjectPython] Line940  # Draft 2D object (typed FeaturePython)
  ChamferSize = 0
  Closed = false
  End = (118.75,-76,0)
  FilletRadius = 0
  Length = 19
  MakeFace = false
  Placement = pos=(118.75,-57,0) rot=(0,0,1;0rad)
  Points = (2) [(0,0,0),(0,-19,0)]
  Start = (118.75,-57,0)
  Subdivisions = 0
FEATURE [Part::Part2DObjectPython] Arc476  # Draft 2D object (typed FeaturePython)
  FirstAngle = 180
  LastAngle = 270
  MakeFace = false
  Placement = pos=(69.5,-73,0) rot=(0,0,1;0rad)
  Radius = 0.5
FEATURE [Part::Part2DObjectPython] Arc477  # Draft 2D object (typed FeaturePython)
  FirstAngle = 90
  LastAngle = 180
  MakeFace = false
  Placement = pos=(95.625,-60,0) rot=(0,0,1;0rad)
  Radius = 0.5
FEATURE [Part::Part2DObjectPython] Arc478  # Draft 2D object (typed FeaturePython)
  FirstAngle = -90
  LastAngle = 0
  MakeFace = false
  Placement = pos=(82.5,-73,0) rot=(0,0,1;0rad)
  Radius = 0.5
FEATURE [Part::Part2DObjectPython] Arc479  # Draft 2D object (typed FeaturePython)
  FirstAngle = 180
  LastAngle = 270
  MakeFace = false
  Placement = pos=(95.625,-73,0) rot=(0,0,1;0rad)
  Radius = 0.5
FEATURE [Part::Part2DObjectPython] Arc480  # Draft 2D object (typed FeaturePython)
  FirstAngle = 0
  LastAngle = 90
  MakeFace = false
  Placement = pos=(82.5,-60,0) rot=(0,0,1;0rad)
  Radius = 0.5
FEATURE [Part::Part2DObjectPython] Line941  # Draft 2D object (typed FeaturePython)
  ChamferSize = 0
  Closed = false
  End = (95.125,-73,0)
  FilletRadius = 0
  Length = 13
  MakeFace = false
  Placement = pos=(95.125,-60,0) rot=(0,0,1;0rad)
  Points = (2) [(0,0,0),(0,-13,0)]
  Start = (95.125,-60,0)
  Subdivisions = 0
FEATURE [Part::Part2DObjectPython] Line942  # Draft 2D object (typed FeaturePython)
  ChamferSize = 0
  Closed = false
  End = (118.75,-76,0)
  FilletRadius = 0
  Length = 33.25
  MakeFace = false
  Placement = pos=(85.5,-76,0) rot=(0,0,1;0rad)
  Points = (2) [(0,0,0),(33.25,0,0)]
  Start = (85.5,-76,0)
  Subdivisions = 0
FEATURE [Part::Part2DObjectPython] Line943  # Draft 2D object (typed FeaturePython)
  ChamferSize = 0
  Closed = false
  End = (83,-60,0)
  FilletRadius = 0
  Length = 13
  MakeFace = false
  Placement = pos=(83,-73,0) rot=(0,0,1;0rad)
  Points = (2) [(0,0,0),(0,13,0)]
  Start = (83,-73,0)
  Subdivisions = 0
FEATURE [Part::Part2DObjectPython] Line944  # Draft 2D object (typed FeaturePython)
  ChamferSize = 0
  Closed = false
  End = (85.5,-76,0)
  FilletRadius = 0
  Length = 19
  MakeFace = false
  Placement = pos=(85.5,-57,0) rot=(0,0,1;0rad)
  Points = (2) [(0,0,0),(0,-19,0)]
  Start = (85.5,-57,0)
  Subdivisions = 0
FEATURE [Part::Part2DObjectPython] Line945  # Draft 2D object (typed FeaturePython)
  ChamferSize = 0
  Closed = false
  End = (156.75,-76,0)
  FilletRadius = 0
  Length = 19
  MakeFace = false
  Placement = pos=(156.75,-57,0) rot=(0,0,1;0rad)
  Points = (2) [(0,0,0),(0,-19,0)]
  Start = (156.75,-57,0)
  Subdivisions = 0
FEATURE [Part::Part2DObjectPython] Line946  # Draft 2D object (typed FeaturePython)
  ChamferSize = 0
  Closed = false
  End = (156.75,-76,0)
  FilletRadius = 0
  Length = 38
  MakeFace = false
  Placement = pos=(118.75,-76,0) rot=(0,0,1;0rad)
  Points = (2) [(0,0,0),(38,0,0)]
  Start = (118.75,-76,0)
  Subdivisions = 0
FEATURE [Part::Part2DObjectPython] Line947  # Draft 2D object (typed FeaturePython)
  ChamferSize = 0
  Closed = false
  End = (118.75,-57,0)
  FilletRadius = 0
  Length = 33.25
  MakeFace = false
  Placement = pos=(85.5,-57,0) rot=(0,0,1;0rad)
  Points = (2) [(0,0,0),(33.25,0,0)]
  Start = (85.5,-57,0)
  Subdivisions = 0
FEATURE [Part::Part2DObjectPython] Line948  # Draft 2D object (typed FeaturePython)
  ChamferSize = 0
  Closed = false
  End = (118.75,-76,0)
  FilletRadius = 0
  Length = 19
  MakeFace = false
  Placement = pos=(118.75,-57,0) rot=(0,0,1;0rad)
  Points = (2) [(0,0,0),(4.26326e-14,-19,0)]
  Start = (118.75,-57,0)
  Subdivisions = 0
FEATURE [Part::Part2DObjectPython] Line949  # Draft 2D object (typed FeaturePython)
  ChamferSize = 0
  Closed = false
  End = (108.625,-59.5,0)
  FilletRadius = 0
  Length = 13
  MakeFace = false
  Placement = pos=(95.625,-59.5,0) rot=(0,0,1;0rad)
  Points = (2) [(0,0,0),(13,0,0)]
  Start = (95.625,-59.5,0)
  Subdivisions = 0
FEATURE [Part::Part2DObjectPython] Line950  # Draft 2D object (typed FeaturePython)
  ChamferSize = 0
  Closed = false
  End = (122.562,-56,0)
  FilletRadius = 0
  Length = 30.376
  MakeFace = false
  Placement = pos=(152.938,-56,0) rot=(0,0,1;0rad)
  Points = (2) [(0,0,0),(-30.376,0,0)]
  Start = (152.938,-56,0)
  Subdivisions = 0
FEATURE [Part::Part2DObjectPython] Line951  # Draft 2D object (typed FeaturePython)
  ChamferSize = 0
  Closed = false
  End = (156.75,-57,0)
  FilletRadius = 0
  Length = 38
  MakeFace = false
  Placement = pos=(118.75,-57,0) rot=(0,0,1;0rad)
  Points = (2) [(0,0,0),(38,1.42109e-14,0)]
  Start = (118.75,-57,0)
  Subdivisions = 0
FEATURE [Part::Part2DObjectPython] Line952  # Draft 2D object (typed FeaturePython)
  ChamferSize = 0
  Closed = false
  End = (129.062,-76.2,0)
  FilletRadius = 0
  Length = 6.5
  MakeFace = false
  Placement = pos=(122.562,-76.2,0) rot=(0,0,1;0rad)
  Points = (2) [(0,0,0),(6.5,0,0)]
  Start = (122.562,-76.2,0)
  Subdivisions = 0
FEATURE [Part::Part2DObjectPython] Line953  # Draft 2D object (typed FeaturePython)
  ChamferSize = 0
  Closed = false
  End = (66.5,-76,0)
  FilletRadius = 0
  Length = 19
  MakeFace = false
  Placement = pos=(66.5,-57,0) rot=(0,0,1;0rad)
  Points = (2) [(0,0,0),(0,-19,0)]
  Start = (66.5,-57,0)
  Subdivisions = 0
FEATURE [Part::Part2DObjectPython] Arc481  # Draft 2D object (typed FeaturePython)
  FirstAngle = 0
  LastAngle = 90
  MakeFace = false
  Placement = pos=(152.938,-56.5,0) rot=(0,0,1;0rad)
  Radius = 0.5
FEATURE [Part::Part2DObjectPython] Arc482  # Draft 2D object (typed FeaturePython)
  FirstAngle = 90
  LastAngle = 180
  MakeFace = false
  Placement = pos=(69.5,-60,0) rot=(0,0,1;0rad)
  Radius = 0.5
FEATURE [Part::Part2DObjectPython] Arc483  # Draft 2D object (typed FeaturePython)
  FirstAngle = 0
  LastAngle = 90
  MakeFace = false
  Placement = pos=(108.625,-60,0) rot=(0,0,1;0rad)
  Radius = 0.5
FEATURE [Part::Part2DObjectPython] Line954  # Draft 2D object (typed FeaturePython)
  ChamferSize = 0
  Closed = false
  End = (122.062,-75.7,0)
  FilletRadius = 0
  Length = 19.2
  MakeFace = false
  Placement = pos=(122.062,-56.5,0) rot=(0,0,1;0rad)
  Points = (2) [(0,0,0),(4.26326e-14,-19.2,0)]
  Start = (122.062,-56.5,0)
  Subdivisions = 0
FEATURE [Part::Part2DObjectPython] Line955  # Draft 2D object (typed FeaturePython)
  ChamferSize = 0
  Closed = false
  End = (69,-73,0)
  FilletRadius = 0
  Length = 13
  MakeFace = false
  Placement = pos=(69,-60,0) rot=(0,0,1;0rad)
  Points = (2) [(0,0,0),(0,-13,0)]
  Start = (69,-60,0)
  Subdivisions = 0
FEATURE [Part::Part2DObjectPython] Arc484  # Draft 2D object (typed FeaturePython)
  FirstAngle = -90
  LastAngle = 0
  MakeFace = false
  Placement = pos=(108.625,-73,0) rot=(0,0,1;0rad)
  Radius = 0.5
FEATURE [Part::Part2DObjectPython] Line956  # Draft 2D object (typed FeaturePython)
  ChamferSize = 0
  Closed = false
  End = (145.438,-73.5,0)
  FilletRadius = 0
  Length = 15.376
  MakeFace = false
  Placement = pos=(130.062,-73.5,0) rot=(0,0,1;0rad)
  Points = (2) [(0,0,0),(15.376,0,0)]
  Start = (130.062,-73.5,0)
  Subdivisions = 0
FEATURE [Part::Part2DObjectPython] Line957  # Draft 2D object (typed FeaturePython)
  ChamferSize = 0
  Closed = false
  End = (152.938,-76.2,0)
  FilletRadius = 0
  Length = 6.5
  MakeFace = false
  Placement = pos=(146.438,-76.2,0) rot=(0,0,1;0rad)
  Points = (2) [(0,0,0),(6.5,0,0)]
  Start = (146.438,-76.2,0)
  Subdivisions = 0
FEATURE [Part::Part2DObjectPython] Arc485  # Draft 2D object (typed FeaturePython)
  FirstAngle = 180
  LastAngle = 270
  MakeFace = false
  Placement = pos=(146.438,-75.7,0) rot=(0,0,1;0rad)
  Radius = 0.5
FEATURE [Part::Part2DObjectPython] Arc486  # Draft 2D object (typed FeaturePython)
  FirstAngle = -90
  LastAngle = 0
  MakeFace = false
  Placement = pos=(129.062,-75.7,0) rot=(0,0,1;0rad)
  Radius = 0.5
FEATURE [Part::Part2DObjectPython] Arc487  # Draft 2D object (typed FeaturePython)
  FirstAngle = 90
  LastAngle = 180
  MakeFace = false
  Placement = pos=(122.562,-56.5,0) rot=(0,0,1;0rad)
  Radius = 0.5
FEATURE [Part::Part2DObjectPython] Arc488  # Draft 2D object (typed FeaturePython)
  FirstAngle = 90
  LastAngle = 180
  MakeFace = false
  Placement = pos=(130.062,-74,0) rot=(0,0,1;0rad)
  Radius = 0.5
FEATURE [App::DocumentObjectGroup] Group100
  Group = -> [Line663,Line677,Line665,Line681,Line666,Arc351,Arc350,Line659,Arc348,Line675,Arc349,Line674]
FEATURE [App::DocumentObjectGroup] Group101  label="1.75u space001"
  Group = -> [Line947,Line944,Line942,Line940,Arc483,Line900,Arc484,Line941,Line949,Arc477,Arc479,Line901]
FEATURE [App::DocumentObjectGroup] Group103
  Group = -> [Line714,Line703,Line700,Line712,Line699,Arc372,Arc371,Line716,Arc369,Line704,Arc370,Line706]
FEATURE [App::DocumentObjectGroup] Group115  label="2u space001"
  Group = -> [Line951,Line948,Line946,Line945,Arc487,Arc481,Line950,Arc474,Arc486,Line952,Line954,Arc488,Arc475,Line957,Arc485,Arc404,Line939,Line956,Line784,Line787]
FEATURE [Part::Part2DObjectPython] Arc489  # Draft 2D object (typed FeaturePython)
  FirstAngle = 90
  LastAngle = 180
  MakeFace = false
  Placement = pos=(72.6,-56.5,0) rot=(0,0,1;0rad)
  Radius = 0.5
FEATURE [Part::Part2DObjectPython] Arc490  # Draft 2D object (typed FeaturePython)
  FirstAngle = 180
  LastAngle = 270
  MakeFace = false
  Placement = pos=(126.5,-73,0) rot=(0,0,1;0rad)
  Radius = 0.5
FEATURE [Part::Part2DObjectPython] Arc491  # Draft 2D object (typed FeaturePython)
  FirstAngle = -90
  LastAngle = 0
  MakeFace = false
  Placement = pos=(139.5,-73,0) rot=(0,0,1;0rad)
  Radius = 0.5
FEATURE [Part::Part2DObjectPython] Arc492  # Draft 2D object (typed FeaturePython)
  FirstAngle = -90
  LastAngle = 0
  MakeFace = false
  Placement = pos=(61.125,-73,0) rot=(0,0,1;0rad)
  Radius = 0.5
FEATURE [Part::Part2DObjectPython] Line958  # Draft 2D object (typed FeaturePython)
  ChamferSize = 0
  Closed = false
  End = (199.5,-76,0)
  FilletRadius = 0
  Length = 19
  MakeFace = false
  Placement = pos=(199.5,-57,0) rot=(0,0,1;0rad)
  Points = (2) [(0,0,0),(0,-19,0)]
  Start = (199.5,-57,0)
  Subdivisions = 0
FEATURE [Part::Part2DObjectPython] Line959  # Draft 2D object (typed FeaturePython)
  ChamferSize = 0
  Closed = false
  End = (139.5,-73.5,0)
  FilletRadius = 0
  Length = 13
  MakeFace = false
  Placement = pos=(126.5,-73.5,0) rot=(0,0,1;0rad)
  Points = (2) [(0,0,0),(13,0,0)]
  Start = (126.5,-73.5,0)
  Subdivisions = 0
FEATURE [Part::Part2DObjectPython] Arc493  # Draft 2D object (typed FeaturePython)
  FirstAngle = 180
  LastAngle = 270
  MakeFace = false
  Placement = pos=(48.125,-73,0) rot=(0,0,1;0rad)
  Radius = 0.5
FEATURE [Part::Part2DObjectPython] Line960  # Draft 2D object (typed FeaturePython)
  ChamferSize = 0
  Closed = false
  End = (61.125,-59.5,0)
  FilletRadius = 0
  Length = 13
  MakeFace = false
  Placement = pos=(48.125,-59.5,0) rot=(0,0,1;0rad)
  Points = (2) [(0,0,0),(13,0,0)]
  Start = (48.125,-59.5,0)
  Subdivisions = 0
FEATURE [Part::Part2DObjectPython] Line961  # Draft 2D object (typed FeaturePython)
  ChamferSize = 0
  Closed = false
  End = (47.625,-73,0)
  FilletRadius = 0
  Length = 13
  MakeFace = false
  Placement = pos=(47.625,-60,0) rot=(0,0,1;0rad)
  Points = (2) [(0,0,0),(0,-13,0)]
  Start = (47.625,-60,0)
  Subdivisions = 0
FEATURE [Part::Part2DObjectPython] Line962  # Draft 2D object (typed FeaturePython)
  ChamferSize = 0
  Closed = false
  End = (140,-60,0)
  FilletRadius = 0
  Length = 13
  MakeFace = false
  Placement = pos=(140,-73,0) rot=(0,0,1;0rad)
  Points = (2) [(0,0,0),(0,13,0)]
  Start = (140,-73,0)
  Subdivisions = 0
FEATURE [Part::Part2DObjectPython] Line963  # Draft 2D object (typed FeaturePython)
  ChamferSize = 0
  Closed = false
  End = (126,-73,0)
  FilletRadius = 0
  Length = 13
  MakeFace = false
  Placement = pos=(126,-60,0) rot=(0,0,1;0rad)
  Points = (2) [(0,0,0),(0,-13,0)]
  Start = (126,-60,0)
  Subdivisions = 0
FEATURE [Part::Part2DObjectPython] Line964  # Draft 2D object (typed FeaturePython)
  ChamferSize = 0
  Closed = false
  End = (66.5,-57,0)
  FilletRadius = 0
  Length = 19
  MakeFace = false
  Placement = pos=(66.5,-76,0) rot=(0,0,1;0rad)
  Points = (2) [(0,0,0),(0,19,0)]
  Start = (66.5,-76,0)
  Subdivisions = 0
FEATURE [Part::Part2DObjectPython] Line965  # Draft 2D object (typed FeaturePython)
  ChamferSize = 0
  Closed = false
  End = (66.5,-76,0)
  FilletRadius = 0
  Length = 23.75
  MakeFace = false
  Placement = pos=(42.75,-76,0) rot=(0,0,1;0rad)
  Points = (2) [(0,0,0),(23.75,0,0)]
  Start = (42.75,-76,0)
  Subdivisions = 0
FEATURE [Part::Part2DObjectPython] Line966  # Draft 2D object (typed FeaturePython)
  ChamferSize = 0
  Closed = false
  End = (66.5,-76,0)
  FilletRadius = 0
  Length = 19
  MakeFace = false
  Placement = pos=(66.5,-57,0) rot=(0,0,1;0rad)
  Points = (2) [(0,0,0),(0,-19,0)]
  Start = (66.5,-57,0)
  Subdivisions = 0
FEATURE [Part::Part2DObjectPython] Line967  # Draft 2D object (typed FeaturePython)
  ChamferSize = 0
  Closed = false
  End = (199.5,-76,0)
  FilletRadius = 0
  Length = 133
  MakeFace = false
  Placement = pos=(66.5,-76,0) rot=(0,0,1;0rad)
  Points = (2) [(0,0,0),(133,0,0)]
  Start = (66.5,-76,0)
  Subdivisions = 0
FEATURE [Part::Part2DObjectPython] Arc494  # Draft 2D object (typed FeaturePython)
  FirstAngle = 90
  LastAngle = 180
  MakeFace = false
  Placement = pos=(140.5,-60,0) rot=(0,0,1;0rad)
  Radius = 0.5
FEATURE [Part::Part2DObjectPython] Arc495  # Draft 2D object (typed FeaturePython)
  FirstAngle = 90
  LastAngle = 180
  MakeFace = false
  Placement = pos=(48.125,-60,0) rot=(0,0,1;0rad)
  Radius = 0.5
FEATURE [Part::Part2DObjectPython] Line968  # Draft 2D object (typed FeaturePython)
  ChamferSize = 0
  Closed = false
  End = (199.5,-57,0)
  FilletRadius = 0
  Length = 133
  MakeFace = false
  Placement = pos=(66.5,-57,0) rot=(0,0,1;0rad)
  Points = (2) [(0,0,0),(133,0,0)]
  Start = (66.5,-57,0)
  Subdivisions = 0
FEATURE [Part::Part2DObjectPython] Line969  # Draft 2D object (typed FeaturePython)
  ChamferSize = 0
  Closed = false
  End = (61.125,-73.5,0)
  FilletRadius = 0
  Length = 13
  MakeFace = false
  Placement = pos=(48.125,-73.5,0) rot=(0,0,1;0rad)
  Points = (2) [(0,0,0),(13,0,0)]
  Start = (48.125,-73.5,0)
  Subdivisions = 0
FEATURE [Part::Part2DObjectPython] Arc496  # Draft 2D object (typed FeaturePython)
  FirstAngle = 0
  LastAngle = 90
  MakeFace = false
  Placement = pos=(125.5,-60,0) rot=(0,0,1;0rad)
  Radius = 0.5
FEATURE [Part::Part2DObjectPython] Line970  # Draft 2D object (typed FeaturePython)
  ChamferSize = 0
  Closed = false
  End = (199.5,-76,0)
  FilletRadius = 0
  Length = 19
  MakeFace = false
  Placement = pos=(199.5,-57,0) rot=(0,0,1;0rad)
  Points = (2) [(0,0,0),(0,-19,0)]
  Start = (199.5,-57,0)
  Subdivisions = 0
FEATURE [Part::Part2DObjectPython] Arc497  # Draft 2D object (typed FeaturePython)
  FirstAngle = -90
  LastAngle = 0
  MakeFace = false
  Placement = pos=(79.1,-75.7,0) rot=(0,0,1;0rad)
  Radius = 0.5
FEATURE [Part::Part2DObjectPython] Line971  # Draft 2D object (typed FeaturePython)
  ChamferSize = 0
  Closed = false
  End = (79.1,-76.2,0)
  FilletRadius = 0
  Length = 6.5
  MakeFace = false
  Placement = pos=(72.6,-76.2,0) rot=(0,0,1;0rad)
  Points = (2) [(0,0,0),(6.5,0,0)]
  Start = (72.6,-76.2,0)
  Subdivisions = 0
FEATURE [Part::Part2DObjectPython] Line972  # Draft 2D object (typed FeaturePython)
  ChamferSize = 0
  Closed = false
  End = (79.6,-75.7,0)
  FilletRadius = 0
  Length = 15.7
  MakeFace = false
  Placement = pos=(79.6,-60,0) rot=(0,0,1;0rad)
  Points = (2) [(0,0,0),(0,-15.7,0)]
  Start = (79.6,-60,0)
  Subdivisions = 0
FEATURE [Part::Part2DObjectPython] Line973  # Draft 2D object (typed FeaturePython)
  ChamferSize = 0
  Closed = false
  End = (80.1,-59.5,0)
  FilletRadius = 0
  Length = 45.4
  MakeFace = false
  Placement = pos=(125.5,-59.5,0) rot=(0,0,1;0rad)
  Points = (2) [(0,0,0),(-45.4,0,0)]
  Start = (125.5,-59.5,0)
  Subdivisions = 0
FEATURE [Part::Part2DObjectPython] Line974  # Draft 2D object (typed FeaturePython)
  ChamferSize = 0
  Closed = false
  End = (72.1,-75.7,0)
  FilletRadius = 0
  Length = 19.2
  MakeFace = false
  Placement = pos=(72.1,-56.5,0) rot=(0,0,1;0rad)
  Points = (2) [(0,0,0),(0,-19.2,0)]
  Start = (72.1,-56.5,0)
  Subdivisions = 0
FEATURE [Part::Part2DObjectPython] Line975  # Draft 2D object (typed FeaturePython)
  ChamferSize = 0
  Closed = false
  End = (140.5,-59.5,0)
  FilletRadius = 0
  Length = 45.4
  MakeFace = false
  Placement = pos=(185.9,-59.5,0) rot=(0,0,1;0rad)
  Points = (2) [(0,0,0),(-45.4,0,0)]
  Start = (185.9,-59.5,0)
  Subdivisions = 0
FEATURE [Part::Part2DObjectPython] Arc498  # Draft 2D object (typed FeaturePython)
  FirstAngle = -90
  LastAngle = 0
  MakeFace = false
  Placement = pos=(193.4,-75.7,0) rot=(0,0,1;0rad)
  Radius = 0.5
FEATURE [Part::Part2DObjectPython] Line976  # Draft 2D object (typed FeaturePython)
  ChamferSize = 0
  Closed = false
  End = (193.9,-56.5,0)
  FilletRadius = 0
  Length = 19.2
  MakeFace = false
  Placement = pos=(193.9,-75.7,0) rot=(0,0,1;0rad)
  Points = (2) [(0,0,0),(0,19.2,0)]
  Start = (193.9,-75.7,0)
  Subdivisions = 0
FEATURE [Part::Part2DObjectPython] Arc499  # Draft 2D object (typed FeaturePython)
  FirstAngle = 0
  LastAngle = 90
  MakeFace = false
  Placement = pos=(193.4,-56.5,0) rot=(0,0,1;0rad)
  Radius = 0.5
FEATURE [Part::Part2DObjectPython] Arc500  # Draft 2D object (typed FeaturePython)
  FirstAngle = 180
  LastAngle = 270
  MakeFace = false
  Placement = pos=(72.6,-75.7,0) rot=(0,0,1;0rad)
  Radius = 0.5
FEATURE [Part::Part2DObjectPython] Line977  # Draft 2D object (typed FeaturePython)
  ChamferSize = 0
  Closed = false
  End = (218.375,-60,0)
  FilletRadius = 0
  Length = 13
  MakeFace = false
  Placement = pos=(218.375,-73,0) rot=(0,0,1;0rad)
  Points = (2) [(0,0,0),(0,13,0)]
  Start = (218.375,-73,0)
  Subdivisions = 0
FEATURE [Part::Part2DObjectPython] Arc501  # Draft 2D object (typed FeaturePython)
  FirstAngle = 0
  LastAngle = 90
  MakeFace = false
  Placement = pos=(217.875,-60,0) rot=(0,0,1;0rad)
  Radius = 0.5
FEATURE [Part::Part2DObjectPython] Arc502  # Draft 2D object (typed FeaturePython)
  FirstAngle = 90
  LastAngle = 180
  MakeFace = false
  Placement = pos=(80.1,-60,0) rot=(0,0,1;0rad)
  Radius = 0.5
FEATURE [Part::Part2DObjectPython] Line978  # Draft 2D object (typed FeaturePython)
  ChamferSize = 0
  Closed = false
  End = (193.4,-76.2,0)
  FilletRadius = 0
  Length = 6.5
  MakeFace = false
  Placement = pos=(186.9,-76.2,0) rot=(0,0,1;0rad)
  Points = (2) [(0,0,0),(6.5,0,0)]
  Start = (186.9,-76.2,0)
  Subdivisions = 0
FEATURE [Part::Part2DObjectPython] Arc503  # Draft 2D object (typed FeaturePython)
  FirstAngle = 180
  LastAngle = 270
  MakeFace = false
  Placement = pos=(204.875,-73,0) rot=(0,0,1;0rad)
  Radius = 0.5
FEATURE [Part::Part2DObjectPython] Arc504  # Draft 2D object (typed FeaturePython)
  FirstAngle = 0
  LastAngle = 90
  MakeFace = false
  Placement = pos=(185.9,-60,0) rot=(0,0,1;0rad)
  Radius = 0.5
FEATURE [Part::Part2DObjectPython] Line979  # Draft 2D object (typed FeaturePython)
  ChamferSize = 0
  Closed = false
  End = (72.6,-56,0)
  FilletRadius = 0
  Length = 120.8
  MakeFace = false
  Placement = pos=(193.4,-56,0) rot=(0,0,1;0rad)
  Points = (2) [(0,0,0),(-120.8,0,0)]
  Start = (193.4,-56,0)
  Subdivisions = 0
FEATURE [Part::Part2DObjectPython] Line980  # Draft 2D object (typed FeaturePython)
  ChamferSize = 0
  Closed = false
  End = (186.4,-75.7,0)
  FilletRadius = 0
  Length = 15.7
  MakeFace = false
  Placement = pos=(186.4,-60,0) rot=(0,0,1;0rad)
  Points = (2) [(0,0,0),(0,-15.7,0)]
  Start = (186.4,-60,0)
  Subdivisions = 0
FEATURE [Part::Part2DObjectPython] Arc505  # Draft 2D object (typed FeaturePython)
  FirstAngle = 180
  LastAngle = 270
  MakeFace = false
  Placement = pos=(186.9,-75.7,0) rot=(0,0,1;0rad)
  Radius = 0.5
FEATURE [App::DocumentObjectGroup] Group116  label="7u space001"
  Group = -> [Line968,Line966,Line967,Line958,Line962,Arc496,Line963,Arc490,Arc494,Arc491,Line959,Arc489,Arc499,Arc500,Line971,Arc497,Arc502,Line973,Line972,Line974,Line979,Arc505,Line978,Arc498,Line976,Arc504,Line980,Line975]
FEATURE [Part::Part2DObjectPython] Line981  # Draft 2D object (typed FeaturePython)
  ChamferSize = 0
  Closed = false
  End = (223.25,-57,0)
  FilletRadius = 0
  Length = 23.75
  MakeFace = false
  Placement = pos=(199.5,-57,0) rot=(0,0,1;0rad)
  Points = (2) [(0,0,0),(23.75,0,0)]
  Start = (199.5,-57,0)
  Subdivisions = 0
FEATURE [Part::Part2DObjectPython] Line982  # Draft 2D object (typed FeaturePython)
  ChamferSize = 0
  Closed = false
  End = (223.25,-57,0)
  FilletRadius = 0
  Length = 19
  MakeFace = false
  Placement = pos=(223.25,-76,0) rot=(0,0,1;0rad)
  Points = (2) [(0,0,0),(0,19,0)]
  Start = (223.25,-76,0)
  Subdivisions = 0
FEATURE [Part::Part2DObjectPython] Line983  # Draft 2D object (typed FeaturePython)
  ChamferSize = 0
  Closed = false
  End = (217.875,-59.5,0)
  FilletRadius = 0
  Length = 13
  MakeFace = false
  Placement = pos=(204.875,-59.5,0) rot=(0,0,1;0rad)
  Points = (2) [(0,0,0),(13,0,0)]
  Start = (204.875,-59.5,0)
  Subdivisions = 0
FEATURE [Part::Part2DObjectPython] Line984  # Draft 2D object (typed FeaturePython)
  ChamferSize = 0
  Closed = false
  End = (204.375,-73,0)
  FilletRadius = 0
  Length = 13
  MakeFace = false
  Placement = pos=(204.375,-60,0) rot=(0,0,1;0rad)
  Points = (2) [(0,0,0),(0,-13,0)]
  Start = (204.375,-60,0)
  Subdivisions = 0
FEATURE [Part::Part2DObjectPython] Arc506  # Draft 2D object (typed FeaturePython)
  FirstAngle = -90
  LastAngle = 0
  MakeFace = false
  Placement = pos=(217.875,-73,0) rot=(0,0,1;0rad)
  Radius = 0.5
FEATURE [Part::Part2DObjectPython] Arc507  # Draft 2D object (typed FeaturePython)
  FirstAngle = 90
  LastAngle = 180
  MakeFace = false
  Placement = pos=(204.875,-60,0) rot=(0,0,1;0rad)
  Radius = 0.5
FEATURE [App::DocumentObjectGroup] Group110
  Group = -> [Line981,Line970,Line905,Line982,Line977,Arc501,Arc507,Line984,Arc503,Line983,Line926,Arc506]
FEATURE [Part::Part2DObjectPython] Line985  # Draft 2D object (typed FeaturePython)
  ChamferSize = 0
  Closed = false
  End = (199.5,-57,0)
  FilletRadius = 0
  Length = 23.75
  MakeFace = false
  Placement = pos=(175.75,-57,0) rot=(0,0,1;0rad)
  Points = (2) [(0,0,0),(23.75,0,0)]
  Start = (175.75,-57,0)
  Subdivisions = 0
FEATURE [Part::Part2DObjectPython] Arc508  # Draft 2D object (typed FeaturePython)
  FirstAngle = 0
  LastAngle = 90
  MakeFace = false
  Placement = pos=(172.75,-60,0) rot=(0,0,1;0rad)
  Radius = 0.5
FEATURE [Part::Part2DObjectPython] Arc509  # Draft 2D object (typed FeaturePython)
  FirstAngle = 0
  LastAngle = 90
  MakeFace = false
  Placement = pos=(194.125,-60,0) rot=(0,0,1;0rad)
  Radius = 0.5
FEATURE [Part::Part2DObjectPython] Line986  # Draft 2D object (typed FeaturePython)
  ChamferSize = 0
  Closed = false
  End = (194.125,-73.5,0)
  FilletRadius = 0
  Length = 13
  MakeFace = false
  Placement = pos=(181.125,-73.5,0) rot=(0,0,1;0rad)
  Points = (2) [(0,0,0),(13,0,0)]
  Start = (181.125,-73.5,0)
  Subdivisions = 0
FEATURE [Part::Part2DObjectPython] Line987  # Draft 2D object (typed FeaturePython)
  ChamferSize = 0
  Closed = false
  End = (247,-57,0)
  FilletRadius = 0
  Length = 19
  MakeFace = false
  Placement = pos=(247,-76,0) rot=(0,0,1;0rad)
  Points = (2) [(0,0,0),(0,19,0)]
  Start = (247,-76,0)
  Subdivisions = 0
FEATURE [Part::Part2DObjectPython] Line988  # Draft 2D object (typed FeaturePython)
  ChamferSize = 0
  Closed = false
  End = (159.25,-73,0)
  FilletRadius = 0
  Length = 13
  MakeFace = false
  Placement = pos=(159.25,-60,0) rot=(0,0,1;0rad)
  Points = (2) [(0,0,0),(0,-13,0)]
  Start = (159.25,-60,0)
  Subdivisions = 0
FEATURE [Part::Part2DObjectPython] Line989  # Draft 2D object (typed FeaturePython)
  ChamferSize = 0
  Closed = false
  End = (199.5,-57,0)
  FilletRadius = 0
  Length = 19
  MakeFace = false
  Placement = pos=(199.5,-76,0) rot=(0,0,1;0rad)
  Points = (2) [(0,0,0),(0,19,0)]
  Start = (199.5,-76,0)
  Subdivisions = 0
FEATURE [Part::Part2DObjectPython] Line990  # Draft 2D object (typed FeaturePython)
  ChamferSize = 0
  Closed = false
  End = (173.25,-60,0)
  FilletRadius = 0
  Length = 13
  MakeFace = false
  Placement = pos=(173.25,-73,0) rot=(0,0,1;0rad)
  Points = (2) [(0,0,0),(0,13,0)]
  Start = (173.25,-73,0)
  Subdivisions = 0
FEATURE [Part::Part2DObjectPython] Arc510  # Draft 2D object (typed FeaturePython)
  FirstAngle = 180
  LastAngle = 270
  MakeFace = false
  Placement = pos=(159.75,-73,0) rot=(0,0,1;0rad)
  Radius = 0.5
FEATURE [Part::Part2DObjectPython] Arc511  # Draft 2D object (typed FeaturePython)
  FirstAngle = 90
  LastAngle = 180
  MakeFace = false
  Placement = pos=(159.75,-60,0) rot=(0,0,1;0rad)
  Radius = 0.5
FEATURE [Part::Part2DObjectPython] Line991  # Draft 2D object (typed FeaturePython)
  ChamferSize = 0
  Closed = false
  End = (156.75,-76,0)
  FilletRadius = 0
  Length = 19
  MakeFace = false
  Placement = pos=(156.75,-57,0) rot=(0,0,1;0rad)
  Points = (2) [(0,0,0),(0,-19,0)]
  Start = (156.75,-57,0)
  Subdivisions = 0
FEATURE [Part::Part2DObjectPython] Arc512  # Draft 2D object (typed FeaturePython)
  FirstAngle = 90
  LastAngle = 180
  MakeFace = false
  Placement = pos=(181.125,-60,0) rot=(0,0,1;0rad)
  Radius = 0.5
FEATURE [Part::Part2DObjectPython] Line992  # Draft 2D object (typed FeaturePython)
  ChamferSize = 0
  Closed = false
  End = (199.5,-76,0)
  FilletRadius = 0
  Length = 23.75
  MakeFace = false
  Placement = pos=(175.75,-76,0) rot=(0,0,1;0rad)
  Points = (2) [(0,0,0),(23.75,0,0)]
  Start = (175.75,-76,0)
  Subdivisions = 0
FEATURE [Part::Part2DObjectPython] Line993  # Draft 2D object (typed FeaturePython)
  ChamferSize = 0
  Closed = false
  End = (194.625,-60,0)
  FilletRadius = 0
  Length = 13
  MakeFace = false
  Placement = pos=(194.625,-73,0) rot=(0,0,1;0rad)
  Points = (2) [(0,0,0),(0,13,0)]
  Start = (194.625,-73,0)
  Subdivisions = 0
FEATURE [Part::Part2DObjectPython] Arc513  # Draft 2D object (typed FeaturePython)
  FirstAngle = -90
  LastAngle = 0
  MakeFace = false
  Placement = pos=(194.125,-73,0) rot=(0,0,1;0rad)
  Radius = 0.5
FEATURE [Part::Part2DObjectPython] Line994  # Draft 2D object (typed FeaturePython)
  ChamferSize = 0
  Closed = false
  End = (223.25,-57,0)
  FilletRadius = 0
  Length = 19
  MakeFace = false
  Placement = pos=(223.25,-76,0) rot=(0,0,1;0rad)
  Points = (2) [(0,0,0),(0,19,0)]
  Start = (223.25,-76,0)
  Subdivisions = 0
FEATURE [Part::Part2DObjectPython] Arc514  # Draft 2D object (typed FeaturePython)
  FirstAngle = -90
  LastAngle = 0
  MakeFace = false
  Placement = pos=(172.75,-73,0) rot=(0,0,1;0rad)
  Radius = 0.5
FEATURE [App::DocumentObjectGroup] Group118
  Group = -> [Line893,Line882,Line894,Line991,Line874,Arc508,Arc511,Line988,Arc510,Line793,Arc514,Line990]
FEATURE [Part::Part2DObjectPython] Arc515  # Draft 2D object (typed FeaturePython)
  FirstAngle = 180
  LastAngle = 270
  MakeFace = false
  Placement = pos=(181.125,-73,0) rot=(0,0,1;0rad)
  Radius = 0.5
FEATURE [Part::Part2DObjectPython] Line995  # Draft 2D object (typed FeaturePython)
  ChamferSize = 0
  Closed = false
  End = (194.125,-59.5,0)
  FilletRadius = 0
  Length = 13
  MakeFace = false
  Placement = pos=(181.125,-59.5,0) rot=(0,0,1;0rad)
  Points = (2) [(0,0,0),(13,0,0)]
  Start = (181.125,-59.5,0)
  Subdivisions = 0
FEATURE [Part::Part2DObjectPython] Line996  # Draft 2D object (typed FeaturePython)
  ChamferSize = 0
  Closed = false
  End = (223.25,-76,0)
  FilletRadius = 0
  Length = 23.75
  MakeFace = false
  Placement = pos=(199.5,-76,0) rot=(0,0,1;0rad)
  Points = (2) [(0,0,0),(23.75,0,0)]
  Start = (199.5,-76,0)
  Subdivisions = 0
FEATURE [Part::Part2DObjectPython] Arc516  # Draft 2D object (typed FeaturePython)
  FirstAngle = -90
  LastAngle = 0
  MakeFace = false
  Placement = pos=(217.875,-73,0) rot=(0,0,1;0rad)
  Radius = 0.5
FEATURE [Part::Part2DObjectPython] Line997  # Draft 2D object (typed FeaturePython)
  ChamferSize = 0
  Closed = false
  End = (223.25,-57,0)
  FilletRadius = 0
  Length = 23.75
  MakeFace = false
  Placement = pos=(199.5,-57,0) rot=(0,0,1;0rad)
  Points = (2) [(0,0,0),(23.75,0,0)]
  Start = (199.5,-57,0)
  Subdivisions = 0
FEATURE [Part::Part2DObjectPython] Line998  # Draft 2D object (typed FeaturePython)
  ChamferSize = 0
  Closed = false
  End = (204.375,-73,0)
  FilletRadius = 0
  Length = 13
  MakeFace = false
  Placement = pos=(204.375,-60,0) rot=(0,0,1;0rad)
  Points = (2) [(0,0,0),(0,-13,0)]
  Start = (204.375,-60,0)
  Subdivisions = 0
FEATURE [Part::Part2DObjectPython] Line999  # Draft 2D object (typed FeaturePython)
  ChamferSize = 0
  Closed = false
  End = (180.625,-73,0)
  FilletRadius = 0
  Length = 13
  MakeFace = false
  Placement = pos=(180.625,-60,0) rot=(0,0,1;0rad)
  Points = (2) [(0,0,0),(0,-13,0)]
  Start = (180.625,-60,0)
  Subdivisions = 0
FEATURE [Part::Part2DObjectPython] Line1000  # Draft 2D object (typed FeaturePython)
  ChamferSize = 0
  Closed = false
  End = (217.875,-59.5,0)
  FilletRadius = 0
  Length = 13
  MakeFace = false
  Placement = pos=(204.875,-59.5,0) rot=(0,0,1;0rad)
  Points = (2) [(0,0,0),(13,0,0)]
  Start = (204.875,-59.5,0)
  Subdivisions = 0
FEATURE [Part::Part2DObjectPython] Line1001  # Draft 2D object (typed FeaturePython)
  ChamferSize = 0
  Closed = false
  End = (175.75,-76,0)
  FilletRadius = 0
  Length = 19
  MakeFace = false
  Placement = pos=(175.75,-57,0) rot=(0,0,1;0rad)
  Points = (2) [(0,0,0),(0,-19,0)]
  Start = (175.75,-57,0)
  Subdivisions = 0
FEATURE [App::DocumentObjectGroup] Group126
  Group = -> [Line985,Line1001,Line992,Line989,Line993,Arc509,Arc512,Line999,Arc515,Line995,Line986,Arc513]
FEATURE [Part::Part2DObjectPython] Line1002  # Draft 2D object (typed FeaturePython)
  ChamferSize = 0
  Closed = false
  End = (218.375,-60,0)
  FilletRadius = 0
  Length = 13
  MakeFace = false
  Placement = pos=(218.375,-73,0) rot=(0,0,1;0rad)
  Points = (2) [(0,0,0),(0,13,0)]
  Start = (218.375,-73,0)
  Subdivisions = 0
FEATURE [Part::Part2DObjectPython] Arc517  # Draft 2D object (typed FeaturePython)
  FirstAngle = 90
  LastAngle = 180
  MakeFace = false
  Placement = pos=(204.875,-60,0) rot=(0,0,1;0rad)
  Radius = 0.5
FEATURE [Part::Part2DObjectPython] Arc518  # Draft 2D object (typed FeaturePython)
  FirstAngle = 0
  LastAngle = 90
  MakeFace = false
  Placement = pos=(217.875,-60,0) rot=(0,0,1;0rad)
  Radius = 0.5
FEATURE [Part::Part2DObjectPython] Arc519  # Draft 2D object (typed FeaturePython)
  FirstAngle = 180
  LastAngle = 270
  MakeFace = false
  Placement = pos=(204.875,-73,0) rot=(0,0,1;0rad)
  Radius = 0.5
FEATURE [Part::Part2DObjectPython] Line1003  # Draft 2D object (typed FeaturePython)
  ChamferSize = 0
  Closed = false
  End = (199.5,-76,0)
  FilletRadius = 0
  Length = 19
  MakeFace = false
  Placement = pos=(199.5,-57,0) rot=(0,0,1;0rad)
  Points = (2) [(0,0,0),(0,-19,0)]
  Start = (199.5,-57,0)
  Subdivisions = 0
FEATURE [Part::Part2DObjectPython] Line1004  # Draft 2D object (typed FeaturePython)
  ChamferSize = 0
  Closed = false
  End = (217.875,-73.5,0)
  FilletRadius = 0
  Length = 13
  MakeFace = false
  Placement = pos=(204.875,-73.5,0) rot=(0,0,1;0rad)
  Points = (2) [(0,0,0),(13,0,0)]
  Start = (204.875,-73.5,0)
  Subdivisions = 0
FEATURE [App::DocumentObjectGroup] Group106
  Group = -> [Line997,Line1003,Line996,Line994,Line1002,Arc518,Arc517,Line998,Arc519,Line1000,Line1004,Arc516]
FEATURE [Part::Part2DObjectPython] Arc520  # Draft 2D object (typed FeaturePython)
  FirstAngle = 90
  LastAngle = 180
  MakeFace = false
  Placement = pos=(52.875,-60,0) rot=(0,0,1;0rad)
  Radius = 0.5
FEATURE [Part::Part2DObjectPython] Line1005  # Draft 2D object (typed FeaturePython)
  ChamferSize = 0
  Closed = false
  End = (242.125,-60,0)
  FilletRadius = 0
  Length = 13
  MakeFace = false
  Placement = pos=(242.125,-73,0) rot=(0,0,1;0rad)
  Points = (2) [(0,0,0),(0,13,0)]
  Start = (242.125,-73,0)
  Subdivisions = 0
FEATURE [Part::Part2DObjectPython] Arc521  # Draft 2D object (typed FeaturePython)
  FirstAngle = -90
  LastAngle = 0
  MakeFace = false
  Placement = pos=(65.875,-73,0) rot=(0,0,1;0rad)
  Radius = 0.5
FEATURE [Part::Part2DObjectPython] Line1006  # Draft 2D object (typed FeaturePython)
  ChamferSize = 0
  Closed = false
  End = (241.625,-73.5,0)
  FilletRadius = 0
  Length = 13
  MakeFace = false
  Placement = pos=(228.625,-73.5,0) rot=(0,0,1;0rad)
  Points = (2) [(0,0,0),(13,0,0)]
  Start = (228.625,-73.5,0)
  Subdivisions = 0
FEATURE [Part::Part2DObjectPython] Line1007  # Draft 2D object (typed FeaturePython)
  ChamferSize = 0
  Closed = false
  End = (114,-76,0)
  FilletRadius = 0
  Length = 19
  MakeFace = false
  Placement = pos=(114,-57,0) rot=(0,0,1;0rad)
  Points = (2) [(0,0,0),(0,-19,0)]
  Start = (114,-57,0)
  Subdivisions = 0
FEATURE [Part::Part2DObjectPython] Line1008  # Draft 2D object (typed FeaturePython)
  ChamferSize = 0
  Closed = false
  End = (108.313,-56.5,0)
  FilletRadius = 0
  Length = 19.2
  MakeFace = false
  Placement = pos=(108.313,-75.7,0) rot=(0,0,1;3.14159rad)
  Points = (2) [(0,0,0),(0,-19.2,0)]
  Start = (108.313,-75.7,0)
  Subdivisions = 0
FEATURE [Part::Part2DObjectPython] Arc522  # Draft 2D object (typed FeaturePython)
  FirstAngle = 0
  LastAngle = 90
  MakeFace = false
  Placement = pos=(100.313,-74,0) rot=(0,0,1;0rad)
  Radius = 0.5
FEATURE [Part::Part2DObjectPython] Line1009  # Draft 2D object (typed FeaturePython)
  ChamferSize = 0
  Closed = false
  End = (100.813,-75.7,0)
  FilletRadius = 0
  Length = 1.7
  MakeFace = false
  Placement = pos=(100.813,-74,0) rot=(0,0,1;0rad)
  Points = (2) [(0,0,0),(0,-1.7,0)]
  Start = (100.813,-74,0)
  Subdivisions = 0
FEATURE [Part::Part2DObjectPython] Line1010  # Draft 2D object (typed FeaturePython)
  ChamferSize = 0
  Closed = false
  End = (114,-76,0)
  FilletRadius = 0
  Length = 42.75
  MakeFace = false
  Placement = pos=(71.25,-76,0) rot=(0,0,1;0rad)
  Points = (2) [(0,0,0),(42.75,0,0)]
  Start = (71.25,-76,0)
  Subdivisions = 0
FEATURE [Part::Part2DObjectPython] Arc523  # Draft 2D object (typed FeaturePython)
  FirstAngle = 180
  LastAngle = 270
  MakeFace = false
  Placement = pos=(77.437,-75.7,0) rot=(0,0,1;0rad)
  Radius = 0.5
FEATURE [Part::Part2DObjectPython] Arc524  # Draft 2D object (typed FeaturePython)
  FirstAngle = 90
  LastAngle = 180
  MakeFace = false
  Placement = pos=(228.625,-60,0) rot=(0,0,1;0rad)
  Radius = 0.5
FEATURE [Part::Part2DObjectPython] Line1011  # Draft 2D object (typed FeaturePython)
  ChamferSize = 0
  Closed = false
  End = (84.437,-74,0)
  FilletRadius = 0
  Length = 1.7
  MakeFace = false
  Placement = pos=(84.437,-75.7,0) rot=(0,0,1;0rad)
  Points = (2) [(0,0,0),(0,1.7,0)]
  Start = (84.437,-75.7,0)
  Subdivisions = 0
FEATURE [Part::Part2DObjectPython] Line1012  # Draft 2D object (typed FeaturePython)
  ChamferSize = 0
  Closed = false
  End = (52.375,-73,0)
  FilletRadius = 0
  Length = 13
  MakeFace = false
  Placement = pos=(52.375,-60,0) rot=(0,0,1;0rad)
  Points = (2) [(0,0,0),(0,-13,0)]
  Start = (52.375,-60,0)
  Subdivisions = 0
FEATURE [Part::Part2DObjectPython] Arc525  # Draft 2D object (typed FeaturePython)
  FirstAngle = 0
  LastAngle = 90
  MakeFace = false
  Placement = pos=(65.875,-60,0) rot=(0,0,1;0rad)
  Radius = 0.5
FEATURE [Part::Part2DObjectPython] Arc526  # Draft 2D object (typed FeaturePython)
  FirstAngle = 0
  LastAngle = 90
  MakeFace = false
  Placement = pos=(241.625,-60,0) rot=(0,0,1;0rad)
  Radius = 0.5
FEATURE [Part::Part2DObjectPython] Line1013  # Draft 2D object (typed FeaturePython)
  ChamferSize = 0
  Closed = false
  End = (71.25,-57,0)
  FilletRadius = 0
  Length = 19
  MakeFace = false
  Placement = pos=(71.25,-76,0) rot=(0,0,1;0rad)
  Points = (2) [(0,0,0),(0,19,0)]
  Start = (71.25,-76,0)
  Subdivisions = 0
FEATURE [Part::Part2DObjectPython] Line1014  # Draft 2D object (typed FeaturePython)
  ChamferSize = 0
  Closed = false
  End = (66.375,-60,0)
  FilletRadius = 0
  Length = 13
  MakeFace = false
  Placement = pos=(66.375,-73,0) rot=(0,0,1;0rad)
  Points = (2) [(0,0,0),(0,13,0)]
  Start = (66.375,-73,0)
  Subdivisions = 0
FEATURE [Part::Part2DObjectPython] Line1015  # Draft 2D object (typed FeaturePython)
  ChamferSize = 0
  Closed = false
  End = (247,-76,0)
  FilletRadius = 0
  Length = 23.75
  MakeFace = false
  Placement = pos=(223.25,-76,0) rot=(0,0,1;0rad)
  Points = (2) [(0,0,0),(23.75,0,0)]
  Start = (223.25,-76,0)
  Subdivisions = 0
FEATURE [Part::Part2DObjectPython] Line1016  # Draft 2D object (typed FeaturePython)
  ChamferSize = 0
  Closed = false
  End = (71.25,-57,0)
  FilletRadius = 0
  Length = 23.75
  MakeFace = false
  Placement = pos=(47.5,-57,0) rot=(0,0,1;0rad)
  Points = (2) [(0,0,0),(23.75,0,0)]
  Start = (47.5,-57,0)
  Subdivisions = 0
FEATURE [Part::Part2DObjectPython] Line1017  # Draft 2D object (typed FeaturePython)
  ChamferSize = 0
  Closed = false
  End = (223.25,-76,0)
  FilletRadius = 0
  Length = 19
  MakeFace = false
  Placement = pos=(223.25,-57,0) rot=(0,0,1;0rad)
  Points = (2) [(0,0,0),(0,-19,0)]
  Start = (223.25,-57,0)
  Subdivisions = 0
FEATURE [Part::Part2DObjectPython] Arc527  # Draft 2D object (typed FeaturePython)
  FirstAngle = 180
  LastAngle = 270
  MakeFace = false
  Placement = pos=(228.625,-73,0) rot=(0,0,1;0rad)
  Radius = 0.5
FEATURE [Part::Part2DObjectPython] Line1018  # Draft 2D object (typed FeaturePython)
  ChamferSize = 0
  Closed = false
  End = (47.5,-76,0)
  FilletRadius = 0
  Length = 19
  MakeFace = false
  Placement = pos=(47.5,-57,0) rot=(0,0,1;0rad)
  Points = (2) [(0,0,0),(0,-19,0)]
  Start = (47.5,-57,0)
  Subdivisions = 0
FEATURE [Part::Part2DObjectPython] Line1019  # Draft 2D object (typed FeaturePython)
  ChamferSize = 0
  Closed = false
  End = (228.125,-73,0)
  FilletRadius = 0
  Length = 13
  MakeFace = false
  Placement = pos=(228.125,-60,0) rot=(0,0,1;0rad)
  Points = (2) [(0,0,0),(0,-13,0)]
  Start = (228.125,-60,0)
  Subdivisions = 0
FEATURE [Part::Part2DObjectPython] Line1020  # Draft 2D object (typed FeaturePython)
  ChamferSize = 0
  Closed = false
  End = (65.875,-59.5,0)
  FilletRadius = 0
  Length = 13
  MakeFace = false
  Placement = pos=(52.875,-59.5,0) rot=(0,0,1;0rad)
  Points = (2) [(0,0,0),(13,0,0)]
  Start = (52.875,-59.5,0)
  Subdivisions = 0
FEATURE [Part::Part2DObjectPython] Line1021  # Draft 2D object (typed FeaturePython)
  ChamferSize = 0
  Closed = false
  End = (241.625,-59.5,0)
  FilletRadius = 0
  Length = 13
  MakeFace = false
  Placement = pos=(228.625,-59.5,0) rot=(0,0,1;0rad)
  Points = (2) [(0,0,0),(13,0,0)]
  Start = (228.625,-59.5,0)
  Subdivisions = 0
FEATURE [Part::Part2DObjectPython] Arc528  # Draft 2D object (typed FeaturePython)
  FirstAngle = -90
  LastAngle = 0
  MakeFace = false
  Placement = pos=(241.625,-73,0) rot=(0,0,1;0rad)
  Radius = 0.5
FEATURE [Part::Part2DObjectPython] Line1022  # Draft 2D object (typed FeaturePython)
  ChamferSize = 0
  Closed = false
  End = (65.875,-73.5,0)
  FilletRadius = 0
  Length = 13
  MakeFace = false
  Placement = pos=(52.875,-73.5,0) rot=(0,0,1;0rad)
  Points = (2) [(0,0,0),(13,0,0)]
  Start = (52.875,-73.5,0)
  Subdivisions = 0
FEATURE [Part::Part2DObjectPython] Line1023  # Draft 2D object (typed FeaturePython)
  ChamferSize = 0
  Closed = false
  End = (247,-57,0)
  FilletRadius = 0
  Length = 23.75
  MakeFace = false
  Placement = pos=(223.25,-57,0) rot=(0,0,1;0rad)
  Points = (2) [(0,0,0),(23.75,0,0)]
  Start = (223.25,-57,0)
  Subdivisions = 0
FEATURE [App::DocumentObjectGroup] Group127
  Group = -> [Line1023,Line1017,Line1015,Line987,Line1005,Arc526,Arc524,Line1019,Arc527,Line1021,Line1006,Arc528]
FEATURE [Part::Part2DObjectPython] Arc529  # Draft 2D object (typed FeaturePython)
  FirstAngle = 180
  LastAngle = 270
  MakeFace = false
  Placement = pos=(52.875,-73,0) rot=(0,0,1;0rad)
  Radius = 0.5
FEATURE [Part::Part2DObjectPython] Line1024  # Draft 2D object (typed FeaturePython)
  ChamferSize = 0
  Closed = false
  End = (71.25,-76,0)
  FilletRadius = 0
  Length = 23.75
  MakeFace = false
  Placement = pos=(47.5,-76,0) rot=(0,0,1;0rad)
  Points = (2) [(0,0,0),(23.75,0,0)]
  Start = (47.5,-76,0)
  Subdivisions = 0
FEATURE [App::DocumentObjectGroup] Group107
  Group = -> [Line1016,Line1018,Line1024,Line1013,Line1014,Arc525,Arc520,Line1012,Arc529,Line1020,Line1022,Arc521]
FEATURE [Part::Part2DObjectPython] Line1025  # Draft 2D object (typed FeaturePython)
  ChamferSize = 0
  Closed = false
  End = (114,-57,0)
  FilletRadius = 0
  Length = 42.75
  MakeFace = false
  Placement = pos=(71.25,-57,0) rot=(0,0,1;0rad)
  Points = (2) [(0,0,0),(42.75,0,0)]
  Start = (71.25,-57,0)
  Subdivisions = 0
FEATURE [Part::Part2DObjectPython] Line1026  # Draft 2D object (typed FeaturePython)
  ChamferSize = 0
  Closed = false
  End = (71.25,-76,0)
  FilletRadius = 0
  Length = 19
  MakeFace = false
  Placement = pos=(71.25,-57,0) rot=(0,0,1;0rad)
  Points = (2) [(0,0,0),(0,-19,0)]
  Start = (71.25,-57,0)
  Subdivisions = 0
FEATURE [Part::Part2DObjectPython] Line1027  # Draft 2D object (typed FeaturePython)
  ChamferSize = 0
  Closed = false
  End = (166.25,-76,0)
  FilletRadius = 0
  Length = 52.25
  MakeFace = false
  Placement = pos=(114,-76,0) rot=(0,0,1;0rad)
  Points = (2) [(0,0,0),(52.25,0,0)]
  Start = (114,-76,0)
  Subdivisions = 0
FEATURE [Part::Part2DObjectPython] Line1028  # Draft 2D object (typed FeaturePython)
  ChamferSize = 0
  Closed = false
  End = (100.313,-73.5,0)
  FilletRadius = 0
  Length = 15.376
  MakeFace = false
  Placement = pos=(84.937,-73.5,0) rot=(0,0,1;0rad)
  Points = (2) [(0,0,0),(15.376,0,0)]
  Start = (84.937,-73.5,0)
  Subdivisions = 0
FEATURE [Part::Part2DObjectPython] Arc530  # Draft 2D object (typed FeaturePython)
  FirstAngle = 180
  LastAngle = 270
  MakeFace = false
  Placement = pos=(124.937,-75.7,0) rot=(0,0,1;0rad)
  Radius = 0.5
FEATURE [Part::Part2DObjectPython] Arc531  # Draft 2D object (typed FeaturePython)
  FirstAngle = 90
  LastAngle = 180
  MakeFace = false
  Placement = pos=(132.437,-74,0) rot=(0,0,1;0rad)
  Radius = 0.5
FEATURE [Part::Part2DObjectPython] Line1029  # Draft 2D object (typed FeaturePython)
  ChamferSize = 0
  Closed = false
  End = (148.313,-75.7,0)
  FilletRadius = 0
  Length = 1.7
  MakeFace = false
  Placement = pos=(148.313,-74,0) rot=(0,0,1;0rad)
  Points = (2) [(0,0,0),(0,-1.7,0)]
  Start = (148.313,-74,0)
  Subdivisions = 0
FEATURE [Part::Part2DObjectPython] Arc532  # Draft 2D object (typed FeaturePython)
  FirstAngle = -90
  LastAngle = 0
  MakeFace = false
  Placement = pos=(83.937,-75.7,0) rot=(0,0,1;0rad)
  Radius = 0.5
FEATURE [Part::Part2DObjectPython] Line1030  # Draft 2D object (typed FeaturePython)
  ChamferSize = 0
  Closed = false
  End = (77.437,-56,0)
  FilletRadius = 0
  Length = 30.376
  MakeFace = false
  Placement = pos=(107.813,-56,0) rot=(0,0,1;0rad)
  Points = (2) [(0,0,0),(-30.376,0,0)]
  Start = (107.813,-56,0)
  Subdivisions = 0
FEATURE [Part::Part2DObjectPython] Line1031  # Draft 2D object (typed FeaturePython)
  ChamferSize = 0
  Closed = false
  End = (0,-76,0)
  FilletRadius = 0
  Length = 19
  MakeFace = false
  Placement = pos=(0,-57,0) rot=(0,0,1;0rad)
  Points = (2) [(0,0,0),(0,-19,0)]
  Start = (0,-57,0)
  Subdivisions = 0
FEATURE [Part::Part2DObjectPython] Arc533  # Draft 2D object (typed FeaturePython)
  FirstAngle = 90
  LastAngle = 180
  MakeFace = false
  Placement = pos=(84.937,-74,0) rot=(0,0,1;0rad)
  Radius = 0.5
FEATURE [Part::Part2DObjectPython] Line1032  # Draft 2D object (typed FeaturePython)
  ChamferSize = 0
  Closed = false
  End = (155.813,-56.5,0)
  FilletRadius = 0
  Length = 19.2
  MakeFace = false
  Placement = pos=(155.813,-75.7,0) rot=(0,0,1;3.14159rad)
  Points = (2) [(0,0,0),(0,-19.2,0)]
  Start = (155.813,-75.7,0)
  Subdivisions = 0
FEATURE [Part::Part2DObjectPython] Line1033  # Draft 2D object (typed FeaturePython)
  ChamferSize = 0
  Closed = false
  End = (131.937,-74,0)
  FilletRadius = 0
  Length = 1.7
  MakeFace = false
  Placement = pos=(131.937,-75.7,0) rot=(0,0,1;0rad)
  Points = (2) [(0,0,0),(0,1.7,0)]
  Start = (131.937,-75.7,0)
  Subdivisions = 0
FEATURE [Part::Part2DObjectPython] Line1034  # Draft 2D object (typed FeaturePython)
  ChamferSize = 0
  Closed = false
  End = (147.813,-73.5,0)
  FilletRadius = 0
  Length = 15.376
  MakeFace = false
  Placement = pos=(132.437,-73.5,0) rot=(0,0,1;0rad)
  Points = (2) [(0,0,0),(15.376,0,0)]
  Start = (132.437,-73.5,0)
  Subdivisions = 0
FEATURE [Part::Part2DObjectPython] Line1035  # Draft 2D object (typed FeaturePython)
  ChamferSize = 0
  Closed = false
  End = (124.937,-56,0)
  FilletRadius = 0
  Length = 30.376
  MakeFace = false
  Placement = pos=(155.313,-56,0) rot=(0,0,1;0rad)
  Points = (2) [(0,0,0),(-30.376,0,0)]
  Start = (155.313,-56,0)
  Subdivisions = 0
FEATURE [Part::Part2DObjectPython] Arc534  # Draft 2D object (typed FeaturePython)
  FirstAngle = -90
  LastAngle = 0
  MakeFace = false
  Placement = pos=(155.313,-75.7,0) rot=(0,0,1;0rad)
  Radius = 0.5
FEATURE [Part::Part2DObjectPython] Arc535  # Draft 2D object (typed FeaturePython)
  FirstAngle = 180
  LastAngle = 270
  MakeFace = false
  Placement = pos=(148.813,-75.7,0) rot=(0,0,1;0rad)
  Radius = 0.5
FEATURE [Part::Part2DObjectPython] Line1036  # Draft 2D object (typed FeaturePython)
  ChamferSize = 0
  Closed = false
  End = (166.25,-57,0)
  FilletRadius = 0
  Length = 52.25
  MakeFace = false
  Placement = pos=(114,-57,0) rot=(0,0,1;0rad)
  Points = (2) [(0,0,0),(52.25,0,0)]
  Start = (114,-57,0)
  Subdivisions = 0
FEATURE [Part::Part2DObjectPython] Arc536  # Draft 2D object (typed FeaturePython)
  FirstAngle = 90
  LastAngle = 180
  MakeFace = false
  Placement = pos=(77.437,-56.5,0) rot=(0,0,1;0rad)
  Radius = 0.5
FEATURE [Part::Part2DObjectPython] Arc537  # Draft 2D object (typed FeaturePython)
  FirstAngle = 0
  LastAngle = 90
  MakeFace = false
  Placement = pos=(107.813,-56.5,0) rot=(0,0,1;0rad)
  Radius = 0.5
FEATURE [Part::Part2DObjectPython] Line1037  # Draft 2D object (typed FeaturePython)
  ChamferSize = 0
  Closed = false
  End = (131.437,-76.2,0)
  FilletRadius = 0
  Length = 6.5
  MakeFace = false
  Placement = pos=(124.937,-76.2,0) rot=(0,0,1;0rad)
  Points = (2) [(0,0,0),(6.5,0,0)]
  Start = (124.937,-76.2,0)
  Subdivisions = 0
FEATURE [Part::Part2DObjectPython] Line1038  # Draft 2D object (typed FeaturePython)
  ChamferSize = 0
  Closed = false
  End = (18.875,-60,0)
  FilletRadius = 0
  Length = 13
  MakeFace = false
  Placement = pos=(18.875,-73,0) rot=(0,0,1;0rad)
  Points = (2) [(0,0,0),(0,13,0)]
  Start = (18.875,-73,0)
  Subdivisions = 0
FEATURE [Part::Part2DObjectPython] Arc538  # Draft 2D object (typed FeaturePython)
  FirstAngle = -90
  LastAngle = 0
  MakeFace = false
  Placement = pos=(131.437,-75.7,0) rot=(0,0,1;0rad)
  Radius = 0.5
FEATURE [Part::Part2DObjectPython] Arc539  # Draft 2D object (typed FeaturePython)
  FirstAngle = 0
  LastAngle = 90
  MakeFace = false
  Placement = pos=(18.375,-60,0) rot=(0,0,1;0rad)
  Radius = 0.5
FEATURE [Part::Part2DObjectPython] Arc540  # Draft 2D object (typed FeaturePython)
  FirstAngle = -90
  LastAngle = 0
  MakeFace = false
  Placement = pos=(107.813,-75.7,0) rot=(0,0,1;0rad)
  Radius = 0.5
FEATURE [Part::Part2DObjectPython] Line1039  # Draft 2D object (typed FeaturePython)
  ChamferSize = 0
  Closed = false
  End = (76.937,-75.7,0)
  FilletRadius = 0
  Length = 19.2
  MakeFace = false
  Placement = pos=(76.937,-56.5,0) rot=(0,0,1;0rad)
  Points = (2) [(0,0,0),(4.26326e-14,-19.2,0)]
  Start = (76.937,-56.5,0)
  Subdivisions = 0
FEATURE [Part::Part2DObjectPython] Line1040  # Draft 2D object (typed FeaturePython)
  ChamferSize = 0
  Closed = false
  End = (107.813,-76.2,0)
  FilletRadius = 0
  Length = 6.5
  MakeFace = false
  Placement = pos=(101.313,-76.2,0) rot=(0,0,1;0rad)
  Points = (2) [(0,0,0),(6.5,0,0)]
  Start = (101.313,-76.2,0)
  Subdivisions = 0
FEATURE [Part::Part2DObjectPython] Arc541  # Draft 2D object (typed FeaturePython)
  FirstAngle = 180
  LastAngle = 270
  MakeFace = false
  Placement = pos=(101.313,-75.7,0) rot=(0,0,1;0rad)
  Radius = 0.5
FEATURE [Part::Part2DObjectPython] Line1041  # Draft 2D object (typed FeaturePython)
  ChamferSize = 0
  Closed = false
  End = (83.937,-76.2,0)
  FilletRadius = 0
  Length = 6.5
  MakeFace = false
  Placement = pos=(77.437,-76.2,0) rot=(0,0,1;0rad)
  Points = (2) [(0,0,0),(6.5,0,0)]
  Start = (77.437,-76.2,0)
  Subdivisions = 0
FEATURE [App::DocumentObjectGroup] Group108  label="2.25u space001"
  Group = -> [Line1025,Line1026,Line1010,Line1007,Line1008,Arc522,Line1009,Line1011,Arc523,Arc540,Line1030,Line1041,Arc537,Line1039,Line1028,Line1040,Arc541,Arc532,Arc536,Arc533]
FEATURE [Part::Part2DObjectPython] Line1042  # Draft 2D object (typed FeaturePython)
  ChamferSize = 0
  Closed = false
  End = (114,-76,0)
  FilletRadius = 0
  Length = 19
  MakeFace = false
  Placement = pos=(114,-57,0) rot=(0,0,1;0rad)
  Points = (2) [(0,0,0),(0,-19,0)]
  Start = (114,-57,0)
  Subdivisions = 0
FEATURE [Part::Part2DObjectPython] Line1043  # Draft 2D object (typed FeaturePython)
  ChamferSize = 0
  Closed = false
  End = (166.25,-76,0)
  FilletRadius = 0
  Length = 19
  MakeFace = false
  Placement = pos=(166.25,-57,0) rot=(0,0,1;0rad)
  Points = (2) [(0,0,0),(0,-19,0)]
  Start = (166.25,-57,0)
  Subdivisions = 0
FEATURE [Part::Part2DObjectPython] Arc542  # Draft 2D object (typed FeaturePython)
  FirstAngle = 0
  LastAngle = 90
  MakeFace = false
  Placement = pos=(147.813,-74,0) rot=(0,0,1;0rad)
  Radius = 0.5
FEATURE [Part::Part2DObjectPython] Arc543  # Draft 2D object (typed FeaturePython)
  FirstAngle = 0
  LastAngle = 90
  MakeFace = false
  Placement = pos=(155.313,-56.5,0) rot=(0,0,1;0rad)
  Radius = 0.5
FEATURE [Part::Part2DObjectPython] Arc544  # Draft 2D object (typed FeaturePython)
  FirstAngle = 90
  LastAngle = 180
  MakeFace = false
  Placement = pos=(124.937,-56.5,0) rot=(0,0,1;0rad)
  Radius = 0.5
FEATURE [Part::Part2DObjectPython] Line1044  # Draft 2D object (typed FeaturePython)
  ChamferSize = 0
  Closed = false
  End = (124.437,-75.7,0)
  FilletRadius = 0
  Length = 19.2
  MakeFace = false
  Placement = pos=(124.437,-56.5,0) rot=(0,0,1;0rad)
  Points = (2) [(0,0,0),(5.68434e-14,-19.2,0)]
  Start = (124.437,-56.5,0)
  Subdivisions = 0
FEATURE [Part::Part2DObjectPython] Line1045  # Draft 2D object (typed FeaturePython)
  ChamferSize = 0
  Closed = false
  End = (155.313,-76.2,0)
  FilletRadius = 0
  Length = 6.5
  MakeFace = false
  Placement = pos=(148.813,-76.2,0) rot=(0,0,1;0rad)
  Points = (2) [(0,0,0),(6.5,0,0)]
  Start = (148.813,-76.2,0)
  Subdivisions = 0
FEATURE [App::DocumentObjectGroup] Group112  label="2.75u space001"
  Group = -> [Line1036,Line1042,Line1027,Line1043,Arc531,Line1032,Arc542,Line1029,Arc530,Line1033,Line1034,Arc538,Line1035,Arc544,Arc543,Arc534,Line1044,Line1045,Arc535,Line1037]
FEATURE [Part::Part2DObjectPython] Line1046  # Draft 2D object (typed FeaturePython)
  ChamferSize = 0
  Closed = false
  End = (23.75,-57,0)
  FilletRadius = 0
  Length = 23.75
  MakeFace = false
  Placement = pos=(0,-57,0) rot=(0,0,1;0rad)
  Points = (2) [(0,0,0),(23.75,0,0)]
  Start = (0,-57,0)
  Subdivisions = 0
FEATURE [Part::Part2DObjectPython] Line1047  # Draft 2D object (typed FeaturePython)
  ChamferSize = 0
  Closed = false
  End = (182.25,-59.5,0)
  FilletRadius = 0
  Length = 13
  MakeFace = false
  Placement = pos=(169.25,-59.5,0) rot=(0,0,1;0rad)
  Points = (2) [(0,0,0),(13,0,0)]
  Start = (169.25,-59.5,0)
  Subdivisions = 0
FEATURE [Part::Part2DObjectPython] Line1048  # Draft 2D object (typed FeaturePython)
  ChamferSize = 0
  Closed = false
  End = (168.75,-73,0)
  FilletRadius = 0
  Length = 13
  MakeFace = false
  Placement = pos=(168.75,-60,0) rot=(0,0,1;0rad)
  Points = (2) [(0,0,0),(0,-13,0)]
  Start = (168.75,-60,0)
  Subdivisions = 0
FEATURE [Part::Part2DObjectPython] Line1049  # Draft 2D object (typed FeaturePython)
  ChamferSize = 0
  Closed = false
  End = (201.25,-73.5,0)
  FilletRadius = 0
  Length = 13
  MakeFace = false
  Placement = pos=(188.25,-73.5,0) rot=(0,0,1;0rad)
  Points = (2) [(0,0,0),(13,0,0)]
  Start = (188.25,-73.5,0)
  Subdivisions = 0
FEATURE [Part::Part2DObjectPython] Arc545  # Draft 2D object (typed FeaturePython)
  FirstAngle = 0
  LastAngle = 90
  MakeFace = false
  Placement = pos=(201.25,-60,0) rot=(0,0,1;0rad)
  Radius = 0.5
FEATURE [Part::Part2DObjectPython] Line1050  # Draft 2D object (typed FeaturePython)
  ChamferSize = 0
  Closed = false
  End = (204.25,-76,0)
  FilletRadius = 0
  Length = 19
  MakeFace = false
  Placement = pos=(204.25,-57,0) rot=(0,0,1;0rad)
  Points = (2) [(0,0,0),(0,-19,0)]
  Start = (204.25,-57,0)
  Subdivisions = 0
FEATURE [Part::Part2DObjectPython] Line1051  # Draft 2D object (typed FeaturePython)
  ChamferSize = 0
  Closed = false
  End = (204.25,-57,0)
  FilletRadius = 0
  Length = 19
  MakeFace = false
  Placement = pos=(185.25,-57,0) rot=(0,0,1;0rad)
  Points = (2) [(0,0,0),(19,0,0)]
  Start = (185.25,-57,0)
  Subdivisions = 0
FEATURE [Part::Part2DObjectPython] Line1052  # Draft 2D object (typed FeaturePython)
  ChamferSize = 0
  Closed = false
  End = (182.25,-73.5,0)
  FilletRadius = 0
  Length = 13
  MakeFace = false
  Placement = pos=(169.25,-73.5,0) rot=(0,0,1;0rad)
  Points = (2) [(0,0,0),(13,0,0)]
  Start = (169.25,-73.5,0)
  Subdivisions = 0
FEATURE [Part::Part2DObjectPython] Arc546  # Draft 2D object (typed FeaturePython)
  FirstAngle = -90
  LastAngle = 0
  MakeFace = false
  Placement = pos=(201.25,-73,0) rot=(0,0,1;0rad)
  Radius = 0.5
FEATURE [Part::Part2DObjectPython] Arc547  # Draft 2D object (typed FeaturePython)
  FirstAngle = 0
  LastAngle = 90
  MakeFace = false
  Placement = pos=(182.25,-60,0) rot=(0,0,1;0rad)
  Radius = 0.5
FEATURE [Part::Part2DObjectPython] Line1053  # Draft 2D object (typed FeaturePython)
  ChamferSize = 0
  Closed = false
  End = (187.75,-73,0)
  FilletRadius = 0
  Length = 13
  MakeFace = false
  Placement = pos=(187.75,-60,0) rot=(0,0,1;0rad)
  Points = (2) [(0,0,0),(0,-13,0)]
  Start = (187.75,-60,0)
  Subdivisions = 0
FEATURE [Part::Part2DObjectPython] Line1054  # Draft 2D object (typed FeaturePython)
  ChamferSize = 0
  Closed = false
  End = (185.25,-57,0)
  FilletRadius = 0
  Length = 19
  MakeFace = false
  Placement = pos=(166.25,-57,0) rot=(0,0,1;0rad)
  Points = (2) [(0,0,0),(19,0,0)]
  Start = (166.25,-57,0)
  Subdivisions = 0
FEATURE [Part::Part2DObjectPython] Line1055  # Draft 2D object (typed FeaturePython)
  ChamferSize = 0
  Closed = false
  End = (182.75,-60,0)
  FilletRadius = 0
  Length = 13
  MakeFace = false
  Placement = pos=(182.75,-73,0) rot=(0,0,1;0rad)
  Points = (2) [(0,0,0),(0,13,0)]
  Start = (182.75,-73,0)
  Subdivisions = 0
FEATURE [Part::Part2DObjectPython] Line1056  # Draft 2D object (typed FeaturePython)
  ChamferSize = 0
  Closed = false
  End = (201.75,-60,0)
  FilletRadius = 0
  Length = 13
  MakeFace = false
  Placement = pos=(201.75,-73,0) rot=(0,0,1;0rad)
  Points = (2) [(0,0,0),(0,13,0)]
  Start = (201.75,-73,0)
  Subdivisions = 0
FEATURE [Part::Part2DObjectPython] Arc548  # Draft 2D object (typed FeaturePython)
  FirstAngle = -90
  LastAngle = 0
  MakeFace = false
  Placement = pos=(182.25,-73,0) rot=(0,0,1;0rad)
  Radius = 0.5
FEATURE [Part::Part2DObjectPython] Line1057  # Draft 2D object (typed FeaturePython)
  ChamferSize = 0
  Closed = false
  End = (166.25,-76,0)
  FilletRadius = 0
  Length = 19
  MakeFace = false
  Placement = pos=(185.25,-76,0) rot=(0,0,1;0rad)
  Points = (2) [(0,0,0),(-19,0,0)]
  Start = (185.25,-76,0)
  Subdivisions = 0
FEATURE [Part::Part2DObjectPython] Arc549  # Draft 2D object (typed FeaturePython)
  FirstAngle = 180
  LastAngle = 270
  MakeFace = false
  Placement = pos=(169.25,-73,0) rot=(0,0,1;0rad)
  Radius = 0.5
FEATURE [Part::Part2DObjectPython] Line1058  # Draft 2D object (typed FeaturePython)
  ChamferSize = 0
  Closed = false
  End = (23.75,-57,0)
  FilletRadius = 0
  Length = 19
  MakeFace = false
  Placement = pos=(23.75,-76,0) rot=(0,0,1;0rad)
  Points = (2) [(0,0,0),(0,19,0)]
  Start = (23.75,-76,0)
  Subdivisions = 0
FEATURE [Part::Part2DObjectPython] Line1059  # Draft 2D object (typed FeaturePython)
  ChamferSize = 0
  Closed = false
  End = (4.875,-73,0)
  FilletRadius = 0
  Length = 13
  MakeFace = false
  Placement = pos=(4.875,-60,0) rot=(0,0,1;0rad)
  Points = (2) [(0,0,0),(0,-13,0)]
  Start = (4.875,-60,0)
  Subdivisions = 0
FEATURE [Part::Part2DObjectPython] Arc550  # Draft 2D object (typed FeaturePython)
  FirstAngle = 90
  LastAngle = 180
  MakeFace = false
  Placement = pos=(188.25,-60,0) rot=(0,0,1;0rad)
  Radius = 0.5
FEATURE [Part::Part2DObjectPython] Line1060  # Draft 2D object (typed FeaturePython)
  ChamferSize = 0
  Closed = false
  End = (185.25,-76,0)
  FilletRadius = 0
  Length = 19
  MakeFace = false
  Placement = pos=(185.25,-57,0) rot=(0,0,1;0rad)
  Points = (2) [(0,0,0),(0,-19,0)]
  Start = (185.25,-57,0)
  Subdivisions = 0
FEATURE [Part::Part2DObjectPython] Arc551  # Draft 2D object (typed FeaturePython)
  FirstAngle = 180
  LastAngle = 270
  MakeFace = false
  Placement = pos=(5.375,-73,0) rot=(0,0,1;0rad)
  Radius = 0.5
FEATURE [Part::Part2DObjectPython] Line1061  # Draft 2D object (typed FeaturePython)
  ChamferSize = 0
  Closed = false
  End = (18.375,-59.5,0)
  FilletRadius = 0
  Length = 13
  MakeFace = false
  Placement = pos=(5.375,-59.5,0) rot=(0,0,1;0rad)
  Points = (2) [(0,0,0),(13,0,0)]
  Start = (5.375,-59.5,0)
  Subdivisions = 0
FEATURE [Part::Part2DObjectPython] Arc552  # Draft 2D object (typed FeaturePython)
  FirstAngle = 90
  LastAngle = 180
  MakeFace = false
  Placement = pos=(5.375,-60,0) rot=(0,0,1;0rad)
  Radius = 0.5
FEATURE [Part::Part2DObjectPython] Arc553  # Draft 2D object (typed FeaturePython)
  FirstAngle = 180
  LastAngle = 270
  MakeFace = false
  Placement = pos=(188.25,-73,0) rot=(0,0,1;0rad)
  Radius = 0.5
FEATURE [Part::Part2DObjectPython] Arc554  # Draft 2D object (typed FeaturePython)
  FirstAngle = 90
  LastAngle = 180
  MakeFace = false
  Placement = pos=(169.25,-60,0) rot=(0,0,1;0rad)
  Radius = 0.5
FEATURE [Part::Part2DObjectPython] Line1062  # Draft 2D object (typed FeaturePython)
  ChamferSize = 0
  Closed = false
  End = (201.25,-59.5,0)
  FilletRadius = 0
  Length = 13
  MakeFace = false
  Placement = pos=(188.25,-59.5,0) rot=(0,0,1;0rad)
  Points = (2) [(0,0,0),(13,0,0)]
  Start = (188.25,-59.5,0)
  Subdivisions = 0
FEATURE [Part::Part2DObjectPython] Line1063  # Draft 2D object (typed FeaturePython)
  ChamferSize = 0
  Closed = false
  End = (185.25,-76,0)
  FilletRadius = 0
  Length = 19
  MakeFace = false
  Placement = pos=(204.25,-76,0) rot=(0,0,1;0rad)
  Points = (2) [(0,0,0),(-19,0,0)]
  Start = (204.25,-76,0)
  Subdivisions = 0
FEATURE [App::DocumentObjectGroup] Group122
  Group = -> [Line1051,Line1050,Line1063,Line1060,Line1062,Arc545,Arc550,Line1053,Arc553,Line1049,Arc546,Line1056]
FEATURE [Part::Part2DObjectPython] Line1064  # Draft 2D object (typed FeaturePython)
  ChamferSize = 0
  Closed = false
  End = (185.25,-76,0)
  FilletRadius = 0
  Length = 19
  MakeFace = false
  Placement = pos=(185.25,-57,0) rot=(0,0,1;0rad)
  Points = (2) [(0,0,0),(0,-19,0)]
  Start = (185.25,-57,0)
  Subdivisions = 0
FEATURE [Part::Part2DObjectPython] Line1065  # Draft 2D object (typed FeaturePython)
  ChamferSize = 0
  Closed = false
  End = (166.25,-76,0)
  FilletRadius = 0
  Length = 19
  MakeFace = false
  Placement = pos=(166.25,-57,0) rot=(0,0,1;0rad)
  Points = (2) [(0,0,0),(0,-19,0)]
  Start = (166.25,-57,0)
  Subdivisions = 0
FEATURE [App::DocumentObjectGroup] Group113
  Group = -> [Line1054,Line1064,Line1057,Line1065,Line1047,Arc547,Arc554,Line1048,Arc549,Line1052,Arc548,Line1055]
FEATURE [Part::Part2DObjectPython] Line1066  # Draft 2D object (typed FeaturePython)
  ChamferSize = 0
  Closed = false
  End = (39.75,-73.5,0)
  FilletRadius = 0
  Length = 13
  MakeFace = false
  Placement = pos=(26.75,-73.5,0) rot=(0,0,1;0rad)
  Points = (2) [(0,0,0),(13,0,0)]
  Start = (26.75,-73.5,0)
  Subdivisions = 0
FEATURE [Part::Part2DObjectPython] Line1067  # Draft 2D object (typed FeaturePython)
  ChamferSize = 0
  Closed = false
  End = (40.25,-60,0)
  FilletRadius = 0
  Length = 13
  MakeFace = false
  Placement = pos=(40.25,-73,0) rot=(0,0,1;0rad)
  Points = (2) [(0,0,0),(0,13,0)]
  Start = (40.25,-73,0)
  Subdivisions = 0
FEATURE [Part::Part2DObjectPython] Line1068  # Draft 2D object (typed FeaturePython)
  ChamferSize = 0
  Closed = false
  End = (220.25,-73.5,0)
  FilletRadius = 0
  Length = 13
  MakeFace = false
  Placement = pos=(207.25,-73.5,0) rot=(0,0,1;0rad)
  Points = (2) [(0,0,0),(13,0,0)]
  Start = (207.25,-73.5,0)
  Subdivisions = 0
FEATURE [Part::Part2DObjectPython] Line1069  # Draft 2D object (typed FeaturePython)
  ChamferSize = 0
  Closed = false
  End = (42.75,-76,0)
  FilletRadius = 0
  Length = 19
  MakeFace = false
  Placement = pos=(42.75,-57,0) rot=(0,0,1;0rad)
  Points = (2) [(0,0,0),(0,-19,0)]
  Start = (42.75,-57,0)
  Subdivisions = 0
FEATURE [Part::Part2DObjectPython] Line1070  # Draft 2D object (typed FeaturePython)
  ChamferSize = 0
  Closed = false
  End = (42.75,-76,0)
  FilletRadius = 0
  Length = 19
  MakeFace = false
  Placement = pos=(42.75,-57,0) rot=(0,0,1;0rad)
  Points = (2) [(0,0,0),(0,-19,0)]
  Start = (42.75,-57,0)
  Subdivisions = 0
FEATURE [Part::Part2DObjectPython] Arc555  # Draft 2D object (typed FeaturePython)
  FirstAngle = -90
  LastAngle = 0
  MakeFace = false
  Placement = pos=(18.375,-73,0) rot=(0,0,1;0rad)
  Radius = 0.5
FEATURE [Part::Part2DObjectPython] Line1071  # Draft 2D object (typed FeaturePython)
  ChamferSize = 0
  Closed = false
  End = (206.75,-73,0)
  FilletRadius = 0
  Length = 13
  MakeFace = false
  Placement = pos=(206.75,-60,0) rot=(0,0,1;0rad)
  Points = (2) [(0,0,0),(0,-13,0)]
  Start = (206.75,-60,0)
  Subdivisions = 0
FEATURE [Part::Part2DObjectPython] Line1072  # Draft 2D object (typed FeaturePython)
  ChamferSize = 0
  Closed = false
  End = (220.75,-60,0)
  FilletRadius = 0
  Length = 13
  MakeFace = false
  Placement = pos=(220.75,-73,0) rot=(0,0,1;0rad)
  Points = (2) [(0,0,0),(0,13,0)]
  Start = (220.75,-73,0)
  Subdivisions = 0
FEATURE [Part::Part2DObjectPython] Arc556  # Draft 2D object (typed FeaturePython)
  FirstAngle = 90
  LastAngle = 180
  MakeFace = false
  Placement = pos=(207.25,-60,0) rot=(0,0,1;0rad)
  Radius = 0.5
FEATURE [Part::Part2DObjectPython] Line1073  # Draft 2D object (typed FeaturePython)
  ChamferSize = 0
  Closed = false
  End = (204.25,-76,0)
  FilletRadius = 0
  Length = 19
  MakeFace = false
  Placement = pos=(204.25,-57,0) rot=(0,0,1;0rad)
  Points = (2) [(0,0,0),(0,-19,0)]
  Start = (204.25,-57,0)
  Subdivisions = 0
FEATURE [Part::Part2DObjectPython] Line1074  # Draft 2D object (typed FeaturePython)
  ChamferSize = 0
  Closed = false
  End = (204.25,-76,0)
  FilletRadius = 0
  Length = 19
  MakeFace = false
  Placement = pos=(223.25,-76,0) rot=(0,0,1;0rad)
  Points = (2) [(0,0,0),(-19,0,0)]
  Start = (223.25,-76,0)
  Subdivisions = 0
FEATURE [Part::Part2DObjectPython] Arc557  # Draft 2D object (typed FeaturePython)
  FirstAngle = 180
  LastAngle = 270
  MakeFace = false
  Placement = pos=(207.25,-73,0) rot=(0,0,1;0rad)
  Radius = 0.5
FEATURE [Part::Part2DObjectPython] Line1075  # Draft 2D object (typed FeaturePython)
  ChamferSize = 0
  Closed = false
  End = (39.75,-59.5,0)
  FilletRadius = 0
  Length = 13
  MakeFace = false
  Placement = pos=(26.75,-59.5,0) rot=(0,0,1;0rad)
  Points = (2) [(0,0,0),(13,0,0)]
  Start = (26.75,-59.5,0)
  Subdivisions = 0
FEATURE [Part::Part2DObjectPython] Line1076  # Draft 2D object (typed FeaturePython)
  ChamferSize = 0
  Closed = false
  End = (42.75,-57,0)
  FilletRadius = 0
  Length = 19
  MakeFace = false
  Placement = pos=(23.75,-57,0) rot=(0,0,1;0rad)
  Points = (2) [(0,0,0),(19,0,0)]
  Start = (23.75,-57,0)
  Subdivisions = 0
FEATURE [Part::Part2DObjectPython] Line1077  # Draft 2D object (typed FeaturePython)
  ChamferSize = 0
  Closed = false
  End = (23.75,-76,0)
  FilletRadius = 0
  Length = 19
  MakeFace = false
  Placement = pos=(23.75,-57,0) rot=(0,0,1;0rad)
  Points = (2) [(0,0,0),(0,-19,0)]
  Start = (23.75,-57,0)
  Subdivisions = 0
FEATURE [Part::Part2DObjectPython] Arc558  # Draft 2D object (typed FeaturePython)
  FirstAngle = 0
  LastAngle = 90
  MakeFace = false
  Placement = pos=(39.75,-60,0) rot=(0,0,1;0rad)
  Radius = 0.5
FEATURE [Part::Part2DObjectPython] Arc559  # Draft 2D object (typed FeaturePython)
  FirstAngle = -90
  LastAngle = 0
  MakeFace = false
  Placement = pos=(220.25,-73,0) rot=(0,0,1;0rad)
  Radius = 0.5
FEATURE [Part::Part2DObjectPython] Arc560  # Draft 2D object (typed FeaturePython)
  FirstAngle = 90
  LastAngle = 180
  MakeFace = false
  Placement = pos=(26.75,-60,0) rot=(0,0,1;0rad)
  Radius = 0.5
FEATURE [Part::Part2DObjectPython] Arc561  # Draft 2D object (typed FeaturePython)
  FirstAngle = 0
  LastAngle = 90
  MakeFace = false
  Placement = pos=(220.25,-60,0) rot=(0,0,1;0rad)
  Radius = 0.5
FEATURE [Part::Part2DObjectPython] Line1078  # Draft 2D object (typed FeaturePython)
  ChamferSize = 0
  Closed = false
  End = (23.75,-76,0)
  FilletRadius = 0
  Length = 23.75
  MakeFace = false
  Placement = pos=(0,-76,0) rot=(0,0,1;0rad)
  Points = (2) [(0,0,0),(23.75,0,0)]
  Start = (0,-76,0)
  Subdivisions = 0
FEATURE [Part::Part2DObjectPython] Line1079  # Draft 2D object (typed FeaturePython)
  ChamferSize = 0
  Closed = false
  End = (18.375,-73.5,0)
  FilletRadius = 0
  Length = 13
  MakeFace = false
  Placement = pos=(5.375,-73.5,0) rot=(0,0,1;0rad)
  Points = (2) [(0,0,0),(13,0,0)]
  Start = (5.375,-73.5,0)
  Subdivisions = 0
FEATURE [App::DocumentObjectGroup] Group121
  Group = -> [Line1046,Line1031,Line1078,Line1058,Line1038,Arc539,Arc552,Line1059,Arc551,Line1061,Line1079,Arc555]
FEATURE [Part::Part2DObjectPython] Line1080  # Draft 2D object (typed FeaturePython)
  ChamferSize = 0
  Closed = false
  End = (223.25,-57,0)
  FilletRadius = 0
  Length = 19
  MakeFace = false
  Placement = pos=(204.25,-57,0) rot=(0,0,1;0rad)
  Points = (2) [(0,0,0),(19,0,0)]
  Start = (204.25,-57,0)
  Subdivisions = 0
FEATURE [Part::Part2DObjectPython] Line1081  # Draft 2D object (typed FeaturePython)
  ChamferSize = 0
  Closed = false
  End = (26.25,-73,0)
  FilletRadius = 0
  Length = 13
  MakeFace = false
  Placement = pos=(26.25,-60,0) rot=(0,0,1;0rad)
  Points = (2) [(0,0,0),(0,-13,0)]
  Start = (26.25,-60,0)
  Subdivisions = 0
FEATURE [Part::Part2DObjectPython] Line1082  # Draft 2D object (typed FeaturePython)
  ChamferSize = 0
  Closed = false
  End = (220.25,-59.5,0)
  FilletRadius = 0
  Length = 13
  MakeFace = false
  Placement = pos=(207.25,-59.5,0) rot=(0,0,1;0rad)
  Points = (2) [(0,0,0),(13,0,0)]
  Start = (207.25,-59.5,0)
  Subdivisions = 0
FEATURE [Part::Part2DObjectPython] Line1083  # Draft 2D object (typed FeaturePython)
  ChamferSize = 0
  Closed = false
  End = (223.25,-76,0)
  FilletRadius = 0
  Length = 19
  MakeFace = false
  Placement = pos=(223.25,-57,0) rot=(0,0,1;0rad)
  Points = (2) [(0,0,0),(0,-19,0)]
  Start = (223.25,-57,0)
  Subdivisions = 0
FEATURE [App::DocumentObjectGroup] Group128
  Group = -> [Line1080,Line1083,Line1074,Line1073,Line1082,Arc561,Arc556,Line1071,Arc557,Line1068,Arc559,Line1072]
FEATURE [App::DocumentObjectGroup] Group120  label="split 004"
  Group = -> [Group107,Group108,Group112,Group113,Group122,Group128]
FEATURE [Part::Part2DObjectPython] Line1084  # Draft 2D object (typed FeaturePython)
  ChamferSize = 0
  Closed = false
  End = (23.75,-76,0)
  FilletRadius = 0
  Length = 19
  MakeFace = false
  Placement = pos=(42.75,-76,0) rot=(0,0,1;0rad)
  Points = (2) [(0,0,0),(-19,0,0)]
  Start = (42.75,-76,0)
  Subdivisions = 0
FEATURE [Part::Part2DObjectPython] Arc562  # Draft 2D object (typed FeaturePython)
  FirstAngle = 180
  LastAngle = 270
  MakeFace = false
  Placement = pos=(26.75,-73,0) rot=(0,0,1;0rad)
  Radius = 0.5
FEATURE [Part::Part2DObjectPython] Arc563  # Draft 2D object (typed FeaturePython)
  FirstAngle = -90
  LastAngle = 0
  MakeFace = false
  Placement = pos=(39.75,-73,0) rot=(0,0,1;0rad)
  Radius = 0.5
FEATURE [App::DocumentObjectGroup] Group125
  Group = -> [Line1076,Line1070,Line1084,Line1077,Line1075,Arc558,Arc560,Line1081,Arc562,Line1066,Arc563,Line1067]
FEATURE [Part::Part2DObjectPython] Line1085  # Draft 2D object (typed FeaturePython)
  ChamferSize = 0
  Closed = false
  End = (61.625,-60,0)
  FilletRadius = 0
  Length = 13
  MakeFace = false
  Placement = pos=(61.625,-73,0) rot=(0,0,1;0rad)
  Points = (2) [(0,0,0),(0,13,0)]
  Start = (61.625,-73,0)
  Subdivisions = 0
FEATURE [Part::Part2DObjectPython] Line1086  # Draft 2D object (typed FeaturePython)
  ChamferSize = 0
  Closed = false
  End = (66.5,-57,0)
  FilletRadius = 0
  Length = 23.75
  MakeFace = false
  Placement = pos=(42.75,-57,0) rot=(0,0,1;0rad)
  Points = (2) [(0,0,0),(23.75,0,0)]
  Start = (42.75,-57,0)
  Subdivisions = 0
FEATURE [Part::Part2DObjectPython] Arc564  # Draft 2D object (typed FeaturePython)
  FirstAngle = 0
  LastAngle = 90
  MakeFace = false
  Placement = pos=(61.125,-60,0) rot=(0,0,1;0rad)
  Radius = 0.5
FEATURE [App::DocumentObjectGroup] Group105
  Group = -> [Line1086,Line1069,Line965,Line964,Line1085,Arc564,Arc495,Line961,Arc493,Line960,Line969,Arc492]
FEATURE [Part::Part2DObjectPython] Arc565  # Draft 2D object (typed FeaturePython)
  FirstAngle = 0
  LastAngle = 90
  MakeFace = false
  Placement = pos=(58.75,-60,0) rot=(0,0,1;0rad)
  Radius = 0.5
FEATURE [Part::Part2DObjectPython] Arc566  # Draft 2D object (typed FeaturePython)
  FirstAngle = 0
  LastAngle = 90
  MakeFace = false
  Placement = pos=(241.625,-60,0) rot=(0,0,1;0rad)
  Radius = 0.5
FEATURE [Part::Part2DObjectPython] Line1087  # Draft 2D object (typed FeaturePython)
  ChamferSize = 0
  Closed = false
  End = (58.75,-59.5,0)
  FilletRadius = 0
  Length = 13
  MakeFace = false
  Placement = pos=(45.75,-59.5,0) rot=(0,0,1;0rad)
  Points = (2) [(0,0,0),(13,0,0)]
  Start = (45.75,-59.5,0)
  Subdivisions = 0
FEATURE [Part::Part2DObjectPython] Line1088  # Draft 2D object (typed FeaturePython)
  ChamferSize = 0
  Closed = false
  End = (114.125,-73,0)
  FilletRadius = 0
  Length = 13
  MakeFace = false
  Placement = pos=(114.125,-60,0) rot=(0,0,1;0rad)
  Points = (2) [(0,0,0),(0,-13,0)]
  Start = (114.125,-60,0)
  Subdivisions = 0
FEATURE [Part::Part2DObjectPython] Line1089  # Draft 2D object (typed FeaturePython)
  ChamferSize = 0
  Closed = false
  End = (197,-60,0)
  FilletRadius = 0
  Length = 13
  MakeFace = false
  Placement = pos=(197,-73,0) rot=(0,0,1;0rad)
  Points = (2) [(0,0,0),(0,13,0)]
  Start = (197,-73,0)
  Subdivisions = 0
FEATURE [Part::Part2DObjectPython] Line1090  # Draft 2D object (typed FeaturePython)
  ChamferSize = 0
  Closed = false
  End = (180.5,-76,0)
  FilletRadius = 0
  Length = 19
  MakeFace = false
  Placement = pos=(180.5,-57,0) rot=(0,0,1;0rad)
  Points = (2) [(0,0,0),(0,-19,0)]
  Start = (180.5,-57,0)
  Subdivisions = 0
FEATURE [Part::Part2DObjectPython] Arc567  # Draft 2D object (typed FeaturePython)
  FirstAngle = -90
  LastAngle = 0
  MakeFace = false
  Placement = pos=(74.337,-75.7,0) rot=(0,0,1;0rad)
  Radius = 0.5
FEATURE [Part::Part2DObjectPython] Line1091  # Draft 2D object (typed FeaturePython)
  ChamferSize = 0
  Closed = false
  End = (74.837,-75.7,0)
  FilletRadius = 0
  Length = 15.7
  MakeFace = false
  Placement = pos=(74.837,-60,0) rot=(0,0,1;0rad)
  Points = (2) [(0,0,0),(0,-15.7,0)]
  Start = (74.837,-60,0)
  Subdivisions = 0
FEATURE [Part::Part2DObjectPython] Arc568  # Draft 2D object (typed FeaturePython)
  FirstAngle = 90
  LastAngle = 180
  MakeFace = false
  Placement = pos=(228.625,-60,0) rot=(0,0,1;0rad)
  Radius = 0.5
FEATURE [Part::Part2DObjectPython] Line1092  # Draft 2D object (typed FeaturePython)
  ChamferSize = 0
  Closed = false
  End = (247,-57,0)
  FilletRadius = 0
  Length = 23.75
  MakeFace = false
  Placement = pos=(223.25,-57,0) rot=(0,0,1;0rad)
  Points = (2) [(0,0,0),(23.75,0,0)]
  Start = (223.25,-57,0)
  Subdivisions = 0
FEATURE [Part::Part2DObjectPython] Arc569  # Draft 2D object (typed FeaturePython)
  FirstAngle = 180
  LastAngle = 270
  MakeFace = false
  Placement = pos=(228.625,-73,0) rot=(0,0,1;0rad)
  Radius = 0.5
FEATURE [Part::Part2DObjectPython] Arc570  # Draft 2D object (typed FeaturePython)
  FirstAngle = -90
  LastAngle = 0
  MakeFace = false
  Placement = pos=(241.625,-73,0) rot=(0,0,1;0rad)
  Radius = 0.5
FEATURE [Part::Part2DObjectPython] Line1093  # Draft 2D object (typed FeaturePython)
  ChamferSize = 0
  Closed = false
  End = (228.125,-73,0)
  FilletRadius = 0
  Length = 13
  MakeFace = false
  Placement = pos=(228.125,-60,0) rot=(0,0,1;0rad)
  Points = (2) [(0,0,0),(0,-13,0)]
  Start = (228.125,-60,0)
  Subdivisions = 0
FEATURE [Part::Part2DObjectPython] Line1094  # Draft 2D object (typed FeaturePython)
  ChamferSize = 0
  Closed = false
  End = (59.25,-60,0)
  FilletRadius = 0
  Length = 13
  MakeFace = false
  Placement = pos=(59.25,-73,0) rot=(0,0,1;0rad)
  Points = (2) [(0,0,0),(0,13,0)]
  Start = (59.25,-73,0)
  Subdivisions = 0
FEATURE [Part::Part2DObjectPython] Line1095  # Draft 2D object (typed FeaturePython)
  ChamferSize = 0
  Closed = false
  End = (42.75,-76,0)
  FilletRadius = 0
  Length = 19
  MakeFace = false
  Placement = pos=(42.75,-57,0) rot=(0,0,1;0rad)
  Points = (2) [(0,0,0),(0,-19,0)]
  Start = (42.75,-57,0)
  Subdivisions = 0
FEATURE [Part::Part2DObjectPython] Arc571  # Draft 2D object (typed FeaturePython)
  FirstAngle = 90
  LastAngle = 180
  MakeFace = false
  Placement = pos=(45.75,-60,0) rot=(0,0,1;0rad)
  Radius = 0.5
FEATURE [Part::Part2DObjectPython] Line1096  # Draft 2D object (typed FeaturePython)
  ChamferSize = 0
  Closed = false
  End = (61.75,-57,0)
  FilletRadius = 0
  Length = 19
  MakeFace = false
  Placement = pos=(42.75,-57,0) rot=(0,0,1;0rad)
  Points = (2) [(0,0,0),(19,0,0)]
  Start = (42.75,-57,0)
  Subdivisions = 0
FEATURE [Part::Part2DObjectPython] Line1097  # Draft 2D object (typed FeaturePython)
  ChamferSize = 0
  Closed = false
  End = (247,-57,0)
  FilletRadius = 0
  Length = 19
  MakeFace = false
  Placement = pos=(247,-76,0) rot=(0,0,1;0rad)
  Points = (2) [(0,0,0),(0,19,0)]
  Start = (247,-76,0)
  Subdivisions = 0
FEATURE [Part::Part2DObjectPython] Line1098  # Draft 2D object (typed FeaturePython)
  ChamferSize = 0
  Closed = false
  End = (61.75,-76,0)
  FilletRadius = 0
  Length = 19
  MakeFace = false
  Placement = pos=(61.75,-57,0) rot=(0,0,1;0rad)
  Points = (2) [(0,0,0),(0,-19,0)]
  Start = (61.75,-57,0)
  Subdivisions = 0
FEATURE [Part::Part2DObjectPython] Line1099  # Draft 2D object (typed FeaturePython)
  ChamferSize = 0
  Closed = false
  End = (42.75,-76,0)
  FilletRadius = 0
  Length = 19
  MakeFace = false
  Placement = pos=(61.75,-76,0) rot=(0,0,1;0rad)
  Points = (2) [(0,0,0),(-19,0,0)]
  Start = (61.75,-76,0)
  Subdivisions = 0
FEATURE [Part::Part2DObjectPython] Arc572  # Draft 2D object (typed FeaturePython)
  FirstAngle = 180
  LastAngle = 270
  MakeFace = false
  Placement = pos=(45.75,-73,0) rot=(0,0,1;0rad)
  Radius = 0.5
FEATURE [Part::Part2DObjectPython] Line1100  # Draft 2D object (typed FeaturePython)
  ChamferSize = 0
  Closed = false
  End = (241.625,-59.5,0)
  FilletRadius = 0
  Length = 13
  MakeFace = false
  Placement = pos=(228.625,-59.5,0) rot=(0,0,1;0rad)
  Points = (2) [(0,0,0),(13,0,0)]
  Start = (228.625,-59.5,0)
  Subdivisions = 0
FEATURE [App::DocumentObjectGroup] Group111
  Group = -> [Line1092,Line930,Line910,Line1097,Line936,Arc566,Arc568,Line1093,Arc569,Line1100,Line934,Arc570]
FEATURE [Part::Part2DObjectPython] Arc573  # Draft 2D object (typed FeaturePython)
  FirstAngle = -90
  LastAngle = 0
  MakeFace = false
  Placement = pos=(58.75,-73,0) rot=(0,0,1;0rad)
  Radius = 0.5
FEATURE [Part::Part2DObjectPython] Arc574  # Draft 2D object (typed FeaturePython)
  FirstAngle = 90
  LastAngle = 180
  MakeFace = false
  Placement = pos=(67.837,-56.5,0) rot=(0,0,1;0rad)
  Radius = 0.5
FEATURE [Part::Part2DObjectPython] Arc575  # Draft 2D object (typed FeaturePython)
  FirstAngle = 180
  LastAngle = 270
  MakeFace = false
  Placement = pos=(114.625,-73,0) rot=(0,0,1;0rad)
  Radius = 0.5
FEATURE [Part::Part2DObjectPython] Arc576  # Draft 2D object (typed FeaturePython)
  FirstAngle = -90
  LastAngle = 0
  MakeFace = false
  Placement = pos=(127.625,-73,0) rot=(0,0,1;0rad)
  Radius = 0.5
FEATURE [Part::Part2DObjectPython] Line1101  # Draft 2D object (typed FeaturePython)
  ChamferSize = 0
  Closed = false
  End = (58.75,-73.5,0)
  FilletRadius = 0
  Length = 13
  MakeFace = false
  Placement = pos=(45.75,-73.5,0) rot=(0,0,1;0rad)
  Points = (2) [(0,0,0),(13,0,0)]
  Start = (45.75,-73.5,0)
  Subdivisions = 0
FEATURE [Part::Part2DObjectPython] Line1102  # Draft 2D object (typed FeaturePython)
  ChamferSize = 0
  Closed = false
  End = (45.25,-73,0)
  FilletRadius = 0
  Length = 13
  MakeFace = false
  Placement = pos=(45.25,-60,0) rot=(0,0,1;0rad)
  Points = (2) [(0,0,0),(0,-13,0)]
  Start = (45.25,-60,0)
  Subdivisions = 0
FEATURE [App::DocumentObjectGroup] Group117
  Group = -> [Line1096,Line1098,Line1099,Line1095,Line1087,Arc565,Arc571,Line1102,Arc572,Line1101,Arc573,Line1094]
FEATURE [Part::Part2DObjectPython] Line1103  # Draft 2D object (typed FeaturePython)
  ChamferSize = 0
  Closed = false
  End = (196.5,-59.5,0)
  FilletRadius = 0
  Length = 13
  MakeFace = false
  Placement = pos=(183.5,-59.5,0) rot=(0,0,1;0rad)
  Points = (2) [(0,0,0),(13,0,0)]
  Start = (183.5,-59.5,0)
  Subdivisions = 0
FEATURE [Part::Part2DObjectPython] Line1104  # Draft 2D object (typed FeaturePython)
  ChamferSize = 0
  Closed = false
  End = (127.625,-73.5,0)
  FilletRadius = 0
  Length = 13
  MakeFace = false
  Placement = pos=(114.625,-73.5,0) rot=(0,0,1;0rad)
  Points = (2) [(0,0,0),(13,0,0)]
  Start = (114.625,-73.5,0)
  Subdivisions = 0
FEATURE [Part::Part2DObjectPython] Line1105  # Draft 2D object (typed FeaturePython)
  ChamferSize = 0
  Closed = false
  End = (128.125,-60,0)
  FilletRadius = 0
  Length = 13
  MakeFace = false
  Placement = pos=(128.125,-73,0) rot=(0,0,1;0rad)
  Points = (2) [(0,0,0),(0,13,0)]
  Start = (128.125,-73,0)
  Subdivisions = 0
FEATURE [Part::Part2DObjectPython] Arc577  # Draft 2D object (typed FeaturePython)
  FirstAngle = 0
  LastAngle = 90
  MakeFace = false
  Placement = pos=(196.5,-60,0) rot=(0,0,1;0rad)
  Radius = 0.5
FEATURE [Part::Part2DObjectPython] Arc578  # Draft 2D object (typed FeaturePython)
  FirstAngle = 90
  LastAngle = 180
  MakeFace = false
  Placement = pos=(128.625,-60,0) rot=(0,0,1;0rad)
  Radius = 0.5
FEATURE [Part::Part2DObjectPython] Arc579  # Draft 2D object (typed FeaturePython)
  FirstAngle = 0
  LastAngle = 90
  MakeFace = false
  Placement = pos=(113.625,-60,0) rot=(0,0,1;0rad)
  Radius = 0.5
FEATURE [Part::Part2DObjectPython] Line1106  # Draft 2D object (typed FeaturePython)
  ChamferSize = 0
  Closed = false
  End = (74.337,-76.2,0)
  FilletRadius = 0
  Length = 6.5
  MakeFace = false
  Placement = pos=(67.837,-76.2,0) rot=(0,0,1;0rad)
  Points = (2) [(0,0,0),(6.5,0,0)]
  Start = (67.837,-76.2,0)
  Subdivisions = 0
FEATURE [Part::Part2DObjectPython] Line1107  # Draft 2D object (typed FeaturePython)
  ChamferSize = 0
  Closed = false
  End = (20,-29,0)
  FilletRadius = 0
  Length = 1
  MakeFace = false
  Placement = pos=(20,-28,0) rot=(0,0,1;0rad)
  Points = (2) [(0,0,0),(0,-1,0)]
  Start = (20,-28,0)
  Subdivisions = 0
FEATURE [Part::Part2DObjectPython] Line1108  # Draft 2D object (typed FeaturePython)
  ChamferSize = 0
  Closed = false
  End = (67.837,-56,0)
  FilletRadius = 0
  Length = 106.576
  MakeFace = false
  Placement = pos=(174.413,-56,0) rot=(0,0,1;0rad)
  Points = (2) [(0,0,0),(-106.576,0,0)]
  Start = (174.413,-56,0)
  Subdivisions = 0
FEATURE [Part::Part2DObjectPython] Line1109  # Draft 2D object (typed FeaturePython)
  ChamferSize = 0
  Closed = false
  End = (174.913,-56.5,0)
  FilletRadius = 0
  Length = 19.2
  MakeFace = false
  Placement = pos=(174.913,-75.7,0) rot=(0,0,1;0rad)
  Points = (2) [(0,0,0),(0,19.2,0)]
  Start = (174.913,-75.7,0)
  Subdivisions = 0
FEATURE [Part::Part2DObjectPython] Line1110  # Draft 2D object (typed FeaturePython)
  ChamferSize = 0
  Closed = false
  End = (113.625,-59.5,0)
  FilletRadius = 0
  Length = 38.288
  MakeFace = false
  Placement = pos=(75.337,-59.5,0) rot=(0,0,1;0rad)
  Points = (2) [(0,0,0),(38.288,0,0)]
  Start = (75.337,-59.5,0)
  Subdivisions = 0
FEATURE [Part::Part2DObjectPython] Line1111  # Draft 2D object (typed FeaturePython)
  ChamferSize = 0
  Closed = false
  End = (180.5,-57,0)
  FilletRadius = 0
  Length = 118.75
  MakeFace = false
  Placement = pos=(61.75,-57,0) rot=(0,0,1;0rad)
  Points = (2) [(0,0,0),(118.75,0,0)]
  Start = (61.75,-57,0)
  Subdivisions = 0
FEATURE [Part::Part2DObjectPython] Arc580  # Draft 2D object (typed FeaturePython)
  FirstAngle = 0
  LastAngle = 90
  MakeFace = false
  Placement = pos=(20.5,-29,0) rot=(0,0,1;3.14159rad)
  Radius = 0.5
FEATURE [Part::Part2DObjectPython] Line1112  # Draft 2D object (typed FeaturePython)
  ChamferSize = 0
  Closed = false
  End = (199.5,-76,0)
  FilletRadius = 0
  Length = 19
  MakeFace = false
  Placement = pos=(199.5,-57,0) rot=(0,0,1;0rad)
  Points = (2) [(0,0,0),(0,-19,0)]
  Start = (199.5,-57,0)
  Subdivisions = 0
FEATURE [Part::Part2DObjectPython] Line1113  # Draft 2D object (typed FeaturePython)
  ChamferSize = 0
  Closed = false
  End = (166.913,-59.5,0)
  FilletRadius = 0
  Length = 38.288
  MakeFace = false
  Placement = pos=(128.625,-59.5,0) rot=(0,0,1;0rad)
  Points = (2) [(0,0,0),(38.288,0,0)]
  Start = (128.625,-59.5,0)
  Subdivisions = 0
FEATURE [Part::Part2DObjectPython] Arc581  # Draft 2D object (typed FeaturePython)
  FirstAngle = -90
  LastAngle = 0
  MakeFace = false
  Placement = pos=(196.5,-73,0) rot=(0,0,1;0rad)
  Radius = 0.5
FEATURE [Part::Part2DObjectPython] Line1114  # Draft 2D object (typed FeaturePython)
  ChamferSize = 0
  Closed = false
  End = (180.5,-76,0)
  FilletRadius = 0
  Length = 19
  MakeFace = false
  Placement = pos=(180.5,-57,0) rot=(0,0,1;0rad)
  Points = (2) [(0,0,0),(0,-19,0)]
  Start = (180.5,-57,0)
  Subdivisions = 0
FEATURE [Part::Part2DObjectPython] Arc582  # Draft 2D object (typed FeaturePython)
  FirstAngle = 90
  LastAngle = 180
  MakeFace = false
  Placement = pos=(183.5,-60,0) rot=(0,0,1;0rad)
  Radius = 0.5
FEATURE [Part::Part2DObjectPython] Arc583  # Draft 2D object (typed FeaturePython)
  FirstAngle = 180
  LastAngle = 270
  MakeFace = false
  Placement = pos=(183.5,-73,0) rot=(0,0,1;0rad)
  Radius = 0.5
FEATURE [Part::Part2DObjectPython] Line1115  # Draft 2D object (typed FeaturePython)
  ChamferSize = 0
  Closed = false
  End = (67.337,-75.7,0)
  FilletRadius = 0
  Length = 19.2
  MakeFace = false
  Placement = pos=(67.337,-56.5,0) rot=(0,0,1;0rad)
  Points = (2) [(0,0,0),(0,-19.2,0)]
  Start = (67.337,-56.5,0)
  Subdivisions = 0
FEATURE [Part::Part2DObjectPython] Line1116  # Draft 2D object (typed FeaturePython)
  ChamferSize = 0
  Closed = false
  End = (61.75,-76,0)
  FilletRadius = 0
  Length = 19
  MakeFace = false
  Placement = pos=(61.75,-57,0) rot=(0,0,1;0rad)
  Points = (2) [(0,0,0),(0,-19,0)]
  Start = (61.75,-57,0)
  Subdivisions = 0
FEATURE [Part::Part2DObjectPython] Line1117  # Draft 2D object (typed FeaturePython)
  ChamferSize = 0
  Closed = false
  End = (180.5,-76,0)
  FilletRadius = 0
  Length = 118.75
  MakeFace = false
  Placement = pos=(61.75,-76,0) rot=(0,0,1;0rad)
  Points = (2) [(0,0,0),(118.75,0,0)]
  Start = (61.75,-76,0)
  Subdivisions = 0
FEATURE [Part::Part2DObjectPython] Line1118  # Draft 2D object (typed FeaturePython)
  ChamferSize = 0
  Closed = false
  End = (30.5,-43,0)
  FilletRadius = 0
  Length = 5
  MakeFace = false
  Placement = pos=(25.5,-43,0) rot=(0,0,1;0rad)
  Points = (2) [(0,0,0),(5,0,0)]
  Start = (25.5,-43,0)
  Subdivisions = 0
FEATURE [Part::Part2DObjectPython] Arc584  # Draft 2D object (typed FeaturePython)
  FirstAngle = -90
  LastAngle = 0
  MakeFace = false
  Placement = pos=(174.413,-75.7,0) rot=(0,0,1;0rad)
  Radius = 0.5
FEATURE [Part::Part2DObjectPython] Arc585  # Draft 2D object (typed FeaturePython)
  FirstAngle = 0
  LastAngle = 90
  MakeFace = false
  Placement = pos=(174.413,-56.5,0) rot=(0,0,1;0rad)
  Radius = 0.5
FEATURE [Part::Part2DObjectPython] Arc586  # Draft 2D object (typed FeaturePython)
  FirstAngle = 90
  LastAngle = 180
  MakeFace = false
  Placement = pos=(75.337,-60,0) rot=(0,0,1;0rad)
  Radius = 0.5
FEATURE [Part::Part2DObjectPython] Line1119  # Draft 2D object (typed FeaturePython)
  ChamferSize = 0
  Closed = false
  End = (174.413,-76.2,0)
  FilletRadius = 0
  Length = 6.5
  MakeFace = false
  Placement = pos=(167.913,-76.2,0) rot=(0,0,1;0rad)
  Points = (2) [(0,0,0),(6.5,0,0)]
  Start = (167.913,-76.2,0)
  Subdivisions = 0
FEATURE [Part::Part2DObjectPython] Arc587  # Draft 2D object (typed FeaturePython)
  FirstAngle = 0
  LastAngle = 90
  MakeFace = false
  Placement = pos=(166.913,-60,0) rot=(0,0,1;0rad)
  Radius = 0.5
FEATURE [Part::Part2DObjectPython] Line1120  # Draft 2D object (typed FeaturePython)
  ChamferSize = 0
  Closed = false
  End = (167.413,-75.7,0)
  FilletRadius = 0
  Length = 15.7
  MakeFace = false
  Placement = pos=(167.413,-60,0) rot=(0,0,1;0rad)
  Points = (2) [(0,0,0),(0,-15.7,0)]
  Start = (167.413,-60,0)
  Subdivisions = 0
FEATURE [Part::Part2DObjectPython] Line1121  # Draft 2D object (typed FeaturePython)
  ChamferSize = 0
  Closed = false
  End = (199.5,-57,0)
  FilletRadius = 0
  Length = 19
  MakeFace = false
  Placement = pos=(180.5,-57,0) rot=(0,0,1;0rad)
  Points = (2) [(0,0,0),(19,0,0)]
  Start = (180.5,-57,0)
  Subdivisions = 0
FEATURE [Part::Part2DObjectPython] Arc588  # Draft 2D object (typed FeaturePython)
  FirstAngle = 180
  LastAngle = 270
  MakeFace = false
  Placement = pos=(67.837,-75.7,0) rot=(0,0,1;0rad)
  Radius = 0.5
FEATURE [Part::Part2DObjectPython] Line1122  # Draft 2D object (typed FeaturePython)
  ChamferSize = 0
  Closed = false
  End = (180.5,-76,0)
  FilletRadius = 0
  Length = 19
  MakeFace = false
  Placement = pos=(199.5,-76,0) rot=(0,0,1;0rad)
  Points = (2) [(0,0,0),(-19,0,0)]
  Start = (199.5,-76,0)
  Subdivisions = 0
FEATURE [Part::Part2DObjectPython] Arc589  # Draft 2D object (typed FeaturePython)
  FirstAngle = 180
  LastAngle = 270
  MakeFace = false
  Placement = pos=(167.913,-75.7,0) rot=(0,0,1;0rad)
  Radius = 0.5
FEATURE [App::DocumentObjectGroup] Group124  label="6.25u space001"
  Group = -> [Line1111,Line1116,Line1117,Line1114,Line1105,Arc579,Line1088,Arc575,Arc578,Arc576,Line1104,Arc574,Arc585,Arc588,Line1106,Arc567,Arc586,Line1091,Line1115,Arc589,Line1119,Arc584,Line1109,Arc587,Line1120,Line1108,Line1110,Line1113]
FEATURE [Part::Part2DObjectPython] Line1123  # Draft 2D object (typed FeaturePython)
  ChamferSize = 0
  Closed = false
  End = (196.5,-73.5,0)
  FilletRadius = 0
  Length = 13
  MakeFace = false
  Placement = pos=(183.5,-73.5,0) rot=(0,0,1;0rad)
  Points = (2) [(0,0,0),(13,0,0)]
  Start = (183.5,-73.5,0)
  Subdivisions = 0
FEATURE [Part::Part2DObjectPython] Arc590  # Draft 2D object (typed FeaturePython)
  FirstAngle = 0
  LastAngle = 90
  MakeFace = false
  Placement = pos=(23.5,-28,0) rot=(0,0,1;0rad)
  Radius = 0.5
FEATURE [Part::Part2DObjectPython] Arc591  # Draft 2D object (typed FeaturePython)
  FirstAngle = 0
  LastAngle = 90
  MakeFace = false
  Placement = pos=(25.5,-51.5,0) rot=(0,0,1;3.14159rad)
  Radius = 0.5
FEATURE [Part::Part2DObjectPython] Line1124  # Draft 2D object (typed FeaturePython)
  ChamferSize = 0
  Closed = false
  End = (25,-43.5,0)
  FilletRadius = 0
  Length = 8
  MakeFace = false
  Placement = pos=(25,-51.5,0) rot=(0,0,1;0rad)
  Points = (2) [(0,0,0),(0,8,0)]
  Start = (25,-51.5,0)
  Subdivisions = 0
FEATURE [Part::Part2DObjectPython] Arc592  # Draft 2D object (typed FeaturePython)
  FirstAngle = 90
  LastAngle = 180
  MakeFace = false
  Placement = pos=(25.5,-43.5,0) rot=(0,0,1;0rad)
  Radius = 0.5
FEATURE [Part::Part2DObjectPython] Arc593  # Draft 2D object (typed FeaturePython)
  FirstAngle = 90
  LastAngle = 180
  MakeFace = false
  Placement = pos=(20.5,-28,0) rot=(0,0,1;0rad)
  Radius = 0.5
FEATURE [Part::Part2DObjectPython] Line1125  # Draft 2D object (typed FeaturePython)
  ChamferSize = 0
  Closed = false
  End = (20.5,-29.5,0)
  FilletRadius = 0
  Length = 3
  MakeFace = false
  Placement = pos=(23.5,-29.5,0) rot=(0,0,1;3.14159rad)
  Points = (2) [(0,0,0),(3,0,0)]
  Start = (23.5,-29.5,0)
  Subdivisions = 0
FEATURE [Part::Part2DObjectPython] Arc594  # Draft 2D object (typed FeaturePython)
  FirstAngle = 90
  LastAngle = 180
  MakeFace = false
  Placement = pos=(23.5,-29,0) rot=(0,0,1;3.14159rad)
  Radius = 0.5
FEATURE [Part::Part2DObjectPython] Line1126  # Draft 2D object (typed FeaturePython)
  ChamferSize = 0
  Closed = false
  End = (23.5,-27.5,0)
  FilletRadius = 0
  Length = 3
  MakeFace = false
  Placement = pos=(20.5,-27.5,0) rot=(0,0,1;0rad)
  Points = (2) [(0,0,0),(3,0,0)]
  Start = (20.5,-27.5,0)
  Subdivisions = 0
FEATURE [Part::Part2DObjectPython] Arc595  # Draft 2D object (typed FeaturePython)
  FirstAngle = 0
  LastAngle = 90
  MakeFace = false
  Placement = pos=(30.5,-43.5,0) rot=(0,0,1;0rad)
  Radius = 0.5
FEATURE [Part::Part2DObjectPython] Line1127  # Draft 2D object (typed FeaturePython)
  ChamferSize = 0
  Closed = false
  End = (183,-73,0)
  FilletRadius = 0
  Length = 13
  MakeFace = false
  Placement = pos=(183,-60,0) rot=(0,0,1;0rad)
  Points = (2) [(0,0,0),(0,-13,0)]
  Start = (183,-60,0)
  Subdivisions = 0
FEATURE [App::DocumentObjectGroup] Group119
  Group = -> [Line1121,Line1112,Line1122,Line1090,Line1103,Arc577,Arc582,Line1127,Arc583,Line1123,Arc581,Line1089]
FEATURE [App::DocumentObjectGroup] Group114  label="full 003"
  Group = -> [Group117,Group124,Group119]
FEATURE [Part::Part2DObjectPython] Line1128  # Draft 2D object (typed FeaturePython)
  ChamferSize = 0
  Closed = false
  End = (25.5,-52,0)
  FilletRadius = 0
  Length = 5
  MakeFace = false
  Placement = pos=(30.5,-52,0) rot=(0,0,1;3.14159rad)
  Points = (2) [(0,0,0),(5,2.13163e-14,0)]
  Start = (30.5,-52,0)
  Subdivisions = 0
FEATURE [Part::Part2DObjectPython] Line1129  # Draft 2D object (typed FeaturePython)
  ChamferSize = 0
  Closed = false
  End = (24,-28,0)
  FilletRadius = 0
  Length = 1
  MakeFace = false
  Placement = pos=(24,-29,0) rot=(0,0,1;0rad)
  Points = (2) [(0,0,0),(0,1,0)]
  Start = (24,-29,0)
  Subdivisions = 0
FEATURE [Part::Part2DObjectPython] Line1130  # Draft 2D object (typed FeaturePython)
  ChamferSize = 0
  Closed = false
  End = (31,-43.5,0)
  FilletRadius = 0
  Length = 8
  MakeFace = false
  Placement = pos=(31,-51.5,0) rot=(0,0,1;0rad)
  Points = (2) [(0,0,0),(0,8,0)]
  Start = (31,-51.5,0)
  Subdivisions = 0
FEATURE [Part::Part2DObjectPython] Arc596  # Draft 2D object (typed FeaturePython)
  FirstAngle = 90
  LastAngle = 180
  MakeFace = false
  Placement = pos=(30.5,-51.5,0) rot=(0,0,1;3.14159rad)
  Radius = 0.5
FEATURE [App::DocumentObjectGroup] Group129  label="LED001"
  Group = -> [Line1126,Line1129,Arc590,Arc593,Line1107,Arc580,Line1125,Arc594]
FEATURE [App::DocumentObjectGroup] Group130  label="Reset001"
  Group = -> [Line1118,Line1130,Arc592,Arc595,Arc596,Line1128,Arc591,Line1124]
FEATURE [Part::Part2DObjectPython] Line1131  # Draft 2D object (typed FeaturePython)
  ChamferSize = 0
  Closed = false
  End = (90.25,-57,0)
  FilletRadius = 0
  Length = 19
  MakeFace = false
  Placement = pos=(90.25,-38,0) rot=(0,0,1;0rad)
  Points = (2) [(0,0,0),(0,-19,0)]
  Start = (90.25,-38,0)
  Subdivisions = 0
FEATURE [App::DocumentObjectGroup] Group131
  Group = -> [Line680,Line682,Line687,Line683,Line670,Arc347,Arc353,Line684,Arc354,Line685,Line686,Arc355]
FEATURE [Part::Part2DObjectPython] Arc597  # Draft 2D object (typed FeaturePython)
  FirstAngle = 0
  LastAngle = 90
  MakeFace = false
  Placement = pos=(206,-3,0) rot=(0,0,1;0rad)
  Radius = 0.5
FEATURE [App::DocumentObjectGroup] Group132
  Group = -> [Line678,Line679,Line672,Line664,Line671,Arc343,Arc346,Line676,Arc352,Line669,Arc345,Line673]
FEATURE [App::DocumentObjectGroup] Group133
  Group = -> [Line702,Line708,Line698,Line696,Line715,Arc365,Arc362,Line709,Arc358,Line713,Arc359,Line697]
FEATURE [App::DocumentObjectGroup] Group134
  Group = -> [Line740,Line738,Line746,Line739,Line756,Arc383,Arc378,Line735,Arc381,Line741,Arc382,Line732]
FEATURE [Part::Part2DObjectPython] Line1132  # Draft 2D object (typed FeaturePython)
  ChamferSize = 0
  Closed = false
  End = (109.25,-38,0)
  FilletRadius = 0
  Length = 19
  MakeFace = false
  Placement = pos=(90.25,-38,0) rot=(0,0,1;0rad)
  Points = (2) [(0,0,0),(19,0,0)]
  Start = (90.25,-38,0)
  Subdivisions = 0
FEATURE [Part::Part2DObjectPython] Line1133  # Draft 2D object (typed FeaturePython)
  ChamferSize = 0
  Closed = false
  End = (209,-19,0)
  FilletRadius = 0
  Length = 19
  MakeFace = false
  Placement = pos=(209,0,0) rot=(0,0,1;0rad)
  Points = (2) [(0,0,0),(0,-19,0)]
  Start = (209,0,0)
  Subdivisions = 0
FEATURE [App::DocumentObjectGroup] Group136
  Group = -> [Line705,Line711,Line701,Line718,Line710,Arc366,Arc376,Line719,Arc363,Line707,Arc364,Line717]
FEATURE [App::DocumentObjectGroup] Group139
  Group = -> [Line726,Line723,Line722,Line725,Line721,Arc375,Arc367,Line727,Arc373,Line720,Arc374,Line724]
FEATURE [App::DocumentObjectGroup] Group140
  Group = -> [Line660,Line1133,Line662,Line668,Line667,Arc597,Arc344,Line661,Arc342,Line657,Arc341,Line658]
FEATURE [App::DocumentObjectGroup] Group141
  Group = -> [Line783,Line766,Line769,Line751,Arc402,Line743,Arc396,Line764,Line782,Arc394,Arc403,Line763]
FEATURE [App::DocumentObjectGroup] Group142
  Group = -> [Line772,Line774,Line775,Line773,Line767,Arc393,Arc401,Line771,Arc398,Line780,Arc385,Line762]
FEATURE [App::DocumentObjectGroup] Group143
  Group = -> [Line759,Line742,Line757,Line745,Line748,Arc389,Arc387,Line749,Arc388,Line755,Arc392,Line747]
FEATURE [App::DocumentObjectGroup] Group145
  Group = -> [Line833,Line831,Line838,Line847,Line834,Arc427,Arc430,Line815,Arc428,Line845,Arc426,Line832]
FEATURE [App::DocumentObjectGroup] Group146
  Group = -> [Line819,Line809,Line829,Line828,Line822,Arc417,Arc424,Line826,Arc425,Line830,Arc416,Line810]
FEATURE [App::DocumentObjectGroup] Group147
  Group = -> [Line850,Line840,Line848,Line849,Line842,Arc431,Arc432,Line841,Arc437,Line843,Arc429,Line839]
FEATURE [App::DocumentObjectGroup] Group148
  Group = -> [Line863,Line837,Line862,Line867,Line844,Arc436,Arc433,Line836,Arc434,Line846,Arc435,Line835]
FEATURE [App::DocumentObjectGroup] Group149
  Group = -> [Line801,Line788,Line799,Line789,Line796,Arc406,Arc411,Line798,Arc412,Line785,Arc413,Line790]
FEATURE [App::DocumentObjectGroup] Group151
  Group = -> [Line811,Line813,Line824,Line818,Line814,Arc418,Arc420,Line812,Arc421,Line825,Arc423,Line816]
FEATURE [App::DocumentObjectGroup] Group152
  Group = -> [Line781,Line776,Line777,Line778,Arc399,Line765,Arc395,Line770,Line779,Arc397,Arc400,Line768]
FEATURE [App::DocumentObjectGroup] Group154
  Group = -> [Line758,Line750,Line754,Line760,Line753,Arc384,Arc390,Line752,Arc391,Line761,Arc386,Line744]
FEATURE [App::DocumentObjectGroup] Group155
  Group = -> [Line791,Line803,Line795,Line786,Line800,Arc407,Arc414,Line804,Arc409,Line792,Arc408,Line794]
FEATURE [Part::Part2DObjectPython] Line1134  # Draft 2D object (typed FeaturePython)
  ChamferSize = 0
  Closed = false
  End = (76,-19,0)
  FilletRadius = 0
  Length = 19
  MakeFace = false
  Placement = pos=(95,-19,0) rot=(0,0,1;0rad)
  Points = (2) [(0,0,0),(-19,0,0)]
  Start = (95,-19,0)
  Subdivisions = 0
FEATURE [Part::Part2DObjectPython] Line1135  # Draft 2D object (typed FeaturePython)
  ChamferSize = 0
  Closed = false
  End = (76,0,0)
  FilletRadius = 0
  Length = 19
  MakeFace = false
  Placement = pos=(57,0,0) rot=(0,0,1;0rad)
  Points = (2) [(0,0,0),(19,0,0)]
  Start = (57,0,0)
  Subdivisions = 0
FEATURE [Part::Part2DObjectPython] Arc598  # Draft 2D object (typed FeaturePython)
  FirstAngle = 180
  LastAngle = 270
  MakeFace = false
  Placement = pos=(117,-16,0) rot=(0,0,1;0rad)
  Radius = 0.5
FEATURE [Part::Part2DObjectPython] Line1136  # Draft 2D object (typed FeaturePython)
  ChamferSize = 0
  Closed = false
  End = (130,-16.5,0)
  FilletRadius = 0
  Length = 13
  MakeFace = false
  Placement = pos=(117,-16.5,0) rot=(0,0,1;0rad)
  Points = (2) [(0,0,0),(13,0,0)]
  Start = (117,-16.5,0)
  Subdivisions = 0
FEATURE [Part::Part2DObjectPython] Line1137  # Draft 2D object (typed FeaturePython)
  ChamferSize = 0
  Closed = false
  End = (95,-19,0)
  FilletRadius = 0
  Length = 19
  MakeFace = false
  Placement = pos=(95,0,0) rot=(0,0,1;0rad)
  Points = (2) [(0,0,0),(0,-19,0)]
  Start = (95,0,0)
  Subdivisions = 0
FEATURE [Part::Part2DObjectPython] Arc599  # Draft 2D object (typed FeaturePython)
  FirstAngle = -90
  LastAngle = 0
  MakeFace = false
  Placement = pos=(111,-16,0) rot=(0,0,1;0rad)
  Radius = 0.5
FEATURE [Part::Part2DObjectPython] Arc600  # Draft 2D object (typed FeaturePython)
  FirstAngle = 180
  LastAngle = 270
  MakeFace = false
  Placement = pos=(98,-16,0) rot=(0,0,1;0rad)
  Radius = 0.5
FEATURE [Part::Part2DObjectPython] Line1138  # Draft 2D object (typed FeaturePython)
  ChamferSize = 0
  Closed = false
  End = (95,-19,0)
  FilletRadius = 0
  Length = 19
  MakeFace = false
  Placement = pos=(95,0,0) rot=(0,0,1;0rad)
  Points = (2) [(0,0,0),(0,-19,0)]
  Start = (95,0,0)
  Subdivisions = 0
FEATURE [Part::Part2DObjectPython] Line1139  # Draft 2D object (typed FeaturePython)
  ChamferSize = 0
  Closed = false
  End = (97.5,-16,0)
  FilletRadius = 0
  Length = 13
  MakeFace = false
  Placement = pos=(97.5,-3,0) rot=(0,0,1;0rad)
  Points = (2) [(0,0,0),(0,-13,0)]
  Start = (97.5,-3,0)
  Subdivisions = 0
FEATURE [Part::Part2DObjectPython] Line1140  # Draft 2D object (typed FeaturePython)
  ChamferSize = 0
  Closed = false
  End = (111,-16.5,0)
  FilletRadius = 0
  Length = 13
  MakeFace = false
  Placement = pos=(98,-16.5,0) rot=(0,0,1;0rad)
  Points = (2) [(0,0,0),(13,0,0)]
  Start = (98,-16.5,0)
  Subdivisions = 0
FEATURE [Part::Part2DObjectPython] Line1141  # Draft 2D object (typed FeaturePython)
  ChamferSize = 0
  Closed = false
  End = (76,-19,0)
  FilletRadius = 0
  Length = 19
  MakeFace = false
  Placement = pos=(76,0,0) rot=(0,0,1;0rad)
  Points = (2) [(0,0,0),(0,-19,0)]
  Start = (76,0,0)
  Subdivisions = 0
FEATURE [Part::Part2DObjectPython] Line1142  # Draft 2D object (typed FeaturePython)
  ChamferSize = 0
  Closed = false
  End = (95,-19,0)
  FilletRadius = 0
  Length = 19
  MakeFace = false
  Placement = pos=(114,-19,0) rot=(0,0,1;0rad)
  Points = (2) [(0,0,0),(-19,0,0)]
  Start = (114,-19,0)
  Subdivisions = 0
FEATURE [Part::Part2DObjectPython] Line1143  # Draft 2D object (typed FeaturePython)
  ChamferSize = 0
  Closed = false
  End = (78.5,-16,0)
  FilletRadius = 0
  Length = 13
  MakeFace = false
  Placement = pos=(78.5,-3,0) rot=(0,0,1;0rad)
  Points = (2) [(0,0,0),(0,-13,0)]
  Start = (78.5,-3,0)
  Subdivisions = 0
FEATURE [Part::Part2DObjectPython] Arc601  # Draft 2D object (typed FeaturePython)
  FirstAngle = 90
  LastAngle = 180
  MakeFace = false
  Placement = pos=(98,-3,0) rot=(0,0,1;0rad)
  Radius = 0.5
FEATURE [Part::Part2DObjectPython] Arc602  # Draft 2D object (typed FeaturePython)
  FirstAngle = 0
  LastAngle = 90
  MakeFace = false
  Placement = pos=(111,-3,0) rot=(0,0,1;0rad)
  Radius = 0.5
FEATURE [Part::Part2DObjectPython] Arc603  # Draft 2D object (typed FeaturePython)
  FirstAngle = 90
  LastAngle = 180
  MakeFace = false
  Placement = pos=(79,-3,0) rot=(0,0,1;0rad)
  Radius = 0.5
FEATURE [Part::Part2DObjectPython] Line1144  # Draft 2D object (typed FeaturePython)
  ChamferSize = 0
  Closed = false
  End = (114,0,0)
  FilletRadius = 0
  Length = 19
  MakeFace = false
  Placement = pos=(95,0,0) rot=(0,0,1;0rad)
  Points = (2) [(0,0,0),(19,0,0)]
  Start = (95,0,0)
  Subdivisions = 0
FEATURE [Part::Part2DObjectPython] Line1145  # Draft 2D object (typed FeaturePython)
  ChamferSize = 0
  Closed = false
  End = (92.5,-3,0)
  FilletRadius = 0
  Length = 13
  MakeFace = false
  Placement = pos=(92.5,-16,0) rot=(0,0,1;0rad)
  Points = (2) [(0,0,0),(0,13,0)]
  Start = (92.5,-16,0)
  Subdivisions = 0
FEATURE [Part::Part2DObjectPython] Line1146  # Draft 2D object (typed FeaturePython)
  ChamferSize = 0
  Closed = false
  End = (114,-19,0)
  FilletRadius = 0
  Length = 19
  MakeFace = false
  Placement = pos=(114,0,0) rot=(0,0,1;0rad)
  Points = (2) [(0,0,0),(0,-19,0)]
  Start = (114,0,0)
  Subdivisions = 0
FEATURE [Part::Part2DObjectPython] Arc604  # Draft 2D object (typed FeaturePython)
  FirstAngle = -90
  LastAngle = 0
  MakeFace = false
  Placement = pos=(130,-16,0) rot=(0,0,1;0rad)
  Radius = 0.5
FEATURE [Part::Part2DObjectPython] Line1147  # Draft 2D object (typed FeaturePython)
  ChamferSize = 0
  Closed = false
  End = (95,0,0)
  FilletRadius = 0
  Length = 19
  MakeFace = false
  Placement = pos=(76,0,0) rot=(0,0,1;0rad)
  Points = (2) [(0,0,0),(19,0,0)]
  Start = (76,0,0)
  Subdivisions = 0
FEATURE [Part::Part2DObjectPython] Line1148  # Draft 2D object (typed FeaturePython)
  ChamferSize = 0
  Closed = false
  End = (111.5,-3,0)
  FilletRadius = 0
  Length = 13
  MakeFace = false
  Placement = pos=(111.5,-16,0) rot=(0,0,1;0rad)
  Points = (2) [(0,0,0),(0,13,0)]
  Start = (111.5,-16,0)
  Subdivisions = 0
FEATURE [Part::Part2DObjectPython] Arc605  # Draft 2D object (typed FeaturePython)
  FirstAngle = -90
  LastAngle = 0
  MakeFace = false
  Placement = pos=(92,-16,0) rot=(0,0,1;0rad)
  Radius = 0.5
FEATURE [Part::Part2DObjectPython] Line1149  # Draft 2D object (typed FeaturePython)
  ChamferSize = 0
  Closed = false
  End = (111,-2.5,0)
  FilletRadius = 0
  Length = 13
  MakeFace = false
  Placement = pos=(98,-2.5,0) rot=(0,0,1;0rad)
  Points = (2) [(0,0,0),(13,0,0)]
  Start = (98,-2.5,0)
  Subdivisions = 0
FEATURE [Part::Part2DObjectPython] Arc606  # Draft 2D object (typed FeaturePython)
  FirstAngle = 180
  LastAngle = 270
  MakeFace = false
  Placement = pos=(79,-16,0) rot=(0,0,1;0rad)
  Radius = 0.5
FEATURE [Part::Part2DObjectPython] Line1150  # Draft 2D object (typed FeaturePython)
  ChamferSize = 0
  Closed = false
  End = (92,-2.5,0)
  FilletRadius = 0
  Length = 13
  MakeFace = false
  Placement = pos=(79,-2.5,0) rot=(0,0,1;0rad)
  Points = (2) [(0,0,0),(13,0,0)]
  Start = (79,-2.5,0)
  Subdivisions = 0
FEATURE [Part::Part2DObjectPython] Line1151  # Draft 2D object (typed FeaturePython)
  ChamferSize = 0
  Closed = false
  End = (57,-19,0)
  FilletRadius = 0
  Length = 19
  MakeFace = false
  Placement = pos=(57,0,0) rot=(0,0,1;0rad)
  Points = (2) [(0,0,0),(0,-19,0)]
  Start = (57,0,0)
  Subdivisions = 0
FEATURE [Part::Part2DObjectPython] Arc607  # Draft 2D object (typed FeaturePython)
  FirstAngle = 0
  LastAngle = 90
  MakeFace = false
  Placement = pos=(92,-3,0) rot=(0,0,1;0rad)
  Radius = 0.5
FEATURE [Part::Part2DObjectPython] Line1152  # Draft 2D object (typed FeaturePython)
  ChamferSize = 0
  Closed = false
  End = (114,-19,0)
  FilletRadius = 0
  Length = 19
  MakeFace = false
  Placement = pos=(114,0,0) rot=(0,0,1;0rad)
  Points = (2) [(0,0,0),(0,-19,0)]
  Start = (114,0,0)
  Subdivisions = 0
FEATURE [Part::Part2DObjectPython] Line1153  # Draft 2D object (typed FeaturePython)
  ChamferSize = 0
  Closed = false
  End = (92,-16.5,0)
  FilletRadius = 0
  Length = 13
  MakeFace = false
  Placement = pos=(79,-16.5,0) rot=(0,0,1;0rad)
  Points = (2) [(0,0,0),(13,0,0)]
  Start = (79,-16.5,0)
  Subdivisions = 0
FEATURE [App::DocumentObjectGroup] Group095
  Group = -> [Line1147,Line1138,Line1134,Line1141,Line1150,Arc607,Arc603,Line1143,Arc606,Line1153,Arc605,Line1145]
FEATURE [Part::Part2DObjectPython] Line1154  # Draft 2D object (typed FeaturePython)
  ChamferSize = 0
  Closed = false
  End = (116.5,-16,0)
  FilletRadius = 0
  Length = 13
  MakeFace = false
  Placement = pos=(116.5,-3,0) rot=(0,0,1;0rad)
  Points = (2) [(0,0,0),(0,-13,0)]
  Start = (116.5,-3,0)
  Subdivisions = 0
FEATURE [Part::Part2DObjectPython] Line1155  # Draft 2D object (typed FeaturePython)
  ChamferSize = 0
  Closed = false
  End = (149.5,-3,0)
  FilletRadius = 0
  Length = 13
  MakeFace = false
  Placement = pos=(149.5,-16,0) rot=(0,0,1;0rad)
  Points = (2) [(0,0,0),(0,13,0)]
  Start = (149.5,-16,0)
  Subdivisions = 0
FEATURE [Part::Part2DObjectPython] Arc608  # Draft 2D object (typed FeaturePython)
  FirstAngle = 90
  LastAngle = 180
  MakeFace = false
  Placement = pos=(117,-3,0) rot=(0,0,1;0rad)
  Radius = 0.5
FEATURE [Part::Part2DObjectPython] Arc609  # Draft 2D object (typed FeaturePython)
  FirstAngle = -90
  LastAngle = 0
  MakeFace = false
  Placement = pos=(149,-16,0) rot=(0,0,1;0rad)
  Radius = 0.5
FEATURE [Part::Part2DObjectPython] Line1156  # Draft 2D object (typed FeaturePython)
  ChamferSize = 0
  Closed = false
  End = (171,0,0)
  FilletRadius = 0
  Length = 19
  MakeFace = false
  Placement = pos=(152,0,0) rot=(0,0,1;0rad)
  Points = (2) [(0,0,0),(19,0,0)]
  Start = (152,0,0)
  Subdivisions = 0
FEATURE [Part::Part2DObjectPython] Line1157  # Draft 2D object (typed FeaturePython)
  ChamferSize = 0
  Closed = false
  End = (133,-19,0)
  FilletRadius = 0
  Length = 19
  MakeFace = false
  Placement = pos=(152,-19,0) rot=(0,0,1;0rad)
  Points = (2) [(0,0,0),(-19,0,0)]
  Start = (152,-19,0)
  Subdivisions = 0
FEATURE [Part::Part2DObjectPython] Line1158  # Draft 2D object (typed FeaturePython)
  ChamferSize = 0
  Closed = false
  End = (190,-19,0)
  FilletRadius = 0
  Length = 19
  MakeFace = false
  Placement = pos=(190,0,0) rot=(0,0,1;0rad)
  Points = (2) [(0,0,0),(0,-19,0)]
  Start = (190,0,0)
  Subdivisions = 0
FEATURE [Part::Part2DObjectPython] Arc610  # Draft 2D object (typed FeaturePython)
  FirstAngle = 0
  LastAngle = 90
  MakeFace = false
  Placement = pos=(187,-3,0) rot=(0,0,1;0rad)
  Radius = 0.5
FEATURE [Part::Part2DObjectPython] Line1159  # Draft 2D object (typed FeaturePython)
  ChamferSize = 0
  Closed = false
  End = (114,-19,0)
  FilletRadius = 0
  Length = 19
  MakeFace = false
  Placement = pos=(133,-19,0) rot=(0,0,1;0rad)
  Points = (2) [(0,0,0),(-19,0,0)]
  Start = (133,-19,0)
  Subdivisions = 0
FEATURE [Part::Part2DObjectPython] Line1160  # Draft 2D object (typed FeaturePython)
  ChamferSize = 0
  Closed = false
  End = (133,-19,0)
  FilletRadius = 0
  Length = 19
  MakeFace = false
  Placement = pos=(133,0,0) rot=(0,0,1;0rad)
  Points = (2) [(0,0,0),(0,-19,0)]
  Start = (133,0,0)
  Subdivisions = 0
FEATURE [Part::Part2DObjectPython] Line1161  # Draft 2D object (typed FeaturePython)
  ChamferSize = 0
  Closed = false
  End = (152,-19,0)
  FilletRadius = 0
  Length = 19
  MakeFace = false
  Placement = pos=(152,0,0) rot=(0,0,1;0rad)
  Points = (2) [(0,0,0),(0,-19,0)]
  Start = (152,0,0)
  Subdivisions = 0
FEATURE [Part::Part2DObjectPython] Arc611  # Draft 2D object (typed FeaturePython)
  FirstAngle = 0
  LastAngle = 90
  MakeFace = false
  Placement = pos=(130,-3,0) rot=(0,0,1;0rad)
  Radius = 0.5
FEATURE [Part::Part2DObjectPython] Line1162  # Draft 2D object (typed FeaturePython)
  ChamferSize = 0
  Closed = false
  End = (133,-19,0)
  FilletRadius = 0
  Length = 19
  MakeFace = false
  Placement = pos=(133,0,0) rot=(0,0,1;0rad)
  Points = (2) [(0,0,0),(0,-19,0)]
  Start = (133,0,0)
  Subdivisions = 0
FEATURE [Part::Part2DObjectPython] Line1163  # Draft 2D object (typed FeaturePython)
  ChamferSize = 0
  Closed = false
  End = (135.5,-16,0)
  FilletRadius = 0
  Length = 13
  MakeFace = false
  Placement = pos=(135.5,-3,0) rot=(0,0,1;0rad)
  Points = (2) [(0,0,0),(0,-13,0)]
  Start = (135.5,-3,0)
  Subdivisions = 0
FEATURE [Part::Part2DObjectPython] Arc612  # Draft 2D object (typed FeaturePython)
  FirstAngle = 0
  LastAngle = 90
  MakeFace = false
  Placement = pos=(149,-3,0) rot=(0,0,1;0rad)
  Radius = 0.5
FEATURE [Part::Part2DObjectPython] Line1164  # Draft 2D object (typed FeaturePython)
  ChamferSize = 0
  Closed = false
  End = (171,-19,0)
  FilletRadius = 0
  Length = 19
  MakeFace = false
  Placement = pos=(171,0,0) rot=(0,0,1;0rad)
  Points = (2) [(0,0,0),(0,-19,0)]
  Start = (171,0,0)
  Subdivisions = 0
FEATURE [Part::Part2DObjectPython] Arc613  # Draft 2D object (typed FeaturePython)
  FirstAngle = 90
  LastAngle = 180
  MakeFace = false
  Placement = pos=(155,-3,0) rot=(0,0,1;0rad)
  Radius = 0.5
FEATURE [Part::Part2DObjectPython] Line1165  # Draft 2D object (typed FeaturePython)
  ChamferSize = 0
  Closed = false
  End = (130.5,-3,0)
  FilletRadius = 0
  Length = 13
  MakeFace = false
  Placement = pos=(130.5,-16,0) rot=(0,0,1;0rad)
  Points = (2) [(0,0,0),(0,13,0)]
  Start = (130.5,-16,0)
  Subdivisions = 0
FEATURE [Part::Part2DObjectPython] Line1166  # Draft 2D object (typed FeaturePython)
  ChamferSize = 0
  Closed = false
  End = (133,0,0)
  FilletRadius = 0
  Length = 19
  MakeFace = false
  Placement = pos=(114,0,0) rot=(0,0,1;0rad)
  Points = (2) [(0,0,0),(19,0,0)]
  Start = (114,0,0)
  Subdivisions = 0
FEATURE [Part::Part2DObjectPython] Arc614  # Draft 2D object (typed FeaturePython)
  FirstAngle = 0
  LastAngle = 90
  MakeFace = false
  Placement = pos=(168,-3,0) rot=(0,0,1;0rad)
  Radius = 0.5
FEATURE [Part::Part2DObjectPython] Line1167  # Draft 2D object (typed FeaturePython)
  ChamferSize = 0
  Closed = false
  End = (130,-2.5,0)
  FilletRadius = 0
  Length = 13
  MakeFace = false
  Placement = pos=(117,-2.5,0) rot=(0,0,1;0rad)
  Points = (2) [(0,0,0),(13,0,0)]
  Start = (117,-2.5,0)
  Subdivisions = 0
FEATURE [App::DocumentObjectGroup] Group096
  Group = -> [Line1166,Line1162,Line1159,Line1152,Line1167,Arc611,Arc608,Line1154,Arc598,Line1136,Arc604,Line1165]
FEATURE [Part::Part2DObjectPython] Line1168  # Draft 2D object (typed FeaturePython)
  ChamferSize = 0
  Closed = false
  End = (149,-2.5,0)
  FilletRadius = 0
  Length = 13
  MakeFace = false
  Placement = pos=(136,-2.5,0) rot=(0,0,1;0rad)
  Points = (2) [(0,0,0),(13,0,0)]
  Start = (136,-2.5,0)
  Subdivisions = 0
FEATURE [Part::Part2DObjectPython] Line1169  # Draft 2D object (typed FeaturePython)
  ChamferSize = 0
  Closed = false
  End = (154.5,-16,0)
  FilletRadius = 0
  Length = 13
  MakeFace = false
  Placement = pos=(154.5,-3,0) rot=(0,0,1;0rad)
  Points = (2) [(0,0,0),(0,-13,0)]
  Start = (154.5,-3,0)
  Subdivisions = 0
FEATURE [Part::Part2DObjectPython] Arc615  # Draft 2D object (typed FeaturePython)
  FirstAngle = 90
  LastAngle = 180
  MakeFace = false
  Placement = pos=(136,-3,0) rot=(0,0,1;0rad)
  Radius = 0.5
FEATURE [Part::Part2DObjectPython] Line1170  # Draft 2D object (typed FeaturePython)
  ChamferSize = 0
  Closed = false
  End = (168,-2.5,0)
  FilletRadius = 0
  Length = 13
  MakeFace = false
  Placement = pos=(155,-2.5,0) rot=(0,0,1;0rad)
  Points = (2) [(0,0,0),(13,0,0)]
  Start = (155,-2.5,0)
  Subdivisions = 0
FEATURE [Part::Part2DObjectPython] Arc616  # Draft 2D object (typed FeaturePython)
  FirstAngle = 180
  LastAngle = 270
  MakeFace = false
  Placement = pos=(136,-16,0) rot=(0,0,1;0rad)
  Radius = 0.5
FEATURE [Part::Part2DObjectPython] Line1171  # Draft 2D object (typed FeaturePython)
  ChamferSize = 0
  Closed = false
  End = (149,-16.5,0)
  FilletRadius = 0
  Length = 13
  MakeFace = false
  Placement = pos=(136,-16.5,0) rot=(0,0,1;0rad)
  Points = (2) [(0,0,0),(13,0,0)]
  Start = (136,-16.5,0)
  Subdivisions = 0
FEATURE [Part::Part2DObjectPython] Line1172  # Draft 2D object (typed FeaturePython)
  ChamferSize = 0
  Closed = false
  End = (152,0,0)
  FilletRadius = 0
  Length = 19
  MakeFace = false
  Placement = pos=(133,0,0) rot=(0,0,1;0rad)
  Points = (2) [(0,0,0),(19,0,0)]
  Start = (133,0,0)
  Subdivisions = 0
FEATURE [App::DocumentObjectGroup] Group138
  Group = -> [Line1172,Line1161,Line1157,Line1160,Line1168,Arc612,Arc615,Line1163,Arc616,Line1171,Arc609,Line1155]
FEATURE [Part::Part2DObjectPython] Line1173  # Draft 2D object (typed FeaturePython)
  ChamferSize = 0
  Closed = false
  End = (152,-19,0)
  FilletRadius = 0
  Length = 19
  MakeFace = false
  Placement = pos=(171,-19,0) rot=(0,0,1;0rad)
  Points = (2) [(0,0,0),(-19,0,0)]
  Start = (171,-19,0)
  Subdivisions = 0
FEATURE [Part::Part2DObjectPython] Arc617  # Draft 2D object (typed FeaturePython)
  FirstAngle = 180
  LastAngle = 270
  MakeFace = false
  Placement = pos=(155,-16,0) rot=(0,0,1;0rad)
  Radius = 0.5
FEATURE [Part::Part2DObjectPython] Line1174  # Draft 2D object (typed FeaturePython)
  ChamferSize = 0
  Closed = false
  End = (152,-19,0)
  FilletRadius = 0
  Length = 19
  MakeFace = false
  Placement = pos=(152,0,0) rot=(0,0,1;0rad)
  Points = (2) [(0,0,0),(0,-19,0)]
  Start = (152,0,0)
  Subdivisions = 0
FEATURE [Part::Part2DObjectPython] Line1175  # Draft 2D object (typed FeaturePython)
  ChamferSize = 0
  Closed = false
  End = (168,-16.5,0)
  FilletRadius = 0
  Length = 13
  MakeFace = false
  Placement = pos=(155,-16.5,0) rot=(0,0,1;0rad)
  Points = (2) [(0,0,0),(13,0,0)]
  Start = (155,-16.5,0)
  Subdivisions = 0
FEATURE [Part::Part2DObjectPython] Line1176  # Draft 2D object (typed FeaturePython)
  ChamferSize = 0
  Closed = false
  End = (190,0,0)
  FilletRadius = 0
  Length = 19
  MakeFace = false
  Placement = pos=(171,0,0) rot=(0,0,1;0rad)
  Points = (2) [(0,0,0),(19,0,0)]
  Start = (171,0,0)
  Subdivisions = 0
FEATURE [Part::Part2DObjectPython] Arc618  # Draft 2D object (typed FeaturePython)
  FirstAngle = 90
  LastAngle = 180
  MakeFace = false
  Placement = pos=(174,-3,0) rot=(0,0,1;0rad)
  Radius = 0.5
FEATURE [Part::Part2DObjectPython] Line1177  # Draft 2D object (typed FeaturePython)
  ChamferSize = 0
  Closed = false
  End = (173.5,-16,0)
  FilletRadius = 0
  Length = 13
  MakeFace = false
  Placement = pos=(173.5,-3,0) rot=(0,0,1;0rad)
  Points = (2) [(0,0,0),(0,-13,0)]
  Start = (173.5,-3,0)
  Subdivisions = 0
FEATURE [Part::Part2DObjectPython] Line1178  # Draft 2D object (typed FeaturePython)
  ChamferSize = 0
  Closed = false
  End = (171,-19,0)
  FilletRadius = 0
  Length = 19
  MakeFace = false
  Placement = pos=(190,-19,0) rot=(0,0,1;0rad)
  Points = (2) [(0,0,0),(-19,0,0)]
  Start = (190,-19,0)
  Subdivisions = 0
FEATURE [Part::Part2DObjectPython] Line1179  # Draft 2D object (typed FeaturePython)
  ChamferSize = 0
  Closed = false
  End = (187,-16.5,0)
  FilletRadius = 0
  Length = 13
  MakeFace = false
  Placement = pos=(174,-16.5,0) rot=(0,0,1;0rad)
  Points = (2) [(0,0,0),(13,0,0)]
  Start = (174,-16.5,0)
  Subdivisions = 0
FEATURE [Part::Part2DObjectPython] Arc619  # Draft 2D object (typed FeaturePython)
  FirstAngle = -90
  LastAngle = 0
  MakeFace = false
  Placement = pos=(187,-16,0) rot=(0,0,1;0rad)
  Radius = 0.5
FEATURE [Part::Part2DObjectPython] Line1180  # Draft 2D object (typed FeaturePython)
  ChamferSize = 0
  Closed = false
  End = (187.5,-3,0)
  FilletRadius = 0
  Length = 13
  MakeFace = false
  Placement = pos=(187.5,-16,0) rot=(0,0,1;0rad)
  Points = (2) [(0,0,0),(0,13,0)]
  Start = (187.5,-16,0)
  Subdivisions = 0
FEATURE [Part::Part2DObjectPython] Arc620  # Draft 2D object (typed FeaturePython)
  FirstAngle = 180
  LastAngle = 270
  MakeFace = false
  Placement = pos=(174,-16,0) rot=(0,0,1;0rad)
  Radius = 0.5
FEATURE [Part::Part2DObjectPython] Line1181  # Draft 2D object (typed FeaturePython)
  ChamferSize = 0
  Closed = false
  End = (171,-19,0)
  FilletRadius = 0
  Length = 19
  MakeFace = false
  Placement = pos=(171,0,0) rot=(0,0,1;0rad)
  Points = (2) [(0,0,0),(0,-19,0)]
  Start = (171,0,0)
  Subdivisions = 0
FEATURE [Part::Part2DObjectPython] Line1182  # Draft 2D object (typed FeaturePython)
  ChamferSize = 0
  Closed = false
  End = (187,-2.5,0)
  FilletRadius = 0
  Length = 13
  MakeFace = false
  Placement = pos=(174,-2.5,0) rot=(0,0,1;0rad)
  Points = (2) [(0,0,0),(13,0,0)]
  Start = (174,-2.5,0)
  Subdivisions = 0
FEATURE [Part::Part2DObjectPython] Line1183  # Draft 2D object (typed FeaturePython)
  ChamferSize = 0
  Closed = false
  End = (19,-19,0)
  FilletRadius = 0
  Length = 19
  MakeFace = false
  Placement = pos=(19,0,0) rot=(0,0,1;0rad)
  Points = (2) [(0,0,0),(0,-19,0)]
  Start = (19,0,0)
  Subdivisions = 0
FEATURE [Part::Part2DObjectPython] Line1184  # Draft 2D object (typed FeaturePython)
  ChamferSize = 0
  Closed = false
  End = (0,-19,0)
  FilletRadius = 0
  Length = 19
  MakeFace = false
  Placement = pos=(19,-19,0) rot=(0,0,1;0rad)
  Points = (2) [(0,0,0),(-19,0,0)]
  Start = (19,-19,0)
  Subdivisions = 0
FEATURE [Part::Part2DObjectPython] Line1185  # Draft 2D object (typed FeaturePython)
  ChamferSize = 0
  Closed = false
  End = (16,-2.5,0)
  FilletRadius = 0
  Length = 13
  MakeFace = false
  Placement = pos=(3,-2.5,0) rot=(0,0,1;0rad)
  Points = (2) [(0,0,0),(13,0,0)]
  Start = (3,-2.5,0)
  Subdivisions = 0
FEATURE [Part::Part2DObjectPython] Line1186  # Draft 2D object (typed FeaturePython)
  ChamferSize = 0
  Closed = false
  End = (19,0,0)
  FilletRadius = 0
  Length = 19
  MakeFace = false
  Points = (2) [(0,0,0),(19,0,0)]
  Start = (0,0,0)
  Subdivisions = 0
FEATURE [Part::Part2DObjectPython] Arc621  # Draft 2D object (typed FeaturePython)
  FirstAngle = 90
  LastAngle = 180
  MakeFace = false
  Placement = pos=(251,-80,0) rot=(0,0,1;3.14159rad)
  Radius = 7.00001
FEATURE [Part::Part2DObjectPython] Line1187  # Draft 2D object (typed FeaturePython)
  ChamferSize = 0
  Closed = false
  End = (0,-19,0)
  FilletRadius = 0
  Length = 19
  MakeFace = false
  Points = (2) [(0,0,0),(0,-19,0)]
  Start = (0,0,0)
  Subdivisions = 0
FEATURE [Part::Part2DObjectPython] Line1188  # Draft 2D object (typed FeaturePython)
  ChamferSize = 0
  Closed = false
  End = (168.5,-3,0)
  FilletRadius = 0
  Length = 13
  MakeFace = false
  Placement = pos=(168.5,-16,0) rot=(0,0,1;0rad)
  Points = (2) [(0,0,0),(0,13,0)]
  Start = (168.5,-16,0)
  Subdivisions = 0
FEATURE [Part::Part2DObjectPython] Arc622  # Draft 2D object (typed FeaturePython)
  FirstAngle = -90
  LastAngle = 0
  MakeFace = false
  Placement = pos=(168,-16,0) rot=(0,0,1;0rad)
  Radius = 0.5
FEATURE [App::DocumentObjectGroup] Group135
  Group = -> [Line1156,Line1164,Line1173,Line1174,Line1170,Arc614,Arc613,Line1169,Arc617,Line1175,Arc622,Line1188]
FEATURE [Part::Part2DObjectPython] Line1189  # Draft 2D object (typed FeaturePython)
  ChamferSize = 0
  Closed = false
  End = (258,-80,0)
  FilletRadius = 0
  Length = 84
  MakeFace = false
  Placement = pos=(258,4,0) rot=(0,0,1;0rad)
  Points = (2) [(0,0,0),(0,-84,0)]
  Start = (258,4,0)
  Subdivisions = 0
FEATURE [Part::Part2DObjectPython] Arc623  # Draft 2D object (typed FeaturePython)
  FirstAngle = 0
  LastAngle = 90
  MakeFace = false
  Placement = pos=(16,-3,0) rot=(0,0,1;0rad)
  Radius = 0.5
FEATURE [Part::Part2DObjectPython] Arc624  # Draft 2D object (typed FeaturePython)
  FirstAngle = 0
  LastAngle = 90
  MakeFace = false
  Placement = pos=(106.25,-41,0) rot=(0,0,1;0rad)
  Radius = 0.5
FEATURE [Part::Part2DObjectPython] Arc625  # Draft 2D object (typed FeaturePython)
  FirstAngle = 0
  LastAngle = 90
  MakeFace = false
  Placement = pos=(251,4,0) rot=(0,0,1;0rad)
  Radius = 7.00001
FEATURE [Part::Part2DObjectPython] Arc626  # Draft 2D object (typed FeaturePython)
  FirstAngle = 0
  LastAngle = 90
  MakeFace = false
  Placement = pos=(-4,-80,0) rot=(0,0,1;3.14159rad)
  Radius = 7.00001
FEATURE [Part::Part2DObjectPython] Line1190  # Draft 2D object (typed FeaturePython)
  ChamferSize = 0
  Closed = false
  End = (251,11,0)
  FilletRadius = 0
  Length = 255
  MakeFace = false
  Placement = pos=(-4,11,0) rot=(0,0,1;0rad)
  Points = (2) [(0,0,0),(255,0,0)]
  Start = (-4,11,0)
  Subdivisions = 0
FEATURE [Part::Part2DObjectPython] Line1191  # Draft 2D object (typed FeaturePython)
  ChamferSize = 0
  Closed = false
  End = (-4,-87,0)
  FilletRadius = 0
  Length = 255
  MakeFace = false
  Placement = pos=(251,-87,0) rot=(0,0,1;0rad)
  Points = (2) [(0,0,0),(-255,2.84217e-14,0)]
  Start = (251,-87,0)
  Subdivisions = 0
FEATURE [Part::Part2DObjectPython] Arc627  # Draft 2D object (typed FeaturePython)
  FirstAngle = 90
  LastAngle = 180
  MakeFace = false
  Placement = pos=(3,-3,0) rot=(0,0,1;0rad)
  Radius = 0.5
FEATURE [Part::Part2DObjectPython] Line1192  # Draft 2D object (typed FeaturePython)
  ChamferSize = 0
  Closed = false
  End = (2.5,-16,0)
  FilletRadius = 0
  Length = 13
  MakeFace = false
  Placement = pos=(2.5,-3,0) rot=(0,0,1;0rad)
  Points = (2) [(0,0,0),(0,-13,0)]
  Start = (2.5,-3,0)
  Subdivisions = 0
FEATURE [Part::Part2DObjectPython] Arc628  # Draft 2D object (typed FeaturePython)
  FirstAngle = 90
  LastAngle = 180
  MakeFace = false
  Placement = pos=(-4,4,0) rot=(0,0,1;0rad)
  Radius = 7.00001
FEATURE [Part::Part2DObjectPython] Arc629  # Draft 2D object (typed FeaturePython)
  FirstAngle = 180
  LastAngle = 270
  MakeFace = false
  Placement = pos=(3,-16,0) rot=(0,0,1;0rad)
  Radius = 0.5
FEATURE [Part::Part2DObjectPython] Line1193  # Draft 2D object (typed FeaturePython)
  ChamferSize = 0
  Closed = false
  End = (16,-16.5,0)
  FilletRadius = 0
  Length = 13
  MakeFace = false
  Placement = pos=(3,-16.5,0) rot=(0,0,1;0rad)
  Points = (2) [(0,0,0),(13,0,0)]
  Start = (3,-16.5,0)
  Subdivisions = 0
FEATURE [Part::Part2DObjectPython] Line1194  # Draft 2D object (typed FeaturePython)
  ChamferSize = 0
  Closed = false
  End = (-11,4,0)
  FilletRadius = 0
  Length = 84
  MakeFace = false
  Placement = pos=(-11,-80,0) rot=(0,0,1;0rad)
  Points = (2) [(0,0,0),(0,84,0)]
  Start = (-11,-80,0)
  Subdivisions = 0
FEATURE [App::DocumentObjectGroup] Group092  label="Outside border001"
  Group = -> [Arc628,Arc625,Arc626,Arc621,Line1190,Line1189,Line1191,Line1194]
FEATURE [Part::Part2DObjectPython] Arc630  # Draft 2D object (typed FeaturePython)
  FirstAngle = -90
  LastAngle = 0
  MakeFace = false
  Placement = pos=(16,-16,0) rot=(0,0,1;0rad)
  Radius = 0.5
FEATURE [Part::Part2DObjectPython] Line1195  # Draft 2D object (typed FeaturePython)
  ChamferSize = 0
  Closed = false
  End = (16.5,-3,0)
  FilletRadius = 0
  Length = 13
  MakeFace = false
  Placement = pos=(16.5,-16,0) rot=(0,0,1;0rad)
  Points = (2) [(0,0,0),(0,13,0)]
  Start = (16.5,-16,0)
  Subdivisions = 0
FEATURE [App::DocumentObjectGroup] Group137
  Group = -> [Line1186,Line1183,Line1184,Line1187,Line1185,Arc623,Arc627,Line1192,Arc629,Line1193,Arc630,Line1195]
FEATURE [Part::Part2DObjectPython] Arc631  # Draft 2D object (typed FeaturePython)
  FirstAngle = 90
  LastAngle = 180
  MakeFace = false
  Placement = pos=(74.25,-41,0) rot=(0,0,1;0rad)
  Radius = 0.5
FEATURE [Part::Part2DObjectPython] Line1196  # Draft 2D object (typed FeaturePython)
  ChamferSize = 0
  Closed = false
  End = (90.25,-57,0)
  FilletRadius = 0
  Length = 19
  MakeFace = false
  Placement = pos=(90.25,-38,0) rot=(0,0,1;0rad)
  Points = (2) [(0,0,0),(0,-19,0)]
  Start = (90.25,-38,0)
  Subdivisions = 0
FEATURE [Part::Part2DObjectPython] Line1197  # Draft 2D object (typed FeaturePython)
  ChamferSize = 0
  Closed = false
  End = (73.75,-54,0)
  FilletRadius = 0
  Length = 13
  MakeFace = false
  Placement = pos=(73.75,-41,0) rot=(0,0,1;0rad)
  Points = (2) [(0,0,0),(0,-13,0)]
  Start = (73.75,-41,0)
  Subdivisions = 0
FEATURE [App::DocumentObjectGroup] Group144
  Group = -> [Line805,Line1196,Line807,Line802,Line808,Arc405,Arc631,Line1197,Arc415,Line797,Arc410,Line806]
FEATURE [Part::Part2DObjectPython] Arc632  # Draft 2D object (typed FeaturePython)
  FirstAngle = -90
  LastAngle = 0
  MakeFace = false
  Placement = pos=(106.25,-54,0) rot=(0,0,1;0rad)
  Radius = 0.5
FEATURE [Part::Part2DObjectPython] Arc633  # Draft 2D object (typed FeaturePython)
  FirstAngle = 90
  LastAngle = 180
  MakeFace = false
  Placement = pos=(22,-3,0) rot=(0,0,1;0rad)
  Radius = 0.5
FEATURE [Part::Part2DObjectPython] Line1198  # Draft 2D object (typed FeaturePython)
  ChamferSize = 0
  Closed = false
  End = (21.5,-16,0)
  FilletRadius = 0
  Length = 13
  MakeFace = false
  Placement = pos=(21.5,-3,0) rot=(0,0,1;0rad)
  Points = (2) [(0,0,0),(0,-13,0)]
  Start = (21.5,-3,0)
  Subdivisions = 0
FEATURE [Part::Part2DObjectPython] Arc634  # Draft 2D object (typed FeaturePython)
  FirstAngle = 180
  LastAngle = 270
  MakeFace = false
  Placement = pos=(41,-16,0) rot=(0,0,1;0rad)
  Radius = 0.5
FEATURE [Part::Part2DObjectPython] Arc635  # Draft 2D object (typed FeaturePython)
  FirstAngle = -90
  LastAngle = 0
  MakeFace = false
  Placement = pos=(73,-16,0) rot=(0,0,1;0rad)
  Radius = 0.5
FEATURE [Part::Part2DObjectPython] Line1199  # Draft 2D object (typed FeaturePython)
  ChamferSize = 0
  Closed = false
  End = (35,-2.5,0)
  FilletRadius = 0
  Length = 13
  MakeFace = false
  Placement = pos=(22,-2.5,0) rot=(0,0,1;0rad)
  Points = (2) [(0,0,0),(13,0,0)]
  Start = (22,-2.5,0)
  Subdivisions = 0
FEATURE [Part::Part2DObjectPython] Line1200  # Draft 2D object (typed FeaturePython)
  ChamferSize = 0
  Closed = false
  End = (106.25,-54.5,0)
  FilletRadius = 0
  Length = 13
  MakeFace = false
  Placement = pos=(93.25,-54.5,0) rot=(0,0,1;0rad)
  Points = (2) [(0,0,0),(13,0,0)]
  Start = (93.25,-54.5,0)
  Subdivisions = 0
FEATURE [App::DocumentObjectGroup] Group150
  Group = -> [Line1132,Line817,Line827,Line1131,Line821,Arc624,Arc419,Line820,Arc422,Line1200,Arc632,Line823]
FEATURE [Part::Part2DObjectPython] Line1201  # Draft 2D object (typed FeaturePython)
  ChamferSize = 0
  Closed = false
  End = (38,-19,0)
  FilletRadius = 0
  Length = 19
  MakeFace = false
  Placement = pos=(38,0,0) rot=(0,0,1;0rad)
  Points = (2) [(0,0,0),(0,-19,0)]
  Start = (38,0,0)
  Subdivisions = 0
FEATURE [Part::Part2DObjectPython] Line1202  # Draft 2D object (typed FeaturePython)
  ChamferSize = 0
  Closed = false
  End = (35,-16.5,0)
  FilletRadius = 0
  Length = 13
  MakeFace = false
  Placement = pos=(22,-16.5,0) rot=(0,0,1;0rad)
  Points = (2) [(0,0,0),(13,0,0)]
  Start = (22,-16.5,0)
  Subdivisions = 0
FEATURE [Part::Part2DObjectPython] Arc636  # Draft 2D object (typed FeaturePython)
  FirstAngle = 0
  LastAngle = 90
  MakeFace = false
  Placement = pos=(35,-3,0) rot=(0,0,1;0rad)
  Radius = 0.5
FEATURE [Part::Part2DObjectPython] Arc637  # Draft 2D object (typed FeaturePython)
  FirstAngle = -90
  LastAngle = 0
  MakeFace = false
  Placement = pos=(35,-16,0) rot=(0,0,1;0rad)
  Radius = 0.5
FEATURE [Part::Part2DObjectPython] Line1203  # Draft 2D object (typed FeaturePython)
  ChamferSize = 0
  Closed = false
  End = (57,-19,0)
  FilletRadius = 0
  Length = 19
  MakeFace = false
  Placement = pos=(57,0,0) rot=(0,0,1;0rad)
  Points = (2) [(0,0,0),(0,-19,0)]
  Start = (57,0,0)
  Subdivisions = 0
FEATURE [Part::Part2DObjectPython] Arc638  # Draft 2D object (typed FeaturePython)
  FirstAngle = 0
  LastAngle = 90
  MakeFace = false
  Placement = pos=(54,-3,0) rot=(0,0,1;0rad)
  Radius = 0.5
FEATURE [Part::Part2DObjectPython] Line1204  # Draft 2D object (typed FeaturePython)
  ChamferSize = 0
  Closed = false
  End = (19,-19,0)
  FilletRadius = 0
  Length = 19
  MakeFace = false
  Placement = pos=(38,-19,0) rot=(0,0,1;0rad)
  Points = (2) [(0,0,0),(-19,0,0)]
  Start = (38,-19,0)
  Subdivisions = 0
FEATURE [Part::Part2DObjectPython] Line1205  # Draft 2D object (typed FeaturePython)
  ChamferSize = 0
  Closed = false
  End = (35.5,-3,0)
  FilletRadius = 0
  Length = 13
  MakeFace = false
  Placement = pos=(35.5,-16,0) rot=(0,0,1;0rad)
  Points = (2) [(0,0,0),(0,13,0)]
  Start = (35.5,-16,0)
  Subdivisions = 0
FEATURE [Part::Part2DObjectPython] Arc639  # Draft 2D object (typed FeaturePython)
  FirstAngle = 90
  LastAngle = 180
  MakeFace = false
  Placement = pos=(41,-3,0) rot=(0,0,1;0rad)
  Radius = 0.5
FEATURE [Part::Part2DObjectPython] Line1206  # Draft 2D object (typed FeaturePython)
  ChamferSize = 0
  Closed = false
  End = (54,-2.5,0)
  FilletRadius = 0
  Length = 13
  MakeFace = false
  Placement = pos=(41,-2.5,0) rot=(0,0,1;0rad)
  Points = (2) [(0,0,0),(13,0,0)]
  Start = (41,-2.5,0)
  Subdivisions = 0
FEATURE [Part::Part2DObjectPython] Arc640  # Draft 2D object (typed FeaturePython)
  FirstAngle = -90
  LastAngle = 0
  MakeFace = false
  Placement = pos=(54,-16,0) rot=(0,0,1;0rad)
  Radius = 0.5
FEATURE [Part::Part2DObjectPython] Line1207  # Draft 2D object (typed FeaturePython)
  ChamferSize = 0
  Closed = false
  End = (38,-19,0)
  FilletRadius = 0
  Length = 19
  MakeFace = false
  Placement = pos=(57,-19,0) rot=(0,0,1;0rad)
  Points = (2) [(0,0,0),(-19,0,0)]
  Start = (57,-19,0)
  Subdivisions = 0
FEATURE [Part::Part2DObjectPython] Arc641  # Draft 2D object (typed FeaturePython)
  FirstAngle = 180
  LastAngle = 270
  MakeFace = false
  Placement = pos=(22,-16,0) rot=(0,0,1;0rad)
  Radius = 0.5
FEATURE [Part::Part2DObjectPython] Line1208  # Draft 2D object (typed FeaturePython)
  ChamferSize = 0
  Closed = false
  End = (40.5,-16,0)
  FilletRadius = 0
  Length = 13
  MakeFace = false
  Placement = pos=(40.5,-3,0) rot=(0,0,1;0rad)
  Points = (2) [(0,0,0),(0,-13,0)]
  Start = (40.5,-3,0)
  Subdivisions = 0
FEATURE [Part::Part2DObjectPython] Line1209  # Draft 2D object (typed FeaturePython)
  ChamferSize = 0
  Closed = false
  End = (54,-16.5,0)
  FilletRadius = 0
  Length = 13
  MakeFace = false
  Placement = pos=(41,-16.5,0) rot=(0,0,1;0rad)
  Points = (2) [(0,0,0),(13,0,0)]
  Start = (41,-16.5,0)
  Subdivisions = 0
FEATURE [Part::Part2DObjectPython] Line1210  # Draft 2D object (typed FeaturePython)
  ChamferSize = 0
  Closed = false
  End = (54.5,-3,0)
  FilletRadius = 0
  Length = 13
  MakeFace = false
  Placement = pos=(54.5,-16,0) rot=(0,0,1;0rad)
  Points = (2) [(0,0,0),(0,13,0)]
  Start = (54.5,-16,0)
  Subdivisions = 0
FEATURE [Part::Part2DObjectPython] Line1211  # Draft 2D object (typed FeaturePython)
  ChamferSize = 0
  Closed = false
  End = (57,0,0)
  FilletRadius = 0
  Length = 19
  MakeFace = false
  Placement = pos=(38,0,0) rot=(0,0,1;0rad)
  Points = (2) [(0,0,0),(19,0,0)]
  Start = (38,0,0)
  Subdivisions = 0
FEATURE [Part::Part2DObjectPython] Line1212  # Draft 2D object (typed FeaturePython)
  ChamferSize = 0
  Closed = false
  End = (38,-19,0)
  FilletRadius = 0
  Length = 19
  MakeFace = false
  Placement = pos=(38,0,0) rot=(0,0,1;0rad)
  Points = (2) [(0,0,0),(0,-19,0)]
  Start = (38,0,0)
  Subdivisions = 0
FEATURE [App::DocumentObjectGroup] Group094
  Group = -> [Line1211,Line1203,Line1207,Line1212,Line1206,Arc638,Arc639,Line1208,Arc634,Line1209,Arc640,Line1210]
FEATURE [Part::Part2DObjectPython] Arc642  # Draft 2D object (typed FeaturePython)
  FirstAngle = 180
  LastAngle = 270
  MakeFace = false
  Placement = pos=(60,-16,0) rot=(0,0,1;0rad)
  Radius = 0.5
FEATURE [Part::Part2DObjectPython] Line1213  # Draft 2D object (typed FeaturePython)
  ChamferSize = 0
  Closed = false
  End = (76,-19,0)
  FilletRadius = 0
  Length = 19
  MakeFace = false
  Placement = pos=(76,0,0) rot=(0,0,1;0rad)
  Points = (2) [(0,0,0),(0,-19,0)]
  Start = (76,0,0)
  Subdivisions = 0
FEATURE [Part::Part2DObjectPython] Line1214  # Draft 2D object (typed FeaturePython)
  ChamferSize = 0
  Closed = false
  End = (38,0,0)
  FilletRadius = 0
  Length = 19
  MakeFace = false
  Placement = pos=(19,0,0) rot=(0,0,1;0rad)
  Points = (2) [(0,0,0),(19,0,0)]
  Start = (19,0,0)
  Subdivisions = 0
FEATURE [Part::Part2DObjectPython] Line1215  # Draft 2D object (typed FeaturePython)
  ChamferSize = 0
  Closed = false
  End = (19,-19,0)
  FilletRadius = 0
  Length = 19
  MakeFace = false
  Placement = pos=(19,0,0) rot=(0,0,1;0rad)
  Points = (2) [(0,0,0),(0,-19,0)]
  Start = (19,0,0)
  Subdivisions = 0
FEATURE [App::DocumentObjectGroup] Group093
  Group = -> [Line1214,Line1201,Line1204,Line1215,Line1199,Arc636,Arc633,Line1198,Arc641,Line1202,Arc637,Line1205]
FEATURE [Part::Part2DObjectPython] Arc643  # Draft 2D object (typed FeaturePython)
  FirstAngle = 0
  LastAngle = 90
  MakeFace = false
  Placement = pos=(73,-3,0) rot=(0,0,1;0rad)
  Radius = 0.5
FEATURE [Part::Part2DObjectPython] Arc644  # Draft 2D object (typed FeaturePython)
  FirstAngle = 90
  LastAngle = 180
  MakeFace = false
  Placement = pos=(60,-3,0) rot=(0,0,1;0rad)
  Radius = 0.5
FEATURE [Part::Part2DObjectPython] Line1216  # Draft 2D object (typed FeaturePython)
  ChamferSize = 0
  Closed = false
  End = (73,-2.5,0)
  FilletRadius = 0
  Length = 13
  MakeFace = false
  Placement = pos=(60,-2.5,0) rot=(0,0,1;0rad)
  Points = (2) [(0,0,0),(13,0,0)]
  Start = (60,-2.5,0)
  Subdivisions = 0
FEATURE [Part::Part2DObjectPython] Line1217  # Draft 2D object (typed FeaturePython)
  ChamferSize = 0
  Closed = false
  End = (57,-19,0)
  FilletRadius = 0
  Length = 19
  MakeFace = false
  Placement = pos=(76,-19,0) rot=(0,0,1;0rad)
  Points = (2) [(0,0,0),(-19,0,0)]
  Start = (76,-19,0)
  Subdivisions = 0
FEATURE [Part::Part2DObjectPython] Line1218  # Draft 2D object (typed FeaturePython)
  ChamferSize = 0
  Closed = false
  End = (59.5,-16,0)
  FilletRadius = 0
  Length = 13
  MakeFace = false
  Placement = pos=(59.5,-3,0) rot=(0,0,1;0rad)
  Points = (2) [(0,0,0),(0,-13,0)]
  Start = (59.5,-3,0)
  Subdivisions = 0
FEATURE [Part::Part2DObjectPython] Line1219  # Draft 2D object (typed FeaturePython)
  ChamferSize = 0
  Closed = false
  End = (73,-16.5,0)
  FilletRadius = 0
  Length = 13
  MakeFace = false
  Placement = pos=(60,-16.5,0) rot=(0,0,1;0rad)
  Points = (2) [(0,0,0),(13,0,0)]
  Start = (60,-16.5,0)
  Subdivisions = 0
FEATURE [Part::Part2DObjectPython] Line1220  # Draft 2D object (typed FeaturePython)
  ChamferSize = 0
  Closed = false
  End = (73.5,-3,0)
  FilletRadius = 0
  Length = 13
  MakeFace = false
  Placement = pos=(73.5,-16,0) rot=(0,0,1;0rad)
  Points = (2) [(0,0,0),(0,13,0)]
  Start = (73.5,-16,0)
  Subdivisions = 0
FEATURE [App::DocumentObjectGroup] Group099
  Group = -> [Line1135,Line1213,Line1217,Line1151,Line1216,Arc643,Arc644,Line1218,Arc642,Line1219,Arc635,Line1220]
FEATURE [App::DocumentObjectGroup] Group156
  Group = -> [Line730,Line728,Line736,Line734,Line737,Arc380,Arc377,Line731,Arc368,Line733,Arc379,Line729]
FEATURE [App::DocumentObjectGroup] Group157
  Group = -> [Line1144,Line1146,Line1142,Line1137,Line1149,Arc602,Arc601,Line1139,Arc600,Line1140,Arc599,Line1148]
FEATURE [App::DocumentObjectGroup] Group158
  Group = -> [Line1176,Line1158,Line1178,Line1181,Line1182,Arc610,Arc618,Line1177,Arc620,Line1179,Arc619,Line1180]
FEATURE [App::DocumentObjectGroup] Group159
  Group = -> [Line694,Line692,Line690,Line688,Line695,Arc361,Arc360,Line693,Arc356,Line691,Arc357,Line689]
FEATURE [App::DocumentObjectGroup] Group102  label="Row 005"
  Group = -> [Group131,Group159,Group133,Group103,Group136,Group139,Group156,Group134,Group143,Group154,Group142,Group152]
FEATURE [App::DocumentObjectGroup] Group160  label="full 004"
  Group = -> [Group121,Group125,Group105,Group116,Group110,Group111]
FEATURE [App::DocumentObjectGroup] Group123  label="Row 4 full001"
  Group = -> [Group160,Group114]
FEATURE [App::DocumentObjectGroup] Group161
  Group = -> [Line908,Line897,Line918,Line914,Line907,Arc456,Arc455,Line915,Arc465,Line916,Line917,Arc466]
FEATURE [App::DocumentObjectGroup] Group162
  Group = -> [Line899,Line904,Line913,Line924,Line909,Arc471,Arc472,Line928,Arc468,Line922,Arc470,Line923]
FEATURE [App::DocumentObjectGroup] Group163
  Group = -> [Line864,Line868,Line861,Line856,Line869,Arc445,Arc446,Line855,Arc442,Line854,Arc439,Line853]
FEATURE [App::DocumentObjectGroup] Group164
  Group = -> [Line873,Line887,Line884,Line885,Line890,Arc452,Arc453,Line875,Arc440,Line880,Arc448,Line879]
FEATURE [App::DocumentObjectGroup] Group165
  Group = -> [Line903,Line919,Line932,Line935,Line920,Arc467,Arc457,Line925,Arc469,Line929,Line921,Arc473]
FEATURE [App::DocumentObjectGroup] Group166
  Group = -> [Line865,Line851,Line866,Line852,Line860,Arc444,Arc447,Line857,Arc443,Line858,Line859,Arc438]
FEATURE [App::DocumentObjectGroup] Group168
  Group = -> [Line927,Line937,Line933,Line953,Line931,Arc480,Arc482,Line955,Arc476,Line938,Arc478,Line943]
FEATURE [App::DocumentObjectGroup] Group109  label="split 003"
  Group = -> [Group161,Group165,Group162,Group168,Group101,Group115,Group118,Group126,Group106,Group127]
FEATURE [App::DocumentObjectGroup] Group167  label="Row 4 split001"
  Group = -> [Group109,Group120]
FEATURE [App::DocumentObjectGroup] Group169  label="full backspace001"
  Group = -> [Line877,Line881,Line878,Line872,Arc463,Arc454,Line892,Arc459,Arc462,Line898,Line902,Arc460,Arc458,Line906,Arc461,Arc464,Line895,Line896,Line911,Line912]
FEATURE [App::DocumentObjectGroup] Group098  label="Row 004"
  Group = -> [Group137,Group093,Group094,Group099,Group095,Group157,Group096,Group138,Group135,Group158,Group140,Group100,Group132,Group169]
FEATURE [App::DocumentObjectGroup] Group170
  Group = -> [Line876,Line870,Line891,Line871,Line889,Arc451,Arc450,Line883,Arc449,Line888,Line886,Arc441]
FEATURE [App::DocumentObjectGroup] Group153  label="Row 006"
  Group = -> [Group141,Group149,Group155,Group144,Group150,Group151,Group146,Group145,Group147,Group148,Group163,Group166,Group164,Group170]
FEATURE [App::DocumentObjectGroup] Group097  label="Switches001"
  Group = -> [Group098,Group102,Group153,Group167,Group123]
FEATURE [App::DocumentObjectGroup] Group104  label="Switch layer 5mm backup"
  Group = -> [Group092,Group097,Group130,Group129]
FEATURE [Part::Part2DObjectPython] Line1221  # Draft 2D object (typed FeaturePython)
  ChamferSize = 0
  Closed = false
  End = (207.25,-40.5,0)
  FilletRadius = 0
  Length = 15.375
  MakeFace = false
  Placement = pos=(222.625,-40.5,0) rot=(0,0,1;0rad)
  Points = (2) [(0,0,0),(-15.375,0,0)]
  Start = (222.625,-40.5,0)
  Subdivisions = 0
FEATURE [Part::Part2DObjectPython] Line1222  # Draft 2D object (typed FeaturePython)
  ChamferSize = 0
  Closed = false
  End = (222.625,-54.5,0)
  FilletRadius = 0
  Length = 15.375
  MakeFace = false
  Placement = pos=(207.25,-54.5,0) rot=(0,0,1;0rad)
  Points = (2) [(0,0,0),(15.375,0,0)]
  Start = (207.25,-54.5,0)
  Subdivisions = 0
FEATURE [Part::Part2DObjectPython] Line1223  # Draft 2D object (typed FeaturePython)
  ChamferSize = 0
  Closed = false
  End = (228.625,-40.5,0)
  FilletRadius = 0
  Length = 15.375
  MakeFace = false
  Placement = pos=(244,-40.5,0) rot=(0,0,1;0rad)
  Points = (2) [(0,0,0),(-15.375,0,0)]
  Start = (244,-40.5,0)
  Subdivisions = 0
FEATURE [Part::Part2DObjectPython] Line1224  # Draft 2D object (typed FeaturePython)
  ChamferSize = 0
  Closed = false
  End = (244,-54.5,0)
  FilletRadius = 0
  Length = 15.375
  MakeFace = false
  Placement = pos=(228.625,-54.5,0) rot=(0,0,1;0rad)
  Points = (2) [(0,0,0),(15.375,0,0)]
  Start = (228.625,-54.5,0)
  Subdivisions = 0
FEATURE [App::DocumentObjectGroup] Group036  label="Row 3"
  Group = -> [Group037,Group038,Group039,Group040,Group041,Group042,Group043,Group044,Group045,Group046,Group047,Group048,Group049,Group050,Line1222,Line1221,Line1224,Line1223]
FEATURE [Part::Part2DObjectPython] Arc645  # Draft 2D object (typed FeaturePython)
  FirstAngle = -90
  LastAngle = 0
  MakeFace = false
  Placement = pos=(212,-2.188,0) rot=(0,0,1;0rad)
  Radius = 0.312
FEATURE [Part::Part2DObjectPython] Arc646  # Draft 2D object (typed FeaturePython)
  FirstAngle = 180
  LastAngle = 270
  MakeFace = false
  Placement = pos=(244,-2.188,0) rot=(0,0,1;0rad)
  Radius = 0.312
FEATURE [Part::Part2DObjectPython] Arc647  # Draft 2D object (typed FeaturePython)
  FirstAngle = 90
  LastAngle = 180
  MakeFace = false
  Placement = pos=(244,-16.812,0) rot=(0,0,1;0rad)
  Radius = 0.312
FEATURE [Part::Part2DObjectPython] Line1225  # Draft 2D object (typed FeaturePython)
  ChamferSize = 0
  Closed = false
  End = (243.688,-19.5,0)
  FilletRadius = 0
  Length = 2.688
  MakeFace = false
  Placement = pos=(243.688,-16.812,0) rot=(0,0,1;0rad)
  Points = (2) [(0,0,0),(0,-2.688,0)]
  Start = (243.688,-16.812,0)
  Subdivisions = 0
FEATURE [Part::Part2DObjectPython] Arc648  # Draft 2D object (typed FeaturePython)
  FirstAngle = 0
  LastAngle = 90
  MakeFace = false
  Placement = pos=(212,-16.812,0) rot=(0,0,1;0rad)
  Radius = 0.312
FEATURE [Part::Part2DObjectPython] Line1226  # Draft 2D object (typed FeaturePython)
  ChamferSize = 0
  Closed = false
  End = (212.312,-0.3,0)
  FilletRadius = 0
  Length = 1.888
  MakeFace = false
  Placement = pos=(212.312,-2.188,0) rot=(0,0,1;0rad)
  Points = (2) [(0,0,0),(0,1.888,0)]
  Start = (212.312,-2.188,0)
  Subdivisions = 0
FEATURE [Part::Part2DObjectPython] Line1227  # Draft 2D object (typed FeaturePython)
  ChamferSize = 0
  Closed = false
  End = (212.312,-19.5,0)
  FilletRadius = 0
  Length = 2.688
  MakeFace = false
  Placement = pos=(212.312,-16.812,0) rot=(0,0,1;0rad)
  Points = (2) [(0,0,0),(0,-2.688,0)]
  Start = (212.312,-16.812,0)
  Subdivisions = 0
FEATURE [Part::Part2DObjectPython] Line1228  # Draft 2D object (typed FeaturePython)
  ChamferSize = 0
  Closed = false
  End = (243.688,-0.3,0)
  FilletRadius = 0
  Length = 1.888
  MakeFace = false
  Placement = pos=(243.688,-2.188,0) rot=(0,0,1;0rad)
  Points = (2) [(0,0,0),(0,1.888,0)]
  Start = (243.688,-2.188,0)
  Subdivisions = 0
FEATURE [App::DocumentObjectGroup] Group052  label="full backspace"
  Group = -> [Arc176,Arc177,Line363,Arc178,Arc179,Line364,Arc180,Arc181,Line367,Arc182,Arc183,Line368,Line369,Line370,Arc648,Line1227,Arc645,Line1226,Line1228,Arc646,Arc647,Line1225]
FEATURE [App::DocumentObjectGroup] Group009  label="Row 1"
  Group = -> [Group010,Group011,Group012,Group013,Group014,Group015,Group016,Group017,Group018,Group019,Group020,Group021,Group022,Group052]
FEATURE [Part::Part2DObjectPython] Line1229  # Draft 2D object (typed FeaturePython)
  ChamferSize = 0
  Closed = false
  End = (155.313,-56,0)
  FilletRadius = 0
  Length = 32.751
  MakeFace = false
  Placement = pos=(122.562,-56,0) rot=(0,0,1;0rad)
  Points = (2) [(0,0,0),(32.751,-2.84217e-14,0)]
  Start = (122.562,-56,0)
  Subdivisions = 0
FEATURE [Part::Part2DObjectPython] Line1230  # Draft 2D object (typed FeaturePython)
  ChamferSize = 0
  Closed = false
  End = (146.438,-76.2,0)
  FilletRadius = 0
  Length = 8.875
  MakeFace = false
  Placement = pos=(155.313,-76.2,0) rot=(0,0,1;0rad)
  Points = (2) [(0,0,0),(-8.875,2.84217e-14,0)]
  Start = (155.313,-76.2,0)
  Subdivisions = 0
FEATURE [Part::Part2DObjectPython] Line1231  # Draft 2D object (typed FeaturePython)
  ChamferSize = 0
  Closed = false
  End = (132.437,-73.5,0)
  FilletRadius = 0
  Length = 13.001
  MakeFace = false
  Placement = pos=(145.438,-73.5,0) rot=(0,0,1;0rad)
  Points = (2) [(0,0,0),(-13.001,-1.42109e-14,0)]
  Start = (145.438,-73.5,0)
  Subdivisions = 0
FEATURE [Part::Part2DObjectPython] Line1232  # Draft 2D object (typed FeaturePython)
  ChamferSize = 0
  Closed = false
  End = (122.562,-76.2,0)
  FilletRadius = 0
  Length = 8.875
  MakeFace = false
  Placement = pos=(131.437,-76.2,0) rot=(0,0,1;0rad)
  Points = (2) [(0,0,0),(-8.875,2.84217e-14,0)]
  Start = (131.437,-76.2,0)
  Subdivisions = 0
FEATURE [Part::Part2DObjectPython] Arc649  # Draft 2D object (typed FeaturePython)
  FirstAngle = -180
  LastAngle = -90
  MakeFace = false
  Placement = pos=(108.625,-59.188,0) rot=(0,0,1;0rad)
  Radius = 0.312
FEATURE [Part::Part2DObjectPython] Arc650  # Draft 2D object (typed FeaturePython)
  FirstAngle = 90
  LastAngle = 180
  MakeFace = false
  Placement = pos=(108.625,-73.812,0) rot=(0,0,1;0rad)
  Radius = 0.312
FEATURE [Part::Part2DObjectPython] Line1233  # Draft 2D object (typed FeaturePython)
  ChamferSize = 0
  Closed = false
  End = (108.313,-56.5,0)
  FilletRadius = 0
  Length = 2.688
  MakeFace = false
  Placement = pos=(108.313,-59.188,0) rot=(0,0,1;0rad)
  Points = (2) [(0,0,0),(2.84217e-14,2.688,0)]
  Start = (108.313,-59.188,0)
  Subdivisions = 0
FEATURE [Part::Part2DObjectPython] Line1234  # Draft 2D object (typed FeaturePython)
  ChamferSize = 0
  Closed = false
  End = (108.313,-75.7,0)
  FilletRadius = 0
  Length = 1.888
  MakeFace = false
  Placement = pos=(108.313,-73.812,0) rot=(0,0,1;0rad)
  Points = (2) [(0,0,0),(0,-1.888,0)]
  Start = (108.313,-73.812,0)
  Subdivisions = 0
FEATURE [Part::Part2DObjectPython] Arc651  # Draft 2D object (typed FeaturePython)
  FirstAngle = -90
  LastAngle = 0
  MakeFace = false
  Placement = pos=(76.437,-59,0) rot=(0,0,1;0rad)
  Radius = 0.5
FEATURE [Part::Part2DObjectPython] Arc652  # Draft 2D object (typed FeaturePython)
  FirstAngle = 0
  LastAngle = 90
  MakeFace = false
  Placement = pos=(76.437,-74,0) rot=(0,0,1;0rad)
  Radius = 0.5
FEATURE [Part::Part2DObjectPython] Line1235  # Draft 2D object (typed FeaturePython)
  ChamferSize = 0
  Closed = false
  End = (76.937,-56.5,0)
  FilletRadius = 0
  Length = 2.5
  MakeFace = false
  Placement = pos=(76.937,-59,0) rot=(0,0,1;0rad)
  Points = (2) [(0,0,0),(0,2.5,0)]
  Start = (76.937,-59,0)
  Subdivisions = 0
FEATURE [Part::Part2DObjectPython] Line1236  # Draft 2D object (typed FeaturePython)
  ChamferSize = 0
  Closed = false
  End = (69.5,-59.5,0)
  FilletRadius = 0
  Length = 6.937
  MakeFace = false
  Placement = pos=(76.437,-59.5,0) rot=(0,0,1;0rad)
  Points = (2) [(0,0,0),(-6.937,0,0)]
  Start = (76.437,-59.5,0)
  Subdivisions = 0
FEATURE [Part::Part2DObjectPython] Line1237  # Draft 2D object (typed FeaturePython)
  ChamferSize = 0
  Closed = false
  End = (76.437,-73.5,0)
  FilletRadius = 0
  Length = 6.937
  MakeFace = false
  Placement = pos=(69.5,-73.5,0) rot=(0,0,1;0rad)
  Points = (2) [(0,0,0),(6.937,0,0)]
  Start = (69.5,-73.5,0)
  Subdivisions = 0
FEATURE [Part::Part2DObjectPython] Line1238  # Draft 2D object (typed FeaturePython)
  ChamferSize = 0
  Closed = false
  End = (76.937,-75.7,0)
  FilletRadius = 0
  Length = 1.7
  MakeFace = false
  Placement = pos=(76.937,-74,0) rot=(0,0,1;0rad)
  Points = (2) [(0,0,0),(-4.26326e-14,-1.7,0)]
  Start = (76.937,-74,0)
  Subdivisions = 0
FEATURE [Part::Part2DObjectPython] Line1239  # Draft 2D object (typed FeaturePython)
  ChamferSize = 0
  Closed = false
  End = (50.5,-59.5,0)
  FilletRadius = 0
  Length = 15.375
  MakeFace = false
  Placement = pos=(65.875,-59.5,0) rot=(0,0,1;0rad)
  Points = (2) [(0,0,0),(-15.375,0,0)]
  Start = (65.875,-59.5,0)
  Subdivisions = 0
FEATURE [Part::Part2DObjectPython] Line1240  # Draft 2D object (typed FeaturePython)
  ChamferSize = 0
  Closed = false
  End = (65.875,-73.5,0)
  FilletRadius = 0
  Length = 15.375
  MakeFace = false
  Placement = pos=(50.5,-73.5,0) rot=(0,0,1;0rad)
  Points = (2) [(0,0,0),(15.375,0,0)]
  Start = (50.5,-73.5,0)
  Subdivisions = 0
FEATURE [Part::Part2DObjectPython] Line1241  # Draft 2D object (typed FeaturePython)
  ChamferSize = 0
  Closed = false
  End = (159.75,-59.5,0)
  FilletRadius = 0
  Length = 41.5
  MakeFace = false
  Placement = pos=(201.25,-59.5,0) rot=(0,0,1;0rad)
  Points = (2) [(0,0,0),(-41.5,1.42109e-14,0)]
  Start = (201.25,-59.5,0)
  Subdivisions = 0
FEATURE [Part::Part2DObjectPython] Line1242  # Draft 2D object (typed FeaturePython)
  ChamferSize = 0
  Closed = false
  End = (201.25,-73.5,0)
  FilletRadius = 0
  Length = 41.5
  MakeFace = false
  Placement = pos=(159.75,-73.5,0) rot=(0,0,1;0rad)
  Points = (2) [(0,0,0),(41.5,-1.42109e-14,0)]
  Start = (159.75,-73.5,0)
  Subdivisions = 0
FEATURE [Part::Part2DObjectPython] Line1243  # Draft 2D object (typed FeaturePython)
  ChamferSize = 0
  Closed = false
  End = (220.25,-59.5,0)
  FilletRadius = 0
  Length = 15.375
  MakeFace = false
  Placement = pos=(204.875,-59.5,0) rot=(0,0,1;0rad)
  Points = (2) [(0,0,0),(15.375,-1.42109e-14,0)]
  Start = (204.875,-59.5,0)
  Subdivisions = 0
FEATURE [Part::Part2DObjectPython] Line1244  # Draft 2D object (typed FeaturePython)
  ChamferSize = 0
  Closed = false
  End = (204.875,-73.5,0)
  FilletRadius = 0
  Length = 15.375
  MakeFace = false
  Placement = pos=(220.25,-73.5,0) rot=(0,0,1;0rad)
  Points = (2) [(0,0,0),(-15.375,1.42109e-14,0)]
  Start = (220.25,-73.5,0)
  Subdivisions = 0
FEATURE [App::DocumentObjectGroup] Group051  label="Row 4 split"
  Group = -> [Group063,Group064,Line1229,Line1230,Line1231,Line1232,Arc649,Arc650,Line1233,Line1234,Arc651,Arc652,Line1235,Line1236,Line1237,Line1238,Line1239,Line1240,Line1241,Line1242,Line1243,Line1244]
FEATURE [Part::Part2DObjectPython] Line1245  # Draft 2D object (typed FeaturePython)
  ChamferSize = 0
  Closed = false
  End = (61.125,-59.5,0)
  FilletRadius = 0
  Length = 15.375
  MakeFace = false
  Placement = pos=(45.75,-59.5,0) rot=(0,0,1;0rad)
  Points = (2) [(0,0,0),(15.375,0,0)]
  Start = (45.75,-59.5,0)
  Subdivisions = 0
FEATURE [Part::Part2DObjectPython] Line1246  # Draft 2D object (typed FeaturePython)
  ChamferSize = 0
  Closed = false
  End = (45.75,-73.5,0)
  FilletRadius = 0
  Length = 15.375
  MakeFace = false
  Placement = pos=(61.125,-73.5,0) rot=(0,0,1;0rad)
  Points = (2) [(0,0,0),(-15.375,0,0)]
  Start = (61.125,-73.5,0)
  Subdivisions = 0
FEATURE [Part::Part2DObjectPython] Line1247  # Draft 2D object (typed FeaturePython)
  ChamferSize = 0
  Closed = false
  End = (113.625,-59.5,0)
  FilletRadius = 0
  Length = 33.525
  MakeFace = false
  Placement = pos=(80.1,-59.5,0) rot=(0,0,1;0rad)
  Points = (2) [(0,0,0),(33.525,0,0)]
  Start = (80.1,-59.5,0)
  Subdivisions = 0
FEATURE [Part::Part2DObjectPython] Line1248  # Draft 2D object (typed FeaturePython)
  ChamferSize = 0
  Closed = false
  End = (79.1,-76.2,0)
  FilletRadius = 0
  Length = 11.263
  MakeFace = false
  Placement = pos=(67.837,-76.2,0) rot=(0,0,1;0rad)
  Points = (2) [(0,0,0),(11.263,0,0)]
  Start = (67.837,-76.2,0)
  Subdivisions = 0
FEATURE [Part::Part2DObjectPython] Line1249  # Draft 2D object (typed FeaturePython)
  ChamferSize = 0
  Closed = false
  End = (193.4,-56,0)
  FilletRadius = 0
  Length = 125.563
  MakeFace = false
  Placement = pos=(67.837,-56,0) rot=(0,0,1;0rad)
  Points = (2) [(0,0,0),(125.563,0,0)]
  Start = (67.837,-56,0)
  Subdivisions = 0
FEATURE [Part::Part2DObjectPython] Line1250  # Draft 2D object (typed FeaturePython)
  ChamferSize = 0
  Closed = false
  End = (174.913,-60,0)
  FilletRadius = 0
  Length = 15.7
  MakeFace = false
  Placement = pos=(174.913,-75.7,0) rot=(0,0,1;0rad)
  Points = (2) [(0,0,0),(0,15.7,0)]
  Start = (174.913,-75.7,0)
  Subdivisions = 0
FEATURE [Part::Part2DObjectPython] Arc653  # Draft 2D object (typed FeaturePython)
  FirstAngle = 90
  LastAngle = 180
  MakeFace = false
  Placement = pos=(175.413,-60,0) rot=(0,0,1;0rad)
  Radius = 0.5
FEATURE [Part::Part2DObjectPython] Line1251  # Draft 2D object (typed FeaturePython)
  ChamferSize = 0
  Closed = false
  End = (140.5,-59.5,0)
  FilletRadius = 0
  Length = 26.413
  MakeFace = false
  Placement = pos=(166.913,-59.5,0) rot=(0,0,1;0rad)
  Points = (2) [(0,0,0),(-26.413,0,0)]
  Start = (166.913,-59.5,0)
  Subdivisions = 0
FEATURE [Part::Part2DObjectPython] Line1252  # Draft 2D object (typed FeaturePython)
  ChamferSize = 0
  Closed = false
  End = (175.413,-59.5,0)
  FilletRadius = 0
  Length = 7.087
  MakeFace = false
  Placement = pos=(182.5,-59.5,0) rot=(0,0,1;0rad)
  Points = (2) [(0,0,0),(-7.087,0,0)]
  Start = (182.5,-59.5,0)
  Subdivisions = 0
FEATURE [Part::Part2DObjectPython] Arc654  # Draft 2D object (typed FeaturePython)
  FirstAngle = -180
  LastAngle = -90
  MakeFace = false
  Placement = pos=(194.4,-59,0) rot=(0,0,1;0rad)
  Radius = 0.5
FEATURE [Part::Part2DObjectPython] Line1253  # Draft 2D object (typed FeaturePython)
  ChamferSize = 0
  Closed = false
  End = (196.5,-59.5,0)
  FilletRadius = 0
  Length = 2.1
  MakeFace = false
  Placement = pos=(194.4,-59.5,0) rot=(0,0,1;0rad)
  Points = (2) [(0,0,0),(2.1,0,0)]
  Start = (194.4,-59.5,0)
  Subdivisions = 0
FEATURE [Part::Part2DObjectPython] Arc655  # Draft 2D object (typed FeaturePython)
  FirstAngle = 90
  LastAngle = 180
  MakeFace = false
  Placement = pos=(194.4,-74,0) rot=(0,0,1;0rad)
  Radius = 0.5
FEATURE [Part::Part2DObjectPython] Arc656  # Draft 2D object (typed FeaturePython)
  FirstAngle = 0
  LastAngle = 90
  MakeFace = false
  Placement = pos=(185.9,-74,0) rot=(0,0,1;0rad)
  Radius = 0.5
FEATURE [Part::Part2DObjectPython] Line1254  # Draft 2D object (typed FeaturePython)
  ChamferSize = 0
  Closed = false
  End = (193.9,-56.5,0)
  FilletRadius = 0
  Length = 2.5
  MakeFace = false
  Placement = pos=(193.9,-59,0) rot=(0,0,1;0rad)
  Points = (2) [(0,0,0),(0,2.5,0)]
  Start = (193.9,-59,0)
  Subdivisions = 0
FEATURE [Part::Part2DObjectPython] Line1255  # Draft 2D object (typed FeaturePython)
  ChamferSize = 0
  Closed = false
  End = (194.4,-73.5,0)
  FilletRadius = 0
  Length = 2.1
  MakeFace = false
  Placement = pos=(196.5,-73.5,0) rot=(0,0,1;0rad)
  Points = (2) [(0,0,0),(-2.1,0,0)]
  Start = (196.5,-73.5,0)
  Subdivisions = 0
FEATURE [Part::Part2DObjectPython] Line1256  # Draft 2D object (typed FeaturePython)
  ChamferSize = 0
  Closed = false
  End = (193.9,-75.7,0)
  FilletRadius = 0
  Length = 1.7
  MakeFace = false
  Placement = pos=(193.9,-74,0) rot=(0,0,1;0rad)
  Points = (2) [(0,0,0),(0,-1.7,0)]
  Start = (193.9,-74,0)
  Subdivisions = 0
FEATURE [Part::Part2DObjectPython] Line1257  # Draft 2D object (typed FeaturePython)
  ChamferSize = 0
  Closed = false
  End = (186.4,-74,0)
  FilletRadius = 0
  Length = 1.7
  MakeFace = false
  Placement = pos=(186.4,-75.7,0) rot=(0,0,1;0rad)
  Points = (2) [(0,0,0),(0,1.7,0)]
  Start = (186.4,-75.7,0)
  Subdivisions = 0
FEATURE [Part::Part2DObjectPython] Line1258  # Draft 2D object (typed FeaturePython)
  ChamferSize = 0
  Closed = false
  End = (183.5,-73.5,0)
  FilletRadius = 0
  Length = 2.4
  MakeFace = false
  Placement = pos=(185.9,-73.5,0) rot=(0,0,1;0rad)
  Points = (2) [(0,0,0),(-2.4,0,0)]
  Start = (185.9,-73.5,0)
  Subdivisions = 0
FEATURE [App::DocumentObjectGroup] Group071  label="Row 4 full"
  Group = -> [Group078,Group079,Line1245,Line1246,Line1247,Line1248,Line1249,Line1250,Arc653,Line1251,Line1252,Arc654,Line1253,Arc655,Arc656,Line1254,Line1255,Line1256,Line1257,Line1258]
FEATURE [App::DocumentObjectGroup] Group008  label="Switches"
  Group = -> [Group009,Group023,Group036,Group051,Group071]
FEATURE [App::DocumentObjectGroup] Group006  label="Switch layer 5mm"
  Group = -> [Group007,Group008,Group084,Group085]
FEATURE [App::DocumentObjectGroup] Group090  label="Middle"
  Group = -> [Group006,Group104]
